FCSTD DOCUMENT  (FreeCAD 0.22R37100 (Git))
Label: composit_stand11
License: All rights reserved
LicenseURL: http://en.wikipedia.org/wiki/All_rights_reserved
objects: Part::FeaturePython×178, Sketcher::SketchObject×145, PartDesign::SubShapeBinder×39, Part::Mirroring×36, Part::Compound×36, PartDesign::FeaturePython×35, PartDesign::CoordinateSystem×35, Part::Extrusion×31, TechDraw::DrawViewDimension×31, PartDesign::Body×29, PartDesign::Boolean×29, PartDesign::Pocket×27, PartDesign::Pad×25, TechDraw::DrawViewPart×22, App::DocumentObjectGroup×12, PartDesign::Mirrored×11, TechDraw::DrawPage×9, TechDraw::DrawViewBalloon×8, PartDesign::Plane×7, Part::Feature×7, +13 more types
note: 794 computed .brp shape members not serialized (recipe doc carries the construction recipe); baked Part::Feature solids carry a one-line shape summary decoded from their .brp
EXTERNAL_REF file=../module.FCStd obj=Sketch
EXTERNAL_REF file=../module.FCStd obj=Spreadsheet
EXTERNAL_REF file=../module.FCStd obj=Body
EXTERNAL_REF file=../dropper.FCStd obj=Connect
EXTERNAL_REF file=../dropper.FCStd obj=Sketch008
EXTERNAL_REF file=../dropper.FCStd obj=Sketch007
EXTERNAL_REF file=../ULZ-P02-14W.FCStd obj=Sketch
EXTERNAL_REF file=../hinge.FCStd obj=Sketch

FEATURE [PartDesign::SubShapeBinder] Binder
  BindCopyOnChange = 0
  BindMode = 0
  ClaimChildren = true
  Context = -> Body [Binder.]
  Fuse = false
  MakeFace = true
  OffsetFill = false
  OffsetIntersection = false
  OffsetJoinType = 0
  OffsetOpenResult = false
  PartialLoad = false
  Relative = false
  Support = -> [Connect]
  _Version = 2
FEATURE [PartDesign::FeaturePython] BaseBend  # WARN: FeaturePython — macro-defined, semantics opaque (R4)
  BendSide = 1
  BendSketch = -> Binder
  MidPlane = false
  Reverse = false
  Suppressed = false
  length = 1100
  radius = 0.1
  thickness = 0.3
  expr: length = <<Properties>>.modules_fix_height
FEATURE [App::Link] Link  label="module_holes"
  LinkedObject = -> <external ../module.FCStd>#Sketch
  expr: LinkedObject = module#<<module_holes>>._self
FEATURE [Part::FeaturePython] LinearArray  # WARN: FeaturePython — macro-defined, semantics opaque (R4)
  Alignment = 0
  CellStart = A1
  Count = 11
  Dir = (0,0,1)
  DirIsDriven = true
  DistributionLaw = 0
  DrivenProperty = 1
  EndInclusive = true
  ExposePlacement = false
  GeneratorMode = 1
  MarkerShape = 1
  MarkerSize = 0
  NumElements = 11
  OrientMode = 0
  Point = (0,0,0)
  PointIsDriven = true
  Reverse = false
  SpanEnd = 800
  SpanStart = 0
  Step = 80
  Type = lattice2LinearArray.LinearArray
  VSGVersion = 1
  Values = 0.0 | 80.0 | 160.0 | 240.0 | 320.0 | 400.0 | 480.0 | 560.0 | 640.0 | 720.0 | 800.0
  ValuesSource = 2
  isLattice = 1
  expr: Count = <<Properties>>.number_of_modules
  expr: SpanEnd = Step * (Count - 1)
FEATURE [Sketcher::SketchObject] Sketch003  label="modules_plasements"
  FullyConstrained = true
  expr: Constraints[27] = <<module>>#<<Properties>>.module_width + 2 mm
  sketch-geometry (12):
    g0: LineSegment StartX=1 StartY=0 StartZ=0 EndX=151 EndY=0 EndZ=0
    g1: LineSegment StartX=151 StartY=0 StartZ=0 EndX=151 EndY=36 EndZ=0
    g2: LineSegment StartX=151 StartY=36 StartZ=0 EndX=1 EndY=36 EndZ=0
    g3: LineSegment StartX=1 StartY=36 StartZ=0 EndX=1 EndY=0 EndZ=0
    g4: LineSegment StartX=175.08 StartY=8.76442 StartZ=0 EndX=289.987 EndY=105.183 EndZ=0
    g5: LineSegment StartX=289.987 StartY=105.183 StartZ=0 EndX=266.846 EndY=132.76 EndZ=0
    g6: LineSegment StartX=266.846 StartY=132.76 StartZ=0 EndX=151.94 EndY=36.342 EndZ=0
    g7: LineSegment StartX=151.94 StartY=36.342 StartZ=0 EndX=175.08 EndY=8.76442 EndZ=0
    g8: LineSegment StartX=151 StartY=36 StartZ=0 EndX=151.532 EndY=36 EndZ=0
    g9: LineSegment StartX=151.532 StartY=36 StartZ=0 EndX=151.94 EndY=36.342 EndZ=0
    g10: LineSegment StartX=151 StartY=0 StartZ=0 EndX=164.635 EndY=0 EndZ=0
    g11: LineSegment StartX=164.635 StartY=0 StartZ=0 EndX=175.08 EndY=8.76442 EndZ=0
  constraints (34):
    c: Coincident(g0,g1)
    c: Coincident(g1,g2)
    c: Coincident(g2,g3)
    c: Coincident(g3,g0)
    c: Horizontal(g0)
    c: Horizontal(g2)
    c: Vertical(g1)
    c: Vertical(g3)
    c: Coincident(g4,g5)
    c: Coincident(g5,g6)
    c: Coincident(g6,g7)
    c: Coincident(g7,g4)
    c: Parallel(g4,g6)
    c: Parallel(g5,g7)
    c: Perpendicular(g5,g4)
    c: Equal(g7,g1)
    c: Equal(g2,g6)
    c: Coincident(g1,g8)
    c: Coincident(g8,g9)
    c: Coincident(g9,g6)
    c: Coincident(g0,g10)
    c: Coincident(g10,g11)
    c: Coincident(g11,g4)
    c: Parallel(g9,g6)
    c: Equal(g9,g8)
    c: DistanceY(g3,g3) = 36
    c: Parallel(g11,g9)
    c: DistanceX(g2,g2) = 150
    c: DistanceX(g0) = 1
    c: Distance(g1,g6) = 1
    c: Angle(g4) = 0.698132
    c: Parallel(g10,g0)
    c: DistanceY(g0) = 0
    c: Horizontal(g8)
FEATURE [Sketcher::SketchObject] Sketch  label="base_Sketch"
  ExternalGeometry = -> [Sketch003]
  FullyConstrained = true
  Placement = pos=(0,20,0) rot=(0,0,1;0rad)
  expr: .Constraints.offset = .Placement.Base.y
  sketch-geometry (6):
    g0: LineSegment StartX=0 StartY=1.6e-15 StartZ=0 EndX=164.635 EndY=1.6e-15 EndZ=0
    g1: LineSegment StartX=164.635 StartY=1.6e-15 StartZ=0 EndX=319.563 EndY=130 EndZ=0
    g2: LineSegment StartX=151 StartY=-20 StartZ=0 EndX=164.635 EndY=-20 EndZ=0
    g3: LineSegment StartX=164.635 StartY=-20 StartZ=0 EndX=175.08 EndY=-11.2356 EndZ=0
    g4: GeomPoint X=157.818 Y=-20 Z=0
    g5: GeomPoint X=-164.635 Y=1.6e-15 Z=0
  constraints (19):
    c: Coincident(g0,g1)
    c: Horizontal(g0)
    c: Parallel(g1,g-3)
    c: Coincident(g-4,g2)
    c: Horizontal(g2)
    c: Coincident(g2,g3)
    c: Coincident(g3,g-3)
    c: Parallel(g3,g-3)
    c: Vertical(g2,g0)
    c: PointOnObject(g0,g-2)
    c: DistanceY(g-4,g0) = 20  'offset'
    c: Angle(g1) = 0.698132  'angle'
    c: Symmetric(g2,g2,g4)
    c: DistanceX(g4) = 157.818  'rivet_placement'
    c: Distance(g1) = 202.244  'side'
    c: Symmetric(g5,g0,g-2)
    c: Distance(g5,g0) = 329.27  'face'
    c: DistanceY(g-4,g1) = 150  'total_depth'
    c: DistanceY(g0,g1) = 130
FEATURE [Sketcher::SketchObject] Sketch001  label="side_Sketch"
  ExternalGeometry = -> [Sketch]
  FullyConstrained = true
  sketch-geometry (2):
    g0: LineSegment StartX=319.563 StartY=150 StartZ=0 EndX=319.563 EndY=150 EndZ=0
    g1: LineSegment StartX=319.563 StartY=150 StartZ=0 EndX=319.563 EndY=0 EndZ=0
  constraints (8):
    c: Coincident(g0,g-3)
    c: Horizontal(g0)
    c: Coincident(g1,g0)
    c: PointOnObject(g1,g-1)
    c: Vertical(g1)
    c: Distance(g1) = 150  'side'
    c: DistanceX(g0,g0) = 0  'front'
    c: DistanceX(g1) = 319.563  'distance'
FEATURE [Part::Mirroring] Part__Mirroring  label="base_Sketch (Mirror #1)"
  Base = (0,0,0)
  Normal = (1,0,0)
  Source = -> Sketch
FEATURE [Sketcher::SketchObject] Sketch002  label="mid_Sketch"
  ExternalGeometry = -> [Sketch]
  FullyConstrained = true
  sketch-geometry (2):
    g0: GeomPoint X=319.563 Y=150 Z=0
    g1: LineSegment StartX=2.71984e-11 StartY=0 StartZ=0 EndX=4.40357e-11 EndY=0 EndZ=0
  constraints (5):
    c: DistanceX(g0) = 319.563  'middle'
    c: Coincident(g1,g-1)
    c: PointOnObject(g1,g-1)
    c: DistanceX(g1,g1) = 0  'length'
    c: Coincident(g0,g-3)
FEATURE [Part::Compound] Compound
  Links = -> [Sketch001,Part__Mirroring,Sketch002,Sketch]
  Placement = pos=(319.563,0,0) rot=(0,0,1;0rad)
  expr: .Placement.Base.x = <<mid_Sketch>>.Constraints.middle
FEATURE [Part::Mirroring] Part__Mirroring001  label="Compound (Mirror #2)"
  Base = (0,0,0)
  Normal = (1,0,0)
  Source = -> Compound
  expr: Normal = <<base_Sketch (Mirror #1)>>.Normal
FEATURE [Part::FeaturePython] Connect  label="face_bend_base"  # WARN: FeaturePython — macro-defined, semantics opaque (R4)
  Objects = -> [Part__Mirroring001,Compound]
  Tolerance = 0
FEATURE [Sketcher::SketchObject] Sketch004
  ExternalGeometry = -> [Sketch003]
  FullyConstrained = false
  sketch-geometry (8):
    g0: LineSegment StartX=70.3141 StartY=-1e-16 StartZ=0 EndX=76 EndY=-1e-16 EndZ=0
    g1: LineSegment StartX=76 StartY=-1e-16 StartZ=0 EndX=76 EndY=53.1648 EndZ=0
    g2: LineSegment StartX=228.178 StartY=53.3186 StartZ=0 EndX=232.533 EndY=56.9735 EndZ=0
    g3: LineSegment StartX=232.533 StartY=56.9735 StartZ=0 EndX=198.36 EndY=97.7001 EndZ=0
    g4: LineSegment StartX=-236.889 StartY=60.6283 StartZ=0 EndX=-232.533 EndY=56.9735 EndZ=0
    g5: LineSegment StartX=-232.533 StartY=56.9735 StartZ=0 EndX=-198.36 EndY=97.7001 EndZ=0
    g6: LineSegment StartX=-81.6859 StartY=-1.2725e-12 StartZ=0 EndX=-76 EndY=-1.2724e-12 EndZ=0
    g7: LineSegment StartX=-76 StartY=-1.2724e-12 StartZ=0 EndX=-76 EndY=53.1648 EndZ=0
  constraints (21):
    c: Coincident(g0,g1)
    c: Vertical(g1)
    c: Coincident(g2,g3)
    c: Coincident(g4,g5)
    c: Coincident(g6,g7)
    c: Vertical(g7)
    c: Perpendicular(g5,g4)
    c: Perpendicular(g3,g2)
    c: Symmetric(g4,g2,g-2)
    c: Equal(g0,g2)
    c: Equal(g2,g6)
    c: Equal(g6,g4)
    c: Equal(g1,g3)
    c: Equal(g3,g7)
    c: Symmetric(g5,g3,g-2)
    c: Symmetric(g6,g0,g-2)
    c: Parallel(g2,g-4)
    c: Horizontal(g0)
    c: Symmetric(g-3,g-3,g0)
    c: Symmetric(g-4,g-4,g2)
    c: Perpendicular(g7,g6)
FEATURE [Part::FeaturePython] Placment  # WARN: FeaturePython — macro-defined, semantics opaque (R4)
  AttacherType = Attacher::AttachEngine3D
  ExposePlacement = true
  MapMode = 49
  MarkerShape = 1
  MarkerSize = 50
  NumElements = 1
  Placement = pos=(76,0,0) rot=(0,0,1;0rad)
  Type = lattice2AttachablePlacement.AttachablePlacement
  isLattice = 1
FEATURE [Part::FeaturePython] PlacementSubsequence  # WARN: FeaturePython — macro-defined, semantics opaque (R4)
  Base = -> Placment
  CycleMode = 0
  ExposePlacement = false
  MarkerShape = 1
  MarkerSize = 0
  NumElements = 4
  Type = lattice2AttachablePlacement.AttachedPlacementSubsequence
  isLattice = 1
FEATURE [Part::FeaturePython] LinearArray001  label="sections_LinearArray"  # WARN: FeaturePython — macro-defined, semantics opaque (R4)
  Alignment = 0
  CellStart = A1
  Count = 5
  Dir = (1,0,0)
  DirIsDriven = true
  DistributionLaw = 0
  DrivenProperty = 1
  EndInclusive = true
  ExposePlacement = false
  GeneratorMode = 0
  MarkerShape = 1
  MarkerSize = 0
  NumElements = 2
  OrientMode = 1
  Point = (0,0,0)
  PointIsDriven = true
  Reverse = false
  SpanEnd = 500
  SpanStart = 0
  Step = 125
  Type = lattice2LinearArray.LinearArray
  VSGVersion = 1
  Values = -319.562984 | 319.562984
  ValuesSource = 0
  isLattice = 1
  expr: Values = list(<<%f>> % (-<<mid_Sketch>>.Constraints.middle / 1 mm); <<%f>> % (<<mid_Sketch>>.Constraints.middle / 1 mm))
FEATURE [Part::FeaturePython] Populate  label="Populate LinearArray001 with PlacementSubsequence"  # WARN: FeaturePython — macro-defined, semantics opaque (R4)
  Copying = 0
  ExposePlacement = false
  MarkerShape = 1
  MarkerSize = 0
  NumElements = 8
  Object = -> PlacementSubsequence
  OutputCompounding = 0
  Placement = pos=(0,20,0) rot=(0,0,1;0rad)
  PlacementsTo = -> LinearArray001
  Referencing = 0
  Type = lattice2PopulateCopies.LatticePopulateCopies
  isLattice = 1
  expr: .Placement.Base.y = <<base_Sketch>>.Constraints.offset
FEATURE [Part::FeaturePython] Populate001  label="Populate LinearArray with Populate LinearArray001 with PlacementSubsequence"  # WARN: FeaturePython — macro-defined, semantics opaque (R4)
  Copying = 0
  ExposePlacement = false
  MarkerShape = 1
  MarkerSize = 0
  NumElements = 88
  Object = -> Populate
  OutputCompounding = 0
  PlacementsTo = -> LinearArray
  Referencing = 0
  Type = lattice2PopulateCopies.LatticePopulateCopies
  isLattice = 1
FEATURE [Part::FeaturePython] Placment001  label="Custom"  # WARN: FeaturePython — macro-defined, semantics opaque (R4)
  ExposePlacement = true
  FlipZ = false
  Invert = false
  MarkerShape = 1
  MarkerSize = 20
  NumElements = 1
  Placement = pos=(0,0,0) rot=(0,0.707107,0.707107;3.14159rad)
  PlacementChoice = 0
  Type = lattice2Placement.LatticePlacement
  isLattice = 1
FEATURE [Part::FeaturePython] Populate002  label="Populate Populate LinearArray with Populate LinearArray001 with PlacementSubsequence with Custom"  # WARN: FeaturePython — macro-defined, semantics opaque (R4)
  Copying = 0
  ExposePlacement = false
  MarkerShape = 1
  MarkerSize = 0
  NumElements = 88
  Object = -> Placment001
  OutputCompounding = 0
  Placement = pos=(0,0,280) rot=(0,0,1;0rad)
  PlacementsTo = -> Populate001
  Referencing = 0
  Type = lattice2PopulateCopies.LatticePopulateCopies
  isLattice = 1
  expr: .Placement.Base.z = <<Properties>>.bottom_cut_height + <<Properties>>.sink_height + module#<<Properties>>.module_height
FEATURE [App::Link] Link001  label="module_Body"
  LinkedObject = -> <external ../module.FCStd>#Body
  expr: LinkedObject = module#<<module_Body>>._self
FEATURE [Part::Extrusion] Extrude
  Base = -> Link
  Dir = (0,0,1)
  DirMode = 2
  FaceMakerClass = Part::FaceMakerBullseye
  LengthFwd = 10
  LengthRev = 0
  Reversed = true
  Solid = true
  Symmetric = false
FEATURE [Part::FeaturePython] Populate004  label="face_modules_fix"  # WARN: FeaturePython — macro-defined, semantics opaque (R4)
  Copying = 0
  ExposePlacement = false
  MarkerShape = 1
  MarkerSize = 0
  NumElements = 0
  Object = -> Extrude
  OutputCompounding = 1
  PlacementsTo = -> Populate002
  Referencing = 0
  Type = lattice2PopulateCopies.LatticePopulateCopies
  isLattice = 0
FEATURE [PartDesign::Body] Body001  label="dummy_body"
  Origin = -> Origin001
FEATURE [Spreadsheet::Sheet] Spreadsheet  label="Properties"
  cells = B2(modules_fix_height)==modules_height + modules_to_droppers + bottom_cut_height + sink_height; C2(total_height)==modules_fix_height + cap_height; D2(number_of_modules)=11; E2(modules_height)==module#<<Properties>>.module_fixture_distance_y * (number_of_modules - 1) + module#<<Properties>>.module_height; F2(modules_to_droppers)==20 mm; G2(bottom_cut_height)==100 mm; H2(sink_height)==20 mm; I2(cap_height)==40 mm
FEATURE [PartDesign::SubShapeBinder] Binder001
  BindCopyOnChange = 0
  BindMode = 0
  ClaimChildren = true
  Context = -> Body003 [Binder001.]
  Fuse = false
  MakeFace = true
  OffsetFill = false
  OffsetIntersection = false
  OffsetJoinType = 0
  OffsetOpenResult = false
  PartialLoad = false
  Relative = false
  Support = -> [Sketch]
  _Version = 2
FEATURE [PartDesign::CoordinateSystem] Local_CS
  AttacherType = Attacher::AttachEngine3D
  AttachmentOffset = pos=(0,0,0) rot=(0,1,0;1.5708rad)
  MapMode = 7
  Placement = pos=(164.635,-1.4e-14,0) rot=(0.889126,0.323616,0.323616;1.68804rad)
FEATURE [Sketcher::SketchObject] Sketch005  label="sink_side_line"
  ExternalGeometry = -> [Binder001]
  FullyConstrained = true
  MapMode = 5
  Placement = pos=(164.635,-2.8e-14,0) rot=(0.889126,0.323616,0.323616;1.68804rad)
  sketch-geometry (1):
    g0: LineSegment StartX=-2.84e-14 StartY=0 StartZ=0 EndX=202.244 EndY=20 EndZ=0
  constraints (4):
    c: Coincident(g0,g-3)
    c: Vertical(g0,g-3)
    c: DistanceY(g0) = 20  'height'
    c: Angle(g0) = 0.0985699  'angle'
FEATURE [Sketcher::SketchObject] Sketch006  label="sink_front_bend_sketch"
  ExternalGeometry = -> [Sketch005]
  FullyConstrained = true
  MapMode = 5
  Placement = pos=(0,0,0) rot=(0.57735,0.57735,0.57735;2.0944rad)
  sketch-geometry (3):
    g0: LineSegment StartX=0 StartY=2.91403 StartZ=0 EndX=-1.83e-14 EndY=0 EndZ=0
    g1: LineSegment StartX=-1.83e-14 StartY=0 StartZ=0 EndX=2.88014 EndY=0.443099 EndZ=0
    g2: ArcOfCircle CenterX=2.5 CenterY=2.91403 CenterZ=0 NormalX=0 NormalY=0 NormalZ=1 AngleXU=0 Radius=2.5 StartAngle=3.14159 EndAngle=4.86504
  constraints (8):
    c: PointOnObject(g0,g-2)
    c: Coincident(g0,g-3)
    c: Coincident(g0,g1)
    c: PointOnObject(g1,g-3)
    c: Tangent(g2,g1) = -1.5708
    c: Tangent(g2,g0) = -1.5708
    c: Radius(g2) = 2.5
    c: Angle(g1) = 0.152649  'angle'
FEATURE [Sketcher::SketchObject] Sketch007
  ExternalGeometry = -> [Binder001]
  FullyConstrained = true
  MapMode = 7
  Placement = pos=(164.635,-8.5e-14,-4e-15) rot=(0.846388,-0.394677,-0.357572;1.83324rad)
  sketch-geometry (3):
    g0: ArcOfCircle CenterX=-2.5 CenterY=2.81034 CenterZ=0 NormalX=0 NormalY=0 NormalZ=1 AngleXU=0 Radius=2.5 StartAngle=4.59564 EndAngle=6.28319
    g1: LineSegment StartX=-2.79121 StartY=0.327355 StartZ=0 EndX=0 EndY=0 EndZ=0
    g2: LineSegment StartX=0 StartY=0 StartZ=0 EndX=0 EndY=2.81034 EndZ=0
  constraints (7):
    c: PointOnObject(g0,g-2)
    c: Coincident(g1,g-1)
    c: Coincident(g2,g1)
    c: Tangent(g2,g0) = -1.5708
    c: Tangent(g1,g0) = -1.5708
    c: PointOnObject(g0,g-3)
    c: Radius(g0) = 2.5
FEATURE [PartDesign::CoordinateSystem] Local_CS001
  AttacherType = Attacher::AttachEngine3D
  AttachmentOffset = pos=(0,0,0) rot=(1,0,0;0.152649rad)
  MapMode = 5
  Placement = pos=(0,0,0) rot=(1,0,0;0.152649rad)
  expr: .AttachmentOffset.Rotation.Angle = <<sink_front_bend_sketch>>.Constraints.angle
FEATURE [Sketcher::SketchObject] Sketch008  label="sink_plane_sketch"
  ExternalGeometry = -> [Sketch006,Sketch005,Sketch007]
  FullyConstrained = true
  MapMode = 5
  Placement = pos=(0,0,0) rot=(1,0,0;0.152649rad)
  sketch-geometry (4):
    g0: LineSegment StartX=-163.725 StartY=2.91403 StartZ=0 EndX=163.725 EndY=2.91403 EndZ=0
    g1: LineSegment StartX=163.725 StartY=2.91403 StartZ=0 EndX=317.576 EndY=133.529 EndZ=0
    g2: LineSegment StartX=317.576 StartY=133.529 StartZ=0 EndX=-317.576 EndY=133.529 EndZ=0
    g3: LineSegment StartX=-317.576 StartY=133.529 StartZ=0 EndX=-163.725 EndY=2.91403 EndZ=0
  constraints (14):
    c: Coincident(g0,g1)
    c: Coincident(g1,g2)
    c: Coincident(g2,g3)
    c: Coincident(g3,g0)
    c: Symmetric(g0,g0,g-2)
    c: Symmetric(g2,g1,g-2)
    c: Parallel(g1,g-4)
    c: PointOnObject(g-5,g1)
    c: PointOnObject(g-3,g0)
    c: Distance(g1) = 201.818  'rigth_side'
    c: Distance(g0) = 327.45  'front'
    c: Distance(g2) = 635.153  'end'
    c: Distance(g3) = 201.818  'left_side'
    c: DistanceY(g-4,g1) = 2
FEATURE [Sketcher::SketchObject] Sketch009
  ExternalGeometry = -> [Sketch006]
  FullyConstrained = true
  MapMode = 2
  Placement = pos=(0,0,0) rot=(0.57735,0.57735,0.57735;2.0944rad)
  sketch-geometry (4):
    g0: ArcOfCircle CenterX=2.5 CenterY=2.91403 CenterZ=0 NormalX=0 NormalY=0 NormalZ=1 AngleXU=0 Radius=2.5 StartAngle=3.14159 EndAngle=4.86504
    g1: LineSegment StartX=2.88014 StartY=0.443099 StartZ=0 EndX=2.80411 EndY=0.937285 EndZ=0
    g2: LineSegment StartX=1.1302e-12 StartY=2.91403 StartZ=0 EndX=0.5 EndY=2.91403 EndZ=0
    g3: ArcOfCircle CenterX=2.5 CenterY=2.91403 CenterZ=0 NormalX=0 NormalY=0 NormalZ=1 AngleXU=0 Radius=2 StartAngle=3.14159 EndAngle=4.86504
  constraints (10):
    c: Coincident(g0,g-3)
    c: Tangent(g0,g-3) = -1.5708
    c: Coincident(g0,g1)
    c: Coincident(g0,g2)
    c: Coincident(g3,g0)
    c: Coincident(g3,g2)
    c: Coincident(g3,g1)
    c: Perpendicular(g3,g1)
    c: Perpendicular(g3,g2)
    c: Distance(g1) = 0.5
FEATURE [Sketcher::SketchObject] Sketch010
  ExternalGeometry = -> [Sketch007]
  FullyConstrained = true
  MapMode = 7
  Placement = pos=(163.725,2.88014,0.443099) rot=(0.846388,-0.394677,-0.357572;1.83324rad)
  sketch-geometry (4):
    g0: ArcOfCircle CenterX=0.291206 CenterY=2.48298 CenterZ=0 NormalX=0 NormalY=0 NormalZ=1 AngleXU=0 Radius=2.5 StartAngle=4.59564 EndAngle=6.28319
    g1: LineSegment StartX=-2.56e-14 StartY=2.7e-15 StartZ=0 EndX=0.0582413 EndY=0.496596 EndZ=0
    g2: LineSegment StartX=2.79121 StartY=2.48298 StartZ=0 EndX=2.29121 EndY=2.48298 EndZ=0
    g3: ArcOfCircle CenterX=0.291206 CenterY=2.48298 CenterZ=0 NormalX=0 NormalY=0 NormalZ=1 AngleXU=0 Radius=2 StartAngle=4.59564 EndAngle=6.28319
  constraints (10):
    c: Coincident(g0,g-3)
    c: Tangent(g0,g-3) = -1.5708
    c: Coincident(g1,g0)
    c: Coincident(g2,g0)
    c: Coincident(g3,g0)
    c: Coincident(g3,g1)
    c: Coincident(g3,g2)
    c: Perpendicular(g0,g1)
    c: Perpendicular(g0,g2)
    c: Distance(g1) = 0.5
FEATURE [Sketcher::SketchObject] Sketch011
  ExternalGeometry = -> [Sketch008]
  FullyConstrained = true
  MapMode = 7
  Placement = pos=(-163.725,2.88014,0.443099) rot=(-0.298783,0.640743,0.707232;3.7787rad)
  sketch-geometry (4):
    g0: ArcOfCircle CenterX=0.291206 CenterY=2.48298 CenterZ=0 NormalX=0 NormalY=0 NormalZ=1 AngleXU=0 Radius=2 StartAngle=4.59564 EndAngle=6.28319
    g1: ArcOfCircle CenterX=0.291206 CenterY=2.48298 CenterZ=0 NormalX=0 NormalY=0 NormalZ=1 AngleXU=0 Radius=2.5 StartAngle=4.59564 EndAngle=6.28319
    g2: LineSegment StartX=-4e-16 StartY=0 StartZ=0 EndX=0.0582413 EndY=0.496596 EndZ=0
    g3: LineSegment StartX=2.29121 StartY=2.48298 StartZ=0 EndX=2.79121 EndY=2.48298 EndZ=0
  constraints (12):
    c: Coincident(g1,g0)
    c: Coincident(g1,g-1)
    c: Coincident(g2,g1)
    c: Coincident(g2,g0)
    c: Coincident(g3,g0)
    c: Coincident(g3,g1)
    c: Perpendicular(g0,g3)
    c: Perpendicular(g0,g2)
    c: Perpendicular(g2,g-3)
    c: Horizontal(g3)
    c: Radius(g0) = 2
    c: Distance(g2) = 0.5
FEATURE [PartDesign::Pad] Pad
  Direction = (0,-0.152057,0.988372)
  Length = 0.5
  Length2 = 10
  Placement = pos=(0,0,0) rot=(1,0,0;0.152649rad)
  Profile = -> Sketch008
  ReferenceAxis = -> Sketch008 [N_Axis]
  Suppressed = false
  Type = 0
FEATURE [PartDesign::Pad] Pad001
  BaseFeature = -> Pad
  Direction = (-0.762326,-0.639667,-0.0984104)
  Length = 201.818
  Length2 = 10
  Placement = pos=(0,0,0) rot=(1,0,0;0.152649rad)
  Profile = -> Sketch010
  ReferenceAxis = -> Sketch010 [N_Axis]
  Reversed = true
  Suppressed = false
  Type = 0
  expr: Length = <<sink_plane_sketch>>.Constraints.rigth_side
FEATURE [PartDesign::Pad] Pad002
  BaseFeature = -> Pad001
  Direction = (-0.762326,0.639667,0.0984104)
  Length = 201.818
  Length2 = 10
  Placement = pos=(0,0,0) rot=(1,0,0;0.152649rad)
  Profile = -> Sketch011
  ReferenceAxis = -> Sketch011 [N_Axis]
  Suppressed = false
  Type = 0
  expr: Length = <<sink_plane_sketch>>.Constraints.left_side
FEATURE [PartDesign::Pad] Pad003
  BaseFeature = -> Pad002
  Direction = (1,0,0)
  Length = 327.45
  Length2 = 10
  Midplane = true
  Placement = pos=(0,0,0) rot=(1,0,0;0.152649rad)
  Profile = -> Sketch009
  ReferenceAxis = -> Sketch009 [N_Axis]
  Suppressed = false
  Type = 0
  expr: Length = <<sink_plane_sketch>>.Constraints.front
FEATURE [Sketcher::SketchObject] Sketch013
  ExternalGeometry = -> [Sketch008,Sketch009]
  FullyConstrained = true
  MapMode = 5
  Placement = pos=(0,0,0) rot=(1,0,0;1.5708rad)
  sketch-geometry (6):
    g0: LineSegment StartX=-163.725 StartY=2.91403 StartZ=0 EndX=-163.725 EndY=80 EndZ=0
    g1: LineSegment StartX=-163.725 StartY=80 StartZ=0 EndX=163.725 EndY=80 EndZ=0
    g2: LineSegment StartX=163.725 StartY=80 StartZ=0 EndX=163.725 EndY=2.91403 EndZ=0
    g3: LineSegment StartX=163.725 StartY=2.91403 StartZ=0 EndX=-163.725 EndY=2.91403 EndZ=0
    g4: LineSegment StartX=-163.725 StartY=0.443099 StartZ=0 EndX=-163.725 EndY=2.91403 EndZ=0
    g5: LineSegment StartX=163.725 StartY=0.443099 StartZ=0 EndX=163.725 EndY=2.91403 EndZ=0
  constraints (16):
    c: Vertical(g0)
    c: Coincident(g0,g1)
    c: Horizontal(g1)
    c: Coincident(g1,g2)
    c: Vertical(g2)
    c: Coincident(g2,g3)
    c: Coincident(g3,g0)
    c: Horizontal(g3)
    c: PointOnObject(g-4,g3)
    c: Coincident(g4,g-3)
    c: Coincident(g4,g0)
    c: Perpendicular(g3,g4)
    c: Coincident(g5,g-3)
    c: Coincident(g5,g2)
    c: Perpendicular(g3,g5)
    c: DistanceY(g1) = 80
FEATURE [Sketcher::SketchObject] Sketch012
  ExternalGeometry = -> [Sketch008,Sketch010,Sketch013]
  FullyConstrained = true
  MapMode = 5
  Placement = pos=(164.635,-2.8e-14,0) rot=(0.889126,0.323616,0.323616;1.68804rad)
  sketch-geometry (4):
    g0: LineSegment StartX=0.909926 StartY=2.91403 StartZ=0 EndX=201.749 EndY=22.775 EndZ=0
    g1: LineSegment StartX=0.909926 StartY=2.91403 StartZ=0 EndX=0.909926 EndY=80 EndZ=0
    g2: LineSegment StartX=0.909926 StartY=80 StartZ=0 EndX=201.749 EndY=80 EndZ=0
    g3: LineSegment StartX=201.749 StartY=80 StartZ=0 EndX=201.749 EndY=22.775 EndZ=0
  constraints (11):
    c: Coincident(g0,g-4)
    c: Parallel(g-3,g0)
    c: Equal(g0,g-3)
    c: Coincident(g0,g1)
    c: Vertical(g1)
    c: Coincident(g1,g2)
    c: Horizontal(g2)
    c: Coincident(g2,g3)
    c: Coincident(g3,g0)
    c: Vertical(g3)
    c: Horizontal(g-5,g1)
FEATURE [PartDesign::Pad] Pad004
  BaseFeature = -> Pad003
  Direction = (0,-1,2e-16)
  Length = 0.5
  Length2 = 10
  Placement = pos=(0,0,0) rot=(1,0,0;0.152649rad)
  Profile = -> Sketch013
  ReferenceAxis = -> Sketch013 [N_Axis]
  Reversed = true
  Suppressed = false
  Type = 0
FEATURE [PartDesign::Pad] Pad005
  BaseFeature = -> Pad004
  Direction = (0.642788,-0.766044,0)
  Length = 0.5
  Length2 = 10
  Placement = pos=(0,0,0) rot=(1,0,0;0.152649rad)
  Profile = -> Sketch012
  ReferenceAxis = -> Sketch012 [N_Axis]
  Reversed = true
  Suppressed = false
  Type = 0
FEATURE [Sketcher::SketchObject] Sketch014
  ExternalGeometry = -> [Binder001]
  FullyConstrained = true
  MapMode = 5
  sketch-geometry (1):
    g0: LineSegment StartX=-319.563 StartY=130 StartZ=0 EndX=-164.635 EndY=0 EndZ=0
  constraints (2):
    c: Symmetric(g0,g-3,g-2)
    c: Symmetric(g0,g-3,g-2)
FEATURE [PartDesign::CoordinateSystem] Local_CS003
  AttacherType = Attacher::AttachEngine3D
  AttachmentOffset = pos=(0,0,0) rot=(0,1,0;1.5708rad)
  MapMode = 7
  Placement = pos=(-164.635,-1.4e-14,0) rot=(0.889126,-0.323616,-0.323616;1.68804rad)
FEATURE [Sketcher::SketchObject] Sketch015
  ExternalGeometry = -> [Sketch008,Sketch011,Sketch013]
  FullyConstrained = true
  MapMode = 5
  Placement = pos=(-164.635,-2.8e-14,0) rot=(0.889126,-0.323616,-0.323616;1.68804rad)
  sketch-geometry (5):
    g0: LineSegment StartX=-201.749 StartY=22.775 StartZ=0 EndX=-0.909926 EndY=2.91403 EndZ=0
    g1: LineSegment StartX=-0.909926 StartY=2.91403 StartZ=0 EndX=-0.909926 EndY=80 EndZ=0
    g2: LineSegment StartX=-0.909926 StartY=80 StartZ=0 EndX=-201.749 EndY=80 EndZ=0
    g3: LineSegment StartX=-201.749 StartY=80 StartZ=0 EndX=-201.749 EndY=22.775 EndZ=0
    g4: LineSegment StartX=-201.993 StartY=20.3041 StartZ=0 EndX=-201.749 EndY=22.775 EndZ=0
  constraints (13):
    c: Coincident(g0,g-4)
    c: Coincident(g1,g0)
    c: Vertical(g1)
    c: Coincident(g1,g2)
    c: Horizontal(g2)
    c: Coincident(g2,g3)
    c: Coincident(g3,g0)
    c: Vertical(g3)
    c: Coincident(g4,g-3)
    c: Coincident(g4,g0)
    c: Perpendicular(g-3,g4)
    c: Parallel(g-3,g0)
    c: Horizontal(g1,g-5)
FEATURE [PartDesign::Pad] Pad006
  BaseFeature = -> Pad005
  Direction = (-0.642788,-0.766044,0)
  Length = 0.5
  Length2 = 10
  Placement = pos=(0,0,0) rot=(1,0,0;0.152649rad)
  Profile = -> Sketch015
  ReferenceAxis = -> Sketch015 [N_Axis]
  Reversed = true
  Suppressed = false
  Type = 0
FEATURE [Sketcher::SketchObject] Sketch016
  ExternalGeometry = -> [Pad006]
  FullyConstrained = true
  MapMode = 5
  Placement = pos=(0,0,0) rot=(1,0,0;0.152649rad)
  sketch-geometry (28):
    g0: LineSegment StartX=0 StartY=2 StartZ=0 EndX=40.9313 EndY=2 EndZ=0
    g1: LineSegment StartX=40.9313 StartY=2 StartZ=0 EndX=81.8625 EndY=2 EndZ=0
    g2: LineSegment StartX=81.8625 StartY=2 StartZ=0 EndX=122.794 EndY=2 EndZ=0
    g3: LineSegment StartX=122.794 StartY=2 StartZ=0 EndX=163.725 EndY=2 EndZ=0
    g4: ArcOfCircle CenterX=-17 CenterY=2 CenterZ=0 NormalX=0 NormalY=0 NormalZ=1 AngleXU=0 Radius=3 StartAngle=1.5708 EndAngle=4.71239
    g5: ArcOfCircle CenterX=17 CenterY=2 CenterZ=0 NormalX=0 NormalY=0 NormalZ=1 AngleXU=0 Radius=3 StartAngle=4.71239 EndAngle=7.85398
    g6: LineSegment StartX=-17 StartY=5 StartZ=0 EndX=17 EndY=5 EndZ=0
    g7: LineSegment StartX=-17 StartY=-1 StartZ=0 EndX=17 EndY=-1 EndZ=0
    g8: GeomPoint X=-20 Y=2 Z=0
    g9: GeomPoint X=20 Y=2 Z=0
    g10: ArcOfCircle CenterX=106 CenterY=2 CenterZ=0 NormalX=0 NormalY=0 NormalZ=1 AngleXU=0 Radius=3 StartAngle=1.5708 EndAngle=4.71239
    g11: ArcOfCircle CenterX=140 CenterY=2 CenterZ=0 NormalX=0 NormalY=0 NormalZ=1 AngleXU=0 Radius=3 StartAngle=4.71239 EndAngle=7.85398
    g12: LineSegment StartX=106 StartY=5 StartZ=0 EndX=140 EndY=5 EndZ=0
    g13: LineSegment StartX=106 StartY=-1 StartZ=0 EndX=140 EndY=-1 EndZ=0
    g14: ArcOfCircle CenterX=-140 CenterY=2 CenterZ=0 NormalX=0 NormalY=0 NormalZ=1 AngleXU=0 Radius=3 StartAngle=1.5708 EndAngle=4.71239
    g15: ArcOfCircle CenterX=-106 CenterY=2 CenterZ=0 NormalX=0 NormalY=0 NormalZ=1 AngleXU=0 Radius=3 StartAngle=4.71239 EndAngle=7.85398
    g16: LineSegment StartX=-140 StartY=5 StartZ=0 EndX=-106 EndY=5 EndZ=0
    g17: LineSegment StartX=-140 StartY=-1 StartZ=0 EndX=-106 EndY=-1 EndZ=0
    g18: ArcOfCircle CenterX=-78.5 CenterY=2 CenterZ=0 NormalX=0 NormalY=0 NormalZ=1 AngleXU=0 Radius=3 StartAngle=1.5708 EndAngle=4.71239
    g19: ArcOfCircle CenterX=-44.5 CenterY=2 CenterZ=0 NormalX=0 NormalY=0 NormalZ=1 AngleXU=0 Radius=3 StartAngle=4.71239 EndAngle=7.85398
    g20: LineSegment StartX=-78.5 StartY=5 StartZ=0 EndX=-44.5 EndY=5 EndZ=0
    g21: LineSegment StartX=-78.5 StartY=-1 StartZ=0 EndX=-44.5 EndY=-1 EndZ=0
    g22: ArcOfCircle CenterX=44.5 CenterY=2 CenterZ=0 NormalX=0 NormalY=0 NormalZ=1 AngleXU=0 Radius=3 StartAngle=1.5708 EndAngle=4.71239
    g23: ArcOfCircle CenterX=78.5 CenterY=2 CenterZ=0 NormalX=0 NormalY=0 NormalZ=1 AngleXU=0 Radius=3 StartAngle=4.71239 EndAngle=7.85398
    g24: LineSegment StartX=44.5 StartY=5 StartZ=0 EndX=78.5 EndY=5 EndZ=0
    g25: LineSegment StartX=44.5 StartY=-1 StartZ=0 EndX=78.5 EndY=-1 EndZ=0
    g26: LineSegment StartX=17 StartY=-1 StartZ=0 EndX=44.5 EndY=-1 EndZ=0
    g27: LineSegment StartX=78.5 StartY=-1 StartZ=0 EndX=106 EndY=-1 EndZ=0
  constraints (67):
    c: PointOnObject(g0,g-2)
    c: Coincident(g0,g1)
    c: Horizontal(g1)
    c: Coincident(g1,g2)
    c: Coincident(g2,g3)
    c: Horizontal(g3)
    c: Vertical(g-3,g3)
    c: Horizontal(g0)
    c: Equal(g0,g1)
    c: Equal(g1,g2)
    c: Equal(g2,g3)
    c: DistanceY(g0) = 2
    c: Horizontal(g2)
    c: Tangent(g4,g6) = 1.5708
    c: Tangent(g4,g7) = -1.5708
    c: Tangent(g5,g6) = 1.5708
    c: Tangent(g5,g7) = -1.5708
    c: Equal(g4,g5)
    c: PointOnObject(g5,g0)
    c: Symmetric(g4,g5,g-2)
    c: Radius(g5) = 3
    c: PointOnObject(g8,g4)
    c: PointOnObject(g9,g5)
    c: Horizontal(g9,g8)
    c: Horizontal(g8,g0)
    c: DistanceX(g8,g9) = 40
    c: Tangent(g10,g12) = 1.5708
    c: Tangent(g10,g13) = -1.5708
    c: Tangent(g11,g12) = 1.5708
    c: Tangent(g11,g13) = -1.5708
    c: Equal(g10,g11)
    c: Tangent(g14,g16) = 1.5708
    c: Tangent(g14,g17) = -1.5708
    c: Tangent(g15,g16) = 1.5708
    c: Tangent(g15,g17) = -1.5708
    c: Equal(g14,g15)
    c: Tangent(g18,g20) = 1.5708
    c: Tangent(g18,g21) = -1.5708
    c: Tangent(g19,g20) = 1.5708
    c: Tangent(g19,g21) = -1.5708
    c: Equal(g18,g19)
    c: Tangent(g22,g24) = 1.5708
    c: Tangent(g22,g25) = -1.5708
    c: Tangent(g23,g24) = 1.5708
    c: Tangent(g23,g25) = -1.5708
    c: Equal(g22,g23)
    c: Horizontal(g14,g15)
    c: Horizontal(g18,g19)
    c: Horizontal(g22,g23)
    c: Horizontal(g10,g11)
    c: Equal(g11,g23)
    c: Equal(g23,g5)
    c: Equal(g5,g19)
    c: Equal(g19,g15)
    c: Equal(g16,g20)
    c: Equal(g20,g6)
    c: Equal(g6,g24)
    c: Equal(g12,g24)
    c: Horizontal(g10,g22)
    c: Symmetric(g19,g22,g-2)
    c: Symmetric(g10,g15,g-2)
    c: Tangent(g26,g5) = -1.5708
    c: Coincident(g26,g22)
    c: Coincident(g27,g23)
    c: Coincident(g27,g10)
    c: Equal(g26,g27)
    c: DistanceX(g11) = 140
FEATURE [PartDesign::FeaturePython] SketchOnSheet  # WARN: FeaturePython — macro-defined, semantics opaque (R4)
  BaseFeature = -> Pad006
  Sketch = -> Sketch016
  Suppressed = false
  baseObject = -> Pad006 [Face14]
  kfactor = 0.5
FEATURE [PartDesign::FeaturePython] CornerRelief  # WARN: FeaturePython — macro-defined, semantics opaque (R4)
  BaseFeature = -> SketchOnSheet
  ReliefSketch = 0
  Size = 5
  SizeRatio = 1
  Suppressed = false
  XOffset = 0
  YOffset = 0
  baseObject = -> SketchOnSheet [Edge56,Edge57]
  kfactor = 0.5
FEATURE [PartDesign::FeaturePython] CornerRelief001  # WARN: FeaturePython — macro-defined, semantics opaque (R4)
  BaseFeature = -> CornerRelief
  ReliefSketch = 0
  Size = 5
  SizeRatio = 1
  Suppressed = false
  XOffset = 0
  YOffset = 0
  baseObject = -> CornerRelief [Edge17,Edge14]
  kfactor = 0.5
  expr: Size = <<CornerRelief>>.Size
FEATURE [Sketcher::SketchObject] Sketch017
  ExternalGeometry = -> [Sketch012]
  FullyConstrained = true
  MapMode = 5
  Placement = pos=(164.635,-2.8e-14,0) rot=(0.889126,0.323616,0.323616;1.68804rad)
  sketch-geometry (6):
    g0: LineSegment StartX=0.909926 StartY=78 StartZ=0 EndX=0.909926 EndY=80 EndZ=0
    g1: LineSegment StartX=0.909926 StartY=80 StartZ=0 EndX=2.90993 EndY=80 EndZ=0
    g2: LineSegment StartX=199.749 StartY=80 StartZ=0 EndX=201.749 EndY=80 EndZ=0
    g3: LineSegment StartX=201.749 StartY=80 StartZ=0 EndX=201.749 EndY=78 EndZ=0
    g4: ArcOfCircle CenterX=2.90993 CenterY=78 CenterZ=0 NormalX=0 NormalY=0 NormalZ=1 AngleXU=0 Radius=2 StartAngle=1.5708 EndAngle=3.14159
    g5: ArcOfCircle CenterX=199.749 CenterY=78 CenterZ=0 NormalX=0 NormalY=0 NormalZ=1 AngleXU=0 Radius=2 StartAngle=5.856e-13 EndAngle=1.5708
  constraints (14):
    c: Coincident(g0,g-3)
    c: Vertical(g0)
    c: Coincident(g0,g1)
    c: PointOnObject(g1,g-3)
    c: Coincident(g2,g-3)
    c: Coincident(g2,g3)
    c: Tangent(g5,g3) = 1.5708
    c: Tangent(g5,g2) = 1.5708
    c: Tangent(g4,g1) = 1.5708
    c: Tangent(g4,g0) = 1.5708
    c: Equal(g4,g5)
    c: Radius(g5) = 2
    c: Vertical(g3)
    c: PointOnObject(g2,g-3)
FEATURE [Sketcher::SketchObject] Sketch018
  ExternalGeometry = -> [Sketch015]
  FullyConstrained = true
  MapMode = 2
  Placement = pos=(-164.635,-2.8e-14,0) rot=(0.889126,-0.323616,-0.323616;1.68804rad)
  sketch-geometry (6):
    g0: ArcOfCircle CenterX=-2.90993 CenterY=78 CenterZ=0 NormalX=0 NormalY=0 NormalZ=1 AngleXU=0 Radius=2 StartAngle=6.28318 EndAngle=7.85398
    g1: ArcOfCircle CenterX=-199.749 CenterY=78 CenterZ=0 NormalX=0 NormalY=0 NormalZ=1 AngleXU=0 Radius=2 StartAngle=1.5708 EndAngle=3.14159
    g2: LineSegment StartX=-201.749 StartY=78 StartZ=0 EndX=-201.749 EndY=80 EndZ=0
    g3: LineSegment StartX=-201.749 StartY=80 StartZ=0 EndX=-199.749 EndY=80 EndZ=0
    g4: LineSegment StartX=-2.90993 StartY=80 StartZ=0 EndX=-0.909926 EndY=80 EndZ=0
    g5: LineSegment StartX=-0.909926 StartY=80 StartZ=0 EndX=-0.909926 EndY=78 EndZ=0
  constraints (15):
    c: PointOnObject(g1,g-3)
    c: Coincident(g2,g3)
    c: Vertical(g2)
    c: Tangent(g1,g2) = 1.5708
    c: Tangent(g3,g1) = 1.5708
    c: Coincident(g4,g5)
    c: Coincident(g5,g0)
    c: Tangent(g5,g0)
    c: Tangent(g0,g4) = 1.5708
    c: Coincident(g4,g-3)
    c: Equal(g0,g1)
    c: Radius(g0) = 2
    c: Coincident(g2,g-3)
    c: PointOnObject(g0,g-3)
    c: Vertical(g5)
FEATURE [Sketcher::SketchObject] Sketch019
  ExternalGeometry = -> [Sketch013]
  FullyConstrained = true
  MapMode = 5
  Placement = pos=(0,0,0) rot=(1,0,0;1.5708rad)
  sketch-geometry (6):
    g0: LineSegment StartX=161.725 StartY=80 StartZ=0 EndX=163.725 EndY=80 EndZ=0
    g1: LineSegment StartX=163.725 StartY=80 StartZ=0 EndX=163.725 EndY=78 EndZ=0
    g2: LineSegment StartX=-163.725 StartY=78 StartZ=0 EndX=-163.725 EndY=80 EndZ=0
    g3: LineSegment StartX=-163.725 StartY=80 StartZ=0 EndX=-161.725 EndY=80 EndZ=0
    g4: ArcOfCircle CenterX=-161.725 CenterY=78 CenterZ=0 NormalX=0 NormalY=0 NormalZ=1 AngleXU=0 Radius=2 StartAngle=1.5708 EndAngle=3.14159
    g5: ArcOfCircle CenterX=161.725 CenterY=78 CenterZ=0 NormalX=0 NormalY=0 NormalZ=1 AngleXU=0 Radius=2 StartAngle=5.87e-13 EndAngle=1.5708
  constraints (14):
    c: Coincident(g0,g-3)
    c: Coincident(g0,g1)
    c: Coincident(g2,g-3)
    c: Coincident(g2,g3)
    c: Tangent(g5,g1) = 1.5708
    c: Tangent(g5,g0) = 1.5708
    c: Tangent(g4,g2) = 1.5708
    c: Tangent(g4,g3) = 1.5708
    c: Equal(g5,g4)
    c: Radius(g5) = 2
    c: PointOnObject(g3,g-3)
    c: Vertical(g2)
    c: PointOnObject(g0,g-3)
    c: Vertical(g1)
FEATURE [PartDesign::Pocket] Pocket
  BaseFeature = -> CornerRelief001
  Direction = (-0.642788,0.766044,0)
  Length = 5
  Length2 = 5
  Midplane = true
  Profile = -> Sketch017
  ReferenceAxis = -> Sketch017 [N_Axis]
  Suppressed = false
  Type = 1
FEATURE [PartDesign::Pocket] Pocket001
  BaseFeature = -> Pocket
  Direction = (0.642788,0.766044,-3e-16)
  Length = 5
  Length2 = 5
  Midplane = true
  Profile = -> Sketch018
  ReferenceAxis = -> Sketch018 [N_Axis]
  Suppressed = false
  Type = 0
FEATURE [PartDesign::Pocket] Pocket002
  BaseFeature = -> Pocket001
  Direction = (0,1,-2e-16)
  Length = 5
  Length2 = 5
  Midplane = true
  Profile = -> Sketch019
  ReferenceAxis = -> Sketch019 [N_Axis]
  Suppressed = false
  Type = 1
FEATURE [PartDesign::CoordinateSystem] Local_CS004  label="sink_place"
  AttacherType = Attacher::AttachEngine3D
  MapMode = 5
FEATURE [PartDesign::CoordinateSystem] Local_CS005  label="face_base_placement"
  AttacherType = Attacher::AttachEngine3D
  AttachmentSupport = -> [XY_Plane]
  MapMode = 5
FEATURE [PartDesign::SubShapeBinder] Binder002  label="base_Sketch_link"
  BindCopyOnChange = 0
  BindMode = 0
  ClaimChildren = true
  Fuse = false
  MakeFace = true
  OffsetFill = false
  OffsetIntersection = false
  OffsetJoinType = 0
  OffsetOpenResult = false
  PartialLoad = false
  Relative = false
  Support = -> [Sketch]
  _Version = 2
  expr: Support = <<base_Sketch>>._self
FEATURE [Sketcher::SketchObject] Sketch023  label="face_top_fix_bends"
  ExternalGeometry = -> [Sketch]
  FullyConstrained = true
  expr: .Constraints.length = 0.4 mm
  expr: Constraints[10] = <<side_Sketch>>.Constraints.distance - .Constraints.length
  expr: Constraints[14] = <<base_Sketch>>.Constraints.offset
  expr: Constraints[15] = <<base_Sketch>>.Constraints.offset - .Constraints.length
  expr: Constraints[3] = <<base_Sketch>>.Constraints.angle - 90 deg
  expr: Constraints[4] = <<base_Sketch>>.Constraints.angle - 90 deg
  expr: Constraints[9] = <<side_Sketch>>.Constraints.distance
  sketch-geometry (8):
    g0: LineSegment StartX=319.563 StartY=0.1 StartZ=0 EndX=319.163 EndY=0.1 EndZ=0
    g1: LineSegment StartX=319.563 StartY=148.551 StartZ=0 EndX=319.163 EndY=148.551 EndZ=0
    g2: LineSegment StartX=318.453 StartY=149.068 StartZ=0 EndX=318.71 EndY=148.762 EndZ=0
    g3: LineSegment StartX=166.933 StartY=21.9284 StartZ=0 EndX=167.19 EndY=21.6219 EndZ=0
    g4: LineSegment StartX=161.635 StartY=20 StartZ=0 EndX=161.635 EndY=19.6 EndZ=0
    g5: LineSegment StartX=0 StartY=0 StartZ=0 EndX=0.4 EndY=0 EndZ=0
    g6: LineSegment StartX=318.71 StartY=148.762 StartZ=0 EndX=318.887 EndY=148.551 EndZ=0
    g7: LineSegment StartX=318.887 StartY=148.551 StartZ=0 EndX=319.163 EndY=148.551 EndZ=0
  constraints (28):
    c: Horizontal(g0)
    c: PointOnObject(g2,g-3)
    c: PointOnObject(g3,g-3)
    c: Angle(g3) = -0.872665
    c: Angle(g2) = -0.872665
    c: Equal(g3,g2)
    c: Equal(g2,g1)
    c: Equal(g1,g0)
    c: Vertical(g0,g1)
    c: DistanceX(g0) = 319.563
    c: DistanceX(g0) = 319.163
    c: DistanceY(g0) = 0.1
    c: Vertical(g4)
    c: DistanceX(g4,g-3) = 3
    c: DistanceY(g4) = 20
    c: DistanceY(g4) = 19.6
    c: Distance(g-3,g3) = 3
    c: Vertical(g1,g0)
    c: Coincident(g5,g-1)
    c: PointOnObject(g5,g-1)
    c: DistanceX(g5,g5) = 0.4  'length'
    c: Coincident(g2,g6)
    c: Coincident(g6,g7)
    c: Coincident(g7,g1)
    c: Parallel(g7,g1)
    c: Parallel(g6,g2)
    c: Equal(g6,g7)
    c: Distance(g1,g2) = 0.5
FEATURE [Sketcher::SketchObject] Sketch026  label="top_bends2_sketch"
  ExternalGeometry = -> [Sketch023]
  FullyConstrained = true
  expr: Constraints[10] = 90 deg - <<base_Sketch>>.Constraints.angle / 2
  expr: Constraints[4] = <<top_bends1_sketch>>.Constraints.max_width
  sketch-geometry (4):
    g0: LineSegment StartX=319.163 StartY=0.1 StartZ=0 EndX=319.163 EndY=148.551 EndZ=0
    g1: LineSegment StartX=294.963 StartY=0.1 StartZ=0 EndX=319.163 EndY=0.1 EndZ=0
    g2: LineSegment StartX=294.963 StartY=0.1 StartZ=0 EndX=294.963 EndY=82.0617 EndZ=0
    g3: LineSegment StartX=294.963 StartY=82.0617 StartZ=0 EndX=319.163 EndY=148.551 EndZ=0
  constraints (11):
    c: Coincident(g1,g0)
    c: Horizontal(g1)
    c: Coincident(g0,g-4)
    c: Coincident(g0,g-3)
    c: DistanceX(g1,g1) = 24.2
    c: Coincident(g1,g2)
    c: Vertical(g2)
    c: DistanceX(g2,g3) = 0
    c: Coincident(g2,g3)
    c: Coincident(g3,g0)
    c: Angle(g3) = 1.22173
FEATURE [Sketcher::SketchObject] Sketch027
  ExternalGeometry = -> [Sketch023,Sketch026]
  FullyConstrained = true
  sketch-geometry (15):
    g0: Circle CenterX=314.763 CenterY=25.1 CenterZ=0 NormalX=0 NormalY=0 NormalZ=1 AngleXU=0 Radius=1.7
    g1: Circle CenterX=314.763 CenterY=131.551 CenterZ=0 NormalX=0 NormalY=0 NormalZ=1 AngleXU=0 Radius=1.7
    g2: LineSegment StartX=316.463 StartY=131.551 StartZ=0 EndX=319.563 EndY=131.551 EndZ=0
    g3: LineSegment StartX=316.563 StartY=55.8253 StartZ=0 EndX=316.563 EndY=75.8253 EndZ=0
    g4: LineSegment StartX=316.563 StartY=75.8253 StartZ=0 EndX=313.363 EndY=75.8253 EndZ=0
    g5: LineSegment StartX=313.363 StartY=75.8253 StartZ=0 EndX=313.363 EndY=55.8253 EndZ=0
    g6: LineSegment StartX=313.363 StartY=55.8253 StartZ=0 EndX=316.563 EndY=55.8253 EndZ=0
    g7: LineSegment StartX=319.563 StartY=0.1 StartZ=0 EndX=319.563 EndY=55.8253 EndZ=0
    g8: LineSegment StartX=319.563 StartY=55.8253 StartZ=0 EndX=319.563 EndY=75.8253 EndZ=0
    g9: LineSegment StartX=319.563 StartY=75.8253 StartZ=0 EndX=319.563 EndY=131.551 EndZ=0
    g10: Circle CenterX=301.963 CenterY=25.1 CenterZ=0 NormalX=0 NormalY=0 NormalZ=1 AngleXU=0 Radius=1.7
    g11: Circle CenterX=301.963 CenterY=75.0617 CenterZ=0 NormalX=0 NormalY=0 NormalZ=1 AngleXU=0 Radius=1.7
    g12: LineSegment StartX=294.963 StartY=82.0617 StartZ=0 EndX=319.163 EndY=82.0617 EndZ=0
    g13: LineSegment StartX=301.963 StartY=82.0617 StartZ=0 EndX=301.963 EndY=75.0617 EndZ=0
    g14: LineSegment StartX=301.963 StartY=75.0617 StartZ=0 EndX=294.963 EndY=75.0617 EndZ=0
  constraints (45):
    c: Equal(g0,g1)
    c: Diameter(g0) = 3.4
    c: Vertical(g1,g0)
    c: DistanceY(g-4,g0) = 25
    c: DistanceY(g1,g-3) = 17
    c: Vertical(g2,g-3)
    c: PointOnObject(g1,g2)
    c: Horizontal(g2)
    c: Coincident(g3,g4)
    c: Coincident(g4,g5)
    c: Coincident(g5,g6)
    c: Coincident(g6,g3)
    c: Vertical(g3)
    c: Vertical(g5)
    c: Horizontal(g4)
    c: Horizontal(g6)
    c: DistanceX(g3,g-4) = 3
    c: DistanceX(g6,g6) = 3.2
    c: DistanceY(g3,g3) = 20
    c: Coincident(g-4,g7)
    c: Vertical(g7)
    c: Coincident(g7,g8)
    c: Vertical(g8)
    c: Coincident(g8,g9)
    c: Coincident(g9,g2)
    c: Equal(g7,g9)
    c: Horizontal(g7,g3)
    c: Horizontal(g3,g8)
    c: PointOnObject(g2,g1)
    c: Distance(g2) = 3.1
    c: Equal(g10,g0)
    c: Horizontal(g10,g0)
    c: Coincident(g12,g-5)
    c: Horizontal(g12)
    c: Vertical(g12,g-4)
    c: PointOnObject(g13,g12)
    c: Coincident(g13,g11)
    c: Vertical(g13)
    c: Coincident(g13,g14)
    c: PointOnObject(g14,g-5)
    c: Horizontal(g14)
    c: Equal(g14,g13)
    c: Vertical(g11,g10)
    c: DistanceX(g-5,g10) = 7
    c: Equal(g11,g10)
FEATURE [PartDesign::FeaturePython] Extend  # WARN: FeaturePython — macro-defined, semantics opaque (R4)
  BaseFeature = -> BaseBend
  Offset = 0.02
  Refine = true
  Suppressed = false
  UseSubtraction = false
  baseObject = -> BaseBend [Face1]
  gap1 = 0
  gap2 = 0
  length = 0
FEATURE [PartDesign::FeaturePython] Bend  # WARN: FeaturePython — macro-defined, semantics opaque (R4)
  AutoMiter = false
  BaseFeature = -> Extend
  BendType = 0
  LengthList = [0.1]
  LengthSpec = 0
  ReliefFactor = 0.7
  Suppressed = false
  UseReliefFactor = false
  angle = 90
  baseObject = -> Extend [Edge119,Edge104,Edge124,Edge75,Edge58,Edge122,Edge29,Edge14]
  bendAList = [90]
  extend1 = 0
  extend2 = 0
  gap1 = 0
  gap2 = 0
  invert = true
  kfactor = 0.5
  length = 0.1
  maxExtendDist = 5
  minGap = 0.2
  minReliefGap = 1
  miterangle1 = 0
  miterangle2 = 0
  offset = 0
  radius = 0.1
  reliefType = 0
  reliefd = 1
  reliefw = 0.8
  sketchflip = false
  sketchinvert = false
  unfold = false
  expr: radius = BaseBend.radius
FEATURE [Sketcher::SketchObject] Sketch028
  ExternalGeometry = -> [Sketch023,Sketch]
  FullyConstrained = true
  sketch-geometry (11):
    g0: LineSegment StartX=318.774 StartY=148.685 StartZ=0 EndX=319.063 EndY=148.928 EndZ=0
    g1: LineSegment StartX=319.063 StartY=148.928 StartZ=0 EndX=318.742 EndY=149.311 EndZ=0
    g2: LineSegment StartX=319.063 StartY=149.58 StartZ=0 EndX=318.453 EndY=149.068 EndZ=0
    g3: LineSegment StartX=318.453 StartY=149.068 StartZ=0 EndX=318.774 EndY=148.685 EndZ=0
    g4: LineSegment StartX=164.817 StartY=19.5 StartZ=0 EndX=167.255 EndY=21.5453 EndZ=0
    g5: LineSegment StartX=167.255 StartY=21.5453 StartZ=0 EndX=166.933 EndY=21.9284 EndZ=0
    g6: LineSegment StartX=166.933 StartY=21.9284 StartZ=0 EndX=161.635 EndY=28.2424 EndZ=0
    g7: LineSegment StartX=161.635 StartY=19.5 StartZ=0 EndX=164.817 EndY=19.5 EndZ=0
    g8: LineSegment StartX=161.635 StartY=28.2424 StartZ=0 EndX=161.635 EndY=20 EndZ=0
    g9: LineSegment StartX=161.635 StartY=20 StartZ=0 EndX=161.635 EndY=19.5 EndZ=0
    g10: LineSegment StartX=319.063 StartY=149.58 StartZ=0 EndX=319.063 EndY=148.928 EndZ=0
  constraints (30):
    c: Coincident(g0,g1)
    c: Coincident(g2,g3)
    c: Parallel(g0,g2)
    c: Coincident(g5,g6)
    c: Coincident(g8,g9)
    c: Coincident(g8,g-4)
    c: Coincident(g4,g7)
    c: Coincident(g5,g-3)
    c: Coincident(g2,g-5)
    c: Coincident(g8,g6)
    c: Parallel(g5,g6)
    c: Parallel(g9,g8)
    c: Perpendicular(g7,g9)
    c: Perpendicular(g5,g4)
    c: Coincident(g10,g0)
    c: Perpendicular(g2,g1)
    c: PointOnObject(g2,g-6)
    c: DistanceX(g10,g-6) = 0.5
    c: PointOnObject(g1,g2)
    c: Coincident(g2,g10)
    c: Vertical(g10)
    c: Coincident(g7,g9)
    c: DistanceY(g9,g9) = 0.5
    c: Parallel(g9,g-4)
    c: Coincident(g5,g4)
    c: Equal(g5,g9)
    c: Parallel(g5,g-3)
    c: PointOnObject(g-5,g3)
    c: Coincident(g3,g0)
    c: Equal(g3,g5)
FEATURE [Sketcher::SketchObject] Sketch029  label="cap_base_sketch"
  FullyConstrained = true
  expr: Constraints[6] = (<<side_Sketch>>.Constraints.distance + <<mid_Sketch>>.Constraints.middle) * 2
  expr: Constraints[7] = <<side_Sketch>>.Constraints.side
  sketch-geometry (3):
    g0: LineSegment StartX=639.126 StartY=0 StartZ=0 EndX=639.126 EndY=150 EndZ=0
    g1: LineSegment StartX=639.126 StartY=150 StartZ=0 EndX=-639.126 EndY=150 EndZ=0
    g2: LineSegment StartX=-639.126 StartY=150 StartZ=0 EndX=-639.126 EndY=0 EndZ=0
  constraints (9):
    c: PointOnObject(g0,g-1)
    c: Vertical(g0)
    c: Coincident(g0,g1)
    c: Coincident(g1,g2)
    c: PointOnObject(g2,g-1)
    c: Vertical(g2)
    c: DistanceX(g1,g1) = 1278.25
    c: DistanceY(g0,g0) = 150
    c: Symmetric(g0,g1,g-2)
FEATURE [Sketcher::SketchObject] Sketch030
  ExternalGeometry = -> [Sketch023,Sketch001]
  FullyConstrained = false
  sketch-geometry (8):
    g0: LineSegment StartX=319.063 StartY=0.1 StartZ=0 EndX=319.063 EndY=0 EndZ=0
    g1: LineSegment StartX=319.063 StartY=0 StartZ=0 EndX=319.563 EndY=0 EndZ=0
    g2: LineSegment StartX=319.563 StartY=0 StartZ=0 EndX=319.563 EndY=0.1 EndZ=0
    g3: LineSegment StartX=319.563 StartY=0.1 StartZ=0 EndX=319.063 EndY=0.1 EndZ=0
    g4: LineSegment StartX=319.063 StartY=149 StartZ=0 EndX=319.563 EndY=149 EndZ=0
    g5: LineSegment StartX=319.563 StartY=149 StartZ=0 EndX=319.563 EndY=150 EndZ=0
    g6: LineSegment StartX=319.563 StartY=150 StartZ=0 EndX=319.063 EndY=150 EndZ=0
    g7: LineSegment StartX=319.063 StartY=150 StartZ=0 EndX=319.063 EndY=149 EndZ=0
  constraints (16):
    c: Coincident(g0,g1)
    c: Coincident(g1,g2)
    c: Coincident(g2,g3)
    c: Coincident(g3,g0)
    c: Vertical(g0)
    c: Vertical(g2)
    c: Horizontal(g1)
    c: Horizontal(g3)
    c: Coincident(g4,g5)
    c: Coincident(g5,g6)
    c: Coincident(g6,g7)
    c: Coincident(g7,g4)
    c: Horizontal(g4)
    c: Horizontal(g6)
    c: Vertical(g5)
    c: Vertical(g7)
FEATURE [PartDesign::SubShapeBinder] Binder003
  BindCopyOnChange = 0
  BindMode = 0
  ClaimChildren = true
  Context = -> Body002 [Binder003.]
  Fuse = false
  MakeFace = true
  OffsetFill = false
  OffsetIntersection = false
  OffsetJoinType = 0
  OffsetOpenResult = false
  PartialLoad = false
  Relative = true
  Support = -> [Connect001]
  _Version = 2
FEATURE [PartDesign::FeaturePython] BaseBend001  # WARN: FeaturePython — macro-defined, semantics opaque (R4)
  BendSide = 0
  BendSketch = -> Binder003
  MidPlane = false
  Reverse = false
  Suppressed = false
  length = 100
  radius = 0.1
  thickness = 0.3
FEATURE [PartDesign::FeaturePython] Extend001  # WARN: FeaturePython — macro-defined, semantics opaque (R4)
  BaseFeature = -> BaseBend001
  Offset = 0.02
  Refine = true
  Suppressed = false
  UseSubtraction = false
  baseObject = -> BaseBend001 [Face1]
  gap1 = 0
  gap2 = 0
  length = 0
FEATURE [PartDesign::FeaturePython] Bend001  # WARN: FeaturePython — macro-defined, semantics opaque (R4)
  AutoMiter = true
  BaseFeature = -> Extend001
  BendType = 1
  LengthList = [15]
  LengthSpec = 0
  ReliefFactor = 0.7
  Suppressed = false
  UseReliefFactor = false
  angle = 90
  baseObject = -> Extend001 [Edge6,Edge8,Edge9,Edge11]
  bendAList = [90]
  extend1 = 0
  extend2 = 0
  gap1 = 0
  gap2 = 0
  invert = true
  kfactor = 0.5
  length = 15
  maxExtendDist = 5
  minGap = 0.2
  minReliefGap = 1
  miterangle1 = 0
  miterangle2 = 0
  offset = 0
  radius = 0.1
  reliefType = 0
  reliefd = 1
  reliefw = 0.8
  sketchflip = false
  sketchinvert = false
  unfold = false
  expr: radius = BaseBend.radius
FEATURE [Sketcher::SketchObject] Sketch031
  AttachmentSupport = -> [XY_Plane003]
  ExternalGeometry = -> [Binder003]
  FullyConstrained = true
  MapMode = 5
  sketch-geometry (13):
    g0: LineSegment StartX=172.194 StartY=8.2 StartZ=0 EndX=172.194 EndY=11.2 EndZ=0
    g1: LineSegment StartX=172.194 StartY=11.2 StartZ=0 EndX=174.122 EndY=8.90187 EndZ=0
    g2: LineSegment StartX=172.194 StartY=8.2 StartZ=0 EndX=173.286 EndY=8.2 EndZ=0
    g3: LineSegment StartX=173.286 StartY=8.2 StartZ=0 EndX=174.122 EndY=8.90187 EndZ=0
    g4: LineSegment StartX=309.163 StartY=122.737 StartZ=0 EndX=309.163 EndY=147 EndZ=0
    g5: LineSegment StartX=309.163 StartY=122.214 StartZ=0 EndX=312.42 EndY=124.947 EndZ=0
    g6: LineSegment StartX=309.163 StartY=122.214 StartZ=0 EndX=308.906 EndY=122.521 EndZ=0
    g7: LineSegment StartX=308.906 StartY=122.521 StartZ=0 EndX=309.163 EndY=122.737 EndZ=0
    g8: LineSegment StartX=312.163 StartY=150 StartZ=0 EndX=312.163 EndY=125.254 EndZ=0
    g9: LineSegment StartX=312.163 StartY=125.254 StartZ=0 EndX=312.42 EndY=124.947 EndZ=0
    g10: LineSegment StartX=309.163 StartY=147 StartZ=0 EndX=311.763 EndY=147 EndZ=0
    g11: LineSegment StartX=311.763 StartY=147 StartZ=0 EndX=311.763 EndY=150 EndZ=0
    g12: LineSegment StartX=311.763 StartY=150 StartZ=0 EndX=312.163 EndY=150 EndZ=0
  constraints (38):
    c: PointOnObject(g0,g-3)
    c: Coincident(g0,g1)
    c: PointOnObject(g1,g-4)
    c: Perpendicular(g-3,g0)
    c: Perpendicular(g-4,g1)
    c: Equal(g1,g0)
    c: DistanceY(g0,g0) = 3
    c: Coincident(g0,g2)
    c: Coincident(g2,g-4)
    c: Coincident(g2,g3)
    c: Coincident(g3,g1)
    c: Vertical(g4)
    c: Coincident(g4,g10)
    c: Coincident(g12,g8)
    c: PointOnObject(g5,g-4)
    c: Vertical(g4,g5)
    c: Coincident(g5,g6)
    c: Coincident(g6,g7)
    c: Distance(g6) = 0.4
    c: Perpendicular(g5,g6)
    c: Perpendicular(g7,g6)
    c: DistanceX(g10,g12) = 3
    c: Coincident(g5,g9)
    c: Coincident(g7,g4)
    c: Coincident(g8,g9)
    c: Vertical(g8)
    c: Perpendicular(g5,g9)
    c: PointOnObject(g-5,g5)
    c: Distance(g9) = 0.4
    c: Coincident(g10,g11)
    c: Horizontal(g10)
    c: Coincident(g11,g12)
    c: Horizontal(g12)
    c: Coincident(g8,g-5)
    c: Vertical(g11)
    c: DistanceY(g11,g11) = 3
    c: DistanceX(g12,g12) = 0.4
    c: Distance(g8,g4) = 3
FEATURE [PartDesign::Pocket] Pocket003
  BaseFeature = -> Bend001
  Direction = (0,0,-1)
  Length = 5
  Length2 = 5
  Midplane = true
  Profile = -> Sketch031
  ReferenceAxis = -> Sketch031 [N_Axis]
  Suppressed = false
  Type = 1
FEATURE [PartDesign::Mirrored] Mirrored
  BaseFeature = -> Pocket003
  MirrorPlane = -> Sketch031 [V_Axis]
  Originals = -> [Pocket003]
  Suppressed = false
FEATURE [Part::FeaturePython] LinearArray002  # WARN: FeaturePython — macro-defined, semantics opaque (R4)
  Alignment = 0
  CellStart = A1
  Count = 2
  Dir = (1,0,0)
  DirIsDriven = true
  DistributionLaw = 0
  DrivenProperty = 1
  EndInclusive = true
  ExposePlacement = false
  GeneratorMode = 0
  MarkerShape = 1
  MarkerSize = 0
  NumElements = 2
  OrientMode = 1
  Placement = pos=(-30,13.8,0) rot=(0,0,1;0rad)
  Point = (0,0,0)
  PointIsDriven = true
  Reverse = false
  SpanEnd = 60
  SpanStart = 0
  Step = 60
  Type = lattice2LinearArray.LinearArray
  VSGVersion = 1
  Values = 0.0 | 60.0
  ValuesSource = 2
  isLattice = 1
  expr: .Placement.Base.x = -SpanEnd / 2
FEATURE [Part::FeaturePython] Populate005  label="Populate Populate LinearArray001 with PlacementSubsequence with LinearArray002"  # WARN: FeaturePython — macro-defined, semantics opaque (R4)
  Copying = 0
  ExposePlacement = false
  MarkerShape = 1
  MarkerSize = 0
  NumElements = 8
  Object = -> LinearArray002
  OutputCompounding = 0
  Placement = pos=(0,20,0) rot=(0,0,1;0rad)
  PlacementsTo = -> PlacementSubsequence
  Referencing = 0
  Type = lattice2PopulateCopies.LatticePopulateCopies
  isLattice = 1
  expr: .Placement.Base.y = <<base_Sketch>>.Constraints.offset
FEATURE [Sketcher::SketchObject] Sketch025
  ExternalGeometry = -> [Sketch023,Populate005]
  FullyConstrained = true
  sketch-geometry (20):
    g0: Circle CenterX=38 CenterY=15.2 CenterZ=0 NormalX=0 NormalY=0 NormalZ=1 AngleXU=0 Radius=1.7
    g1: Circle CenterX=144.635 CenterY=15.2 CenterZ=0 NormalX=0 NormalY=0 NormalZ=1 AngleXU=0 Radius=1.7
    g2: Circle CenterX=183.041 CenterY=29.1787 CenterZ=0 NormalX=0 NormalY=0 NormalZ=1 AngleXU=0 Radius=1.7
    g3: Circle CenterX=266.261 CenterY=99.008 CenterZ=0 NormalX=0 NormalY=0 NormalZ=1 AngleXU=0 Radius=1.7
    g4: LineSegment StartX=161.635 StartY=20 StartZ=0 EndX=0 EndY=20 EndZ=0
    g5: LineSegment StartX=144.635 StartY=16.9 StartZ=0 EndX=144.635 EndY=20 EndZ=0
    g6: LineSegment StartX=166.933 StartY=21.9284 StartZ=0 EndX=318.453 EndY=149.068 EndZ=0
    g7: LineSegment StartX=265.168 StartY=100.31 StartZ=0 EndX=263.175 EndY=102.685 EndZ=0
    g8: LineSegment StartX=181.949 StartY=30.481 StartZ=0 EndX=179.956 EndY=32.8558 EndZ=0
    g9: LineSegment StartX=0 StartY=15.2 StartZ=0 EndX=38 EndY=15.2 EndZ=0
    g10: LineSegment StartX=38 StartY=15.2 StartZ=0 EndX=91.3175 EndY=15.2 EndZ=0
    g11: LineSegment StartX=91.3175 StartY=15.2 StartZ=0 EndX=144.635 EndY=15.2 EndZ=0
    g12: LineSegment StartX=246.644 StartY=106.829 StartZ=0 EndX=255.515 EndY=96.2571 EndZ=0
    g13: Circle CenterX=204.174 CenterY=27.3299 CenterZ=0 NormalX=0 NormalY=0 NormalZ=1 AngleXU=0 Radius=1.7
    g14: LineSegment StartX=183.041 StartY=29.1787 StartZ=0 EndX=192.683 EndY=17.6881 EndZ=0
    g15: LineSegment StartX=192.683 StartY=17.6881 StartZ=0 EndX=204.174 EndY=27.3299 EndZ=0
    g16: LineSegment StartX=275.902 StartY=87.5173 StartZ=0 EndX=266.261 EndY=99.008 EndZ=0
    g17: LineSegment StartX=204.174 StartY=27.3299 StartZ=0 EndX=240.038 EndY=57.4236 EndZ=0
    g18: LineSegment StartX=240.038 StartY=57.4236 StartZ=0 EndX=275.902 EndY=87.5173 EndZ=0
    g19: Circle CenterX=240.038 CenterY=57.4236 CenterZ=0 NormalX=0 NormalY=0 NormalZ=1 AngleXU=0 Radius=1.7
  constraints (58):
    c: Equal(g0,g1)
    c: Equal(g0,g2)
    c: Equal(g0,g3)
    c: Diameter(g0) = 3.4
    c: Coincident(g4,g-3)
    c: PointOnObject(g4,g-2)
    c: Horizontal(g4)
    c: PointOnObject(g5,g1)
    c: PointOnObject(g5,g4)
    c: Vertical(g5)
    c: Horizontal(g1,g0)
    c: PointOnObject(g1,g5)
    c: Coincident(g6,g-4)
    c: Coincident(g6,g-5)
    c: PointOnObject(g7,g3)
    c: PointOnObject(g7,g6)
    c: PointOnObject(g8,g2)
    c: PointOnObject(g8,g6)
    c: Perpendicular(g6,g8)
    c: PointOnObject(g2,g8)
    c: PointOnObject(g3,g7)
    c: Perpendicular(g6,g7)
    c: Equal(g7,g8)
    c: Distance(g6,g8) = 17
    c: PointOnObject(g9,g-2)
    c: Coincident(g9,g0)
    c: Horizontal(g9)
    c: Coincident(g9,g10)
    c: Horizontal(g10)
    c: Coincident(g10,g11)
    c: Coincident(g11,g1)
    c: Equal(g11,g10)
    c: DistanceX(g1,g4) = 17
    c: DistanceY(g5,g5) = 3.1
    c: Equal(g8,g5)
    c: Coincident(g12,g-6)
    c: PointOnObject(g12,g6)
    c: Perpendicular(g6,g12)
    c: Distance(g12,g7) = 10
    c: Coincident(g14,g2)
    c: Parallel(g14,g8)
    c: Equal(g13,g2)
    c: Distance(g14) = 15
    c: Coincident(g14,g15)
    c: Coincident(g15,g13)
    c: Coincident(g15,g17)
    c: Coincident(g18,g16)
    c: Coincident(g16,g3)
    c: Parallel(g7,g16)
    c: Perpendicular(g14,g15)
    c: Equal(g15,g14)
    c: Coincident(g17,g18)
    c: Parallel(g15,g17)
    c: Parallel(g15,g18)
    c: Equal(g17,g18)
    c: Coincident(g19,g17)
    c: Equal(g19,g13)
    c: DistanceX(g9,g9) = 38
FEATURE [Sketcher::SketchObject] Sketch020  label="top_cut_line"
  ExternalGeometry = -> [Sketch,Sketch025]
  FullyConstrained = false
  sketch-geometry (5):
    g0: LineSegment StartX=159.84 StartY=-3.34356 StartZ=0 EndX=333.391 EndY=142.283 EndZ=0
    g1: LineSegment StartX=159.969 StartY=-3.49677 StartZ=0 EndX=333.519 EndY=142.13 EndZ=0
    g2: LineSegment StartX=333.519 StartY=142.13 StartZ=0 EndX=333.262 EndY=142.436 EndZ=0
    g3: LineSegment StartX=333.262 StartY=142.436 StartZ=0 EndX=159.711 EndY=-3.19035 EndZ=0
    g4: LineSegment StartX=159.711 StartY=-3.19035 StartZ=0 EndX=159.969 EndY=-3.49677 EndZ=0
  constraints (12):
    c: Coincident(g1,g2)
    c: Coincident(g2,g3)
    c: Coincident(g3,g4)
    c: Coincident(g4,g1)
    c: Parallel(g1,g3)
    c: Parallel(g2,g4)
    c: Perpendicular(g2,g1)
    c: Symmetric(g1,g3,g0)
    c: Symmetric(g1,g2,g0)
    c: Distance(g4) = 0.4
    c: Parallel(g0,g-3)
    c: Distance(g-4,g0) = 10
FEATURE [Sketcher::SketchObject] Sketch021  label="dropper_fix_composit_base_sketch"
  ExternalGeometry = -> [Sketch020,Sketch,Sketch025]
  FullyConstrained = true
  expr: Constraints[12] = <<base_Sketch>>.Constraints.total_depth
  sketch-geometry (4):
    g0: LineSegment StartX=0 StartY=8.2 StartZ=0 EndX=173.286 EndY=8.2 EndZ=0
    g1: LineSegment StartX=312.163 StartY=150 StartZ=0 EndX=0 EndY=150 EndZ=0
    g2: LineSegment StartX=173.286 StartY=8.2 StartZ=0 EndX=312.163 EndY=124.732 EndZ=0
    g3: LineSegment StartX=312.163 StartY=124.732 StartZ=0 EndX=312.163 EndY=150 EndZ=0
  constraints (15):
    c: Coincident(g0,g2)
    c: Coincident(g3,g1)
    c: PointOnObject(g0,g-2)
    c: PointOnObject(g1,g-2)
    c: Horizontal(g1)
    c: Horizontal(g0)
    c: Coincident(g2,g3)
    c: PointOnObject(g-3,g2)
    c: PointOnObject(g-3,g2)
    c: Vertical(g3)
    c: DistanceY(g0,g-6) = 7
    c: Angle(g-1,g2) = 0.698132  'angle'
    c: DistanceY(g1) = 150
    c: Distance(g3) = 25.2683  'side'
    c: DistanceX(g1,g-4) = 7.4
FEATURE [Sketcher::SketchObject] Sketch022
  ExternalGeometry = -> [Sketch020]
  FullyConstrained = false
  sketch-geometry (6):
    g0: LineSegment StartX=159.711 StartY=-3.19035 StartZ=0 EndX=159.711 EndY=-88.7348 EndZ=0
    g1: LineSegment StartX=159.711 StartY=-88.7348 StartZ=0 EndX=398.504 EndY=-88.7348 EndZ=0
    g2: LineSegment StartX=398.504 StartY=-88.7348 StartZ=0 EndX=398.504 EndY=175.545 EndZ=0
    g3: LineSegment StartX=398.504 StartY=175.545 StartZ=0 EndX=333.262 EndY=175.545 EndZ=0
    g4: LineSegment StartX=333.262 StartY=175.545 StartZ=0 EndX=333.262 EndY=142.436 EndZ=0
    g5: LineSegment StartX=333.262 StartY=142.436 StartZ=0 EndX=159.711 EndY=-3.19035 EndZ=0
  constraints (13):
    c: Coincident(g-3,g0)
    c: Vertical(g0)
    c: Coincident(g0,g1)
    c: Horizontal(g1)
    c: Coincident(g1,g2)
    c: Vertical(g2)
    c: Coincident(g2,g3)
    c: Horizontal(g3)
    c: Coincident(g3,g4)
    c: Coincident(g4,g-3)
    c: Vertical(g4)
    c: Coincident(g4,g5)
    c: Coincident(g5,g0)
FEATURE [Sketcher::SketchObject] Sketch024  label="top_bends1_sketch"
  ExternalGeometry = -> [Sketch023,Sketch021]
  FullyConstrained = true
  sketch-geometry (11):
    g0: LineSegment StartX=0 StartY=19.6 StartZ=0 EndX=161.635 EndY=19.6 EndZ=0
    g1: LineSegment StartX=161.635 StartY=19.6 StartZ=0 EndX=161.635 EndY=9.6 EndZ=0
    g2: LineSegment StartX=161.635 StartY=9.6 StartZ=0 EndX=0 EndY=9.6 EndZ=0
    g3: LineSegment StartX=182.746 StartY=3.08367 StartZ=0 EndX=286.263 EndY=89.9452 EndZ=0
    g4: LineSegment StartX=167.19 StartY=21.6219 StartZ=0 EndX=182.746 EndY=3.08367 EndZ=0
    g5: LineSegment StartX=318.71 StartY=148.762 StartZ=0 EndX=167.19 EndY=21.6219 EndZ=0
    g6: LineSegment StartX=318.71 StartY=148.762 StartZ=0 EndX=286.263 EndY=89.9452 EndZ=0
    g7: LineSegment StartX=318.453 StartY=149.068 StartZ=0 EndX=318.453 EndY=0 EndZ=0
    g8: LineSegment StartX=166.933 StartY=21.9284 StartZ=0 EndX=318.453 EndY=149.068 EndZ=0
    g9: LineSegment StartX=166.933 StartY=21.9284 StartZ=0 EndX=242.693 EndY=10.9642 EndZ=0
    g10: LineSegment StartX=318.453 StartY=0 StartZ=0 EndX=242.693 EndY=10.9642 EndZ=0
  constraints (30):
    c: PointOnObject(g0,g-2)
    c: Coincident(g0,g-5)
    c: Horizontal(g0)
    c: Coincident(g0,g1)
    c: Vertical(g1)
    c: Coincident(g1,g2)
    c: Coincident(g5,g4)
    c: Coincident(g4,g3)
    c: Coincident(g5,g-4)
    c: Parallel(g3,g5)
    c: Coincident(g6,g3)
    c: Coincident(g5,g6)
    c: Coincident(g5,g-3)
    c: Parallel(g4,g-4)
    c: PointOnObject(g2,g-2)
    c: Horizontal(g2)
    c: DistanceY(g1,g1) = 10
    c: Coincident(g7,g-3)
    c: PointOnObject(g7,g-1)
    c: Vertical(g7)
    c: Coincident(g8,g-4)
    c: Coincident(g8,g7)
    c: Coincident(g9,g8)
    c: Coincident(g10,g7)
    c: Coincident(g10,g9)
    c: Parallel(g10,g9)
    c: Equal(g10,g9)
    c: PointOnObject(g9,g6)
    c: Distance(g3,g-6) = 10
    c: Distance(g3,g4) = 24.2  'max_width'
FEATURE [Part::Mirroring] Part__Mirroring003  label="Sketch024 (Mirror #4)"
  Base = (0,0,0)
  Normal = (1,0,0)
  Source = -> Sketch024
FEATURE [Part::FeaturePython] Connect002  # WARN: FeaturePython — macro-defined, semantics opaque (R4)
  Objects = -> [Sketch024,Part__Mirroring003]
  Tolerance = 0
FEATURE [Part::Compound] Compound002
  Links = -> [Connect002,Sketch026]
  Placement = pos=(319.563,0,0) rot=(0,0,1;0rad)
  expr: .Placement.Base.x = <<mid_Sketch>>.Constraints.middle
FEATURE [Part::Mirroring] Part__Mirroring004  label="Compound002 (Mirror #5)"
  Base = (0,0,0)
  Normal = (1,0,0)
  Source = -> Compound002
FEATURE [Part::FeaturePython] Connect003  # WARN: FeaturePython — macro-defined, semantics opaque (R4)
  Objects = -> [Part__Mirroring004,Compound002]
  Tolerance = 0
FEATURE [Part::Mirroring] Part__Mirroring005  label="Sketch025 (Mirror #6)"
  Base = (0,0,0)
  Normal = (1,0,0)
  Source = -> Sketch025
FEATURE [Part::Compound] Compound003
  Links = -> [Sketch025,Part__Mirroring005,Sketch027]
  Placement = pos=(319.563,0,0) rot=(0,0,1;0rad)
  expr: .Placement.Base.x = <<mid_Sketch>>.Constraints.middle
FEATURE [Part::Mirroring] Part__Mirroring006  label="Compound003 (Mirror #7)"
  Base = (0,0,0)
  Normal = (1,0,0)
  Source = -> Compound003
FEATURE [Part::Compound] Compound004
  Links = -> [Part__Mirroring006,Compound003]
FEATURE [Part::Extrusion] Extrude001
  Base = -> Connect003
  Dir = (0,0,1)
  DirMode = 2
  FaceMakerClass = Part::FaceMakerBullseye
  LengthFwd = 0.3
  LengthRev = 0
  Solid = true
  Symmetric = false
FEATURE [Part::Extrusion] Extrude002
  Base = -> Compound004
  Dir = (0,0,1)
  DirMode = 2
  FaceMakerClass = Part::FaceMakerBullseye
  LengthFwd = 10
  LengthRev = 0
  Solid = true
  Symmetric = false
FEATURE [Part::Cut] Cut
  Base = -> Extrude001
  Placement = pos=(0,0,1100.1) rot=(0,0,1;0rad)
  Tool = -> Extrude002
  expr: .Placement.Base.z = <<Properties>>.modules_fix_height + 0.1 mm
FEATURE [Part::Mirroring] Part__Mirroring002  label="dropper_fix_composit_base_sketch (Mirror #3)"
  Base = (0,0,0)
  Normal = (1,0,0)
  Source = -> Sketch021
FEATURE [Part::FeaturePython] Connect001  # WARN: FeaturePython — macro-defined, semantics opaque (R4)
  Objects = -> [Sketch021,Part__Mirroring002]
  Tolerance = 0
FEATURE [PartDesign::SubShapeBinder] Binder004
  BindCopyOnChange = 0
  BindMode = 0
  ClaimChildren = false
  Fuse = false
  MakeFace = true
  OffsetFill = false
  OffsetIntersection = false
  OffsetJoinType = 0
  OffsetOpenResult = false
  PartialLoad = false
  Relative = true
  Support = -> [<external ../dropper.FCStd>#Connect]
  _Version = 2
  expr: Support = dropper#<<fix>>._self
FEATURE [PartDesign::SubShapeBinder] Binder005  label="dropper_feed"
  BindCopyOnChange = 0
  BindMode = 0
  ClaimChildren = false
  Fuse = false
  MakeFace = true
  OffsetFill = false
  OffsetIntersection = false
  OffsetJoinType = 0
  OffsetOpenResult = false
  PartialLoad = false
  Relative = false
  Support = -> [<external ../dropper.FCStd>#Sketch008]
  _Version = 2
  expr: Support = <<dropper>>#<<feed>>._self
FEATURE [PartDesign::SubShapeBinder] Binder006  label="dropper_base"
  BindCopyOnChange = 0
  BindMode = 0
  ClaimChildren = false
  Fuse = false
  MakeFace = true
  OffsetFill = false
  OffsetIntersection = false
  OffsetJoinType = 0
  OffsetOpenResult = false
  PartialLoad = false
  Relative = true
  Support = -> [<external ../dropper.FCStd>#Sketch007]
  _Version = 2
  expr: Support = <<dropper>>#<<base>>._self
FEATURE [Part::Compound] Compound008
  Links = -> [Binder004,Binder006]
FEATURE [Part::FeaturePython] FuseCompound  label="dropper_fix"  # WARN: FeaturePython — macro-defined, semantics opaque (R4)
  Base = -> Compound008
  Refine = true
  recomputeQuota = -1
FEATURE [Part::Extrusion] Extrude004  label="dropper_feed_extrude"
  Base = -> Binder005
  Dir = (0,0,1)
  DirMode = 2
  FaceMakerClass = Part::FaceMakerBullseye
  LengthFwd = 30
  LengthRev = 0
  Solid = false
  Symmetric = true
FEATURE [Part::FeaturePython] Populate006  label="Populate Populate Populate LinearArray001 with PlacementSubsequence with LinearArray002 with dropper_feed"  # WARN: FeaturePython — macro-defined, semantics opaque (R4)
  Copying = 0
  ExposePlacement = false
  MarkerShape = 1
  MarkerSize = 0
  NumElements = 0
  Object = -> Extrude004
  OutputCompounding = 1
  PlacementsTo = -> Populate005
  Referencing = 0
  Type = lattice2PopulateCopies.LatticePopulateCopies
  isLattice = 0
FEATURE [Part::Extrusion] Extrude005  label="dropper_fix_extrude"
  Base = -> FuseCompound
  Dir = (0,0,1)
  DirMode = 2
  FaceMakerClass = Part::FaceMakerBullseye
  LengthFwd = 2.4
  LengthRev = 0
  Solid = false
  Symmetric = false
FEATURE [Part::Extrusion] Extrude006  label="dropper_base_extrude"
  Base = -> Binder006
  Dir = (0,0,1)
  DirMode = 2
  FaceMakerClass = Part::FaceMakerBullseye
  LengthFwd = 20
  LengthRev = 0
  Solid = false
  Symmetric = false
FEATURE [Part::FeaturePython] Populate008  label="Populate Populate Populate LinearArray001 with PlacementSubsequence with LinearArray002 with dropper_base"  # WARN: FeaturePython — macro-defined, semantics opaque (R4)
  Copying = 0
  ExposePlacement = false
  MarkerShape = 1
  MarkerSize = 0
  NumElements = 0
  Object = -> Extrude006
  OutputCompounding = 1
  PlacementsTo = -> Populate005
  Referencing = 0
  Type = lattice2PopulateCopies.LatticePopulateCopies
  isLattice = 0
FEATURE [Part::Compound] Compound010
  Links = -> [Part__Mirroring005,Sketch025]
FEATURE [Part::Extrusion] Extrude007
  Base = -> Compound010
  Dir = (0,0,1)
  DirMode = 2
  FaceMakerClass = Part::FaceMakerBullseye
  LengthFwd = 10
  LengthRev = 0
  Solid = true
  Symmetric = false
FEATURE [PartDesign::CoordinateSystem] Local_CS008
  AttacherType = Attacher::AttachEngine3D
  AttachmentOffset = pos=(0,20,0) rot=(0,0,1;0rad)
  AttachmentSupport = -> [XY_Plane003]
  MapMode = 5
  Placement = pos=(0,20,0) rot=(0,0,1;0rad)
  expr: .AttachmentOffset.Base.y = <<base_Sketch>>.Constraints.offset
FEATURE [PartDesign::CoordinateSystem] Local_CS009  label="face_section_LCS"
  AttacherType = Attacher::AttachEngine3D
  AttachmentOffset = pos=(319.563,20,0) rot=(0,0,1;0rad)
  AttachmentSupport = -> [XY_Plane]
  MapMode = 5
  Placement = pos=(319.563,20,0) rot=(0,0,1;0rad)
  expr: .AttachmentOffset.Base.x = <<mid_Sketch>>.Constraints.middle
  expr: .AttachmentOffset.Base.y = <<base_Sketch>>.Constraints.offset
FEATURE [PartDesign::CoordinateSystem] Local_CS006  label="sink1_placement"
  AttacherType = Attacher::AttachEngine3D
  AttachmentOffset = pos=(0,0,100) rot=(0,0,1;0rad)
  AttachmentSupport = -> [Local_CS009]
  MapMode = 5
  Placement = pos=(319.563,20,100) rot=(0,0,1;0rad)
  expr: .AttachmentOffset.Base.z = <<sink_placement>>.Placement.Base.z
FEATURE [PartDesign::CoordinateSystem] Local_CS007  label="sink2_placement"
  AttacherType = Attacher::AttachEngine3D
  AttachmentOffset = pos=(-639.126,0,0) rot=(0,0,1;0rad)
  AttachmentSupport = -> [Local_CS006]
  MapMode = 5
  Placement = pos=(-319.563,20,100) rot=(0,0,1;0rad)
  expr: .AttachmentOffset.Base.x = -<<mid_Sketch>>.Constraints.middle * 2
FEATURE [PartDesign::CoordinateSystem] Local_CS010  label="dropper_comp_fix1"
  AttacherType = Attacher::AttachEngine3D
  AttachmentOffset = pos=(0,0,1100) rot=(0,0,1;0rad)
  AttachmentSupport = -> [Local_CS009]
  MapMode = 5
  Placement = pos=(319.563,20,1100) rot=(0,0,1;0rad)
  expr: .AttachmentOffset.Base.z = <<Properties>>.modules_fix_height
FEATURE [PartDesign::CoordinateSystem] Local_CS011  label="dropper_comp_fix2"
  AttacherType = Attacher::AttachEngine3D
  AttachmentOffset = pos=(-639.126,0,0) rot=(0,0,1;0rad)
  AttachmentSupport = -> [Local_CS010]
  MapMode = 5
  Placement = pos=(-319.563,20,1100) rot=(0,0,1;0rad)
  expr: .AttachmentOffset.Base.x = -<<mid_Sketch>>.Constraints.middle * 2
FEATURE [Sketcher::SketchObject] Sketch032  label="dropper_fix_PP_base_sketch"
  ExternalGeometry = -> [Sketch021,Sketch025,Sketch]
  FullyConstrained = true
  sketch-geometry (12):
    g0: LineSegment StartX=0 StartY=11.2 StartZ=0 EndX=172.194 EndY=11.2 EndZ=0
    g1: LineSegment StartX=273.061 StartY=126 StartZ=0 EndX=251.134 EndY=126 EndZ=0
    g2: LineSegment StartX=251.134 StartY=126 StartZ=0 EndX=155.317 EndY=45.6 EndZ=0
    g3: LineSegment StartX=155.317 StartY=45.6 StartZ=0 EndX=0 EndY=45.6 EndZ=0
    g4: LineSegment StartX=172.194 StartY=8.2 StartZ=0 EndX=172.194 EndY=11.2 EndZ=0
    g5: LineSegment StartX=172.194 StartY=11.2 StartZ=0 EndX=174.122 EndY=8.90187 EndZ=0
    g6: LineSegment StartX=172.194 StartY=11.2 StartZ=0 EndX=273.061 EndY=95.8371 EndZ=0
    g7: LineSegment StartX=273.061 StartY=95.8371 StartZ=0 EndX=273.061 EndY=126 EndZ=0
    g8: LineSegment StartX=273.061 StartY=99.008 StartZ=0 EndX=266.261 EndY=99.008 EndZ=0
    g9: LineSegment StartX=266.261 StartY=99.008 StartZ=0 EndX=270.631 EndY=93.7989 EndZ=0
    g10: LineSegment StartX=155.317 StartY=20 StartZ=0 EndX=155.317 EndY=45.6 EndZ=0
    g11: LineSegment StartX=155.317 StartY=45.6 StartZ=0 EndX=171.773 EndY=25.9893 EndZ=0
  constraints (37):
    c: PointOnObject(g0,g-2)
    c: Horizontal(g0)
    c: Coincident(g0,g6)
    c: Coincident(g7,g1)
    c: Horizontal(g1)
    c: Coincident(g1,g2)
    c: Coincident(g2,g3)
    c: PointOnObject(g3,g-2)
    c: Horizontal(g3)
    c: PointOnObject(g4,g-4)
    c: Coincident(g4,g0)
    c: Vertical(g4)
    c: Coincident(g4,g5)
    c: PointOnObject(g5,g-3)
    c: Perpendicular(g-3,g5)
    c: Equal(g4,g5)
    c: DistanceY(g4,g4) = 3
    c: Coincident(g6,g7)
    c: Parallel(g6,g2)
    c: Parallel(g6,g-3)
    c: Vertical(g7)
    c: PointOnObject(g8,g7)
    c: Coincident(g8,g-5)
    c: Coincident(g8,g9)
    c: PointOnObject(g9,g6)
    c: Horizontal(g8)
    c: Perpendicular(g6,g9)
    c: Equal(g8,g9)
    c: DistanceY(g1,g-6) = 24
    c: Coincident(g10,g2)
    c: Vertical(g10)
    c: Coincident(g10,g11)
    c: PointOnObject(g11,g-6)
    c: Perpendicular(g-6,g11)
    c: Horizontal(g10,g-6)
    c: Equal(g10,g11)
    c: DistanceY(g10,g10) = 25.6
FEATURE [Part::Mirroring] Part__Mirroring009  label="Sketch032 (Mirror #10)"
  Base = (0,0,0)
  Normal = (1,0,0)
  Source = -> Sketch032
FEATURE [Part::FeaturePython] Connect004  # WARN: FeaturePython — macro-defined, semantics opaque (R4)
  Objects = -> [Part__Mirroring009,Sketch032]
  Tolerance = 0
FEATURE [PartDesign::SubShapeBinder] Binder007
  BindCopyOnChange = 0
  BindMode = 0
  ClaimChildren = true
  Context = -> Body004 [Binder007.]
  Fuse = false
  MakeFace = true
  OffsetFill = false
  OffsetIntersection = false
  OffsetJoinType = 0
  OffsetOpenResult = false
  PartialLoad = false
  Relative = true
  Support = -> [Connect004]
  _Version = 2
FEATURE [PartDesign::Pad] Pad007
  Direction = (0,0,1)
  Length = 5
  Length2 = 10
  Profile = -> Binder007
  Suppressed = false
  Type = 0
FEATURE [PartDesign::CoordinateSystem] Local_CS012
  AttacherType = Attacher::AttachEngine3D
  AttachmentSupport = -> [XY_Plane005]
  MapMode = 5
FEATURE [PartDesign::CoordinateSystem] Local_CS013  label="dropper_fix_PP_placement"
  AttacherType = Attacher::AttachEngine3D
  AttachmentOffset = pos=(0,0,3) rot=(0,0,1;0rad)
  AttachmentSupport = -> [XY_Plane003]
  MapMode = 5
  Placement = pos=(0,0,3) rot=(0,0,1;0rad)
FEATURE [Sketcher::SketchObject] Sketch033  label="bar_base_sketch"
  FullyConstrained = true
  expr: .Constraints.depth = <<base_Sketch>>.Constraints.offset - 3 mm
  sketch-geometry (17):
    g0: LineSegment StartX=0 StartY=16 StartZ=0 EndX=13 EndY=16 EndZ=0
    g1: LineSegment StartX=15 StartY=14 StartZ=0 EndX=15 EndY=3 EndZ=0
    g2: LineSegment StartX=18 StartY=0 StartZ=0 EndX=30 EndY=0 EndZ=0
    g3: LineSegment StartX=30 StartY=0 StartZ=0 EndX=30 EndY=1 EndZ=0
    g4: LineSegment StartX=30 StartY=1 StartZ=0 EndX=18 EndY=1 EndZ=0
    g5: LineSegment StartX=16 StartY=3 StartZ=0 EndX=16 EndY=14 EndZ=0
    g6: LineSegment StartX=13 StartY=17 StartZ=0 EndX=0 EndY=17 EndZ=0
    g7: ArcOfCircle CenterX=13 CenterY=14 CenterZ=0 NormalX=0 NormalY=0 NormalZ=1 AngleXU=0 Radius=2 StartAngle=2e-16 EndAngle=1.5708
    g8: GeomPoint X=15 Y=16 Z=0
    g9: ArcOfCircle CenterX=13 CenterY=14 CenterZ=0 NormalX=0 NormalY=0 NormalZ=1 AngleXU=0 Radius=3 StartAngle=0 EndAngle=1.5708
    g10: GeomPoint X=16 Y=17 Z=0
    g11: ArcOfCircle CenterX=18 CenterY=3 CenterZ=0 NormalX=0 NormalY=0 NormalZ=1 AngleXU=0 Radius=2 StartAngle=3.14159 EndAngle=4.71239
    g12: GeomPoint X=16 Y=1 Z=0
    g13: ArcOfCircle CenterX=18 CenterY=3 CenterZ=0 NormalX=0 NormalY=0 NormalZ=1 AngleXU=0 Radius=3 StartAngle=3.14159 EndAngle=4.71239
    g14: GeomPoint X=15 Y=0 Z=0
    g15: GeomPoint X=-30 Y=0 Z=0
    g16: GeomPoint X=-13 Y=16 Z=0
  constraints (40):
    c: PointOnObject(g0,g-2)
    c: Horizontal(g0)
    c: PointOnObject(g14,g-1)
    c: Vertical(g1)
    c: PointOnObject(g2,g-1)
    c: Coincident(g2,g3)
    c: Vertical(g3)
    c: Coincident(g3,g4)
    c: Horizontal(g4)
    c: Vertical(g5)
    c: PointOnObject(g6,g-2)
    c: Horizontal(g6)
    c: PointOnObject(g8,g0)
    c: PointOnObject(g8,g1)
    c: Tangent(g0,g7) = 1.5708
    c: Tangent(g1,g7) = 1.5708
    c: PointOnObject(g10,g5)
    c: PointOnObject(g10,g6)
    c: Tangent(g5,g9) = -1.5708
    c: Tangent(g6,g9) = -1.5708
    c: PointOnObject(g12,g4)
    c: PointOnObject(g12,g5)
    c: Tangent(g4,g11) = 1.5708
    c: Tangent(g5,g11) = 1.5708
    c: PointOnObject(g14,g1)
    c: PointOnObject(g14,g2)
    c: Tangent(g1,g13) = -1.5708
    c: Tangent(g2,g13) = -1.5708
    c: Coincident(g13,g11)
    c: Coincident(g7,g9)
    c: DistanceY(g3,g3) = 1  'thickness'
    c: Equal(g11,g7)
    c: Radius(g11) = 2  'r'
    c: Symmetric(g15,g2,g-2)
    c: DistanceX(g15,g2) = 60  'total_width'
    c: Symmetric(g16,g0,g-2)
    c: DistanceX(g16,g0) = 26  'inner_plane_width'
    c: DistanceX(g2,g2) = 12  'fix_plane'
    c: DistanceY(g6) = 17  'depth'
    c: DistanceX(g5) = 16
FEATURE [Part::Mirroring] Part__Mirroring010  label="Sketch033 (Mirror #11)"
  Base = (0,0,0)
  Normal = (1,0,0)
  Source = -> Sketch033
FEATURE [Part::FeaturePython] Connect005  # WARN: FeaturePython — macro-defined, semantics opaque (R4)
  Objects = -> [Part__Mirroring010,Sketch033]
  Tolerance = 0
FEATURE [PartDesign::SubShapeBinder] Binder008
  BindCopyOnChange = 0
  BindMode = 0
  ClaimChildren = true
  Context = -> Body005 [Binder008.]
  Fuse = false
  MakeFace = true
  OffsetFill = false
  OffsetIntersection = false
  OffsetJoinType = 0
  OffsetOpenResult = false
  PartialLoad = false
  Relative = false
  Support = -> [Connect005]
  _Version = 2
FEATURE [PartDesign::Pad] Pad008  label="bar_pad"
  Direction = (0,0,1)
  Length = 1272.25
  Length2 = 10
  Profile = -> Binder008
  Refine = true
  Suppressed = false
  Type = 0
  expr: Length = <<Dimensions>>.Constraints.width - 3 mm * 2
FEATURE [Sketcher::SketchObject] Sketch034  label="wall_fix_sketch"
  FullyConstrained = true
  sketch-geometry (5):
    g0: ArcOfCircle CenterX=0 CenterY=0 CenterZ=0 NormalX=0 NormalY=0 NormalZ=1 AngleXU=0 Radius=7.5 StartAngle=5.32983 EndAngle=7.85398
    g1: ArcOfCircle CenterX=5.5 CenterY=-7.74597 CenterZ=0 NormalX=0 NormalY=0 NormalZ=1 AngleXU=0 Radius=2 StartAngle=2.18823 EndAngle=3.14159
    g2: ArcOfCircle CenterX=0 CenterY=-12 CenterZ=0 NormalX=0 NormalY=0 NormalZ=1 AngleXU=0 Radius=3.5 StartAngle=4.71239 EndAngle=6.28319
    g3: LineSegment StartX=3.5 StartY=-12 StartZ=0 EndX=3.5 EndY=-7.74597 EndZ=0
    g4: GeomPoint X=0 Y=-4 Z=0
  constraints (14):
    c: Coincident(g0,g-1)
    c: PointOnObject(g0,g-2)
    c: PointOnObject(g2,g-2)
    c: PointOnObject(g2,g-2)
    c: Vertical(g3)
    c: Tangent(g3,g2) = -1.5708
    c: Tangent(g3,g1) = 1.5708
    c: Tangent(g1,g0) = 1.5708
    c: Diameter(g0) = 15
    c: Diameter(g2) = 7
    c: DistanceY(g2) = -12
    c: Radius(g1) = 2
    c: Symmetric(g0,g2,g4)
    c: DistanceY(g4) = -4  'center'
FEATURE [Part::Mirroring] Part__Mirroring011  label="Sketch034 (Mirror #12)"
  Base = (0,0,0)
  Normal = (1,0,0)
  Source = -> Sketch034
FEATURE [Part::FeaturePython] Connect006  # WARN: FeaturePython — macro-defined, semantics opaque (R4)
  Objects = -> [Part__Mirroring011,Sketch034]
  Tolerance = 0
FEATURE [Part::Extrusion] Extrude008
  Base = -> Connect006
  Dir = (0,0,1)
  DirMode = 2
  FaceMakerClass = Part::FaceMakerBullseye
  LengthFwd = 10
  LengthRev = 0
  Solid = true
  Symmetric = false
FEATURE [Sketcher::SketchObject] Sketch035  label="bar_fix_base_sketch"
  FullyConstrained = true
  Placement = pos=(0,0,0) rot=(0.57735,0.57735,0.57735;2.0944rad)
  sketch-geometry (2):
    g0: LineSegment StartX=0 StartY=40 StartZ=0 EndX=0 EndY=0 EndZ=0
    g1: LineSegment StartX=0 StartY=0 StartZ=0 EndX=50 EndY=0 EndZ=0
  constraints (6):
    c: PointOnObject(g0,g-2)
    c: Coincident(g0,g-1)
    c: Coincident(g0,g1)
    c: PointOnObject(g1,g-1)
    c: DistanceY(g0,g0) = 40  'bar_side'
    c: DistanceX(g1,g1) = 50  'comp_side'
FEATURE [PartDesign::SubShapeBinder] Binder009
  BindCopyOnChange = 0
  BindMode = 0
  ClaimChildren = true
  Context = -> Body006 [Binder009.]
  Fuse = false
  MakeFace = true
  OffsetFill = false
  OffsetIntersection = false
  OffsetJoinType = 0
  OffsetOpenResult = false
  PartialLoad = false
  Placement = pos=(0,0,0) rot=(0.57735,0.57735,0.57735;2.0944rad)
  Relative = false
  Support = -> [Sketch035]
  _Version = 2
FEATURE [PartDesign::FeaturePython] BaseBend002  label="bar_fix_BaseBend"  # WARN: FeaturePython — macro-defined, semantics opaque (R4)
  BendSide = 1
  BendSketch = -> Binder009
  MidPlane = true
  Reverse = false
  Suppressed = false
  length = 26
  radius = 2
  thickness = 0.7
  expr: length = <<bar_base_sketch>>.Constraints.inner_plane_width
FEATURE [Part::FeaturePython] LinearArray003  # WARN: FeaturePython — macro-defined, semantics opaque (R4)
  Alignment = 0
  CellStart = A1
  Count = 2
  Dir = (1,0,0)
  DirIsDriven = true
  DistributionLaw = 0
  DrivenProperty = 1
  EndInclusive = true
  ExposePlacement = false
  GeneratorMode = 0
  MarkerShape = 1
  MarkerSize = 50
  NumElements = 2
  OrientMode = 1
  Placement = pos=(-157.818,0,0) rot=(0,0,1;0rad)
  Point = (0,0,0)
  PointIsDriven = true
  Reverse = false
  SpanEnd = 315.635
  SpanStart = 0
  Step = 315.635
  Type = lattice2LinearArray.LinearArray
  VSGVersion = 1
  Values = 0.0 | 315.63501731982126
  ValuesSource = 2
  isLattice = 1
  expr: .Placement.Base.x = -SpanEnd / 2
  expr: SpanEnd = <<base_Sketch>>.Constraints.rivet_placement * 2
FEATURE [Part::FeaturePython] Populate009  label="Populate LinearArray001 with LinearArray003"  # WARN: FeaturePython — macro-defined, semantics opaque (R4)
  Copying = 0
  ExposePlacement = false
  MarkerShape = 1
  MarkerSize = 0
  NumElements = 4
  Object = -> LinearArray003
  OutputCompounding = 0
  Placement = pos=(24,-3,636.126) rot=(0.57735,-0.57735,-0.57735;4.18879rad)
  PlacementsTo = -> LinearArray001
  Referencing = 0
  Type = lattice2PopulateCopies.LatticePopulateCopies
  isLattice = 1
  expr: .Placement.Base.x = (<<bar_base_sketch>>.Constraints.total_width - <<bar_base_sketch>>.Constraints.fix_plane) / 2
  expr: .Placement.Base.z = <<mid_Sketch>>.Constraints.middle + <<side_Sketch>>.Constraints.distance - 3 mm
FEATURE [Part::FeaturePython] LinearArray004  # WARN: FeaturePython — macro-defined, semantics opaque (R4)
  Alignment = 0
  CellStart = A1
  Count = 2
  Dir = (1,0,0)
  DirIsDriven = true
  DistributionLaw = 0
  DrivenProperty = 1
  EndInclusive = true
  ExposePlacement = false
  GeneratorMode = 0
  MarkerShape = 1
  MarkerSize = 0
  NumElements = 2
  OrientMode = 1
  Placement = pos=(-636.126,17,220) rot=(0.707107,0,0.707107;3.14159rad)
  Point = (0,0,0)
  PointIsDriven = true
  Reverse = false
  SpanEnd = 663.5
  SpanStart = 0
  Step = 663.5
  Type = lattice2LinearArray.LinearArray
  VSGVersion = 1
  Values = 0.0 | 663.5
  ValuesSource = 2
  isLattice = 1
  expr: .Placement.Base.x = -(<<side_Sketch>>.Constraints.distance + <<mid_Sketch>>.Constraints.middle - 3 mm)
  expr: .Placement.Base.y = <<base_Sketch>>.Constraints.offset - 3 mm
FEATURE [Sketcher::SketchObject] Sketch036
  FullyConstrained = true
  sketch-geometry (3):
    g0: Circle CenterX=0 CenterY=45 CenterZ=0 NormalX=0 NormalY=0 NormalZ=1 AngleXU=0 Radius=1.7
    g1: Circle CenterX=10 CenterY=15 CenterZ=0 NormalX=0 NormalY=0 NormalZ=1 AngleXU=0 Radius=1.7
    g2: Circle CenterX=-10 CenterY=15 CenterZ=0 NormalX=0 NormalY=0 NormalZ=1 AngleXU=0 Radius=1.7
  constraints (8):
    c: Equal(g0,g2)
    c: Equal(g0,g1)
    c: Diameter(g0) = 3.4
    c: PointOnObject(g0,g-2)
    c: Symmetric(g2,g1,g-2)
    c: DistanceX(g2,g1) = 20
    c: DistanceY(g0) = 45
    c: DistanceY(g1) = 15
FEATURE [Part::FeaturePython] Placment002  label="Custom001"  # WARN: FeaturePython — macro-defined, semantics opaque (R4)
  ExposePlacement = true
  FlipZ = false
  Invert = false
  MarkerShape = 1
  MarkerSize = 10
  NumElements = 1
  Placement = pos=(0,0,0) rot=(0,0,1;3.14159rad)
  PlacementChoice = 0
  Type = lattice2Placement.LatticePlacement
  isLattice = 1
FEATURE [Part::FeaturePython] ArrayFromShape  label="Array from Sketch036"  # WARN: FeaturePython — macro-defined, semantics opaque (R4)
  CompoundTraversal = 1
  ExposePlacement = false
  MarkerShape = 1
  MarkerSize = 0
  NumElements = 3
  OrientElementIndex = 0
  OrientMode = 0
  Placement = pos=(0,0,-3) rot=(0,0,1;0rad)
  ShapeLink = -> Sketch036
  TranslateElementIndex = 0
  TranslateMode = 3
  Type = lattice2ArrayFromShape.LatticeArrayFromShape
  isLattice = 1
FEATURE [Part::FeaturePython] Populate010  label="Populate Custom001 with Array from Sketch036"  # WARN: FeaturePython — macro-defined, semantics opaque (R4)
  Copying = 0
  ExposePlacement = false
  MarkerShape = 1
  MarkerSize = 0
  NumElements = 3
  Object = -> ArrayFromShape
  OutputCompounding = 0
  PlacementsTo = -> Placment002
  Referencing = 0
  Type = lattice2PopulateCopies.LatticePopulateCopies
  isLattice = 1
FEATURE [Part::Cylinder] Cylinder  label="hole_3.4mm"
  Angle = 360
  AttacherType = Attacher::AttachEngine3D
  FirstAngle = 0
  Height = 5.5
  Radius = 1.7
  SecondAngle = 0
FEATURE [Sketcher::SketchObject] Sketch037
  FullyConstrained = true
  Placement = pos=(0,0,0) rot=(1,0,0;1.5708rad)
  expr: Constraints[10] = <<bar_base_sketch>>.Constraints.inner_plane_width - 7 mm
  sketch-geometry (9):
    g0: LineSegment StartX=-9.5 StartY=12 StartZ=0 EndX=9.5 EndY=12 EndZ=0
    g1: LineSegment StartX=9.5 StartY=12 StartZ=0 EndX=9.5 EndY=34 EndZ=0
    g2: LineSegment StartX=9.5 StartY=34 StartZ=0 EndX=-9.5 EndY=34 EndZ=0
    g3: LineSegment StartX=-9.5 StartY=34 StartZ=0 EndX=-9.5 EndY=12 EndZ=0
    g4: GeomPoint X=0 Y=23 Z=0
    g5: Circle CenterX=-9.5 CenterY=12 CenterZ=0 NormalX=0 NormalY=0 NormalZ=1 AngleXU=0 Radius=1.7
    g6: Circle CenterX=-9.5 CenterY=34 CenterZ=0 NormalX=0 NormalY=0 NormalZ=1 AngleXU=0 Radius=1.7
    g7: Circle CenterX=9.5 CenterY=34 CenterZ=0 NormalX=0 NormalY=0 NormalZ=1 AngleXU=0 Radius=1.7
    g8: Circle CenterX=9.5 CenterY=12 CenterZ=0 NormalX=0 NormalY=0 NormalZ=1 AngleXU=0 Radius=1.7
  constraints (21):
    c: Coincident(g0,g1)
    c: Coincident(g1,g2)
    c: Coincident(g2,g3)
    c: Coincident(g3,g0)
    c: Horizontal(g0)
    c: Horizontal(g2)
    c: Vertical(g1)
    c: Vertical(g3)
    c: Symmetric(g2,g0,g4)
    c: PointOnObject(g4,g-2)
    c: DistanceX(g2,g2) = 19
    c: DistanceY(g0) = 12
    c: DistanceY(g1,g1) = 22
    c: Coincident(g5,g0)
    c: Coincident(g6,g2)
    c: Coincident(g7,g1)
    c: Coincident(g8,g0)
    c: Equal(g8,g7)
    c: Equal(g8,g6)
    c: Equal(g8,g5)
    c: Diameter(g8) = 3.4
FEATURE [Part::Extrusion] Extrude009
  Base = -> Sketch037
  Dir = (0,-1,2e-16)
  DirMode = 2
  FaceMakerClass = Part::FaceMakerBullseye
  LengthFwd = 50
  LengthRev = 0
  Solid = true
  Symmetric = true
FEATURE [Part::FeaturePython] Placment003  label="Custom002"  # WARN: FeaturePython — macro-defined, semantics opaque (R4)
  ExposePlacement = true
  FlipZ = false
  Invert = false
  MarkerShape = 1
  MarkerSize = 10
  NumElements = 1
  Placement = pos=(0,16,0) rot=(0,0,1;0rad)
  PlacementChoice = 0
  Type = lattice2Placement.LatticePlacement
  isLattice = 1
  expr: .Placement.Base.y = <<bar_base_sketch>>.Constraints.depth - <<bar_base_sketch>>.Constraints.thickness
FEATURE [Part::FeaturePython] Placment004  label="Custom003"  # WARN: FeaturePython — macro-defined, semantics opaque (R4)
  ExposePlacement = true
  FlipZ = false
  Invert = false
  MarkerShape = 1
  MarkerSize = 10
  NumElements = 1
  Placement = pos=(0,16,1272.25) rot=(0,1,0;3.14159rad)
  PlacementChoice = 0
  Type = lattice2Placement.LatticePlacement
  isLattice = 1
  expr: .Placement.Base.y = <<Custom002>>.Placement.Base.y
  expr: .Placement.Base.z = <<bar_pad>>.Length
FEATURE [Part::FeaturePython] Populate013  label="Populate Populate LinearArray001 with LinearArray003 with hole_3.4mm"  # WARN: FeaturePython — macro-defined, semantics opaque (R4)
  Copying = 0
  ExposePlacement = false
  MarkerShape = 1
  MarkerSize = 0
  NumElements = 0
  Object = -> Cylinder
  OutputCompounding = 1
  PlacementsTo = -> Populate009
  Referencing = 0
  Type = lattice2PopulateCopies.LatticePopulateCopies
  isLattice = 0
FEATURE [Part::FeaturePython] Join001  # WARN: FeaturePython — macro-defined, semantics opaque (R4)
  ExposePlacement = false
  Interleave = false
  Links = -> [Placment003,Placment004]
  MarkerShape = 1
  MarkerSize = 0
  NumElements = 2
  Type = lattice2JoinArrays.JoinArrays
  isLattice = 1
FEATURE [Part::FeaturePython] Populate014  label="Populate Join001 with Extrude009"  # WARN: FeaturePython — macro-defined, semantics opaque (R4)
  Copying = 0
  ExposePlacement = false
  MarkerShape = 1
  MarkerSize = 0
  NumElements = 0
  Object = -> Extrude009
  OutputCompounding = 1
  PlacementsTo = -> Join001
  Referencing = 0
  Type = lattice2PopulateCopies.LatticePopulateCopies
  isLattice = 0
FEATURE [Part::FeaturePython] Populate015  label="Populate Array from Sketch036 with hole_3.4mm"  # WARN: FeaturePython — macro-defined, semantics opaque (R4)
  Copying = 0
  ExposePlacement = false
  MarkerShape = 1
  MarkerSize = 0
  NumElements = 0
  Object = -> Cylinder
  OutputCompounding = 1
  PlacementsTo = -> ArrayFromShape
  Referencing = 0
  Type = lattice2PopulateCopies.LatticePopulateCopies
  isLattice = 0
FEATURE [Part::Compound] Compound013
  Links = -> [Extrude009,Populate015]
FEATURE [Part::FeaturePython] Populate016  label="Populate Join001 with Populate Custom001 with Array from Sketch036"  # WARN: FeaturePython — macro-defined, semantics opaque (R4)
  Copying = 0
  ExposePlacement = false
  MarkerShape = 1
  MarkerSize = 0
  NumElements = 6
  Object = -> Populate010
  OutputCompounding = 0
  PlacementsTo = -> Join001
  Referencing = 0
  Type = lattice2PopulateCopies.LatticePopulateCopies
  isLattice = 1
FEATURE [Part::FeaturePython] Join  # WARN: FeaturePython — macro-defined, semantics opaque (R4)
  ExposePlacement = false
  Interleave = false
  Links = -> [Populate009,Populate016]
  MarkerShape = 1
  MarkerSize = 0
  NumElements = 10
  Type = lattice2JoinArrays.JoinArrays
  isLattice = 1
FEATURE [Part::FeaturePython] Populate011  label="Populate LinearArray004 with Join"  # WARN: FeaturePython — macro-defined, semantics opaque (R4)
  Copying = 0
  ExposePlacement = false
  MarkerShape = 1
  MarkerSize = 0
  NumElements = 20
  Object = -> Join
  OutputCompounding = 0
  PlacementsTo = -> LinearArray004
  Referencing = 0
  Type = lattice2PopulateCopies.LatticePopulateCopies
  isLattice = 1
FEATURE [Part::FeaturePython] Populate012  label="face_bar_fix"  # WARN: FeaturePython — macro-defined, semantics opaque (R4)
  Copying = 0
  ExposePlacement = false
  MarkerShape = 1
  MarkerSize = 0
  NumElements = 0
  Object = -> Cylinder
  OutputCompounding = 1
  PlacementsTo = -> Populate011
  Referencing = 0
  Type = lattice2PopulateCopies.LatticePopulateCopies
  isLattice = 0
FEATURE [PartDesign::CoordinateSystem] Local_CS014  label="bar1_placement"
  AttacherType = Attacher::AttachEngine3D
  AttachmentSupport = -> [LinearArray004]
  MapMode = 1
  Placement = pos=(-636.126,17,220) rot=(0.707107,0,0.707107;3.14159rad)
FEATURE [PartDesign::CoordinateSystem] Local_CS015  label="bar2_placement"
  AttacherType = Attacher::AttachEngine3D
  AttachmentSupport = -> [LinearArray004]
  MapMode = 1
  Placement = pos=(-636.126,17,883.5) rot=(0.707107,0,0.707107;3.14159rad)
FEATURE [PartDesign::CoordinateSystem] Local_CS016  label="bar_orig"
  AttacherType = Attacher::AttachEngine3D
  MapMode = 5
FEATURE [PartDesign::CoordinateSystem] Local_CS017  label="bar_fix_orig"
  AttacherType = Attacher::AttachEngine3D
  AttachmentOffset = pos=(0,0,0) rot=(0,0,1;3.14159rad)
  MapMode = 5
  Placement = pos=(0,0,0) rot=(0,0,1;3.14159rad)
FEATURE [PartDesign::CoordinateSystem] Local_CS018  label="bar_top"
  AttacherType = Attacher::AttachEngine3D
  AttachmentOffset = pos=(0,0,1272.25) rot=(0,-1,0;3.14159rad)
  MapMode = 5
  Placement = pos=(0,0,1272.25) rot=(0,1,0;3.14159rad)
  expr: .AttachmentOffset.Base.z = <<bar_pad>>.Length
FEATURE [Part::FeaturePython] LinearArray005  # WARN: FeaturePython — macro-defined, semantics opaque (R4)
  Alignment = 0
  CellStart = A1
  Count = 2
  Dir = (1,0,0)
  DirIsDriven = true
  DistributionLaw = 0
  DrivenProperty = 1
  EndInclusive = true
  ExposePlacement = false
  GeneratorMode = 0
  MarkerShape = 1
  MarkerSize = 0
  NumElements = 2
  OrientMode = 1
  Placement = pos=(0,17,636.126) rot=(0.57735,-0.57735,0.57735;2.0944rad)
  Point = (0,0,0)
  PointIsDriven = true
  Reverse = false
  SpanEnd = 539.126
  SpanStart = -539.126
  Step = 1078.25
  Type = lattice2LinearArray.LinearArray
  VSGVersion = 1
  Values = -539.1259687141459 | 539.1259687141459
  ValuesSource = 2
  isLattice = 1
  expr: .Placement.Base.y = <<bar_base_sketch>>.Constraints.depth
  expr: .Placement.Base.z = <<mid_Sketch>>.Constraints.middle + <<side_Sketch>>.Constraints.distance - 3 mm
  expr: SpanEnd = <<Dimensions>>.Constraints.width / 2 - 100 mm
  expr: SpanStart = -SpanEnd
FEATURE [Part::FeaturePython] Populate017  label="Populate LinearArray005 with Extrude008"  # WARN: FeaturePython — macro-defined, semantics opaque (R4)
  Copying = 0
  ExposePlacement = false
  MarkerShape = 1
  MarkerSize = 0
  NumElements = 0
  Object = -> Extrude008
  OutputCompounding = 1
  Placement = pos=(-4,0,0) rot=(0,0,1;0rad)
  PlacementsTo = -> LinearArray005
  Referencing = 0
  Type = lattice2PopulateCopies.LatticePopulateCopies
  isLattice = 0
  expr: .Placement.Base.x = <<wall_fix_sketch>>.Constraints.center
FEATURE [Sketcher::SketchObject] Sketch038
  AttachmentOffset = pos=(-0.5,0,0) rot=(0,1,0;1.5708rad)
  ExternalGeometry = -> [Sketch012]
  FullyConstrained = true
  MapMode = 7
  Placement = pos=(164.314,0.383022,0) rot=(0.889126,0.323616,0.323616;1.68804rad)
  sketch-geometry (6):
    g0: LineSegment StartX=-14.0901 StartY=73 StartZ=0 EndX=5.90993 EndY=73 EndZ=0
    g1: LineSegment StartX=5.90993 StartY=73 StartZ=0 EndX=5.90993 EndY=88 EndZ=0
    g2: LineSegment StartX=171.749 StartY=73 StartZ=0 EndX=191.749 EndY=73 EndZ=0
    g3: LineSegment StartX=191.749 StartY=73 StartZ=0 EndX=191.749 EndY=88 EndZ=0
    g4: LineSegment StartX=0.909926 StartY=80 StartZ=0 EndX=5.90993 EndY=80 EndZ=0
    g5: LineSegment StartX=201.749 StartY=80 StartZ=0 EndX=191.749 EndY=80 EndZ=0
  constraints (20):
    c: Horizontal(g0)
    c: Coincident(g0,g1)
    c: Vertical(g1)
    c: Horizontal(g2)
    c: Coincident(g2,g3)
    c: Vertical(g3)
    c: Horizontal(g2,g0)
    c: Equal(g1,g3)
    c: Equal(g0,g2)
    c: DistanceY(g0) = 73
    c: Coincident(g4,g-3)
    c: PointOnObject(g4,g1)
    c: Horizontal(g4)
    c: Coincident(g5,g-3)
    c: PointOnObject(g5,g3)
    c: Horizontal(g5)
    c: DistanceX(g4,g4) = 5
    c: DistanceX(g2,g2) = 20
    c: DistanceY(g3,g3) = 15
    c: DistanceX(g5,g5) = 10
FEATURE [Sketcher::SketchObject] Sketch039
  ExternalGeometry = -> [Sketch013]
  FullyConstrained = true
  Placement = pos=(0,0.5,0) rot=(1,0,0;1.5708rad)
  sketch-geometry (4):
    g0: LineSegment StartX=138.725 StartY=73 StartZ=0 EndX=158.725 EndY=73 EndZ=0
    g1: LineSegment StartX=158.725 StartY=73 StartZ=0 EndX=158.725 EndY=113 EndZ=0
    g2: LineSegment StartX=138.725 StartY=21 StartZ=0 EndX=158.725 EndY=21 EndZ=0
    g3: LineSegment StartX=158.725 StartY=21 StartZ=0 EndX=158.725 EndY=61 EndZ=0
  constraints (15):
    c: Horizontal(g0)
    c: Coincident(g0,g1)
    c: Vertical(g1)
    c: DistanceY(g0) = 73
    c: DistanceX(g0,g-3) = 5
    c: DistanceX(g0,g0) = 20
    c: DistanceY(g1,g1) = 40
    c: DistanceY(g0,g-3) = 7
    c: Horizontal(g2)
    c: Coincident(g2,g3)
    c: Vertical(g3)
    c: Vertical(g2,g0)
    c: Equal(g2,g0)
    c: Equal(g3,g1)
    c: DistanceY(g2,g0) = 52
FEATURE [App::DocumentObjectGroup] Group001  label="sketches"
  Group = -> [Sketch003,Sketch004,Sketch020,Sketch022,Sketch023,Sketch029,Binder002,Sketch036,Sketch038,Sketch039,Sketch]
FEATURE [Part::FeaturePython] Placment005  # WARN: FeaturePython — macro-defined, semantics opaque (R4)
  AttacherType = Attacher::AttachEngine3D
  ExposePlacement = true
  MapMode = 49
  MarkerShape = 1
  MarkerSize = 20
  NumElements = 1
  Placement = pos=(168.841,4.18185,73) rot=(0.889126,0.323616,0.323616;1.68804rad)
  Type = lattice2AttachablePlacement.AttachablePlacement
  isLattice = 1
FEATURE [Part::FeaturePython] Placment006  # WARN: FeaturePython — macro-defined, semantics opaque (R4)
  AttacherType = Attacher::AttachEngine3D
  ExposePlacement = true
  MapMode = 49
  MarkerShape = 1
  MarkerSize = 20
  NumElements = 1
  Placement = pos=(158.725,0.5,73) rot=(1,0,0;1.5708rad)
  Type = lattice2AttachablePlacement.AttachablePlacement
  isLattice = 1
FEATURE [Part::FeaturePython] PlacementSubsequence001  # WARN: FeaturePython — macro-defined, semantics opaque (R4)
  Base = -> Placment005
  CycleMode = 0
  ExposePlacement = false
  MarkerShape = 1
  MarkerSize = 0
  NumElements = 2
  Type = lattice2AttachablePlacement.AttachedPlacementSubsequence
  isLattice = 1
FEATURE [Part::FeaturePython] Mirror  label="Mirror of Join002"  # WARN: FeaturePython — macro-defined, semantics opaque (R4)
  ExposePlacement = false
  FlipX = true
  FlipY = false
  FlipZ = false
  MarkerShape = 1
  MarkerSize = 0
  NumElements = 2
  Object = -> PlacementSubsequence001
  ObjectTraversal = 0
  Type = lattice2Mirror.LatticeMirror
  isLattice = 1
FEATURE [Part::FeaturePython] Placment007  label="sink_placement"  # WARN: FeaturePython — macro-defined, semantics opaque (R4)
  ExposePlacement = true
  FlipZ = false
  Invert = false
  MarkerShape = 1
  MarkerSize = 20
  NumElements = 1
  Placement = pos=(0,20,100) rot=(0,0,1;0rad)
  PlacementChoice = 0
  Type = lattice2Placement.LatticePlacement
  isLattice = 1
  expr: .Placement.Base.y = <<base_Sketch>>.Constraints.offset
  expr: .Placement.Base.z = <<Properties>>.bottom_cut_height
FEATURE [Part::FeaturePython] Populate022  label="Populate Populate Populate LinearArray with Populate LinearArray001 with PlacementSubsequence with Custom with module_Body"  # WARN: FeaturePython — macro-defined, semantics opaque (R4)
  Copying = 0
  ExposePlacement = false
  MarkerShape = 1
  MarkerSize = 0
  NumElements = 0
  Object = -> Link001
  OutputCompounding = 1
  PlacementsTo = -> Populate002
  Referencing = 0
  Type = lattice2PopulateCopies.LatticePopulateCopies
  isLattice = 0
FEATURE [PartDesign::CoordinateSystem] Local_CS019
  AttacherType = Attacher::AttachEngine3D
  MapMode = 5
FEATURE [App::Part] Part  label="modules"
  Group = -> [Populate022,Local_CS019]
  Origin = -> Origin009
FEATURE [Sketcher::SketchObject] Sketch040  label="sink_front_sketch"
  FullyConstrained = true
  expr: Constraints[2] = <<base_Sketch>>.Constraints.face / 2
  expr: Constraints[3] = -<<mid_Sketch>>.Constraints.middle
  sketch-geometry (5):
    g0: LineSegment StartX=-319.563 StartY=0 StartZ=0 EndX=164.635 EndY=0 EndZ=0
    g1: LineSegment StartX=-309.563 StartY=-35 StartZ=0 EndX=204.635 EndY=-35 EndZ=0
    g2: LineSegment StartX=204.635 StartY=-35 StartZ=0 EndX=204.635 EndY=35 EndZ=0
    g3: LineSegment StartX=204.635 StartY=35 StartZ=0 EndX=-309.563 EndY=35 EndZ=0
    g4: LineSegment StartX=-309.563 StartY=35 StartZ=0 EndX=-309.563 EndY=-35 EndZ=0
  constraints (18):
    c: PointOnObject(g0,g-1)
    c: PointOnObject(g0,g-1)
    c: DistanceX(g0) = 164.635
    c: DistanceX(g0) = -319.563
    c: Coincident(g1,g2)
    c: Coincident(g2,g3)
    c: Coincident(g3,g4)
    c: Coincident(g4,g1)
    c: Horizontal(g1)
    c: Horizontal(g3)
    c: Vertical(g2)
    c: Vertical(g4)
    c: DistanceY(g2) = 35
    c: DistanceX(g0,g2) = 40
    c: DistanceY(g1) = -35
    c: DistanceX(g0,g3) = 10
    c: DistanceX(g1,g-1) = 309.563  'left'
    c: DistanceX(g-1,g1) = 204.635  'right'
FEATURE [PartDesign::CoordinateSystem] Local_CS020
  AttacherType = Attacher::AttachEngine3D
  AttachmentOffset = pos=(0,3,0) rot=(0,0,1;0rad)
  AttachmentSupport = -> [XY_Plane008]
  MapMode = 5
  Placement = pos=(0,3,0) rot=(0,0,1;0rad)
FEATURE [PartDesign::SubShapeBinder] Binder010
  BindCopyOnChange = 0
  BindMode = 0
  ClaimChildren = true
  Context = -> Body007 [Binder010.]
  Fuse = false
  MakeFace = true
  OffsetFill = false
  OffsetIntersection = false
  OffsetJoinType = 0
  OffsetOpenResult = false
  PartialLoad = false
  Placement = pos=(0,0,0) rot=(1,0,0;1.5708rad)
  Relative = false
  Support = -> [Sketch040]
  _Version = 2
FEATURE [Sketcher::SketchObject] Sketch042  label="sink_back_base_Sketch"
  ExternalGeometry = -> [Binder010]
  FullyConstrained = false
  MapMode = 5
  Placement = pos=(0,0,0) rot=(0.57735,0.57735,0.57735;2.0944rad)
  sketch-geometry (11):
    g0: LineSegment StartX=0 StartY=-33.9589 StartZ=0 EndX=7.8e-15 EndY=35 EndZ=0
    g1: LineSegment StartX=7.8e-15 StartY=35 StartZ=0 EndX=-0.5 EndY=35 EndZ=0
    g2: LineSegment StartX=-0.5 StartY=35 StartZ=0 EndX=-0.5 EndY=-33.9589 EndZ=0
    g3: LineSegment StartX=0.566059 StartY=-36.0067 StartZ=0 EndX=3.27471 EndY=-37.9034 EndZ=0
    g4: LineSegment StartX=3.27471 StartY=-37.9034 StartZ=0 EndX=3.5615 EndY=-37.4938 EndZ=0
    g5: LineSegment StartX=3.5615 StartY=-37.4938 StartZ=0 EndX=0.852847 EndY=-35.5972 EndZ=0
    g6: ArcOfCircle CenterX=2 CenterY=-33.9589 CenterZ=0 NormalX=0 NormalY=0 NormalZ=1 AngleXU=0 Radius=2 StartAngle=3.14159 EndAngle=4.10152
    g7: GeomPoint X=0 Y=-35 Z=0
    g8: ArcOfCircle CenterX=2 CenterY=-33.9589 CenterZ=0 NormalX=0 NormalY=0 NormalZ=1 AngleXU=0 Radius=2.5 StartAngle=3.14159 EndAngle=4.10152
    g9: GeomPoint X=-0.5 Y=-35.2603 Z=0
    g10: LineSegment StartX=0.566059 StartY=-36.0067 StartZ=0 EndX=0.852847 EndY=-35.5972 EndZ=0
  constraints (26):
    c: PointOnObject(g7,g-2)
    c: Coincident(g0,g1)
    c: Horizontal(g1)
    c: Coincident(g1,g2)
    c: Vertical(g2)
    c: Coincident(g3,g4)
    c: Coincident(g4,g5)
    c: PointOnObject(g7,g0)
    c: PointOnObject(g7,g5)
    c: Tangent(g0,g6) = 1.5708
    c: Tangent(g5,g6) = 1.5708
    c: PointOnObject(g9,g2)
    c: PointOnObject(g9,g3)
    c: Tangent(g2,g8) = -1.5708
    c: Tangent(g3,g8) = -1.5708
    c: Coincident(g8,g6)
    c: DistanceX(g1,g1) = 0.5
    c: Perpendicular(g5,g4)
    c: Perpendicular(g3,g4)
    c: Radius(g6) = 2
    c: Angle(g5) = 2.53073
    c: Coincident(g10,g8)
    c: Angle(g5,g-1) = 0.610865  'angle'
    c: Coincident(g10,g6)
    c: Coincident(g0,g-4)
    c: PointOnObject(g-3,g5)
FEATURE [Sketcher::SketchObject] Sketch041
  AttachmentOffset = pos=(0,0,-35) rot=(1,0,0;-0.610865rad)
  AttachmentSupport = -> [XY_Plane008]
  ExternalGeometry = -> [Sketch042,Binder010]
  FullyConstrained = true
  MapMode = 5
  Placement = pos=(0,0,-35) rot=(1,0,0;5.67232rad)
  expr: .AttachmentOffset.Rotation.Angle = -<<sink_back_base_Sketch>>.Constraints.angle
  sketch-geometry (4):
    g0: LineSegment StartX=-309.563 StartY=1.04113 StartZ=0 EndX=204.635 EndY=1.04113 EndZ=0
    g1: LineSegment StartX=204.635 StartY=1.04113 StartZ=0 EndX=204.635 EndY=26.0411 EndZ=0
    g2: LineSegment StartX=204.635 StartY=26.0411 StartZ=0 EndX=-309.563 EndY=66.0411 EndZ=0
    g3: LineSegment StartX=-309.563 StartY=66.0411 StartZ=0 EndX=-309.563 EndY=1.04113 EndZ=0
  constraints (13):
    c: Coincident(g0,g1)
    c: Coincident(g1,g2)
    c: Coincident(g2,g3)
    c: Horizontal(g0)
    c: Vertical(g1)
    c: Vertical(g3)
    c: Coincident(g0,g3)
    c: PointOnObject(g-3,g0)
    c: PointOnObject(g-4,g1)
    c: PointOnObject(g-5,g3)
    c: DistanceY(g1,g2) = 40
    c: DistanceY(g1,g1) = 25
    c: Distance(g2) = 515.751  'end'
FEATURE [Sketcher::SketchObject] Sketch043
  AttachmentSupport = -> [Sketch041]
  ExternalGeometry = -> [Sketch041]
  FullyConstrained = true
  MapMode = 7
  Placement = pos=(204.635,21.3316,-49.9366) rot=(0.593097,0.556507,0.581839;2.03146rad)
  sketch-geometry (6):
    g0: LineSegment StartX=2e-16 StartY=-8.9e-15 StartZ=0 EndX=-0.286208 EndY=-0.409982 EndZ=0
    g1: ArcOfCircle CenterX=1.14483 CenterY=1.63993 CenterZ=0 NormalX=0 NormalY=0 NormalZ=1 AngleXU=0 Radius=2 StartAngle=4.10294 EndAngle=5.67374
    g2: ArcOfCircle CenterX=1.14483 CenterY=1.63993 CenterZ=0 NormalX=0 NormalY=0 NormalZ=1 AngleXU=0 Radius=2.5 StartAngle=4.10294 EndAngle=5.67374
    g3: LineSegment StartX=2.78476 StartY=0.495097 StartZ=0 EndX=16.4011 EndY=20 EndZ=0
    g4: LineSegment StartX=16.4011 StartY=20 StartZ=0 EndX=16.8111 EndY=19.7138 EndZ=0
    g5: LineSegment StartX=16.8111 StartY=19.7138 StartZ=0 EndX=3.19474 EndY=0.208889 EndZ=0
  constraints (16):
    c: Coincident(g0,g-3)
    c: Coincident(g1,g0)
    c: Coincident(g2,g1)
    c: Coincident(g2,g0)
    c: Tangent(g1,g3) = -1.5708
    c: Coincident(g3,g4)
    c: Coincident(g4,g5)
    c: Perpendicular(g-3,g0)
    c: Perpendicular(g1,g0)
    c: Tangent(g5,g2) = 1.5708
    c: Distance(g0) = 0.5
    c: Perpendicular(g3,g4)
    c: Perpendicular(g5,g4)
    c: Angle(g3,g-3) = 1.5708
    c: Radius(g1) = 2
    c: DistanceY(g3) = 20
FEATURE [PartDesign::Pad] Pad009  label="sink_back_base_Pad009"
  Direction = (1,0,0)
  Length = 204.635
  Length2 = 309.563
  Placement = pos=(0,0,0) rot=(0.57735,0.57735,0.57735;2.0944rad)
  Profile = -> Sketch042
  ReferenceAxis = -> Sketch042 [N_Axis]
  Suppressed = false
  Type = 4
  expr: Length = <<sink_front_sketch>>.Constraints.right
  expr: Length2 = <<sink_front_sketch>>.Constraints.left
FEATURE [PartDesign::Pad] Pad010
  BaseFeature = -> Pad009
  Direction = (0,0.573576,0.819152)
  Length = 0.5
  Length2 = 10
  Placement = pos=(0,0,0) rot=(0.57735,0.57735,0.57735;2.0944rad)
  Profile = -> Sketch041
  ReferenceAxis = -> Sketch041 [N_Axis]
  Reversed = true
  Suppressed = false
  Type = 0
FEATURE [Sketcher::SketchObject] Sketch044
  ExternalGeometry = -> [Sketch]
  FullyConstrained = true
  sketch-geometry (5):
    g0: LineSegment StartX=-319.563 StartY=150 StartZ=0 EndX=319.563 EndY=150 EndZ=0
    g1: LineSegment StartX=319.563 StartY=150 StartZ=0 EndX=319.563 EndY=0 EndZ=0
    g2: LineSegment StartX=319.563 StartY=0 StartZ=0 EndX=-319.563 EndY=0 EndZ=0
    g3: LineSegment StartX=-319.563 StartY=0 StartZ=0 EndX=-319.563 EndY=150 EndZ=0
    g4: LineSegment StartX=-164.635 StartY=20 StartZ=0 EndX=-319.563 EndY=150 EndZ=0
  constraints (13):
    c: PointOnObject(g1,g-1)
    c: Vertical(g1)
    c: Coincident(g1,g2)
    c: PointOnObject(g2,g-1)
    c: Coincident(g2,g3)
    c: Vertical(g3)
    c: Symmetric(g4,g-3,g-2)
    c: Symmetric(g4,g-3,g-2)
    c: PointOnObject(g0,g4)
    c: Horizontal(g0)
    c: Coincident(g1,g0)
    c: Coincident(g3,g0)
    c: Coincident(g0,g-3)
FEATURE [PartDesign::SubShapeBinder] Binder011  label="drain_holer_link"
  BindCopyOnChange = 0
  BindMode = 0
  ClaimChildren = true
  Fuse = false
  MakeFace = true
  OffsetFill = false
  OffsetIntersection = false
  OffsetJoinType = 0
  OffsetOpenResult = false
  PartialLoad = false
  Relative = false
  Support = -> [Sketch045]
  _Version = 2
FEATURE [Part::Mirroring] Part__Mirroring013  label="Binder011 (Mirror #14)"
  Base = (0,0,0)
  Normal = (1,0,0)
  Source = -> Binder011
FEATURE [Part::FeaturePython] Connect007  # WARN: FeaturePython — macro-defined, semantics opaque (R4)
  Objects = -> [Binder011,Part__Mirroring013]
  Tolerance = 0
FEATURE [Part::FeaturePython] Placment008  # WARN: FeaturePython — macro-defined, semantics opaque (R4)
  AttacherType = Attacher::AttachEngine3D
  AttachmentOffset = pos=(0,0,10) rot=(0.707107,0,0.707107;3.14159rad)
  ExposePlacement = true
  MapMode = 7
  MarkerShape = 1
  MarkerSize = 20
  NumElements = 1
  Placement = pos=(78.5328,88.0194,-1e-15) rot=(0.249244,0.684791,-0.684791;3.63013rad)
  Type = lattice2AttachablePlacement.AttachablePlacement
  isLattice = 1
FEATURE [Part::FeaturePython] Mirror002  label="Mirror002 of Placment008"  # WARN: FeaturePython — macro-defined, semantics opaque (R4)
  ExposePlacement = false
  FlipX = true
  FlipY = false
  FlipZ = false
  MarkerShape = 1
  MarkerSize = 20
  NumElements = 1
  Object = -> Placment008
  ObjectTraversal = 0
  Type = lattice2Mirror.LatticeMirror
  isLattice = 1
FEATURE [Part::FeaturePython] Join005  # WARN: FeaturePython — macro-defined, semantics opaque (R4)
  ExposePlacement = false
  Interleave = false
  Links = -> [Placment008,Mirror002]
  MarkerShape = 1
  MarkerSize = 0
  NumElements = 2
  Type = lattice2JoinArrays.JoinArrays
  isLattice = 1
FEATURE [Part::FeaturePython] LinearArray006  # WARN: FeaturePython — macro-defined, semantics opaque (R4)
  Alignment = 0
  CellStart = A1
  Count = 2
  Dir = (0,0,1)
  DirIsDriven = true
  DistributionLaw = 0
  DrivenProperty = 1
  EndInclusive = true
  ExposePlacement = false
  GeneratorMode = 0
  MarkerShape = 1
  MarkerSize = 0
  NumElements = 2
  OrientMode = 0
  Point = (0,0,0)
  PointIsDriven = true
  Reverse = false
  SpanEnd = 94
  SpanStart = 77
  Step = 17
  Type = lattice2LinearArray.LinearArray
  VSGVersion = 1
  Values = 77.0 | 94.0
  ValuesSource = 2
  isLattice = 1
FEATURE [Part::FeaturePython] Populate024  label="Populate LinearArray006 with Join005"  # WARN: FeaturePython — macro-defined, semantics opaque (R4)
  Copying = 0
  ExposePlacement = false
  MarkerShape = 1
  MarkerSize = 0
  NumElements = 4
  Object = -> Join005
  OutputCompounding = 0
  PlacementsTo = -> LinearArray006
  Referencing = 0
  Type = lattice2PopulateCopies.LatticePopulateCopies
  isLattice = 1
FEATURE [Part::FeaturePython] Populate025  label="Populate Populate LinearArray006 with Join005 with hole_3.4mm"  # WARN: FeaturePython — macro-defined, semantics opaque (R4)
  Copying = 0
  ExposePlacement = false
  MarkerShape = 1
  MarkerSize = 0
  NumElements = 0
  Object = -> Cylinder
  OutputCompounding = 1
  PlacementsTo = -> Populate024
  Referencing = 0
  Type = lattice2PopulateCopies.LatticePopulateCopies
  isLattice = 0
FEATURE [Sketcher::SketchObject] Sketch046
  FullyConstrained = true
  expr: .Constraints.door_rotation_axis_d = 3.5
  sketch-geometry (1):
    g0: Circle CenterX=10 CenterY=23.1324 CenterZ=0 NormalX=0 NormalY=0 NormalZ=1 AngleXU=0 Radius=1.75
  constraints (3):
    c: DistanceY(g0) = 23.1324  'door_offset'
    c: Diameter(g0) = 3.5  'door_rotation_axis_d'
    c: DistanceX(g0) = 10
FEATURE [Sketcher::SketchObject] Sketch047
  FullyConstrained = false
  sketch-geometry (5):
    g0: LineSegment StartX=-16.0768 StartY=11.7242 StartZ=0 EndX=-16.0768 EndY=0 EndZ=0
    g1: LineSegment StartX=-16.0768 StartY=0 StartZ=0 EndX=16.0768 EndY=0 EndZ=0
    g2: LineSegment StartX=16.0768 StartY=0 StartZ=0 EndX=16.0768 EndY=11.7242 EndZ=0
    g3: LineSegment StartX=16.0768 StartY=11.7242 StartZ=0 EndX=-16.0768 EndY=11.7242 EndZ=0
    g4: GeomPoint X=0 Y=5.8621 Z=0
  constraints (11):
    c: Coincident(g0,g1)
    c: Coincident(g1,g2)
    c: Coincident(g2,g3)
    c: Coincident(g3,g0)
    c: Vertical(g0)
    c: Vertical(g2)
    c: Horizontal(g1)
    c: Horizontal(g3)
    c: Symmetric(g2,g0,g4)
    c: PointOnObject(g4,g-2)
    c: PointOnObject(g1,g-1)
FEATURE [Sketcher::SketchObject] Sketch049
  FullyConstrained = false
  sketch-geometry (1):
    g0: Circle CenterX=0 CenterY=4.74044 CenterZ=0 NormalX=0 NormalY=0 NormalZ=1 AngleXU=0 Radius=1.75
  constraints (2):
    c: PointOnObject(g0,g-2)
    c: Diameter(g0) = 3.5
FEATURE [Sketcher::SketchObject] Sketch048
  ExternalGeometry = -> [Sketch049]
  FullyConstrained = true
  sketch-geometry (4):
    g0: ArcOfCircle CenterX=0 CenterY=4.74044 CenterZ=0 NormalX=0 NormalY=0 NormalZ=1 AngleXU=0 Radius=7 StartAngle=5.53923 EndAngle=8.02573
    g1: LineSegment StartX=-40 StartY=6e-16 StartZ=0 EndX=5.15055 EndY=0 EndZ=0
    g2: ArcOfCircle CenterX=50.0751 CenterY=-283.949 CenterZ=0 NormalX=0 NormalY=0 NormalZ=1 AngleXU=0 Radius=300 StartAngle=1.74254 EndAngle=1.86835
    g3: ArcOfCircle CenterX=-37 CenterY=2e-16 CenterZ=0 NormalX=0 NormalY=0 NormalZ=1 AngleXU=0 Radius=3 StartAngle=1.86835 EndAngle=3.14159
  constraints (11):
    c: PointOnObject(g0,g-1)
    c: PointOnObject(g1,g-1)
    c: Coincident(g1,g0)
    c: Tangent(g2,g0) = -1.5708
    c: Perpendicular(g3,g1) = 1.5708
    c: Tangent(g3,g2) = -1.5708
    c: Radius(g3) = 3
    c: Radius(g0) = 7
    c: DistanceX(g1,g-1) = 40
    c: Coincident(g0,g-3)
    c: Radius(g2) = 300
FEATURE [PartDesign::SubShapeBinder] Binder013
  BindCopyOnChange = 0
  BindMode = 0
  ClaimChildren = true
  Context = -> Body010 [Binder013.]
  Fuse = false
  MakeFace = true
  OffsetFill = false
  OffsetIntersection = false
  OffsetJoinType = 0
  OffsetOpenResult = false
  PartialLoad = false
  Relative = false
  Support = -> [Sketch048]
  _Version = 2
FEATURE [PartDesign::Pad] Pad012
  Direction = (0,0,1)
  Length = 13
  Length2 = 10
  Midplane = true
  Profile = -> Binder013
  Suppressed = false
  Type = 0
FEATURE [PartDesign::SubShapeBinder] Binder014
  BindCopyOnChange = 0
  BindMode = 0
  ClaimChildren = false
  Context = -> Body010 [Binder014.]
  Fuse = false
  MakeFace = true
  OffsetFill = false
  OffsetIntersection = false
  OffsetJoinType = 0
  OffsetOpenResult = false
  PartialLoad = false
  Relative = true
  Support = -> [Sketch049]
  _Version = 2
FEATURE [PartDesign::Pocket] Pocket004
  BaseFeature = -> Pad012
  Direction = (0,0,-1)
  Length = 5
  Length2 = 5
  Midplane = true
  Profile = -> Binder014
  Suppressed = false
  Type = 1
FEATURE [PartDesign::SubShapeBinder] Binder015
  BindCopyOnChange = 0
  BindMode = 0
  ClaimChildren = false
  Context = -> Body009 [Binder015.]
  Fuse = false
  MakeFace = true
  OffsetFill = false
  OffsetIntersection = false
  OffsetJoinType = 0
  OffsetOpenResult = false
  PartialLoad = false
  Relative = true
  Support = -> [Sketch046]
  _Version = 2
FEATURE [Sketcher::SketchObject] Sketch050
  AttachmentOffset = pos=(0,0,-13) rot=(0,0,1;0rad)
  ExternalGeometry = -> [Binder015]
  FullyConstrained = true
  MapMode = 5
  Placement = pos=(0,0,-13) rot=(0,0,1;0rad)
  sketch-geometry (4):
    g0: LineSegment StartX=-15 StartY=-1.8e-15 StartZ=0 EndX=15 EndY=3.091e-13 EndZ=0
    g1: ArcOfCircle CenterX=10 CenterY=23.1324 CenterZ=0 NormalX=0 NormalY=0 NormalZ=1 AngleXU=0 Radius=7 StartAngle=0.0322243 EndAngle=2.14272
    g2: ArcOfCircle CenterX=33.2738 CenterY=-13.0246 CenterZ=0 NormalX=0 NormalY=0 NormalZ=1 AngleXU=0 Radius=50 StartAngle=2.14272 EndAngle=2.87806
    g3: ArcOfCircle CenterX=-82.9517 CenterY=20.1361 CenterZ=0 NormalX=0 NormalY=0 NormalZ=1 AngleXU=0 Radius=100 StartAngle=6.08044 EndAngle=6.31541
  constraints (11):
    c: PointOnObject(g0,g-1)
    c: Symmetric(g0,g0,g-2)
    c: Coincident(g1,g-3)
    c: Coincident(g2,g0)
    c: Coincident(g3,g0)
    c: Tangent(g2,g1) = -1.5708
    c: Tangent(g3,g1) = -1.5708
    c: DistanceX(g0,g0) = 30
    c: Radius(g1) = 7
    c: Radius(g2) = 50
    c: Radius(g3) = 100
FEATURE [Sketcher::SketchObject] Sketch051
  AttachmentOffset = pos=(0,0,-7) rot=(0,0,1;0rad)
  ExternalGeometry = -> [Sketch050]
  FullyConstrained = true
  MapMode = 5
  Placement = pos=(0,0,-7) rot=(0,0,1;0rad)
  sketch-geometry (4):
    g0: ArcOfCircle CenterX=33.2738 CenterY=-13.0246 CenterZ=0 NormalX=0 NormalY=0 NormalZ=1 AngleXU=0 Radius=50 StartAngle=2.61743 EndAngle=2.87806
    g1: ArcOfCircle CenterX=-82.9517 CenterY=20.1361 CenterZ=0 NormalX=0 NormalY=0 NormalZ=1 AngleXU=0 Radius=100 StartAngle=6.08044 EndAngle=6.20173
    g2: LineSegment StartX=-10.0132 StartY=12 StartZ=0 EndX=16.7168 EndY=12 EndZ=0
    g3: LineSegment StartX=-15 StartY=-1.8e-15 StartZ=0 EndX=15 EndY=1.5419e-12 EndZ=0
  constraints (10):
    c: Coincident(g0,g-4)
    c: Coincident(g0,g-4)
    c: Coincident(g1,g-3)
    c: Coincident(g1,g-3)
    c: Coincident(g2,g0)
    c: Coincident(g2,g1)
    c: Horizontal(g2)
    c: DistanceY(g1) = 12
    c: Coincident(g3,g0)
    c: Coincident(g3,g1)
FEATURE [PartDesign::Pad] Pad013
  Direction = (0,0,1)
  Length = 6
  Length2 = 10
  Profile = -> Sketch050
  ReferenceAxis = -> Sketch050 [N_Axis]
  Suppressed = false
  Type = 0
  expr: Length = <<Sketch051>>.AttachmentOffset.Base.z - <<Sketch050>>.AttachmentOffset.Base.z
FEATURE [PartDesign::Pad] Pad014
  BaseFeature = -> Pad013
  Direction = (0,0,1)
  Length = 7
  Length2 = 10
  Profile = -> Sketch051
  ReferenceAxis = -> Sketch051 [N_Axis]
  Suppressed = false
  Type = 0
  expr: Length = -<<Sketch051>>.AttachmentOffset.Base.z
FEATURE [PartDesign::Plane] DatumPlane
  AttachmentOffset = pos=(0,0,7) rot=(0,0,1;0rad)
  Length = 60.4972
  MapMode = 5
  Placement = pos=(0,0,7) rot=(0,0,1;0rad)
  ResizeMode = 0
  Width = 65.5925
  expr: .AttachmentOffset.Base.z = <<Pad014>>.Length
FEATURE [PartDesign::Mirrored] Mirrored001
  BaseFeature = -> Pad014
  MirrorPlane = -> XY_Plane011
  Originals = -> [Pad014,Pad013]
  Suppressed = false
FEATURE [PartDesign::Pocket] Pocket005
  BaseFeature = -> Mirrored001
  Direction = (0,0,-1)
  Length = 5
  Length2 = 5
  Midplane = true
  Profile = -> Binder015
  Refine = true
  Suppressed = false
  Type = 1
FEATURE [PartDesign::CoordinateSystem] Local_CS021  label="door_rot_axis2"
  AttacherType = Attacher::AttachEngine3D
  MapMode = 45
  Placement = pos=(8e-15,4.74044,0) rot=(0,0,1.16318;0rad)
FEATURE [PartDesign::Body] Body010  label="door_fix2"
  Group = -> [Binder013,Pad012,Binder014,Pocket004,Local_CS021]
  Origin = -> Origin012
  Tip = -> Pocket004
FEATURE [PartDesign::CoordinateSystem] Local_CS022  label="door_rot_axis"
  AttacherType = Attacher::AttachEngine3D
  MapMode = 45
  Placement = pos=(10,23.1324,0) rot=(0,0,1;1.2e-05rad)
FEATURE [Part::FeaturePython] LinearArray007  # WARN: FeaturePython — macro-defined, semantics opaque (R4)
  Alignment = 0
  CellStart = A1
  Count = 2
  Dir = (1,0,0)
  DirIsDriven = true
  DistributionLaw = 0
  DrivenProperty = 1
  EndInclusive = true
  ExposePlacement = false
  GeneratorMode = 0
  MarkerShape = 1
  MarkerSize = 0
  NumElements = 2
  OrientMode = 1
  Placement = pos=(-7,12,0) rot=(1,0,0;1.5708rad)
  Point = (0,0,0)
  PointIsDriven = true
  Reverse = false
  SpanEnd = 14
  SpanStart = 0
  Step = 14
  Type = lattice2LinearArray.LinearArray
  VSGVersion = 1
  Values = 0.0 | 14.0
  ValuesSource = 2
  isLattice = 1
  expr: .Placement.Base.x = -SpanEnd / 2
FEATURE [Sketcher::SketchObject] Sketch052
  FullyConstrained = true
  MapMode = 5
  sketch-geometry (1):
    g0: Circle CenterX=0 CenterY=0 CenterZ=0 NormalX=0 NormalY=0 NormalZ=1 AngleXU=0 Radius=3.025
  constraints (2):
    c: Coincident(g0,g-1)
    c: Diameter(g0) = 6.05
FEATURE [Sketcher::SketchObject] Sketch053
  FullyConstrained = true
  MapMode = 5
  sketch-geometry (1):
    g0: Circle CenterX=0 CenterY=0 CenterZ=0 NormalX=0 NormalY=0 NormalZ=1 AngleXU=0 Radius=1.75
  constraints (2):
    c: Coincident(g0,g-1)
    c: Diameter(g0) = 3.5
FEATURE [PartDesign::Pad] Pad015
  Direction = (0,0,1)
  Length = 2.1
  Length2 = 10
  Profile = -> Sketch052
  ReferenceAxis = -> Sketch052 [N_Axis]
  Suppressed = false
  Type = 0
FEATURE [PartDesign::Pad] Pad016
  BaseFeature = -> Pad015
  Direction = (0,0,1)
  Length = 50
  Length2 = 10
  Profile = -> Sketch053
  ReferenceAxis = -> Sketch053 [N_Axis]
  Suppressed = false
  Type = 0
FEATURE [PartDesign::Body] Body011
  Group = -> [Sketch052,Sketch053,Pad015,Pad016]
  Origin = -> Origin013
  Tip = -> Pad016
FEATURE [Part::FeaturePython] Populate026  label="Populate LinearArray007 with Body011"  # WARN: FeaturePython — macro-defined, semantics opaque (R4)
  Copying = 0
  ExposePlacement = false
  MarkerShape = 1
  MarkerSize = 0
  NumElements = 0
  Object = -> Body011
  OutputCompounding = 1
  PlacementsTo = -> LinearArray007
  Referencing = 0
  Type = lattice2PopulateCopies.LatticePopulateCopies
  isLattice = 0
FEATURE [Part::Compound] Compound017
  Links = -> [Populate026]
FEATURE [PartDesign::Boolean] Boolean009
  BaseFeature = -> Pocket005
  Group = -> [Compound017]
  Suppressed = false
  Type = 1
  UsePlacement = true
FEATURE [PartDesign::CoordinateSystem] Local_CS023  label="door_fix"
  AttacherType = Attacher::AttachEngine3D
  AttachmentOffset = pos=(0,0,0) rot=(0,1,0;3.14159rad)
  MapMode = 5
  Placement = pos=(0,0,0) rot=(0,0.707107,0.707107;3.14159rad)
FEATURE [PartDesign::Body] Body009  label="door_fix1"
  Group = -> [Sketch050,Binder015,Sketch051,Pad013,Pad014,DatumPlane,Mirrored001,Pocket005,Local_CS022,Boolean009,Local_CS023]
  Origin = -> Origin011
  Tip = -> Boolean009
FEATURE [Part::FeaturePython] LinearArray008  # WARN: FeaturePython — macro-defined, semantics opaque (R4)
  Alignment = 0
  CellStart = A1
  Count = 2
  Dir = (0,1,0)
  DirIsDriven = true
  DistributionLaw = 0
  DrivenProperty = 1
  EndInclusive = true
  ExposePlacement = false
  GeneratorMode = 0
  MarkerShape = 1
  MarkerSize = 0
  NumElements = 2
  OrientMode = 0
  Placement = pos=(319.563,150,0) rot=(1,0,0;1.5708rad)
  Point = (0,0,0)
  PointIsDriven = true
  Reverse = false
  SpanEnd = 200
  SpanStart = 0
  Step = 200
  Type = lattice2LinearArray.LinearArray
  VSGVersion = 1
  Values = 0.0 | 200.0
  ValuesSource = 2
  isLattice = 1
  expr: .Placement.Base.x = <<side_Sketch>>.Constraints.distance - <<side_Sketch>>.Constraints.front / 2
  expr: .Placement.Base.y = <<side_Sketch>>.Constraints.side
FEATURE [PartDesign::CoordinateSystem] Local_CS024
  AttacherType = Attacher::AttachEngine3D
  AttachmentOffset = pos=(319.563,0,0) rot=(0,1,0;3.14159rad)
  AttachmentSupport = -> [XY_Plane]
  MapMode = 5
  Placement = pos=(319.563,0,0) rot=(0,1,0;3.14159rad)
  expr: .AttachmentOffset.Base.x = <<mid_Sketch>>.Constraints.middle
FEATURE [Sketcher::SketchObject] Sketch054
  ExternalGeometry = -> [Sketch008]
  FullyConstrained = true
  MapMode = 5
  Placement = pos=(0,0,0) rot=(0.57735,0.57735,0.57735;2.0944rad)
  sketch-geometry (7):
    g0: ArcOfCircle CenterX=132.281 CenterY=18.3274 CenterZ=0 NormalX=0 NormalY=0 NormalZ=1 AngleXU=0 Radius=2 StartAngle=0 EndAngle=1.72345
    g1: ArcOfCircle CenterX=132.281 CenterY=18.3274 CenterZ=0 NormalX=0 NormalY=0 NormalZ=1 AngleXU=0 Radius=2.5 StartAngle=1.4e-15 EndAngle=1.72345
    g2: LineSegment StartX=131.977 StartY=20.3041 StartZ=0 EndX=131.901 EndY=20.7983 EndZ=0
    g3: LineSegment StartX=134.281 StartY=18.3274 StartZ=0 EndX=134.281 EndY=10.8274 EndZ=0
    g4: LineSegment StartX=134.281 StartY=10.8274 StartZ=0 EndX=134.781 EndY=10.8274 EndZ=0
    g5: LineSegment StartX=134.781 StartY=10.8274 StartZ=0 EndX=134.781 EndY=18.3274 EndZ=0
    g6: LineSegment StartX=134.781 StartY=20.8274 StartZ=0 EndX=0 EndY=20.8274 EndZ=0
  constraints (19):
    c: Coincident(g1,g0)
    c: Coincident(g2,g1)
    c: Vertical(g3)
    c: Coincident(g4,g3)
    c: Horizontal(g4)
    c: Coincident(g5,g4)
    c: Vertical(g5)
    c: Tangent(g0,g-3) = 1.5708
    c: Perpendicular(g2,g-3)
    c: Distance(g2) = 0.5
    c: Coincident(g2,g0)
    c: Radius(g0) = 2
    c: Horizontal(g6)
    c: Tangent(g6,g1)
    c: PointOnObject(g6,g-2)
    c: PointOnObject(g6,g5)
    c: Tangent(g3,g0) = 1.5708
    c: DistanceY(g4,g6) = 10
    c: Tangent(g5,g1) = -1.5708
FEATURE [PartDesign::Pad] Pad017
  BaseFeature = -> Pocket002
  Direction = (1,0,0)
  Length = 635.153
  Length2 = 10
  Midplane = true
  Profile = -> Sketch054
  ReferenceAxis = -> Sketch054 [N_Axis]
  Suppressed = false
  Type = 0
  expr: Length = <<sink_plane_sketch>>.Constraints.end
FEATURE [Sketcher::SketchObject] Sketch055
  ExternalGeometry = -> [Sketch054]
  FullyConstrained = true
  MapMode = 5
  Placement = pos=(0,0,0) rot=(1,0,0;1.5708rad)
  expr: Constraints[5] = <<sink_plane_sketch>>.Constraints.end / 2
  sketch-geometry (3):
    g0: ArcOfCircle CenterX=315.576 CenterY=12.8274 CenterZ=0 NormalX=0 NormalY=0 NormalZ=1 AngleXU=0 Radius=2 StartAngle=4.71239 EndAngle=6.28319
    g1: LineSegment StartX=315.576 StartY=10.8274 StartZ=0 EndX=317.576 EndY=10.8274 EndZ=0
    g2: LineSegment StartX=317.576 StartY=10.8274 StartZ=0 EndX=317.576 EndY=12.8274 EndZ=0
  constraints (9):
    c: Coincident(g1,g2)
    c: Coincident(g2,g0)
    c: Tangent(g2,g0)
    c: Vertical(g2)
    c: Horizontal(g1)
    c: DistanceX(g1) = 317.576
    c: Radius(g0) = 2
    c: Tangent(g0,g1) = -1.5708
    c: Horizontal(g-3,g1)
FEATURE [PartDesign::Pocket] Pocket006
  BaseFeature = -> Pad017
  Direction = (0,1,-2e-16)
  Length = 5
  Length2 = 5
  Midplane = true
  Profile = -> Sketch055
  ReferenceAxis = -> Sketch055 [N_Axis]
  Suppressed = false
  Type = 1
FEATURE [PartDesign::Mirrored] Mirrored002
  BaseFeature = -> Pocket006
  MirrorPlane = -> Sketch055 [V_Axis]
  Originals = -> [Pocket006]
  Suppressed = false
FEATURE [Sketcher::SketchObject] Sketch056  label="Dimensions"
  ExternalGeometry = -> [Sketch,Sketch004]
  FullyConstrained = true
  expr: .Constraints.depth = <<side_Sketch>>.Constraints.side
  expr: .Constraints.modules_middle_distance = <<mid_Sketch>>.Constraints.middle
  expr: .Constraints.side_face = <<side_Sketch>>.Constraints.front
  expr: .Constraints.width = (<<mid_Sketch>>.Constraints.middle + <<side_Sketch>>.Constraints.distance) * 2
  expr: Constraints[8] = <<base_Sketch>>.Constraints.offset
  sketch-geometry (10):
    g0: LineSegment StartX=-639.126 StartY=6.21388e-09 StartZ=0 EndX=639.126 EndY=-6.21414e-09 EndZ=0
    g1: LineSegment StartX=639.126 StartY=-6.21414e-09 StartZ=0 EndX=639.126 EndY=150 EndZ=0
    g2: LineSegment StartX=319.563 StartY=-3.10539e-09 StartZ=0 EndX=319.563 EndY=20 EndZ=0
    g3: LineSegment StartX=319.563 StartY=20 StartZ=0 EndX=484.198 EndY=20 EndZ=0
    g4: LineSegment StartX=484.198 StartY=20 StartZ=0 EndX=639.126 EndY=150 EndZ=0
    g5: LineSegment StartX=639.126 StartY=150 StartZ=0 EndX=639.126 EndY=150 EndZ=0
    g6: LineSegment StartX=319.563 StartY=20 StartZ=0 EndX=154.928 EndY=20 EndZ=0
    g7: LineSegment StartX=154.928 StartY=20 StartZ=0 EndX=2.24247e-11 EndY=150 EndZ=0
    g8: LineSegment StartX=2.24247e-11 StartY=150 StartZ=0 EndX=-1.66443e-11 EndY=150 EndZ=0
    g9: LineSegment StartX=-1.66443e-11 StartY=150 StartZ=0 EndX=-2.33878e-11 EndY=150 EndZ=0
  constraints (32):
    c: Coincident(g1,g0)
    c: Vertical(g1)
    c: PointOnObject(g-1,g0)
    c: DistanceY(g1,g1) = 150  'depth'
    c: DistanceX(g0,g0) = 1278.25  'width'
    c: Symmetric(g0,g0,g-2)
    c: PointOnObject(g2,g0)
    c: Vertical(g2)
    c: DistanceY(g2,g2) = 20
    c: Coincident(g3,g2)
    c: Horizontal(g3)
    c: Coincident(g4,g3)
    c: Coincident(g5,g1)
    c: Horizontal(g5)
    c: Coincident(g2,g6)
    c: Coincident(g6,g7)
    c: Coincident(g7,g8)
    c: PointOnObject(g8,g-2)
    c: Horizontal(g8)
    c: Coincident(g8,g9)
    c: Symmetric(g9,g7,g8)
    c: Symmetric(g6,g3,g2)
    c: Symmetric(g4,g7,g2)
    c: Coincident(g5,g4)
    c: DistanceX(g5,g5) = 0  'side_face'
    c: DistanceX(g8,g2) = 319.563  'modules_middle_distance'
    c: DistanceX(g9,g7) = 4.00553e-11  'midle_face'
    c: Equal(g3,g-3)
    c: DistanceX(g6,g3) = 329.27  'modules_face'
    c: Distance(g4) = 202.244  'modules_side'
    c: DistanceX(g-4) = 76  'module_center_offset'
    c: DistanceX(g2,g0) = 319.563  'module_middle_side'
FEATURE [Sketcher::SketchObject] Sketch057
  FullyConstrained = true
  MapMode = 5
  Placement = pos=(0,0,0) rot=(1,0,0;1.5708rad)
  expr: Constraints[6] = <<bar_base_sketch>>.Constraints.total_width / 2
  sketch-geometry (3):
    g0: ArcOfCircle CenterX=25 CenterY=5 CenterZ=0 NormalX=0 NormalY=0 NormalZ=1 AngleXU=0 Radius=5 StartAngle=4.71239 EndAngle=6.28319
    g1: LineSegment StartX=25 StartY=3.304e-13 StartZ=0 EndX=30 EndY=0 EndZ=0
    g2: LineSegment StartX=30 StartY=0 StartZ=0 EndX=30 EndY=5 EndZ=0
  constraints (8):
    c: PointOnObject(g0,g-1)
    c: PointOnObject(g1,g-1)
    c: Coincident(g2,g1)
    c: Tangent(g2,g0) = -1.5708
    c: Vertical(g2)
    c: Tangent(g1,g0) = -1.5708
    c: DistanceX(g1) = 30
    c: Radius(g0) = 5
FEATURE [PartDesign::Plane] DatumPlane001
  AttachmentOffset = pos=(0,0,636.126) rot=(0,0,1;0rad)
  Length = 70.9545
  MapMode = 5
  Placement = pos=(0,0,636.126) rot=(0,0,1;0rad)
  ResizeMode = 0
  Width = 60.9545
  expr: .AttachmentOffset.Base.z = <<bar_pad>>.Length / 2
FEATURE [PartDesign::Mirrored] Mirrored003
  MirrorPlane = -> YZ_Plane006
  Suppressed = false
FEATURE [PartDesign::Mirrored] Mirrored004
  MirrorPlane = -> DatumPlane001
  Suppressed = false
FEATURE [Sketcher::SketchObject] Sketch058
  AttachmentOffset = pos=(0,240.563,0) rot=(0,0,1;0rad)
  FullyConstrained = true
  MapMode = 5
  Placement = pos=(0,5.3e-14,240.563) rot=(1,0,0;1.5708rad)
  expr: .AttachmentOffset.Base.y = <<Dimensions>>.Constraints.module_middle_side - 3 mm - <<Dimensions>>.Constraints.module_center_offset
  expr: Constraints[44] = -<<bar_base_sketch>>.Constraints.total_width / 2
  sketch-geometry (22):
    g0: LineSegment StartX=-21 StartY=61.5 StartZ=0 EndX=-21 EndY=70.5 EndZ=0
    g1: LineSegment StartX=-30 StartY=76.5 StartZ=0 EndX=-30 EndY=55.5 EndZ=0
    g2: LineSegment StartX=-21 StartY=-70.5 StartZ=0 EndX=-21 EndY=-61.5 EndZ=0
    g3: LineSegment StartX=-30 StartY=-55.5 StartZ=0 EndX=-30 EndY=-76.5 EndZ=0
    g4: LineSegment StartX=-24 StartY=-58.5 StartZ=0 EndX=-27 EndY=-58.5 EndZ=0
    g5: LineSegment StartX=-27 StartY=58.5 StartZ=0 EndX=-24 EndY=58.5 EndZ=0
    g6: LineSegment StartX=-24 StartY=73.5 StartZ=0 EndX=-27 EndY=73.5 EndZ=0
    g7: LineSegment StartX=-27 StartY=-73.5 StartZ=0 EndX=-24 EndY=-73.5 EndZ=0
    g8: ArcOfCircle CenterX=-27 CenterY=76.5 CenterZ=0 NormalX=0 NormalY=0 NormalZ=1 AngleXU=0 Radius=3 StartAngle=3.14159 EndAngle=4.71239
    g9: ArcOfCircle CenterX=-27 CenterY=55.5 CenterZ=0 NormalX=0 NormalY=0 NormalZ=1 AngleXU=0 Radius=3 StartAngle=1.5708 EndAngle=3.14159
    g10: ArcOfCircle CenterX=-27 CenterY=-55.5 CenterZ=0 NormalX=0 NormalY=0 NormalZ=1 AngleXU=0 Radius=3 StartAngle=3.14159 EndAngle=4.71239
    g11: ArcOfCircle CenterX=-27 CenterY=-76.5 CenterZ=0 NormalX=0 NormalY=0 NormalZ=1 AngleXU=0 Radius=3 StartAngle=1.5708 EndAngle=3.14159
    g12: ArcOfCircle CenterX=-24 CenterY=61.5 CenterZ=0 NormalX=0 NormalY=0 NormalZ=1 AngleXU=0 Radius=3 StartAngle=4.71239 EndAngle=6.28319
    g13: GeomPoint X=-21 Y=58.5 Z=0
    g14: ArcOfCircle CenterX=-24 CenterY=70.5 CenterZ=0 NormalX=0 NormalY=0 NormalZ=1 AngleXU=0 Radius=3 StartAngle=1.6e-15 EndAngle=1.5708
    g15: GeomPoint X=-21 Y=73.5 Z=0
    g16: ArcOfCircle CenterX=-24 CenterY=-61.5 CenterZ=0 NormalX=0 NormalY=0 NormalZ=1 AngleXU=0 Radius=3 StartAngle=9e-16 EndAngle=1.5708
    g17: GeomPoint X=-21 Y=-58.5 Z=0
    g18: ArcOfCircle CenterX=-24 CenterY=-70.5 CenterZ=0 NormalX=0 NormalY=0 NormalZ=1 AngleXU=0 Radius=3 StartAngle=4.71239 EndAngle=6.28319
    g19: GeomPoint X=-21 Y=-73.5 Z=0
    g20: GeomPoint X=-30 Y=66 Z=0
    g21: GeomPoint X=-30 Y=-66 Z=0
  constraints (49):
    c: Vertical(g0)
    c: Vertical(g1)
    c: Vertical(g2)
    c: Vertical(g3)
    c: Equal(g3,g1)
    c: Symmetric(g3,g1,g-1)
    c: Horizontal(g4)
    c: Horizontal(g5)
    c: Horizontal(g6)
    c: Horizontal(g7)
    c: Tangent(g11,g7) = 1.5708
    c: Tangent(g11,g3) = -1.5708
    c: Tangent(g10,g4) = 1.5708
    c: Tangent(g10,g3) = -1.5708
    c: Tangent(g9,g5) = 1.5708
    c: Tangent(g9,g1) = -1.5708
    c: Tangent(g8,g6) = 1.5708
    c: Tangent(g8,g1) = -1.5708
    c: PointOnObject(g13,g0)
    c: PointOnObject(g13,g5)
    c: Tangent(g0,g12) = -1.5708
    c: Tangent(g5,g12) = -1.5708
    c: PointOnObject(g15,g0)
    c: PointOnObject(g15,g6)
    c: Tangent(g0,g14) = -1.5708
    c: Tangent(g6,g14) = -1.5708
    c: PointOnObject(g17,g2)
    c: PointOnObject(g17,g4)
    c: Tangent(g2,g16) = -1.5708
    c: Tangent(g4,g16) = -1.5708
    c: PointOnObject(g19,g2)
    c: PointOnObject(g19,g7)
    c: Tangent(g2,g18) = -1.5708
    c: Tangent(g7,g18) = -1.5708
    c: Equal(g18,g11)
    c: Equal(g11,g16)
    c: Equal(g16,g10)
    c: Equal(g10,g9)
    c: Equal(g9,g12)
    c: Equal(g12,g14)
    c: Equal(g14,g8)
    c: Radius(g14) = 3
    c: Symmetric(g3,g3,g21)
    c: Symmetric(g1,g1,g20)
    c: DistanceX(g20) = -30
    c: Vertical(g17,g13)
    c: DistanceY(g19,g17) = 15
    c: DistanceY(g21,g20) = 132
    c: Distance(g15,g1) = 9
FEATURE [Sketcher::SketchObject] Sketch059
  AttachmentOffset = pos=(13,40,0) rot=(0,0,1;0rad)
  FullyConstrained = true
  MapMode = 5
  Placement = pos=(13,8.9e-15,40) rot=(1,0,0;1.5708rad)
  expr: .AttachmentOffset.Base.x = <<bar_fix_BaseBend>>.length / 2
  expr: .AttachmentOffset.Base.y = <<bar_fix_base_sketch>>.Constraints.bar_side
  sketch-geometry (3):
    g0: ArcOfCircle CenterX=-5 CenterY=-5 CenterZ=0 NormalX=0 NormalY=0 NormalZ=1 AngleXU=0 Radius=5 StartAngle=-2.7e-15 EndAngle=1.5708
    g1: LineSegment StartX=-5 StartY=0 StartZ=0 EndX=0 EndY=0 EndZ=0
    g2: LineSegment StartX=0 StartY=0 StartZ=0 EndX=0 EndY=-5 EndZ=0
  constraints (7):
    c: PointOnObject(g0,g-1)
    c: PointOnObject(g0,g-2)
    c: Coincident(g1,g-1)
    c: Coincident(g2,g1)
    c: Tangent(g2,g0) = 1.5708
    c: Tangent(g1,g0) = 1.5708
    c: Radius(g0) = 5
FEATURE [PartDesign::Pocket] Pocket009
  BaseFeature = -> BaseBend002
  Direction = (0,1,-2e-16)
  Length = 5
  Length2 = 5
  Midplane = true
  Profile = -> Sketch059
  ReferenceAxis = -> Sketch059 [N_Axis]
  Suppressed = false
  Type = 1
FEATURE [Sketcher::SketchObject] Sketch060
  AttachmentOffset = pos=(13,50,0) rot=(0,0,1;0rad)
  FullyConstrained = true
  MapMode = 5
  Placement = pos=(13,50,0) rot=(0,0,1;0rad)
  expr: .AttachmentOffset.Base.x = <<bar_fix_BaseBend>>.length / 2
  expr: .AttachmentOffset.Base.y = <<bar_fix_base_sketch>>.Constraints.comp_side
  sketch-geometry (3):
    g0: LineSegment StartX=-5 StartY=0 StartZ=0 EndX=0 EndY=0 EndZ=0
    g1: LineSegment StartX=0 StartY=0 StartZ=0 EndX=0 EndY=-5 EndZ=0
    g2: ArcOfCircle CenterX=-5 CenterY=-5 CenterZ=0 NormalX=0 NormalY=0 NormalZ=1 AngleXU=0 Radius=5 StartAngle=0 EndAngle=1.5708
  constraints (7):
    c: PointOnObject(g0,g-1)
    c: Coincident(g0,g-1)
    c: Coincident(g0,g1)
    c: PointOnObject(g1,g-2)
    c: Tangent(g2,g0) = 1.5708
    c: Tangent(g2,g1) = 1.5708
    c: Radius(g2) = 5
FEATURE [PartDesign::Pocket] Pocket010
  BaseFeature = -> Pocket009
  Direction = (0,0,-1)
  Length = 5
  Length2 = 5
  Midplane = true
  Profile = -> Sketch060
  ReferenceAxis = -> Sketch060 [N_Axis]
  Suppressed = false
  Type = 1
FEATURE [PartDesign::Mirrored] Mirrored005
  BaseFeature = -> Pocket010
  MirrorPlane = -> YZ_Plane007
  Originals = -> [Pocket009,Pocket010]
  Suppressed = false
FEATURE [PartDesign::Boolean] Boolean005
  BaseFeature = -> Mirrored005
  Group = -> [Compound013]
  Suppressed = false
  Type = 1
  UsePlacement = true
FEATURE [PartDesign::Body] Body006  label="bar_fix"
  Group = -> [Binder009,BaseBend002,Sketch059,Pocket009,Sketch060,Pocket010,Mirrored005,Boolean005,Local_CS017]
  Origin = -> Origin007
  Tip = -> Boolean005
FEATURE [Sketcher::SketchObject] Sketch061
  AttachmentSupport = -> [XZ_Plane008]
  ExternalGeometry = -> [Sketch042]
  FullyConstrained = true
  MapMode = 5
  Placement = pos=(0,0,0) rot=(1,0,0;1.5708rad)
  expr: Constraints[14] = <<sink_back_base_Pad009>>.Length
  expr: Constraints[15] = -<<sink_back_base_Pad009>>.Length2
  sketch-geometry (6):
    g0: LineSegment StartX=204.635 StartY=30 StartZ=0 EndX=204.635 EndY=35 EndZ=0
    g1: LineSegment StartX=204.635 StartY=35 StartZ=0 EndX=199.635 EndY=35 EndZ=0
    g2: LineSegment StartX=-304.563 StartY=35 StartZ=0 EndX=-309.563 EndY=35 EndZ=0
    g3: LineSegment StartX=-309.563 StartY=35 StartZ=0 EndX=-309.563 EndY=30 EndZ=0
    g4: ArcOfCircle CenterX=199.635 CenterY=30 CenterZ=0 NormalX=0 NormalY=0 NormalZ=1 AngleXU=0 Radius=5 StartAngle=-1.35e-13 EndAngle=1.5708
    g5: ArcOfCircle CenterX=-304.563 CenterY=30 CenterZ=0 NormalX=0 NormalY=0 NormalZ=1 AngleXU=0 Radius=5 StartAngle=1.5708 EndAngle=3.14159
  constraints (16):
    c: Vertical(g0)
    c: Coincident(g0,g1)
    c: Horizontal(g1)
    c: Coincident(g2,g3)
    c: Vertical(g3)
    c: Horizontal(g2)
    c: Horizontal(g2,g0)
    c: Tangent(g5,g2) = -1.5708
    c: Tangent(g5,g3) = -1.5708
    c: Radius(g5) = 5
    c: Tangent(g4,g0) = -1.5708
    c: Tangent(g4,g1) = -1.5708
    c: Equal(g4,g5)
    c: Horizontal(g-3,g0)
    c: DistanceX(g0) = 204.635
    c: DistanceX(g2) = -309.563
FEATURE [TechDraw::DrawSVGTemplate] Template
  Height = 210
  Orientation = 1
  Template = <path>
  Width = 297
FEATURE [TechDraw::DrawViewPart] View003
  CoarseView = false
  Direction = (0.57735,0.57735,0.57735)
  Focus = 100
  HardHidden = false
  IsoCount = 0
  IsoHidden = false
  IsoVisible = false
  LockPosition = false
  Perspective = false
  Rotation = 0
  ScaleType = 0
  ScrubCount = 0
  SeamHidden = false
  SeamVisible = true
  SmoothHidden = false
  SmoothVisible = true
  Source = -> [Body006]
  X = 88.5
  XDirection = (-0.707107,0.707107,0)
  Y = 105
FEATURE [TechDraw::DrawViewPart] View004
  CoarseView = false
  Direction = (1,0,0)
  Focus = 100
  HardHidden = false
  IsoCount = 0
  IsoHidden = false
  IsoVisible = false
  LockPosition = false
  Perspective = false
  Rotation = 0
  ScaleType = 0
  ScrubCount = 0
  SeamHidden = false
  SeamVisible = true
  SmoothHidden = false
  SmoothVisible = true
  Source = -> [Body006]
  X = 199.423
  XDirection = (0,1,0)
  Y = 112.227
FEATURE [Part::FeaturePython] Placment009  # WARN: FeaturePython — macro-defined, semantics opaque (R4)
  AttacherType = Attacher::AttachEngine3D
  ExposePlacement = true
  MarkerShape = 1
  MarkerSize = 20
  NumElements = 1
  Placement = pos=(0,0.5,73) rot=(1,0,0;1.5708rad)
  Type = lattice2AttachablePlacement.AttachablePlacement
  isLattice = 1
FEATURE [Sketcher::SketchObject] Sketch062
  AttachmentSupport = -> [Sketch043]
  FullyConstrained = true
  MapMode = 51
  Placement = pos=(204.79,37.7561,-29.9564) rot=(0.999043,-0.020198,0.0388;4.10074rad)
  expr: Constraints[8] = -<<Pad011>>.Length
  sketch-geometry (6):
    g0: LineSegment StartX=0 StartY=5 StartZ=0 EndX=0 EndY=0 EndZ=0
    g1: LineSegment StartX=0 StartY=0 StartZ=0 EndX=-5 EndY=0 EndZ=0
    g2: LineSegment StartX=-515.751 StartY=5 StartZ=0 EndX=-515.751 EndY=0 EndZ=0
    g3: LineSegment StartX=-515.751 StartY=0 StartZ=0 EndX=-510.751 EndY=0 EndZ=0
    g4: ArcOfCircle CenterX=-5 CenterY=5 CenterZ=0 NormalX=0 NormalY=0 NormalZ=1 AngleXU=0 Radius=5 StartAngle=4.71239 EndAngle=6.28319
    g5: ArcOfCircle CenterX=-510.751 CenterY=5 CenterZ=0 NormalX=0 NormalY=0 NormalZ=1 AngleXU=0 Radius=5 StartAngle=3.14159 EndAngle=4.71239
  constraints (15):
    c: PointOnObject(g0,g-2)
    c: Coincident(g0,g-1)
    c: Coincident(g0,g1)
    c: PointOnObject(g1,g-1)
    c: Vertical(g2)
    c: Coincident(g2,g3)
    c: PointOnObject(g3,g-1)
    c: Horizontal(g3)
    c: DistanceX(g2) = -515.751
    c: Tangent(g4,g0) = 1.5708
    c: Tangent(g4,g1) = 1.5708
    c: Tangent(g5,g3) = -1.5708
    c: Tangent(g5,g2) = -1.5708
    c: Equal(g4,g5)
    c: Radius(g4) = 5
FEATURE [Sketcher::SketchObject] Sketch063
  AttachmentSupport = -> [XZ_Plane008]
  ExternalGeometry = -> [Binder010]
  FullyConstrained = true
  MapMode = 5
  Placement = pos=(0,0,0) rot=(1,0,0;1.5708rad)
  expr: Constraints[1] = -<<Dimensions>>.Constraints.modules_face / 2
  sketch-geometry (10):
    g0: GeomPoint X=-164.635 Y=0 Z=0
    g1: LineSegment StartX=-309.563 StartY=35 StartZ=0 EndX=-309.563 EndY=4.5 EndZ=0
    g2: LineSegment StartX=-307.063 StartY=7 StartZ=0 EndX=-167.135 EndY=7 EndZ=0
    g3: LineSegment StartX=-164.635 StartY=9.5 StartZ=0 EndX=-164.635 EndY=32.5 EndZ=0
    g4: LineSegment StartX=-162.135 StartY=35 StartZ=0 EndX=-309.563 EndY=35 EndZ=0
    g5: ArcOfCircle CenterX=-307.063 CenterY=4.5 CenterZ=0 NormalX=0 NormalY=0 NormalZ=1 AngleXU=0 Radius=2.5 StartAngle=1.5708 EndAngle=3.14159
    g6: ArcOfCircle CenterX=-167.135 CenterY=9.5 CenterZ=0 NormalX=0 NormalY=0 NormalZ=1 AngleXU=0 Radius=2.5 StartAngle=4.71239 EndAngle=6.28319
    g7: ArcOfCircle CenterX=-162.135 CenterY=32.5 CenterZ=0 NormalX=0 NormalY=0 NormalZ=1 AngleXU=0 Radius=2.5 StartAngle=1.5708 EndAngle=3.14159
    g8: GeomPoint X=-309.563 Y=35 Z=0
    g9: GeomPoint X=-164.635 Y=7 Z=0
  constraints (22):
    c: PointOnObject(g0,g-1)
    c: DistanceX(g0) = -164.635
    c: Tangent(g2,g6) = -1.5708
    c: Tangent(g3,g6) = -1.5708
    c: Vertical(g1)
    c: Vertical(g3)
    c: Horizontal(g2)
    c: Horizontal(g4)
    c: Equal(g5,g6)
    c: Equal(g6,g7)
    c: PointOnObject(g9,g2)
    c: PointOnObject(g9,g3)
    c: Diameter(g6) = 5
    c: Vertical(g9,g0)
    c: DistanceY(g0,g9) = 7
    c: Tangent(g7,g3) = 1.5708
    c: Tangent(g4,g7) = -1.5708
    c: Tangent(g5,g2) = 1.5708
    c: Tangent(g5,g1) = -1.5708
    c: Coincident(g8,g-3)
    c: Coincident(g1,g8)
    c: Coincident(g1,g4)
FEATURE [Sketcher::SketchObject] Sketch064  label="lamp_fix_base_Sketch"
  ExternalGeometry = -> [Sketch]
  FullyConstrained = true
  sketch-geometry (4):
    g0: LineSegment StartX=299.412 StartY=134.005 StartZ=0 EndX=318.563 EndY=150.075 EndZ=0
    g1: LineSegment StartX=318.563 StartY=150.075 StartZ=0 EndX=273.568 EndY=203.698 EndZ=0
    g2: LineSegment StartX=273.568 StartY=203.698 StartZ=0 EndX=263.568 EndY=197.924 EndZ=0
    g3: LineSegment StartX=319.563 StartY=150 StartZ=0 EndX=319.113 EndY=150.536 EndZ=0
  constraints (13):
    c: Coincident(g1,g0)
    c: Coincident(g2,g1)
    c: Distance(g0) = 25
    c: Coincident(g3,g-3)
    c: PointOnObject(g3,g0)
    c: Perpendicular(g0,g3)
    c: Perpendicular(g-3,g3)
    c: Angle(g1) = 2.26893
    c: Distance(g1) = 70
    c: DistanceX(g2,g2) = 10
    c: Angle(g2,g1) = 1.74533
    c: Distance(g3) = 0.7
    c: DistanceX(g0,g3) = 1
FEATURE [PartDesign::SubShapeBinder] Binder016
  BindCopyOnChange = 0
  BindMode = 0
  ClaimChildren = true
  Context = -> Body012 [Binder016.]
  Fuse = false
  MakeFace = true
  OffsetFill = false
  OffsetIntersection = false
  OffsetJoinType = 0
  OffsetOpenResult = false
  PartialLoad = false
  Relative = false
  Support = -> [Sketch064]
  _Version = 2
FEATURE [PartDesign::FeaturePython] BaseBend004  label="lamp_fix_BaseBend"  # WARN: FeaturePython — macro-defined, semantics opaque (R4)
  BendSide = 0
  BendSketch = -> Binder016
  MidPlane = false
  Reverse = false
  Suppressed = false
  length = 900
  radius = 2
  thickness = 0.7
FEATURE [Sketcher::SketchObject] Sketch065  label="lamp_fix_cut_sketch"
  AttachmentOffset = pos=(0,166.7,0) rot=(0,1,0;1.5708rad)
  FullyConstrained = true
  MapMode = 7
  Placement = pos=(318.563,150.075,166.7) rot=(0.313146,0.671543,0.671543;2.53465rad)
  expr: .AttachmentOffset.Base.y = 60 mm + .Constraints.length / 2
  sketch-geometry (8):
    g0: LineSegment StartX=-0.5 StartY=-106.7 StartZ=0 EndX=2.2 EndY=-106.7 EndZ=0
    g1: LineSegment StartX=4.2 StartY=-104.7 StartZ=0 EndX=4.2 EndY=104.7 EndZ=0
    g2: LineSegment StartX=2.2 StartY=106.7 StartZ=0 EndX=-0.5 EndY=106.7 EndZ=0
    g3: LineSegment StartX=-0.5 StartY=106.7 StartZ=0 EndX=-0.5 EndY=-106.7 EndZ=0
    g4: ArcOfCircle CenterX=2.2 CenterY=104.7 CenterZ=0 NormalX=0 NormalY=0 NormalZ=1 AngleXU=0 Radius=2 StartAngle=-2.7e-15 EndAngle=1.5708
    g5: GeomPoint X=4.2 Y=106.7 Z=0
    g6: ArcOfCircle CenterX=2.2 CenterY=-104.7 CenterZ=0 NormalX=0 NormalY=0 NormalZ=1 AngleXU=0 Radius=2 StartAngle=4.71239 EndAngle=6.28319
    g7: GeomPoint X=4.2 Y=-106.7 Z=0
  constraints (19):
    c: Coincident(g2,g3)
    c: Horizontal(g0)
    c: Horizontal(g2)
    c: Vertical(g1)
    c: PointOnObject(g5,g1)
    c: PointOnObject(g5,g2)
    c: Tangent(g1,g4) = -1.5708
    c: Tangent(g2,g4) = -1.5708
    c: Tangent(g0,g6) = -1.5708
    c: Tangent(g1,g6) = -1.5708
    c: Equal(g6,g4)
    c: Radius(g6) = 2  'r'
    c: Coincident(g0,g3)
    c: DistanceX(g0) = -0.5
    c: PointOnObject(g7,g1)
    c: PointOnObject(g7,g0)
    c: Symmetric(g0,g2,g-1)
    c: DistanceY(g3,g3) = 213.4  'length'
    c: DistanceX(g0,g0) = 2.7
FEATURE [Sketcher::SketchObject] Sketch066  label="lamp_fix_cut_sketch2"
  AttachmentOffset = pos=(0,166.7,0) rot=(0,1,0;1.5708rad)
  FullyConstrained = true
  MapMode = 7
  Placement = pos=(299.412,134.005,166.7) rot=(0.889126,0.323616,0.323616;1.68804rad)
  expr: .AttachmentOffset.Base.y = <<lamp_fix_cut_sketch>>.AttachmentOffset.Base.y
  expr: Constraints[6] = <<lamp_fix_cut_sketch>>.Constraints.length
  expr: Constraints[7] = <<lamp_fix_cut_sketch>>.Constraints.r
  sketch-geometry (4):
    g0: ArcOfCircle CenterX=2 CenterY=108.7 CenterZ=0 NormalX=0 NormalY=0 NormalZ=1 AngleXU=0 Radius=2 StartAngle=3.14159 EndAngle=4.71239
    g1: ArcOfCircle CenterX=2 CenterY=-108.7 CenterZ=0 NormalX=0 NormalY=0 NormalZ=1 AngleXU=0 Radius=2 StartAngle=1.5708 EndAngle=3.14159
    g2: LineSegment StartX=0 StartY=-108.7 StartZ=0 EndX=0 EndY=108.7 EndZ=0
    g3: LineSegment StartX=2 StartY=106.7 StartZ=0 EndX=2 EndY=-106.7 EndZ=0
  constraints (10):
    c: Coincident(g0,g3)
    c: Perpendicular(g3,g1) = 4.71239
    c: Perpendicular(g0,g3)
    c: Tangent(g1,g2) = 1.5708
    c: Vertical(g2)
    c: Symmetric(g1,g0,g-1)
    c: DistanceY(g3,g3) = 213.4
    c: Radius(g1) = 2
    c: PointOnObject(g-1,g2)
    c: Tangent(g0,g2) = 1.5708
FEATURE [Part::Mirroring] Part__Mirroring014  label="Sketch064 (Mirror #15)"
  Base = (0,0,0)
  Normal = (1,0,0)
  Source = -> Sketch064
FEATURE [PartDesign::SubShapeBinder] Binder017
  BindCopyOnChange = 0
  BindMode = 0
  ClaimChildren = true
  Context = -> Body013 [Binder017.]
  Fuse = false
  MakeFace = true
  OffsetFill = false
  OffsetIntersection = false
  OffsetJoinType = 0
  OffsetOpenResult = false
  PartialLoad = false
  Relative = true
  Support = -> [Part__Mirroring014]
  _Version = 2
FEATURE [PartDesign::FeaturePython] BaseBend005  # WARN: FeaturePython — macro-defined, semantics opaque (R4)
  BendSide = 1
  BendSketch = -> Binder017
  MidPlane = false
  Reverse = false
  Suppressed = false
  length = 900
  radius = 2
  thickness = 0.7
  expr: length = <<lamp_fix_BaseBend>>.length
  expr: radius = <<lamp_fix_BaseBend>>.radius
  expr: thickness = <<lamp_fix_BaseBend>>.thickness
FEATURE [PartDesign::SubShapeBinder] Binder020
  BindCopyOnChange = 0
  BindMode = 0
  ClaimChildren = true
  Fuse = false
  MakeFace = true
  OffsetFill = false
  OffsetIntersection = false
  OffsetJoinType = 0
  OffsetOpenResult = false
  PartialLoad = false
  Relative = true
  Support = -> [<external ../ULZ-P02-14W.FCStd>#Sketch]
  _Version = 2
  expr: Support = <<ULZ-P02-14W>>#<<holes>>._self
FEATURE [Part::FeaturePython] Placment010  # WARN: FeaturePython — macro-defined, semantics opaque (R4)
  AttacherType = Attacher::AttachEngine3D
  AttachmentOffset = pos=(0,450,11) rot=(0,-1,0;1.5708rad)
  ExposePlacement = true
  MapMode = 7
  MarkerShape = 1
  MarkerSize = 20
  NumElements = 1
  Placement = pos=(280.639,195.271,450) rot=(0.834817,-0.389282,-0.389282;1.75037rad)
  Type = lattice2AttachablePlacement.AttachablePlacement
  isLattice = 1
FEATURE [Part::FeaturePython] PlacementSubsequence002  # WARN: FeaturePython — macro-defined, semantics opaque (R4)
  Base = -> Placment006
  CycleMode = 0
  ExposePlacement = false
  MarkerShape = 1
  MarkerSize = 0
  NumElements = 2
  Type = lattice2AttachablePlacement.AttachedPlacementSubsequence
  isLattice = 1
FEATURE [Part::FeaturePython] Mirror001  label="Mirror001 of PlacementSubsequence002"  # WARN: FeaturePython — macro-defined, semantics opaque (R4)
  ExposePlacement = false
  FlipX = true
  FlipY = false
  FlipZ = false
  MarkerShape = 1
  MarkerSize = 20
  NumElements = 2
  Object = -> PlacementSubsequence002
  ObjectTraversal = 0
  Type = lattice2Mirror.LatticeMirror
  isLattice = 1
FEATURE [Part::FeaturePython] Join006  label="sink_front_fix"  # WARN: FeaturePython — macro-defined, semantics opaque (R4)
  ExposePlacement = false
  Interleave = false
  Links = -> [Placment009,Mirror001,PlacementSubsequence002]
  MarkerShape = 1
  MarkerSize = 0
  NumElements = 5
  Type = lattice2JoinArrays.JoinArrays
  isLattice = 1
FEATURE [Part::FeaturePython] Join003  # WARN: FeaturePython — macro-defined, semantics opaque (R4)
  ExposePlacement = false
  Interleave = false
  Links = -> [Mirror,Join006,PlacementSubsequence001]
  MarkerShape = 1
  MarkerSize = 0
  NumElements = 9
  Type = lattice2JoinArrays.JoinArrays
  isLattice = 1
FEATURE [Part::FeaturePython] Populate018  label="Populate Join003 with hole_3.4mm"  # WARN: FeaturePython — macro-defined, semantics opaque (R4)
  Copying = 0
  ExposePlacement = false
  MarkerShape = 1
  MarkerSize = 0
  NumElements = 0
  Object = -> Cylinder
  OutputCompounding = 1
  PlacementsTo = -> Join003
  Referencing = 0
  Type = lattice2PopulateCopies.LatticePopulateCopies
  isLattice = 0
FEATURE [Part::FeaturePython] Populate019  label="Populate LinearArray001 with Join003"  # WARN: FeaturePython — macro-defined, semantics opaque (R4)
  Copying = 0
  ExposePlacement = false
  MarkerShape = 1
  MarkerSize = 0
  NumElements = 18
  Object = -> Join003
  OutputCompounding = 0
  PlacementsTo = -> LinearArray001
  Referencing = 0
  Type = lattice2PopulateCopies.LatticePopulateCopies
  isLattice = 1
FEATURE [Part::FeaturePython] Populate020  label="Populate Custom004 with Populate LinearArray001 with Join003"  # WARN: FeaturePython — macro-defined, semantics opaque (R4)
  Copying = 0
  ExposePlacement = false
  MarkerShape = 1
  MarkerSize = 0
  NumElements = 18
  Object = -> Populate019
  OutputCompounding = 0
  PlacementsTo = -> Placment007
  Referencing = 0
  Type = lattice2PopulateCopies.LatticePopulateCopies
  isLattice = 1
FEATURE [Part::FeaturePython] Populate021  label="face_sink_fix"  # WARN: FeaturePython — macro-defined, semantics opaque (R4)
  Copying = 0
  ExposePlacement = false
  MarkerShape = 1
  MarkerSize = 0
  NumElements = 0
  Object = -> Cylinder
  OutputCompounding = 1
  PlacementsTo = -> Populate020
  Referencing = 0
  Type = lattice2PopulateCopies.LatticePopulateCopies
  isLattice = 0
FEATURE [Part::Compound] Compound014
  Links = -> [Populate018]
FEATURE [PartDesign::Boolean] Boolean006
  BaseFeature = -> Mirrored002
  Group = -> [Compound014]
  Suppressed = false
  Type = 1
  UsePlacement = true
FEATURE [PartDesign::Body] Body003  label="sink"
  Group = -> [Binder001,Local_CS,Sketch005,Sketch006,Sketch007,Local_CS001,Sketch008,Sketch009,Sketch010,Sketch011,Pad,Pad001,Pad002,Pad003,Sketch012,Sketch013,Pad004,Pad005,Sketch014,Local_CS003,Sketch015,Pad006,Sketch016,SketchOnSheet,CornerRelief,CornerRelief001,Sketch017,Sketch018,Sketch019,Pocket,Pocket001,Pocket002,Local_CS004,Sketch054,Pad017,Sketch055,Pocket006,Mirrored002,Boolean006]
  Origin = -> Origin004
  Tip = -> Mirrored002
FEATURE [Part::FeaturePython] Populate023  label="Populate Join004 with hole_3.4mm"  # WARN: FeaturePython — macro-defined, semantics opaque (R4)
  Copying = 0
  ExposePlacement = false
  MarkerShape = 1
  MarkerSize = 0
  NumElements = 0
  Object = -> Cylinder
  OutputCompounding = 1
  PlacementsTo = -> Join006
  Referencing = 0
  Type = lattice2PopulateCopies.LatticePopulateCopies
  isLattice = 0
FEATURE [Part::Compound] Compound015
  Links = -> [Populate023]
FEATURE [TechDraw::DrawViewPart] View005
  CoarseView = false
  Direction = (0.762326,0.639667,0.0984104)
  Focus = 100
  HardHidden = false
  IsoCount = 0
  IsoHidden = false
  IsoVisible = false
  LockPosition = false
  Perspective = false
  Rotation = 0
  Scale = 0.5
  ScaleType = 1
  ScrubCount = 0
  SeamHidden = false
  SeamVisible = true
  SmoothHidden = false
  SmoothVisible = true
  Source = -> [Boolean006]
  X = 108.5
  XDirection = (-0.642787,0.766045,-1.20347e-07)
  Y = 165
FEATURE [TechDraw::DrawViewPart] View011
  CoarseView = false
  Direction = (1,0,0)
  Focus = 100
  HardHidden = false
  IsoCount = 0
  IsoHidden = false
  IsoVisible = false
  LockPosition = false
  Perspective = false
  Rotation = 0
  ScaleType = 0
  ScrubCount = 0
  SeamHidden = false
  SeamVisible = true
  SmoothHidden = false
  SmoothVisible = true
  Source = -> [Body003]
  X = 198.5
  XDirection = (0,1,0)
  Y = 85
FEATURE [TechDraw::DrawViewPart] View012
  CoarseView = false
  Direction = (0,1,0)
  Focus = 100
  HardHidden = false
  IsoCount = 0
  IsoHidden = false
  IsoVisible = false
  LockPosition = false
  Perspective = false
  Rotation = 0
  Scale = 0.375
  ScaleType = 1
  ScrubCount = 0
  SeamHidden = false
  SeamVisible = true
  SmoothHidden = false
  SmoothVisible = true
  Source = -> [Body003]
  X = 148.889
  XDirection = (-1,0,0)
  Y = 20.3888
FEATURE [Sketcher::SketchObject] Sketch067
  AttachmentOffset = pos=(0,0,0) rot=(0,1,0;1.5708rad)
  FullyConstrained = true
  MapMode = 7
  Placement = pos=(299.412,134.005,0) rot=(0.889126,0.323616,0.323616;1.68804rad)
  sketch-geometry (3):
    g0: ArcOfCircle CenterX=3 CenterY=3 CenterZ=0 NormalX=0 NormalY=0 NormalZ=1 AngleXU=0 Radius=3 StartAngle=3.14159 EndAngle=4.71239
    g1: LineSegment StartX=0 StartY=3 StartZ=0 EndX=0 EndY=0 EndZ=0
    g2: LineSegment StartX=0 StartY=0 StartZ=0 EndX=3 EndY=0 EndZ=0
  constraints (7):
    c: Coincident(g1,g2)
    c: Tangent(g0,g1) = -1.5708
    c: Tangent(g2,g0) = -1.5708
    c: Coincident(g1,g-1)
    c: Vertical(g1)
    c: Horizontal(g2)
    c: Radius(g0) = 3
FEATURE [Sketcher::SketchObject] Sketch068
  AttachmentOffset = pos=(0,0,0) rot=(0,1,0;1.5708rad)
  FullyConstrained = true
  MapMode = 7
  Placement = pos=(263.568,197.924,0) rot=(-0.186157,0.694747,0.694747;3.50969rad)
  sketch-geometry (3):
    g0: LineSegment StartX=0 StartY=3 StartZ=0 EndX=0 EndY=0 EndZ=0
    g1: LineSegment StartX=0 StartY=0 StartZ=0 EndX=-3 EndY=0 EndZ=0
    g2: ArcOfCircle CenterX=-3 CenterY=3 CenterZ=0 NormalX=0 NormalY=0 NormalZ=1 AngleXU=0 Radius=3 StartAngle=4.71239 EndAngle=6.28319
  constraints (7):
    c: PointOnObject(g0,g-2)
    c: Coincident(g0,g-1)
    c: Coincident(g0,g1)
    c: Horizontal(g1)
    c: Tangent(g2,g0) = 1.5708
    c: Tangent(g2,g1) = 1.5708
    c: Radius(g2) = 3
FEATURE [PartDesign::Plane] DatumPlane002
  AttachmentOffset = pos=(0,0,450) rot=(0,0,1;0rad)
  Length = 399.987
  MapMode = 5
  Placement = pos=(0,0,450) rot=(0,0,1;0rad)
  ResizeMode = 0
  Width = 284.925
  expr: .AttachmentOffset.Base.z = <<lamp_fix_BaseBend>>.length / 2
FEATURE [PartDesign::Pocket] Pocket018
  BaseFeature = -> BaseBend004
  Direction = (-0.642788,0.766044,0)
  Length = 5
  Length2 = 5
  Profile = -> Sketch067
  ReferenceAxis = -> Sketch067 [N_Axis]
  Reversed = true
  Suppressed = false
  Type = 1
FEATURE [PartDesign::Pocket] Pocket019
  BaseFeature = -> Pocket018
  Direction = (0.5,-0.866025,0)
  Length = 5
  Length2 = 5
  Profile = -> Sketch068
  ReferenceAxis = -> Sketch068 [N_Axis]
  Reversed = true
  Suppressed = false
  Type = 0
FEATURE [PartDesign::Mirrored] Mirrored006
  BaseFeature = -> Pocket019
  MirrorPlane = -> DatumPlane002
  Originals = -> [Pocket018,Pocket019]
  Suppressed = false
FEATURE [Part::FeaturePython] Placment011  # WARN: FeaturePython — macro-defined, semantics opaque (R4)
  AttacherType = Attacher::AttachEngine3D
  AttachmentOffset = pos=(-1,0,10) rot=(0.57735,0.57735,0.57735;2.0944rad)
  ExposePlacement = true
  MapMode = 7
  MarkerShape = 1
  MarkerSize = 50
  NumElements = 1
  Placement = pos=(311.26,144.338,0) rot=(0.671543,-0.313146,0.671543;2.53465rad)
  Type = lattice2AttachablePlacement.AttachablePlacement
  isLattice = 1
FEATURE [PartDesign::CoordinateSystem] Local_CS025  label="face_lamp_fix_LCS"
  AttacherType = Attacher::AttachEngine3D
  AttachmentOffset = pos=(319.563,0,182) rot=(0,0,1;0rad)
  AttachmentSupport = -> [XY_Plane]
  MapMode = 5
  Placement = pos=(319.563,0,182) rot=(0,0,1;0rad)
  expr: AttachmentOffset = <<face_lamp_fix_placement>>.Placement
FEATURE [PartDesign::CoordinateSystem] Local_CS026  label="lamp_fix_base_LCS"
  AttacherType = Attacher::AttachEngine3D
  MapMode = 5
FEATURE [PartDesign::Plane] DatumPlane003
  AttachmentOffset = pos=(0,0,450) rot=(0,0,1;0rad)
  Length = 399.511
  MapMode = 5
  Placement = pos=(0,0,450) rot=(0,0,1;0rad)
  ResizeMode = 0
  Width = 284.889
  expr: .AttachmentOffset.Base.z = <<BaseBend005>>.length / 2
FEATURE [Sketcher::SketchObject] Sketch069
  AttachmentOffset = pos=(0,0,0) rot=(0,1,0;1.5708rad)
  FullyConstrained = true
  MapMode = 7
  Placement = pos=(-299.412,134.005,0) rot=(0.249244,0.684791,0.684791;2.65306rad)
  sketch-geometry (3):
    g0: ArcOfCircle CenterX=3 CenterY=3 CenterZ=0 NormalX=0 NormalY=0 NormalZ=1 AngleXU=0 Radius=3 StartAngle=3.14159 EndAngle=4.71239
    g1: LineSegment StartX=2.6446e-12 StartY=3 StartZ=0 EndX=0 EndY=0 EndZ=0
    g2: LineSegment StartX=0 StartY=0 StartZ=0 EndX=3 EndY=2.6446e-12 EndZ=0
  constraints (7):
    c: Coincident(g1,g2)
    c: Tangent(g2,g0) = -1.5708
    c: Tangent(g0,g1) = -1.5708
    c: Coincident(g1,g-1)
    c: PointOnObject(g0,g-1)
    c: PointOnObject(g0,g-2)
    c: Radius(g0) = 3
FEATURE [Sketcher::SketchObject] Sketch070
  AttachmentOffset = pos=(0,0,0) rot=(0,1,0;1.5708rad)
  FullyConstrained = true
  MapMode = 7
  Placement = pos=(-263.568,197.924,0) rot=(0.935113,-0.250563,-0.250563;1.63783rad)
  sketch-geometry (3):
    g0: LineSegment StartX=-3 StartY=2.571e-13 StartZ=0 EndX=0 EndY=0 EndZ=0
    g1: LineSegment StartX=0 StartY=0 StartZ=0 EndX=0 EndY=3 EndZ=0
    g2: ArcOfCircle CenterX=-3 CenterY=3 CenterZ=0 NormalX=0 NormalY=0 NormalZ=1 AngleXU=0 Radius=3 StartAngle=4.71239 EndAngle=6.28319
  constraints (7):
    c: Coincident(g0,g-1)
    c: Coincident(g0,g1)
    c: Tangent(g2,g0) = -1.5708
    c: Tangent(g2,g1) = -1.5708
    c: Radius(g2) = 3
    c: PointOnObject(g1,g-2)
    c: PointOnObject(g0,g-1)
FEATURE [Part::FeaturePython] Mirror004  label="Mirror004 of Placment010"  # WARN: FeaturePython — macro-defined, semantics opaque (R4)
  ExposePlacement = false
  FlipX = true
  FlipY = false
  FlipZ = false
  MarkerShape = 1
  MarkerSize = 50
  NumElements = 1
  Object = -> Placment010
  ObjectTraversal = 0
  Type = lattice2Mirror.LatticeMirror
  isLattice = 1
FEATURE [PartDesign::CoordinateSystem] Local_CS027
  AttacherType = Attacher::AttachEngine3D
  MapMode = 5
FEATURE [PartDesign::CoordinateSystem] Local_CS028  label="lamp_fix_lamp_LCS"
  AttacherType = Attacher::AttachEngine3D
  MapMode = 2
  Placement = pos=(280.639,195.271,450) rot=(0.834817,-0.389282,-0.389282;1.75037rad)
FEATURE [Part::Feature] Unfold001
  shape: bbox 68.43 x 81.42 x 900 mm, 52 faces (baked)
FEATURE [Sketcher::SketchObject] Unfold_Sketch001  label="lamp_fix_mirror_Group_Sketch"
  FullyConstrained = false
  sketch-geometry (50):
    g0: ArcOfCircle CenterX=-115.039 CenterY=3 CenterZ=0 NormalX=0 NormalY=0 NormalZ=1 AngleXU=1e-16 Radius=3 StartAngle=3.14159 EndAngle=4.71239
    g1: LineSegment StartX=-115.039 StartY=0 StartZ=0 EndX=-15.1723 EndY=0 EndZ=0
    g2: ArcOfCircle CenterX=-15.1723 CenterY=3 CenterZ=0 NormalX=0 NormalY=0 NormalZ=1 AngleXU=1e-16 Radius=3 StartAngle=4.71239 EndAngle=6.28319
    g3: LineSegment StartX=-12.1723 StartY=3 StartZ=0 EndX=-12.1723 EndY=897 EndZ=0
    g4: ArcOfCircle CenterX=-15.1723 CenterY=897 CenterZ=0 NormalX=0 NormalY=0 NormalZ=1 AngleXU=-1e-16 Radius=3 StartAngle=1e-16 EndAngle=1.5708
    g5: LineSegment StartX=-115.039 StartY=900 StartZ=0 EndX=-15.1723 EndY=900 EndZ=0
    g6: ArcOfCircle CenterX=-115.039 CenterY=897 CenterZ=0 NormalX=0 NormalY=0 NormalZ=1 AngleXU=-1e-16 Radius=3 StartAngle=1.5708 EndAngle=3.14159
    g7: LineSegment StartX=-118.039 StartY=842 StartZ=0 EndX=-118.039 EndY=897 EndZ=0
    g8: ArcOfCircle CenterX=-116.039 CenterY=842 CenterZ=0 NormalX=0 NormalY=0 NormalZ=1 AngleXU=1e-16 Radius=2 StartAngle=3.14159 EndAngle=4.71239
    g9: LineSegment StartX=-116.039 StartY=840 StartZ=0 EndX=-91.3045 EndY=840 EndZ=0
    g10: ArcOfCircle CenterX=-91.3045 CenterY=838 CenterZ=0 NormalX=0 NormalY=0 NormalZ=1 AngleXU=-2e-16 Radius=2 StartAngle=2e-16 EndAngle=1.5708
    g11: LineSegment StartX=-89.3045 StartY=838 StartZ=0 EndX=-89.3045 EndY=628.6 EndZ=0
    g12: ArcOfCircle CenterX=-91.3045 CenterY=628.6 CenterZ=0 NormalX=0 NormalY=0 NormalZ=1 AngleXU=-2e-16 Radius=2 StartAngle=4.71239 EndAngle=6.28319
    g13: LineSegment StartX=-91.3045 StartY=626.6 StartZ=0 EndX=-116.039 EndY=626.6 EndZ=0
    g14: ArcOfCircle CenterX=-116.039 CenterY=624.6 CenterZ=0 NormalX=0 NormalY=0 NormalZ=1 AngleXU=1e-16 Radius=2 StartAngle=1.5708 EndAngle=3.14159
    g15: LineSegment StartX=-118.039 StartY=558.7 StartZ=0 EndX=-118.039 EndY=624.6 EndZ=0
    g16: ArcOfCircle CenterX=-116.039 CenterY=558.7 CenterZ=0 NormalX=0 NormalY=0 NormalZ=1 AngleXU=1e-16 Radius=2 StartAngle=3.14159 EndAngle=4.71239
    g17: LineSegment StartX=-116.039 StartY=556.7 StartZ=0 EndX=-91.3045 EndY=556.7 EndZ=0
    g18: ArcOfCircle CenterX=-91.3045 CenterY=554.7 CenterZ=0 NormalX=0 NormalY=0 NormalZ=1 AngleXU=-2e-16 Radius=2 StartAngle=2e-16 EndAngle=1.5708
    g19: LineSegment StartX=-89.3045 StartY=554.7 StartZ=0 EndX=-89.3045 EndY=345.3 EndZ=0
    g20: ArcOfCircle CenterX=-91.3045 CenterY=345.3 CenterZ=0 NormalX=0 NormalY=0 NormalZ=1 AngleXU=-2e-16 Radius=2 StartAngle=4.71239 EndAngle=6.28319
    g21: LineSegment StartX=-91.3045 StartY=343.3 StartZ=0 EndX=-116.039 EndY=343.3 EndZ=0
    g22: ArcOfCircle CenterX=-116.039 CenterY=341.3 CenterZ=0 NormalX=0 NormalY=0 NormalZ=1 AngleXU=1e-16 Radius=2 StartAngle=1.5708 EndAngle=3.14159
    g23: LineSegment StartX=-118.039 StartY=275.4 StartZ=0 EndX=-118.039 EndY=341.3 EndZ=0
    g24: ArcOfCircle CenterX=-116.039 CenterY=275.4 CenterZ=0 NormalX=0 NormalY=0 NormalZ=1 AngleXU=1e-16 Radius=2 StartAngle=3.14159 EndAngle=4.71239
    g25: LineSegment StartX=-116.039 StartY=273.4 StartZ=0 EndX=-91.3045 EndY=273.4 EndZ=0
    g26: ArcOfCircle CenterX=-91.3045 CenterY=271.4 CenterZ=0 NormalX=0 NormalY=0 NormalZ=1 AngleXU=-2e-16 Radius=2 StartAngle=-2.84e-14 EndAngle=1.5708
    g27: LineSegment StartX=-89.3045 StartY=271.4 StartZ=0 EndX=-89.3045 EndY=62 EndZ=0
    g28: ArcOfCircle CenterX=-91.3045 CenterY=62 CenterZ=0 NormalX=0 NormalY=0 NormalZ=1 AngleXU=-2e-16 Radius=2 StartAngle=4.71239 EndAngle=6.28319
    g29: LineSegment StartX=-91.3045 StartY=60 StartZ=0 EndX=-116.039 EndY=60 EndZ=0
    g30: ArcOfCircle CenterX=-116.039 CenterY=58 CenterZ=0 NormalX=0 NormalY=0 NormalZ=1 AngleXU=1e-16 Radius=2 StartAngle=1.5708 EndAngle=3.14159
    g31: LineSegment StartX=-118.039 StartY=3 StartZ=0 EndX=-118.039 EndY=58 EndZ=0
    g32: LineSegment StartX=-114.132 StartY=896 StartZ=0 EndX=-112.438 EndY=892.366 EndZ=0
    g33: LineSegment StartX=-112.438 StartY=892.366 StartZ=0 EndX=-110.744 EndY=896 EndZ=0
    g34: LineSegment StartX=-110.744 StartY=896 StartZ=0 EndX=-109.837 EndY=895.577 EndZ=0
    g35: LineSegment StartX=-109.837 StartY=895.577 StartZ=0 EndX=-112.438 EndY=890 EndZ=0
    g36: LineSegment StartX=-112.438 StartY=890 StartZ=0 EndX=-115.039 EndY=895.577 EndZ=0
    g37: LineSegment StartX=-115.039 StartY=895.577 StartZ=0 EndX=-114.132 EndY=896 EndZ=0
    g38: LineSegment StartX=-115.039 StartY=4.42262 StartZ=0 EndX=-114.132 EndY=4 EndZ=0
    g39: LineSegment StartX=-112.438 StartY=10 StartZ=0 EndX=-115.039 EndY=4.42262 EndZ=0
    g40: LineSegment StartX=-109.837 StartY=4.42262 StartZ=0 EndX=-112.438 EndY=10 EndZ=0
    g41: LineSegment StartX=-110.744 StartY=4 StartZ=0 EndX=-109.837 EndY=4.42262 EndZ=0
    g42: LineSegment StartX=-112.438 StartY=7.6338 StartZ=0 EndX=-110.744 EndY=4 EndZ=0
    g43: LineSegment StartX=-114.132 StartY=4 StartZ=0 EndX=-112.438 EndY=7.6338 EndZ=0
    g44: Circle CenterX=-106.039 CenterY=870 CenterZ=0 NormalX=0 NormalY=0 NormalZ=1 AngleXU=1.5708 Radius=1.7
    g45: Circle CenterX=-106.039 CenterY=590 CenterZ=0 NormalX=0 NormalY=0 NormalZ=1 AngleXU=1.5708 Radius=1.7
    g46: Circle CenterX=-106.039 CenterY=30 CenterZ=0 NormalX=0 NormalY=0 NormalZ=1 AngleXU=1.5708 Radius=1.7
    g47: Circle CenterX=-106.039 CenterY=310 CenterZ=0 NormalX=0 NormalY=0 NormalZ=1 AngleXU=1.5708 Radius=1.7
    g48: Circle CenterX=-38.6545 CenterY=895 CenterZ=0 NormalX=0 NormalY=0 NormalZ=-1 AngleXU=1e-16 Radius=1.6
    g49: Circle CenterX=-30.3545 CenterY=5 CenterZ=0 NormalX=0 NormalY=0 NormalZ=-1 AngleXU=1e-16 Radius=1.6
FEATURE [Sketcher::SketchObject] Unfold_Sketch_Outline001
  FullyConstrained = false
  sketch-geometry (32):
    g0: ArcOfCircle CenterX=-115.039 CenterY=3 CenterZ=0 NormalX=0 NormalY=0 NormalZ=1 AngleXU=1e-16 Radius=3 StartAngle=3.14159 EndAngle=4.71239
    g1: LineSegment StartX=-115.039 StartY=0 StartZ=0 EndX=-15.1723 EndY=0 EndZ=0
    g2: ArcOfCircle CenterX=-15.1723 CenterY=3 CenterZ=0 NormalX=0 NormalY=0 NormalZ=1 AngleXU=1e-16 Radius=3 StartAngle=4.71239 EndAngle=6.28319
    g3: LineSegment StartX=-12.1723 StartY=3 StartZ=0 EndX=-12.1723 EndY=897 EndZ=0
    g4: ArcOfCircle CenterX=-15.1723 CenterY=897 CenterZ=0 NormalX=0 NormalY=0 NormalZ=1 AngleXU=-1e-16 Radius=3 StartAngle=1e-16 EndAngle=1.5708
    g5: LineSegment StartX=-115.039 StartY=900 StartZ=0 EndX=-15.1723 EndY=900 EndZ=0
    g6: ArcOfCircle CenterX=-115.039 CenterY=897 CenterZ=0 NormalX=0 NormalY=0 NormalZ=1 AngleXU=-1e-16 Radius=3 StartAngle=1.5708 EndAngle=3.14159
    g7: LineSegment StartX=-118.039 StartY=842 StartZ=0 EndX=-118.039 EndY=897 EndZ=0
    g8: ArcOfCircle CenterX=-116.039 CenterY=842 CenterZ=0 NormalX=0 NormalY=0 NormalZ=1 AngleXU=1e-16 Radius=2 StartAngle=3.14159 EndAngle=4.71239
    g9: LineSegment StartX=-116.039 StartY=840 StartZ=0 EndX=-91.3045 EndY=840 EndZ=0
    g10: ArcOfCircle CenterX=-91.3045 CenterY=838 CenterZ=0 NormalX=0 NormalY=0 NormalZ=1 AngleXU=-2e-16 Radius=2 StartAngle=2e-16 EndAngle=1.5708
    g11: LineSegment StartX=-89.3045 StartY=838 StartZ=0 EndX=-89.3045 EndY=628.6 EndZ=0
    g12: ArcOfCircle CenterX=-91.3045 CenterY=628.6 CenterZ=0 NormalX=0 NormalY=0 NormalZ=1 AngleXU=-2e-16 Radius=2 StartAngle=4.71239 EndAngle=6.28319
    g13: LineSegment StartX=-91.3045 StartY=626.6 StartZ=0 EndX=-116.039 EndY=626.6 EndZ=0
    g14: ArcOfCircle CenterX=-116.039 CenterY=624.6 CenterZ=0 NormalX=0 NormalY=0 NormalZ=1 AngleXU=1e-16 Radius=2 StartAngle=1.5708 EndAngle=3.14159
    g15: LineSegment StartX=-118.039 StartY=558.7 StartZ=0 EndX=-118.039 EndY=624.6 EndZ=0
    g16: ArcOfCircle CenterX=-116.039 CenterY=558.7 CenterZ=0 NormalX=0 NormalY=0 NormalZ=1 AngleXU=1e-16 Radius=2 StartAngle=3.14159 EndAngle=4.71239
    g17: LineSegment StartX=-116.039 StartY=556.7 StartZ=0 EndX=-91.3045 EndY=556.7 EndZ=0
    g18: ArcOfCircle CenterX=-91.3045 CenterY=554.7 CenterZ=0 NormalX=0 NormalY=0 NormalZ=1 AngleXU=-2e-16 Radius=2 StartAngle=2e-16 EndAngle=1.5708
    g19: LineSegment StartX=-89.3045 StartY=554.7 StartZ=0 EndX=-89.3045 EndY=345.3 EndZ=0
    g20: ArcOfCircle CenterX=-91.3045 CenterY=345.3 CenterZ=0 NormalX=0 NormalY=0 NormalZ=1 AngleXU=-2e-16 Radius=2 StartAngle=4.71239 EndAngle=6.28319
    g21: LineSegment StartX=-91.3045 StartY=343.3 StartZ=0 EndX=-116.039 EndY=343.3 EndZ=0
    g22: ArcOfCircle CenterX=-116.039 CenterY=341.3 CenterZ=0 NormalX=0 NormalY=0 NormalZ=1 AngleXU=1e-16 Radius=2 StartAngle=1.5708 EndAngle=3.14159
    g23: LineSegment StartX=-118.039 StartY=275.4 StartZ=0 EndX=-118.039 EndY=341.3 EndZ=0
    g24: ArcOfCircle CenterX=-116.039 CenterY=275.4 CenterZ=0 NormalX=0 NormalY=0 NormalZ=1 AngleXU=1e-16 Radius=2 StartAngle=3.14159 EndAngle=4.71239
    g25: LineSegment StartX=-116.039 StartY=273.4 StartZ=0 EndX=-91.3045 EndY=273.4 EndZ=0
    g26: ArcOfCircle CenterX=-91.3045 CenterY=271.4 CenterZ=0 NormalX=0 NormalY=0 NormalZ=1 AngleXU=-2e-16 Radius=2 StartAngle=-2.84e-14 EndAngle=1.5708
    g27: LineSegment StartX=-89.3045 StartY=271.4 StartZ=0 EndX=-89.3045 EndY=62 EndZ=0
    g28: ArcOfCircle CenterX=-91.3045 CenterY=62 CenterZ=0 NormalX=0 NormalY=0 NormalZ=1 AngleXU=-2e-16 Radius=2 StartAngle=4.71239 EndAngle=6.28319
    g29: LineSegment StartX=-91.3045 StartY=60 StartZ=0 EndX=-116.039 EndY=60 EndZ=0
    g30: ArcOfCircle CenterX=-116.039 CenterY=58 CenterZ=0 NormalX=0 NormalY=0 NormalZ=1 AngleXU=1e-16 Radius=2 StartAngle=1.5708 EndAngle=3.14159
    g31: LineSegment StartX=-118.039 StartY=3 StartZ=0 EndX=-118.039 EndY=58 EndZ=0
FEATURE [Sketcher::SketchObject] Unfold_Sketch_Internal001
  FullyConstrained = false
  sketch-geometry (18):
    g0: LineSegment StartX=-114.132 StartY=896 StartZ=0 EndX=-112.438 EndY=892.366 EndZ=0
    g1: LineSegment StartX=-112.438 StartY=892.366 StartZ=0 EndX=-110.744 EndY=896 EndZ=0
    g2: LineSegment StartX=-110.744 StartY=896 StartZ=0 EndX=-109.837 EndY=895.577 EndZ=0
    g3: LineSegment StartX=-109.837 StartY=895.577 StartZ=0 EndX=-112.438 EndY=890 EndZ=0
    g4: LineSegment StartX=-112.438 StartY=890 StartZ=0 EndX=-115.039 EndY=895.577 EndZ=0
    g5: LineSegment StartX=-115.039 StartY=895.577 StartZ=0 EndX=-114.132 EndY=896 EndZ=0
    g6: LineSegment StartX=-115.039 StartY=4.42262 StartZ=0 EndX=-114.132 EndY=4 EndZ=0
    g7: LineSegment StartX=-114.132 StartY=4 StartZ=0 EndX=-112.438 EndY=7.6338 EndZ=0
    g8: LineSegment StartX=-112.438 StartY=7.6338 StartZ=0 EndX=-110.744 EndY=4 EndZ=0
    g9: LineSegment StartX=-110.744 StartY=4 StartZ=0 EndX=-109.837 EndY=4.42262 EndZ=0
    g10: LineSegment StartX=-109.837 StartY=4.42262 StartZ=0 EndX=-112.438 EndY=10 EndZ=0
    g11: LineSegment StartX=-112.438 StartY=10 StartZ=0 EndX=-115.039 EndY=4.42262 EndZ=0
    g12: Circle CenterX=-106.039 CenterY=590 CenterZ=0 NormalX=0 NormalY=0 NormalZ=1 AngleXU=1.5708 Radius=1.7
    g13: Circle CenterX=-106.039 CenterY=870 CenterZ=0 NormalX=0 NormalY=0 NormalZ=1 AngleXU=1.5708 Radius=1.7
    g14: Circle CenterX=-106.039 CenterY=30 CenterZ=0 NormalX=0 NormalY=0 NormalZ=1 AngleXU=1.5708 Radius=1.7
    g15: Circle CenterX=-106.039 CenterY=310 CenterZ=0 NormalX=0 NormalY=0 NormalZ=1 AngleXU=1.5708 Radius=1.7
    g16: Circle CenterX=-38.6545 CenterY=895 CenterZ=0 NormalX=0 NormalY=0 NormalZ=-1 AngleXU=1e-16 Radius=1.6
    g17: Circle CenterX=-30.3545 CenterY=5 CenterZ=0 NormalX=0 NormalY=0 NormalZ=-1 AngleXU=1e-16 Radius=1.6
FEATURE [Sketcher::SketchObject] Unfold_Sketch_bends001
  FullyConstrained = false
  sketch-geometry (5):
    g0: LineSegment StartX=-93.2716 StartY=60 StartZ=0 EndX=-93.2716 EndY=0 EndZ=0
    g1: LineSegment StartX=-23.6119 StartY=900 StartZ=0 EndX=-23.6119 EndY=0 EndZ=0
    g2: LineSegment StartX=-93.2716 StartY=900 StartZ=0 EndX=-93.2716 EndY=840 EndZ=0
    g3: LineSegment StartX=-93.2716 StartY=343.3 StartZ=0 EndX=-93.2716 EndY=273.4 EndZ=0
    g4: LineSegment StartX=-93.2716 StartY=626.6 StartZ=0 EndX=-93.2716 EndY=556.7 EndZ=0
FEATURE [Part::FeaturePython] Placment012  # WARN: FeaturePython — macro-defined, semantics opaque (R4)
  AttacherType = Attacher::AttachEngine3D
  ExposePlacement = true
  MarkerShape = 1
  MarkerSize = 50
  NumElements = 1
  Placement = pos=(323,150,0) rot=(0,0,1;0rad)
  Type = lattice2AttachablePlacement.AttachablePlacement
  isLattice = 1
  expr: .Placement.Base.y = <<base_Sketch>>.Constraints.total_depth
FEATURE [Part::FeaturePython] Placment013  label="face_lamp_fix_placement"  # WARN: FeaturePython — macro-defined, semantics opaque (R4)
  AttacherType = Attacher::AttachEngine3D
  ExposePlacement = true
  MarkerShape = 1
  MarkerSize = 50
  NumElements = 1
  Placement = pos=(319.563,0,182) rot=(0,0,1;0rad)
  Type = lattice2AttachablePlacement.AttachablePlacement
  isLattice = 1
  expr: .Placement.Base.x = <<face_section_LCS>>.Placement.Base.x
FEATURE [Part::FeaturePython] Placment014  # WARN: FeaturePython — macro-defined, semantics opaque (R4)
  AttacherType = Attacher::AttachEngine3D
  ExposePlacement = true
  MarkerShape = 1
  MarkerSize = 50
  NumElements = 1
  Placement = pos=(-323,150,0) rot=(0,0,1;0rad)
  Type = lattice2AttachablePlacement.AttachablePlacement
  isLattice = 1
  expr: .Placement.Base.x = -<<Placment012>>.Placement.Base.x
  expr: .Placement.Base.y = <<Placment012>>.Placement.Base.y
  expr: .Placement.Base.z = <<Placment012>>.Placement.Base.z
FEATURE [Part::FeaturePython] Placment015  # WARN: FeaturePython — macro-defined, semantics opaque (R4)
  AttacherType = Attacher::AttachEngine3D
  ExposePlacement = true
  MarkerShape = 1
  MarkerSize = 100
  NumElements = 1
  Placement = pos=(-319.563,0,182) rot=(0,0,1;0rad)
  Type = lattice2AttachablePlacement.AttachablePlacement
  isLattice = 1
  expr: .Placement.Base.x = -<<face_lamp_fix_placement>>.Placement.Base.x
  expr: .Placement.Base.y = <<face_lamp_fix_placement>>.Placement.Base.y
  expr: .Placement.Base.z = <<face_lamp_fix_placement>>.Placement.Base.z
FEATURE [Part::FeaturePython] Join008  # WARN: FeaturePython — macro-defined, semantics opaque (R4)
  ExposePlacement = false
  Interleave = false
  Links = -> [Placment013,Placment015]
  MarkerShape = 1
  MarkerSize = 0
  NumElements = 2
  Type = lattice2JoinArrays.JoinArrays
  isLattice = 1
FEATURE [Part::FeaturePython] Join009  # WARN: FeaturePython — macro-defined, semantics opaque (R4)
  ExposePlacement = false
  Interleave = false
  Links = -> [Placment012,Placment014]
  MarkerShape = 1
  MarkerSize = 0
  NumElements = 2
  Type = lattice2JoinArrays.JoinArrays
  isLattice = 1
FEATURE [Part::FeaturePython] Populate034  label="Populate Join008 with Join009"  # WARN: FeaturePython — macro-defined, semantics opaque (R4)
  Copying = 0
  ExposePlacement = false
  MarkerShape = 1
  MarkerSize = 0
  NumElements = 4
  Object = -> Join009
  OutputCompounding = 0
  PlacementsTo = -> Join008
  Referencing = 0
  Type = lattice2PopulateCopies.LatticePopulateCopies
  isLattice = 1
FEATURE [Sketcher::SketchObject] Sketch072
  FullyConstrained = true
  Placement = pos=(0,0,0) rot=(1,0,0;1.5708rad)
  sketch-geometry (16):
    g0: LineSegment StartX=-1.6 StartY=-1 StartZ=0 EndX=1.6 EndY=-1 EndZ=0
    g1: LineSegment StartX=1.6 StartY=-1 StartZ=0 EndX=1.6 EndY=61 EndZ=0
    g2: LineSegment StartX=1.6 StartY=61 StartZ=0 EndX=-1.6 EndY=61 EndZ=0
    g3: LineSegment StartX=-1.6 StartY=61 StartZ=0 EndX=-1.6 EndY=-1 EndZ=0
    g4: LineSegment StartX=-1.6 StartY=272.4 StartZ=0 EndX=1.6 EndY=272.4 EndZ=0
    g5: LineSegment StartX=1.6 StartY=272.4 StartZ=0 EndX=1.6 EndY=344.3 EndZ=0
    g6: LineSegment StartX=1.6 StartY=344.3 StartZ=0 EndX=-1.6 EndY=344.3 EndZ=0
    g7: LineSegment StartX=-1.6 StartY=344.3 StartZ=0 EndX=-1.6 EndY=272.4 EndZ=0
    g8: LineSegment StartX=-1.6 StartY=555.7 StartZ=0 EndX=1.6 EndY=555.7 EndZ=0
    g9: LineSegment StartX=1.6 StartY=555.7 StartZ=0 EndX=1.6 EndY=627.6 EndZ=0
    g10: LineSegment StartX=1.6 StartY=627.6 StartZ=0 EndX=-1.6 EndY=627.6 EndZ=0
    g11: LineSegment StartX=-1.6 StartY=627.6 StartZ=0 EndX=-1.6 EndY=555.7 EndZ=0
    g12: LineSegment StartX=-1.6 StartY=839 StartZ=0 EndX=1.6 EndY=839 EndZ=0
    g13: LineSegment StartX=1.6 StartY=839 StartZ=0 EndX=1.6 EndY=901 EndZ=0
    g14: LineSegment StartX=1.6 StartY=901 StartZ=0 EndX=-1.6 EndY=901 EndZ=0
    g15: LineSegment StartX=-1.6 StartY=901 StartZ=0 EndX=-1.6 EndY=839 EndZ=0
  constraints (47):
    c: Coincident(g0,g1)
    c: Coincident(g1,g2)
    c: Coincident(g2,g3)
    c: Horizontal(g2)
    c: Vertical(g1)
    c: Vertical(g3)
    c: Coincident(g4,g5)
    c: Coincident(g5,g6)
    c: Coincident(g6,g7)
    c: Coincident(g7,g4)
    c: Horizontal(g4)
    c: Horizontal(g6)
    c: Vertical(g5)
    c: Vertical(g7)
    c: Coincident(g8,g9)
    c: Coincident(g9,g10)
    c: Coincident(g10,g11)
    c: Coincident(g11,g8)
    c: Horizontal(g8)
    c: Horizontal(g10)
    c: Vertical(g9)
    c: Vertical(g11)
    c: Coincident(g12,g13)
    c: Coincident(g13,g14)
    c: Coincident(g14,g15)
    c: Coincident(g15,g12)
    c: Horizontal(g12)
    c: Horizontal(g14)
    c: Vertical(g13)
    c: Vertical(g15)
    c: Coincident(g3,g0)
    c: Distance(g-1,g0) = 1
    c: Vertical(g4,g2)
    c: Vertical(g8,g6)
    c: Vertical(g10,g12)
    c: Vertical(g1,g4)
    c: Vertical(g5,g8)
    c: Vertical(g9,g12)
    c: Symmetric(g0,g0,g-2)
    c: DistanceX(g0,g0) = 3.2
    c: DistanceY(g1,g1) = 62
    c: DistanceY(g4) = 272.4
    c: DistanceY(g5) = 344.3
    c: DistanceY(g8) = 555.7
    c: DistanceY(g9) = 627.6
    c: DistanceY(g12) = 839
    c: DistanceY(g13) = 901
FEATURE [Part::Extrusion] Extrude013
  Base = -> Sketch072
  Dir = (0,-1,2e-16)
  DirMode = 2
  FaceMakerClass = Part::FaceMakerBullseye
  LengthFwd = 10
  LengthRev = 0
  Solid = true
  Symmetric = false
FEATURE [Sketcher::SketchObject] Sketch075
  AttachmentOffset = pos=(0,0,0) rot=(0,0.707107,0.707107;3.14159rad)
  FullyConstrained = true
  MapMode = 5
  Placement = pos=(484.198,20,100) rot=(0,0.707107,0.707107;3.14159rad)
  sketch-geometry (5):
    g0: LineSegment StartX=18.7482 StartY=0 StartZ=0 EndX=-1 EndY=0 EndZ=0
    g1: LineSegment StartX=-1 StartY=0 StartZ=0 EndX=-1 EndY=15 EndZ=0
    g2: LineSegment StartX=-1 StartY=15 StartZ=0 EndX=1 EndY=15 EndZ=0
    g3: ArcOfCircle CenterX=1 CenterY=0 CenterZ=0 NormalX=0 NormalY=0 NormalZ=1 AngleXU=0 Radius=15 StartAngle=0.167448 EndAngle=1.5708
    g4: ArcOfCircle CenterX=18.7482 CenterY=3 CenterZ=0 NormalX=0 NormalY=0 NormalZ=1 AngleXU=0 Radius=3 StartAngle=3.30904 EndAngle=4.71239
  constraints (14):
    c: PointOnObject(g0,g-1)
    c: Horizontal(g0)
    c: Coincident(g0,g1)
    c: Vertical(g1)
    c: Coincident(g1,g2)
    c: Horizontal(g2)
    c: PointOnObject(g3,g-1)
    c: Tangent(g4,g0) = 1.5708
    c: Tangent(g3,g2) = 1.5708
    c: Tangent(g4,g3) = 1.5708
    c: Radius(g4) = 3
    c: Radius(g3) = 15
    c: DistanceX(g2) = 1
    c: DistanceX(g1) = -1
FEATURE [Sketcher::SketchObject] Sketch076
  AttachmentOffset = pos=(0,0,0) rot=(0.889126,0.323616,0.323616;1.68804rad)
  FullyConstrained = true
  MapMode = 5
  Placement = pos=(484.198,20,100) rot=(0.889126,0.323616,0.323616;1.68804rad)
  expr: .AttachmentOffset.Rotation.Yaw = <<base_Sketch>>.Constraints.angle
  sketch-geometry (5):
    g0: LineSegment StartX=18.7482 StartY=0 StartZ=0 EndX=-1 EndY=0 EndZ=0
    g1: LineSegment StartX=-1 StartY=0 StartZ=0 EndX=-1 EndY=15 EndZ=0
    g2: LineSegment StartX=-1 StartY=15 StartZ=0 EndX=1 EndY=15 EndZ=0
    g3: ArcOfCircle CenterX=1 CenterY=0 CenterZ=0 NormalX=0 NormalY=0 NormalZ=1 AngleXU=0 Radius=15 StartAngle=0.167448 EndAngle=1.5708
    g4: ArcOfCircle CenterX=18.7482 CenterY=3 CenterZ=0 NormalX=0 NormalY=0 NormalZ=1 AngleXU=0 Radius=3 StartAngle=3.30904 EndAngle=4.71239
  constraints (14):
    c: PointOnObject(g0,g-1)
    c: PointOnObject(g0,g-1)
    c: Coincident(g0,g1)
    c: Vertical(g1)
    c: Coincident(g1,g2)
    c: Horizontal(g2)
    c: PointOnObject(g3,g-1)
    c: Tangent(g3,g2) = 1.5708
    c: Tangent(g4,g0) = 1.5708
    c: Tangent(g4,g3) = 1.5708
    c: DistanceX(g2) = 1
    c: DistanceY(g1,g1) = 15
    c: DistanceX(g1) = -1
    c: Radius(g4) = 3
FEATURE [PartDesign::Plane] DatumPlane004
  Length = 65.8114
  MapMode = 4
  Placement = pos=(319.563,20,100) rot=(0.57735,0.57735,0.57735;2.0944rad)
  ResizeMode = 0
  Width = 140.811
FEATURE [PartDesign::Plane] DatumPlane005
  Length = 60
  MapMode = 4
  Placement = pos=(0,0,0) rot=(0.57735,0.57735,0.57735;2.0944rad)
  ResizeMode = 0
  Width = 60
FEATURE [PartDesign::Mirrored] Mirrored008
  MirrorPlane = -> DatumPlane004
  Suppressed = false
FEATURE [PartDesign::LinearPattern] LinearPattern004
  Direction = -> Sketch075 [H_Axis]
  Length = 639.126
  Mode = 0
  Occurrences = 2
  Offset = 639.126
  Suppressed = false
  expr: Length = <<Dimensions>>.Constraints.modules_middle_distance * 2
FEATURE [Sketcher::SketchObject] Sketch078
  AttachmentOffset = pos=(0,0,0) rot=(0,1,0;1.5708rad)
  AttachmentSupport = -> [Sketch021]
  FullyConstrained = true
  MapMode = 7
  Placement = pos=(312.163,124.732,0) rot=(0.889126,0.323616,0.323616;1.68804rad)
  sketch-geometry (2):
    g0: Circle CenterX=-15 CenterY=10 CenterZ=0 NormalX=0 NormalY=0 NormalZ=1 AngleXU=0 Radius=1.7
    g1: Circle CenterX=-153 CenterY=10 CenterZ=0 NormalX=0 NormalY=0 NormalZ=1 AngleXU=0 Radius=1.7
  constraints (6):
    c: Diameter(g0) = 3.4
    c: DistanceX(g0) = -15
    c: DistanceY(g0) = 10
    c: Equal(g1,g0)
    c: Horizontal(g0,g1)
    c: DistanceX(g1) = -153
FEATURE [Part::Extrusion] Extrude016
  Base = -> Sketch078
  Dir = (0.642788,-0.766044,2e-16)
  DirMode = 2
  FaceMakerClass = Part::FaceMakerBullseye
  LengthFwd = 10
  LengthRev = 0
  Solid = true
  Symmetric = true
FEATURE [Part::Mirroring] Part__Mirroring018  label="Extrude016 (Mirror #19)"
  Base = (0,0,0)
  Normal = (1,0,0)
  Source = -> Extrude016
FEATURE [Part::Compound] Compound009
  Links = -> [Populate008,Extrude007,Extrude016,Part__Mirroring018]
FEATURE [Sketcher::SketchObject] Sketch079
  FullyConstrained = true
  MapMode = 5
  sketch-geometry (5):
    g0: LineSegment StartX=-1.6 StartY=-50 StartZ=0 EndX=1.6 EndY=-50 EndZ=0
    g1: LineSegment StartX=1.6 StartY=-50 StartZ=0 EndX=1.6 EndY=50 EndZ=0
    g2: LineSegment StartX=1.6 StartY=50 StartZ=0 EndX=-1.6 EndY=50 EndZ=0
    g3: LineSegment StartX=-1.6 StartY=50 StartZ=0 EndX=-1.6 EndY=-50 EndZ=0
    g4: GeomPoint X=0 Y=0 Z=0
  constraints (12):
    c: Coincident(g0,g1)
    c: Coincident(g1,g2)
    c: Coincident(g2,g3)
    c: Coincident(g3,g0)
    c: Horizontal(g0)
    c: Horizontal(g2)
    c: Vertical(g1)
    c: Vertical(g3)
    c: Symmetric(g2,g0,g4)
    c: Coincident(g4,g-1)
    c: DistanceX(g0,g0) = 3.2
    c: DistanceY(g1,g1) = 100
FEATURE [PartDesign::Pad] Pad018
  Direction = (0,0,1)
  Length = 2.4
  Length2 = 10
  Profile = -> Sketch079
  ReferenceAxis = -> Sketch079 [N_Axis]
  Suppressed = false
  Type = 0
FEATURE [Part::MultiFuse] Fusion002
  Shapes = -> [Extrude004,Extrude005]
FEATURE [PartDesign::Boolean] Boolean015
  BaseFeature = -> Pad018
  Group = -> [Fusion002]
  Refine = true
  Suppressed = false
  Type = 0
  UsePlacement = true
FEATURE [PartDesign::Body] Body016
  Group = -> [Sketch079,Pad018,Boolean015]
  Origin = -> Origin018
  Tip = -> Boolean015
FEATURE [Part::FeaturePython] Populate007  label="Populate Populate Populate LinearArray001 with PlacementSubsequence with LinearArray002 with dropper_fix"  # WARN: FeaturePython — macro-defined, semantics opaque (R4)
  Copying = 0
  ExposePlacement = false
  MarkerShape = 1
  MarkerSize = 0
  NumElements = 0
  Object = -> Body016
  OutputCompounding = 1
  PlacementsTo = -> Populate006
  Referencing = 0
  Type = lattice2PopulateCopies.LatticePopulateCopies
  isLattice = 0
FEATURE [Part::MultiFuse] Fusion
  Refine = true
  Shapes = -> [Populate007,Extrude007]
FEATURE [PartDesign::Boolean] Boolean003
  BaseFeature = -> Pad007
  Group = -> [Fusion]
  Suppressed = false
  Type = 1
  UsePlacement = true
FEATURE [PartDesign::Body] Body004  label="dropper_fix_PP"
  Group = -> [Binder007,Pad007,Boolean003,Local_CS012]
  Origin = -> Origin005
  Tip = -> Boolean003
FEATURE [PartDesign::SubShapeBinder] Binder021
  BindCopyOnChange = 0
  BindMode = 0
  ClaimChildren = true
  Context = -> Body017 [Binder021.]
  Fuse = false
  MakeFace = true
  OffsetFill = false
  OffsetIntersection = false
  OffsetJoinType = 0
  OffsetOpenResult = false
  PartialLoad = false
  Placement = pos=(0,0,-10) rot=(0,0,1;0rad)
  Relative = false
  Support = -> [Connect007]
  _Version = 2
FEATURE [PartDesign::FeaturePython] BaseBend006  label="drain_holder_BaseBend"  # WARN: FeaturePython — macro-defined, semantics opaque (R4)
  BendSide = 0
  BendSketch = -> Binder021
  MidPlane = false
  Reverse = false
  Suppressed = false
  length = 110
  radius = 0.1
  thickness = 0.3
FEATURE [Sketcher::SketchObject] Sketch081  label="cap_outer_base_Sketch"
  FullyConstrained = true
  expr: .Constraints.depth = <<Dimensions>>.Constraints.depth + 5 mm
  expr: .Constraints.length = <<Dimensions>>.Constraints.width
  sketch-geometry (3):
    g0: LineSegment StartX=639.126 StartY=0 StartZ=0 EndX=639.126 EndY=155 EndZ=0
    g1: LineSegment StartX=639.126 StartY=155 StartZ=0 EndX=-639.126 EndY=155 EndZ=0
    g2: LineSegment StartX=-639.126 StartY=155 StartZ=0 EndX=-639.126 EndY=0 EndZ=0
  constraints (9):
    c: PointOnObject(g0,g-1)
    c: Vertical(g0)
    c: Coincident(g0,g1)
    c: Coincident(g1,g2)
    c: PointOnObject(g2,g-1)
    c: Vertical(g2)
    c: DistanceY(g0) = 155  'depth'
    c: DistanceX(g1,g1) = 1278.25  'length'
    c: Symmetric(g0,g1,g-2)
FEATURE [PartDesign::SubShapeBinder] Binder022
  BindCopyOnChange = 0
  BindMode = 0
  ClaimChildren = true
  Context = -> Body018 [Binder022.]
  Fuse = false
  MakeFace = true
  OffsetFill = false
  OffsetIntersection = false
  OffsetJoinType = 0
  OffsetOpenResult = false
  PartialLoad = false
  Relative = false
  Support = -> [Sketch081]
  _Version = 2
FEATURE [PartDesign::FeaturePython] BaseBend007  label="cap_outer_BaseBend"  # WARN: FeaturePython — macro-defined, semantics opaque (R4)
  BendSide = 1
  BendSketch = -> Binder022
  MidPlane = false
  Reverse = false
  Suppressed = false
  length = 50
  radius = 0.1
  thickness = 0.3
FEATURE [PartDesign::FeaturePython] Bend005  # WARN: FeaturePython — macro-defined, semantics opaque (R4)
  AutoMiter = false
  BaseFeature = -> BaseBend007
  BendType = 1
  LengthList = [155]
  LengthSpec = 1
  ReliefFactor = 0.7
  Suppressed = false
  UseReliefFactor = false
  angle = 90
  baseObject = -> BaseBend007 [Edge43,Edge29,Edge14]
  bendAList = [90]
  extend1 = 0
  extend2 = 0
  gap1 = 0
  gap2 = 0
  invert = true
  kfactor = 0.5
  length = 155
  maxExtendDist = 5
  minGap = 0.2
  minReliefGap = 1
  miterangle1 = 0
  miterangle2 = 0
  offset = 0
  radius = 0.1
  reliefType = 0
  reliefd = 1
  reliefw = 0.8
  sketchflip = false
  sketchinvert = false
  unfold = false
  expr: length = <<cap_outer_base_Sketch>>.Constraints.depth
  expr: radius = BaseBend007.radius
FEATURE [Sketcher::SketchObject] Sketch082
  ExternalGeometry = -> [Sketch081]
  FullyConstrained = true
  sketch-geometry (4):
    g0: LineSegment StartX=639.126 StartY=155 StartZ=0 EndX=0 EndY=794.126 EndZ=0
    g1: LineSegment StartX=577.852 StartY=93.7258 StartZ=0 EndX=639.126 EndY=155 EndZ=0
    g2: ArcOfCircle CenterX=584.923 CenterY=86.6548 CenterZ=0 NormalX=0 NormalY=0 NormalZ=1 AngleXU=0 Radius=10 StartAngle=2.35619 EndAngle=3.14159
    g3: LineSegment StartX=574.923 StartY=86.6548 StartZ=0 EndX=574.923 EndY=0 EndZ=0
  constraints (11):
    c: PointOnObject(g0,g-2)
    c: Angle(g0) = 2.35619
    c: Coincident(g0,g-3)
    c: Coincident(g1,g0)
    c: Perpendicular(g0,g1)
    c: PointOnObject(g3,g-1)
    c: Vertical(g3)
    c: Tangent(g2,g1) = 1.5708
    c: Tangent(g3,g2) = -1.5708
    c: Equal(g3,g1)
    c: Radius(g2) = 10
FEATURE [Part::Offset2D] Offset2D
  Fill = true
  Intersection = false
  Join = 0
  Mode = 1
  SelfIntersection = false
  Source = -> Sketch082
  Value = 0.05
FEATURE [PartDesign::SubShapeBinder] Binder023
  BindCopyOnChange = 0
  BindMode = 0
  ClaimChildren = true
  Context = -> Body018 [Binder023.]
  Fuse = true
  MakeFace = true
  OffsetFill = false
  OffsetIntersection = false
  OffsetJoinType = 0
  OffsetOpenResult = false
  PartialLoad = false
  Placement = pos=(0,0,50) rot=(0,0,1;0rad)
  Relative = false
  Support = -> [Part__Mirroring019,Offset2D]
  _Version = 2
  expr: .Placement.Base.z = <<cap_outer_BaseBend>>.length
FEATURE [Part::Mirroring] Part__Mirroring019  label="Offset2D (Mirror #20)"
  Base = (0,0,0)
  Normal = (1,0,0)
  Source = -> Offset2D
FEATURE [PartDesign::Pocket] Pocket025
  BaseFeature = -> Bend005
  Direction = (0,0,1)
  Length = 0.8
  Length2 = 5
  Midplane = true
  Profile = -> Binder023
  Refine = true
  Suppressed = false
  Type = 0
FEATURE [Part::FeaturePython] CapCornerCut  # WARN: FeaturePython — macro-defined, semantics opaque (R4)
  CompositBendRadius = 0.1
  CompositThickness = 0.3
  Offset = 0.1
  Source = -> Sketch081
FEATURE [PartDesign::SubShapeBinder] Binder024
  BindCopyOnChange = 0
  BindMode = 0
  ClaimChildren = true
  Context = -> Body018 [Binder024.]
  Fuse = false
  MakeFace = true
  OffsetFill = false
  OffsetIntersection = false
  OffsetJoinType = 0
  OffsetOpenResult = false
  PartialLoad = false
  Placement = pos=(0,0,50) rot=(0,0,1;0rad)
  Relative = true
  Support = -> [CapCornerCut]
  _Version = 2
  expr: Placement = <<Binder023>>.Placement
FEATURE [PartDesign::Pocket] Pocket026
  BaseFeature = -> Pocket025
  Direction = (0,0,1)
  Length = 0.8
  Length2 = 5
  Midplane = true
  Profile = -> Binder024
  Suppressed = false
  Type = 0
  expr: Length = <<Pocket025>>.Length
FEATURE [Sketcher::SketchObject] Sketch083
  ExternalGeometry = -> [Sketch082]
  FullyConstrained = true
  sketch-geometry (17):
    g0: Circle CenterX=589.923 CenterY=20 CenterZ=0 NormalX=0 NormalY=0 NormalZ=1 AngleXU=0 Radius=1.7
    g1: Circle CenterX=559.923 CenterY=20 CenterZ=0 NormalX=0 NormalY=0 NormalZ=1 AngleXU=0 Radius=1.7
    g2: Circle CenterX=589.923 CenterY=84.5837 CenterZ=0 NormalX=0 NormalY=0 NormalZ=1 AngleXU=0 Radius=1.7
    g3: Circle CenterX=624.126 CenterY=118.787 CenterZ=0 NormalX=0 NormalY=0 NormalZ=1 AngleXU=0 Radius=1.7
    g4: Circle CenterX=602.913 CenterY=140 CenterZ=0 NormalX=0 NormalY=0 NormalZ=1 AngleXU=0 Radius=1.7
    g5: Circle CenterX=559.923 CenterY=97.0101 CenterZ=0 NormalX=0 NormalY=0 NormalZ=1 AngleXU=0 Radius=1.7
    g6: LineSegment StartX=574.923 StartY=86.6548 StartZ=0 EndX=574.923 EndY=90.7969 EndZ=0
    g7: LineSegment StartX=574.923 StartY=90.7969 StartZ=0 EndX=577.852 EndY=93.7258 EndZ=0
    g8: LineSegment StartX=559.923 StartY=20 StartZ=0 EndX=589.923 EndY=20 EndZ=0
    g9: LineSegment StartX=589.923 StartY=20 StartZ=0 EndX=589.923 EndY=84.5837 EndZ=0
    g10: LineSegment StartX=589.923 StartY=84.5837 StartZ=0 EndX=624.126 EndY=118.787 EndZ=0
    g11: LineSegment StartX=624.126 StartY=118.787 StartZ=0 EndX=602.913 EndY=140 EndZ=0
    g12: LineSegment StartX=602.913 StartY=140 StartZ=0 EndX=559.923 EndY=97.0101 EndZ=0
    g13: LineSegment StartX=559.923 StartY=97.0101 StartZ=0 EndX=559.923 EndY=20 EndZ=0
    g14: LineSegment StartX=574.923 StartY=90.7969 StartZ=0 EndX=589.923 EndY=84.5837 EndZ=0
    g15: LineSegment StartX=574.923 StartY=86.6548 StartZ=0 EndX=576.387 EndY=90.1903 EndZ=0
    g16: LineSegment StartX=576.387 StartY=90.1903 StartZ=0 EndX=577.852 EndY=93.7258 EndZ=0
  constraints (41):
    c: Coincident(g-3,g6)
    c: Vertical(g6)
    c: Coincident(g6,g7)
    c: Coincident(g7,g-4)
    c: Parallel(g7,g-4)
    c: Coincident(g8,g1)
    c: Coincident(g8,g0)
    c: Coincident(g8,g9)
    c: Coincident(g9,g2)
    c: Coincident(g9,g10)
    c: Coincident(g10,g3)
    c: Coincident(g10,g11)
    c: Coincident(g11,g4)
    c: Coincident(g11,g12)
    c: Coincident(g12,g5)
    c: Coincident(g12,g13)
    c: Coincident(g13,g8)
    c: Parallel(g9,g-3)
    c: Parallel(g-3,g13)
    c: Symmetric(g2,g5,g6)
    c: Perpendicular(g-4,g11)
    c: Perpendicular(g-3,g8)
    c: Coincident(g14,g6)
    c: Coincident(g14,g2)
    c: Coincident(g6,g15)
    c: Coincident(g15,g16)
    c: Coincident(g16,g7)
    c: PointOnObject(g15,g14)
    c: Equal(g15,g16)
    c: Parallel(g16,g15)
    c: DistanceX(g8,g8) = 30
    c: DistanceY(g0) = 20
    c: Parallel(g10,g-4)
    c: Parallel(g-4,g12)
    c: Equal(g0,g1)
    c: Equal(g1,g2)
    c: Equal(g2,g5)
    c: Equal(g5,g3)
    c: Equal(g3,g4)
    c: Diameter(g0) = 3.4
    c: DistanceX(g3,g-4) = 15
FEATURE [Part::Extrusion] Extrude017
  Base = -> Sketch083
  Dir = (0,0,1)
  DirMode = 2
  FaceMakerClass = Part::FaceMakerBullseye
  LengthFwd = 120
  LengthRev = 0
  Solid = true
  Symmetric = false
FEATURE [Part::Mirroring] Part__Mirroring020  label="Extrude017 (Mirror #21)"
  Base = (0,0,0)
  Normal = (1,0,0)
  Source = -> Extrude017
FEATURE [Sketcher::SketchObject] Sketch084  label="cap_inner_sketch"
  ExternalGeometry = -> [Sketch083,Sketch081]
  FullyConstrained = true
  sketch-geometry (11):
    g0: LineSegment StartX=606.427 StartY=152 StartZ=0 EndX=553.923 EndY=99.4954 EndZ=0
    g1: LineSegment StartX=553.923 StartY=99.4954 StartZ=0 EndX=553.923 EndY=0 EndZ=0
    g2: LineSegment StartX=553.923 StartY=0 StartZ=0 EndX=636.126 EndY=0 EndZ=0
    g3: LineSegment StartX=636.126 StartY=0 StartZ=0 EndX=636.126 EndY=152 EndZ=0
    g4: LineSegment StartX=636.126 StartY=152 StartZ=0 EndX=606.427 EndY=152 EndZ=0
    g5: LineSegment StartX=639.126 StartY=152 StartZ=0 EndX=636.126 EndY=152 EndZ=0
    g6: LineSegment StartX=636.126 StartY=152 StartZ=0 EndX=636.126 EndY=155 EndZ=0
    g7: LineSegment StartX=553.923 StartY=97.0101 StartZ=0 EndX=559.923 EndY=97.0101 EndZ=0
    g8: LineSegment StartX=559.923 StartY=97.0101 StartZ=0 EndX=555.68 EndY=101.253 EndZ=0
    g9: LineSegment StartX=602.913 StartY=140 StartZ=0 EndX=598.67 EndY=144.243 EndZ=0
    g10: LineSegment StartX=559.923 StartY=20 StartZ=0 EndX=553.923 EndY=20 EndZ=0
  constraints (34):
    c: Coincident(g0,g1)
    c: Coincident(g1,g2)
    c: Horizontal(g2)
    c: Coincident(g2,g3)
    c: Vertical(g3)
    c: Coincident(g3,g4)
    c: Coincident(g4,g0)
    c: Horizontal(g4)
    c: Horizontal(g2,g-6)
    c: DistanceX(g2,g-6) = 3
    c: PointOnObject(g5,g-6)
    c: Coincident(g5,g3)
    c: Horizontal(g5)
    c: Coincident(g5,g6)
    c: Vertical(g6)
    c: Horizontal(g6,g-6)
    c: PointOnObject(g7,g1)
    c: Coincident(g7,g-5)
    c: Coincident(g7,g8)
    c: PointOnObject(g8,g0)
    c: Horizontal(g7)
    c: Equal(g7,g8)
    c: Perpendicular(g0,g8)
    c: Coincident(g9,g-3)
    c: PointOnObject(g9,g0)
    c: Perpendicular(g0,g9)
    c: Equal(g9,g8)
    c: Coincident(g10,g-4)
    c: PointOnObject(g10,g1)
    c: Horizontal(g10)
    c: Equal(g10,g7)
    c: DistanceX(g10,g10) = 6
    c: DistanceX(g2) = 636.126  'side'
    c: Equal(g5,g6)
FEATURE [PartDesign::SubShapeBinder] Binder025
  BindCopyOnChange = 0
  BindMode = 0
  ClaimChildren = true
  Context = -> Body019 [Binder025.]
  Fuse = false
  MakeFace = true
  OffsetFill = false
  OffsetIntersection = false
  OffsetJoinType = 0
  OffsetOpenResult = false
  PartialLoad = false
  Relative = false
  Support = -> [Sketch084]
  _Version = 2
FEATURE [PartDesign::FeaturePython] BaseBend008  label="cap_inner_BaseBend"  # WARN: FeaturePython — macro-defined, semantics opaque (R4)
  BendSide = 0
  BendSketch = -> Binder025
  MidPlane = false
  Placement = pos=(0,0,46.7) rot=(0,0,1;0rad)
  Reverse = false
  Suppressed = false
  length = 100
  radius = 0.1
  thickness = 0.3
  expr: .Placement.Base.z = <<cap_outer_BaseBend>>.length - 3.3 mm
FEATURE [PartDesign::FeaturePython] Bend006  # WARN: FeaturePython — macro-defined, semantics opaque (R4)
  AutoMiter = true
  BaseFeature = -> BaseBend008
  BendType = 1
  LengthList = [47]
  LengthSpec = 1
  ReliefFactor = 0.7
  Suppressed = false
  UseReliefFactor = false
  angle = 90
  baseObject = -> BaseBend008 [Edge13]
  bendAList = [90]
  extend1 = 0
  extend2 = 0
  gap1 = 0
  gap2 = 0
  invert = true
  kfactor = 0.5
  length = 47
  maxExtendDist = 5
  minGap = 0.2
  minReliefGap = 1
  miterangle1 = 0
  miterangle2 = 0
  offset = 0
  radius = 0.1
  reliefType = 0
  reliefd = 1
  reliefw = 0.8
  sketchflip = false
  sketchinvert = false
  unfold = false
  expr: length = <<cap_outer_BaseBend>>.length - 3 mm
  expr: radius = BaseBend008.radius
FEATURE [PartDesign::SubShapeBinder] Binder026
  BindCopyOnChange = 0
  BindMode = 0
  ClaimChildren = false
  Context = -> Body019 [Binder026.]
  Fuse = false
  MakeFace = true
  OffsetFill = false
  OffsetIntersection = false
  OffsetJoinType = 0
  OffsetOpenResult = false
  PartialLoad = false
  Relative = true
  Support = -> [Sketch027[Edge3]]
  _Version = 2
FEATURE [Sketcher::SketchObject] Sketch085
  AttachmentOffset = pos=(0,0,636.126) rot=(0,0,1;0rad)
  ExternalGeometry = -> [Binder026]
  FullyConstrained = true
  MapMode = 5
  Placement = pos=(636.126,0,0) rot=(0.57735,0.57735,0.57735;2.0944rad)
  expr: .AttachmentOffset.Base.z = <<cap_inner_sketch>>.Constraints.side
  sketch-geometry (8):
    g0: LineSegment StartX=72.8253 StartY=0 StartZ=0 EndX=72.8253 EndY=-2 EndZ=0
    g1: LineSegment StartX=72.8253 StartY=-2 StartZ=0 EndX=70.3253 EndY=-4.5 EndZ=0
    g2: LineSegment StartX=70.3253 StartY=-4.5 StartZ=0 EndX=61.3253 EndY=-4.5 EndZ=0
    g3: LineSegment StartX=61.3253 StartY=-4.5 StartZ=0 EndX=58.8253 EndY=-2 EndZ=0
    g4: LineSegment StartX=58.8253 StartY=-2 StartZ=0 EndX=58.8253 EndY=0 EndZ=0
    g5: LineSegment StartX=72.8253 StartY=0 StartZ=0 EndX=58.8253 EndY=0 EndZ=0
    g6: LineSegment StartX=75.8253 StartY=0 StartZ=0 EndX=72.8253 EndY=0 EndZ=0
    g7: LineSegment StartX=58.8253 StartY=0 StartZ=0 EndX=55.8253 EndY=0 EndZ=0
  constraints (22):
    c: Vertical(g0)
    c: Coincident(g0,g1)
    c: Coincident(g1,g2)
    c: Horizontal(g2)
    c: Coincident(g2,g3)
    c: Coincident(g3,g4)
    c: Vertical(g4)
    c: Equal(g4,g0)
    c: Equal(g1,g3)
    c: DistanceY(g2,g4) = 4.5
    c: DistanceY(g4,g4) = 2
    c: Coincident(g0,g5)
    c: Coincident(g5,g4)
    c: PointOnObject(g4,g-3)
    c: PointOnObject(g0,g-3)
    c: Coincident(g6,g-3)
    c: Coincident(g6,g0)
    c: Coincident(g7,g4)
    c: Coincident(g7,g-3)
    c: Equal(g7,g6)
    c: DistanceX(g7,g4) = 3
    c: Angle(g3) = 2.35619
FEATURE [Sketcher::SketchObject] Sketch086
  FullyConstrained = false
  Placement = pos=(0,0,0) rot=(0.57735,0.57735,0.57735;2.0944rad)
  sketch-geometry (1):
    g0: Circle CenterX=68.276 CenterY=15 CenterZ=0 NormalX=0 NormalY=0 NormalZ=1 AngleXU=0 Radius=1.7
  constraints (1):
    c: Diameter(g0) = 3.4
FEATURE [Part::Extrusion] Extrude018
  Base = -> Sketch086
  Dir = (1,0,0)
  DirMode = 2
  FaceMakerClass = Part::FaceMakerBullseye
  LengthFwd = 10
  LengthRev = 0
  Placement = pos=(639.126,0,0) rot=(0,0,1;0rad)
  Reversed = true
  Solid = true
  Symmetric = false
  expr: .Placement.Base.x = <<cap_outer_base_Sketch>>.Constraints.length / 2
FEATURE [Part::Compound] Compound024
  Links = -> [Extrude017,Extrude018]
FEATURE [PartDesign::CoordinateSystem] Local_CS030  label="cap_outer_LCS"
  AttacherType = Attacher::AttachEngine3D
  MapMode = 5
FEATURE [PartDesign::CoordinateSystem] Local_CS031  label="cap_inner_LCS"
  AttacherType = Attacher::AttachEngine3D
  MapMode = 5
FEATURE [PartDesign::CoordinateSystem] Local_CS032  label="face_top_LCS"
  AttacherType = Attacher::AttachEngine3D
  AttachmentOffset = pos=(0,0,1100) rot=(0,0,1;0rad)
  MapMode = 5
  Placement = pos=(0,0,1100) rot=(0,0,1;0rad)
  expr: .AttachmentOffset.Base.z = <<Properties>>.modules_fix_height
FEATURE [Part::Mirroring] Part__Mirroring021  label="Extrude018 (Mirror #22)"
  Base = (0,0,0)
  Normal = (1,0,0)
  Source = -> Extrude018
FEATURE [Part::Compound] Compound023
  Links = -> [Part__Mirroring020,Extrude017,Extrude018,Part__Mirroring021]
FEATURE [PartDesign::Boolean] Boolean017
  BaseFeature = -> Pocket026
  Group = -> [Compound023]
  Suppressed = false
  Type = 1
  UsePlacement = true
FEATURE [PartDesign::Body] Body018  label="cap_outer"
  Group = -> [Binder022,BaseBend007,Bend005,Binder023,Pocket025,Binder024,Pocket026,Boolean017,Local_CS030]
  Origin = -> Origin020
  Tip = -> Boolean017
FEATURE [PartDesign::Pocket] Pocket027
  BaseFeature = -> BaseBend005
  Direction = (-0.642788,-0.766044,-2e-16)
  Length = 5
  Length2 = 5
  Midplane = true
  Profile = -> Sketch069
  ReferenceAxis = -> Sketch069 [N_Axis]
  Suppressed = false
  Type = 0
FEATURE [PartDesign::Pocket] Pocket021
  BaseFeature = -> Pocket027
  Direction = (0.5,0.866025,0)
  Length = 5
  Length2 = 5
  Midplane = true
  Profile = -> Sketch070
  ReferenceAxis = -> Sketch070 [N_Axis]
  Suppressed = false
  Type = 0
FEATURE [PartDesign::Mirrored] Mirrored007
  BaseFeature = -> Pocket021
  MirrorPlane = -> DatumPlane003
  Originals = -> [Pocket027,Pocket021]
  Suppressed = false
FEATURE [Part::Cylinder] Cylinder001  label="wire_hole"
  Angle = 360
  AttacherType = Attacher::AttachEngine3D
  FirstAngle = 0
  Height = 10
  Radius = 4
  SecondAngle = 0
FEATURE [Part::FeaturePython] Placment016  # WARN: FeaturePython — macro-defined, semantics opaque (R4)
  AttacherType = Attacher::AttachEngine3D
  ExposePlacement = true
  MarkerShape = 1
  MarkerSize = 10
  NumElements = 1
  Placement = pos=(10,6,0) rot=(0,0,1;0rad)
  Type = lattice2AttachablePlacement.AttachablePlacement
  isLattice = 1
FEATURE [Part::FeaturePython] Placment017  # WARN: FeaturePython — macro-defined, semantics opaque (R4)
  AttacherType = Attacher::AttachEngine3D
  ExposePlacement = true
  MarkerShape = 1
  MarkerSize = 10
  NumElements = 1
  Placement = pos=(890,6,0) rot=(0,0,1;0rad)
  Type = lattice2AttachablePlacement.AttachablePlacement
  isLattice = 1
  expr: .Placement.Base.x = 900 mm - <<Placment016>>.Placement.Base.x
  expr: .Placement.Base.y = <<Placment016>>.Placement.Base.y
FEATURE [Part::FeaturePython] Join010  # WARN: FeaturePython — macro-defined, semantics opaque (R4)
  ExposePlacement = false
  Interleave = false
  Links = -> [Placment016,Placment017]
  MarkerShape = 1
  MarkerSize = 0
  NumElements = 2
  Type = lattice2JoinArrays.JoinArrays
  isLattice = 1
FEATURE [Part::FeaturePython] Populate040  label="Populate Placment011 with Join010"  # WARN: FeaturePython — macro-defined, semantics opaque (R4)
  Copying = 0
  ExposePlacement = false
  MarkerShape = 1
  MarkerSize = 0
  NumElements = 2
  Object = -> Join010
  OutputCompounding = 0
  PlacementsTo = -> Placment011
  Referencing = 0
  Type = lattice2PopulateCopies.LatticePopulateCopies
  isLattice = 1
FEATURE [Part::FeaturePython] Populate041  label="Populate Populate Placment011 with Join010 with wire_hole"  # WARN: FeaturePython — macro-defined, semantics opaque (R4)
  Copying = 0
  ExposePlacement = false
  MarkerShape = 1
  MarkerSize = 0
  NumElements = 0
  Object = -> Cylinder001
  OutputCompounding = 1
  PlacementsTo = -> Populate040
  Referencing = 0
  Type = lattice2PopulateCopies.LatticePopulateCopies
  isLattice = 0
FEATURE [Part::FeaturePython] Mirror005  label="Mirror005 of Populate Placment011 with Join010"  # WARN: FeaturePython — macro-defined, semantics opaque (R4)
  ExposePlacement = false
  FlipX = true
  FlipY = false
  FlipZ = false
  MarkerShape = 1
  MarkerSize = 0
  NumElements = 2
  Object = -> Populate040
  ObjectTraversal = 0
  Type = lattice2Mirror.LatticeMirror
  isLattice = 1
FEATURE [Part::FeaturePython] Populate042  label="Populate Mirror005 of Populate Placment011 with Join010 with wire_hole"  # WARN: FeaturePython — macro-defined, semantics opaque (R4)
  Copying = 0
  ExposePlacement = false
  MarkerShape = 1
  MarkerSize = 0
  NumElements = 0
  Object = -> Cylinder001
  OutputCompounding = 1
  PlacementsTo = -> Mirror005
  Referencing = 0
  Type = lattice2PopulateCopies.LatticePopulateCopies
  isLattice = 0
FEATURE [Part::FeaturePython] Populate043  label="Populate Placment011 with Placment017"  # WARN: FeaturePython — macro-defined, semantics opaque (R4)
  Copying = 0
  ExposePlacement = false
  MarkerShape = 1
  MarkerSize = 50
  NumElements = 1
  Object = -> Placment017
  OutputCompounding = 0
  PlacementsTo = -> Placment011
  Referencing = 0
  Type = lattice2PopulateCopies.LatticePopulateCopies
  isLattice = 1
FEATURE [Part::FeaturePython] Mirror006  label="Mirror006 of Populate Placment011 with Placment017"  # WARN: FeaturePython — macro-defined, semantics opaque (R4)
  ExposePlacement = false
  FlipX = true
  FlipY = false
  FlipZ = false
  MarkerShape = 1
  MarkerSize = 50
  NumElements = 1
  Object = -> Populate043
  ObjectTraversal = 0
  Type = lattice2Mirror.LatticeMirror
  isLattice = 1
FEATURE [Part::FeaturePython] Join011  # WARN: FeaturePython — macro-defined, semantics opaque (R4)
  ExposePlacement = false
  Interleave = false
  Links = -> [Mirror006,Populate043]
  MarkerShape = 1
  MarkerSize = 0
  NumElements = 2
  Type = lattice2JoinArrays.JoinArrays
  isLattice = 1
FEATURE [Part::FeaturePython] Populate044  label="Populate Join008 with Join011"  # WARN: FeaturePython — macro-defined, semantics opaque (R4)
  Copying = 0
  ExposePlacement = false
  MarkerShape = 1
  MarkerSize = 0
  NumElements = 4
  Object = -> Join011
  OutputCompounding = 0
  PlacementsTo = -> Join008
  Referencing = 0
  Type = lattice2PopulateCopies.LatticePopulateCopies
  isLattice = 1
FEATURE [Part::FeaturePython] Populate045  label="Populate Populate Join008 with Join011 with wire_hole"  # WARN: FeaturePython — macro-defined, semantics opaque (R4)
  Copying = 0
  ExposePlacement = false
  MarkerShape = 1
  MarkerSize = 0
  NumElements = 0
  Object = -> Cylinder001
  OutputCompounding = 1
  PlacementsTo = -> Populate044
  Referencing = 0
  Type = lattice2PopulateCopies.LatticePopulateCopies
  isLattice = 0
FEATURE [Sketcher::SketchObject] Sketch087
  ExternalGeometry = -> [Binder020]
  FullyConstrained = true
  sketch-geometry (18):
    g0: ArcOfCircle CenterX=4.15 CenterY=-445.4 CenterZ=0 NormalX=0 NormalY=0 NormalZ=1 AngleXU=0 Radius=1.6 StartAngle=3.14159 EndAngle=6.28319
    g1: ArcOfCircle CenterX=4.15 CenterY=-444.6 CenterZ=0 NormalX=0 NormalY=0 NormalZ=1 AngleXU=0 Radius=1.6 StartAngle=1.13e-14 EndAngle=3.14159
    g2: LineSegment StartX=2.55 StartY=-445.4 StartZ=0 EndX=2.55 EndY=-444.6 EndZ=0
    g3: LineSegment StartX=5.75 StartY=-445.4 StartZ=0 EndX=5.75 EndY=-444.6 EndZ=0
    g4: LineSegment StartX=4.15 StartY=-447 StartZ=0 EndX=4.15 EndY=-443 EndZ=0
    g5: ArcOfCircle CenterX=-4.15 CenterY=444.6 CenterZ=0 NormalX=0 NormalY=0 NormalZ=1 AngleXU=0 Radius=1.6 StartAngle=3.14159 EndAngle=6.28319
    g6: ArcOfCircle CenterX=-4.15 CenterY=445.4 CenterZ=0 NormalX=0 NormalY=0 NormalZ=1 AngleXU=0 Radius=1.6 StartAngle=1.01e-14 EndAngle=3.14159
    g7: LineSegment StartX=-5.75 StartY=444.6 StartZ=0 EndX=-5.75 EndY=445.4 EndZ=0
    g8: LineSegment StartX=-2.55 StartY=444.6 StartZ=0 EndX=-2.55 EndY=445.4 EndZ=0
    g9: LineSegment StartX=-4.15 StartY=443 StartZ=0 EndX=-4.15 EndY=447 EndZ=0
    g10: ArcOfCircle CenterX=-4.15 CenterY=-445.4 CenterZ=0 NormalX=0 NormalY=0 NormalZ=1 AngleXU=0 Radius=1.6 StartAngle=3.14159 EndAngle=6.28319
    g11: ArcOfCircle CenterX=-4.15 CenterY=-444.6 CenterZ=0 NormalX=0 NormalY=0 NormalZ=1 AngleXU=0 Radius=1.6 StartAngle=-7.1e-15 EndAngle=3.14159
    g12: LineSegment StartX=-5.75 StartY=-445.4 StartZ=0 EndX=-5.75 EndY=-444.6 EndZ=0
    g13: LineSegment StartX=-2.55 StartY=-445.4 StartZ=0 EndX=-2.55 EndY=-444.6 EndZ=0
    g14: ArcOfCircle CenterX=4.15 CenterY=444.6 CenterZ=0 NormalX=0 NormalY=0 NormalZ=1 AngleXU=0 Radius=1.6 StartAngle=3.14159 EndAngle=6.28319
    g15: ArcOfCircle CenterX=4.15 CenterY=445.4 CenterZ=0 NormalX=0 NormalY=0 NormalZ=1 AngleXU=0 Radius=1.6 StartAngle=-1.51e-14 EndAngle=3.14159
    g16: LineSegment StartX=2.55 StartY=444.6 StartZ=0 EndX=2.55 EndY=445.4 EndZ=0
    g17: LineSegment StartX=5.75 StartY=444.6 StartZ=0 EndX=5.75 EndY=445.4 EndZ=0
  constraints (44):
    c: Tangent(g0,g2) = 1.5708
    c: Tangent(g0,g3) = -1.5708
    c: Tangent(g1,g2) = 1.5708
    c: Tangent(g1,g3) = -1.5708
    c: Equal(g0,g1)
    c: Symmetric(g0,g1,g-4)
    c: Vertical(g2)
    c: Equal(g1,g-4)
    c: PointOnObject(g4,g0)
    c: PointOnObject(g4,g1)
    c: Vertical(g4)
    c: PointOnObject(g-4,g4)
    c: DistanceY(g4,g4) = 4
    c: Tangent(g5,g7) = 1.5708
    c: Tangent(g5,g8) = -1.5708
    c: Tangent(g6,g7) = 1.5708
    c: Tangent(g6,g8) = -1.5708
    c: Equal(g5,g6)
    c: Vertical(g7)
    c: Equal(g6,g-3)
    c: PointOnObject(g9,g5)
    c: PointOnObject(g9,g6)
    c: Vertical(g9)
    c: PointOnObject(g-3,g9)
    c: Symmetric(g5,g6,g-3)
    c: Equal(g9,g4)
    c: Tangent(g10,g12) = 1.5708
    c: Tangent(g10,g13) = -1.5708
    c: Tangent(g11,g12) = 1.5708
    c: Tangent(g11,g13) = -1.5708
    c: Equal(g10,g11)
    c: Tangent(g14,g16) = 1.5708
    c: Tangent(g14,g17) = -1.5708
    c: Tangent(g15,g16) = 1.5708
    c: Tangent(g15,g17) = -1.5708
    c: Equal(g14,g15)
    c: Vertical(g16)
    c: Equal(g15,g6)
    c: Equal(g16,g8)
    c: Symmetric(g15,g6,g-2)
    c: Vertical(g13)
    c: Equal(g1,g11)
    c: Equal(g13,g2)
    c: Symmetric(g11,g1,g-2)
FEATURE [Part::Extrusion] Extrude011
  Base = -> Sketch087
  Dir = (0,0,1)
  DirMode = 2
  FaceMakerClass = Part::FaceMakerBullseye
  LengthFwd = 10
  LengthRev = 0
  Solid = true
  Symmetric = true
FEATURE [Part::FeaturePython] Populate027  label="Populate Placment010 with Extrude011"  # WARN: FeaturePython — macro-defined, semantics opaque (R4)
  Copying = 0
  ExposePlacement = false
  MarkerShape = 1
  MarkerSize = 0
  NumElements = 0
  Object = -> Extrude011
  OutputCompounding = 2
  PlacementsTo = -> Placment010
  Referencing = 0
  Type = lattice2PopulateCopies.LatticePopulateCopies
  isLattice = 0
FEATURE [Part::FeaturePython] Populate033  label="Populate Mirror004 of Placment010 with Extrude011"  # WARN: FeaturePython — macro-defined, semantics opaque (R4)
  Copying = 0
  ExposePlacement = false
  MarkerShape = 1
  MarkerSize = 0
  NumElements = 0
  Object = -> Extrude011
  OutputCompounding = 1
  PlacementsTo = -> Mirror004
  Referencing = 0
  Type = lattice2PopulateCopies.LatticePopulateCopies
  isLattice = 0
FEATURE [Part::Extrusion] Extrude019
  Base = -> Sketch028
  Dir = (0,0,1)
  DirMode = 2
  FaceMakerClass = Part::FaceMakerBullseye
  LengthFwd = 0.4
  LengthRev = 0
  Solid = true
  Symmetric = false
FEATURE [Part::Mirroring] Part__Mirroring007  label="Sketch028 (Mirror #8)"
  Base = (0,0,0)
  Normal = (1,0,0)
  Source = -> Extrude019
FEATURE [Part::Extrusion] Extrude020
  Base = -> Sketch030
  Dir = (0,0,1)
  DirMode = 2
  FaceMakerClass = Part::FaceMakerBullseye
  LengthFwd = 0.4
  LengthRev = 0
  Solid = true
  Symmetric = false
FEATURE [Part::FeaturePython] Populate038  label="Populate Populate Join008 with Join009 with Extrude013"  # WARN: FeaturePython — macro-defined, semantics opaque (R4)
  Copying = 0
  ExposePlacement = false
  MarkerShape = 1
  MarkerSize = 0
  NumElements = 0
  Object = -> Extrude013
  OutputCompounding = 1
  PlacementsTo = -> Populate034
  Referencing = 0
  Type = lattice2PopulateCopies.LatticePopulateCopies
  isLattice = 0
FEATURE [Part::MultiFuse] Fusion004
  Placement = pos=(319.563,0,0) rot=(0,0,1;0rad)
  Refine = true
  Shapes = -> [Part__Mirroring007,Extrude019,Extrude020]
  expr: .Placement.Base.x = <<mid_Sketch>>.Constraints.middle
FEATURE [Part::Mirroring] Part__Mirroring008  label="Compound006 (Mirror #9)"
  Base = (0,0,0)
  Normal = (1,0,0)
  Source = -> Fusion004
FEATURE [Part::MultiFuse] Fusion003
  Placement = pos=(0,0,1100) rot=(0,0,1;0rad)
  Refine = true
  Shapes = -> [Part__Mirroring008,Fusion004]
  expr: .Placement.Base.z = <<Properties>>.modules_fix_height
FEATURE [Part::Compound] Compound007
  Links = -> [Fusion003]
FEATURE [Part::Feature] Unfold007
  shape: bbox 26.6 x 88.07 x 0.7 mm, 17 faces (baked)
FEATURE [Sketcher::SketchObject] Unfold_Sketch_Outline006
  FullyConstrained = false
  sketch-geometry (8):
    g0: LineSegment StartX=-13.3 StartY=-33.0715 StartZ=0 EndX=-13.3 EndY=45 EndZ=0
    g1: ArcOfCircle CenterX=-8.3 CenterY=45 CenterZ=0 NormalX=0 NormalY=0 NormalZ=1 AngleXU=3.14159 Radius=5 StartAngle=4.71239 EndAngle=6.28319
    g2: LineSegment StartX=-8.3 StartY=50 StartZ=0 EndX=8.3 EndY=50 EndZ=0
    g3: ArcOfCircle CenterX=8.3 CenterY=45 CenterZ=0 NormalX=0 NormalY=0 NormalZ=1 AngleXU=0 Radius=5 StartAngle=0 EndAngle=1.5708
    g4: LineSegment StartX=13.3 StartY=-33.0715 StartZ=0 EndX=13.3 EndY=45 EndZ=0
    g5: ArcOfCircle CenterX=8.3 CenterY=-33.0715 CenterZ=0 NormalX=0 NormalY=0 NormalZ=1 AngleXU=0 Radius=5 StartAngle=4.71239 EndAngle=6.28319
    g6: LineSegment StartX=-8.3 StartY=-38.0715 StartZ=0 EndX=8.3 EndY=-38.0715 EndZ=0
    g7: ArcOfCircle CenterX=-8.3 CenterY=-33.0715 CenterZ=0 NormalX=0 NormalY=0 NormalZ=1 AngleXU=3.14159 Radius=5 StartAngle=-2.7e-15 EndAngle=1.5708
FEATURE [Sketcher::SketchObject] Unfold_Sketch_Internal006
  FullyConstrained = false
  sketch-geometry (7):
    g0: Circle CenterX=8e-15 CenterY=45 CenterZ=0 NormalX=0 NormalY=0 NormalZ=-1 AngleXU=-3.14159 Radius=1.7
    g1: Circle CenterX=-9.8 CenterY=-32.0715 CenterZ=0 NormalX=0 NormalY=0 NormalZ=1 AngleXU=0 Radius=1.7
    g2: Circle CenterX=9.8 CenterY=-32.0715 CenterZ=0 NormalX=0 NormalY=0 NormalZ=1 AngleXU=0 Radius=1.7
    g3: Circle CenterX=-9.8 CenterY=-10.0715 CenterZ=0 NormalX=0 NormalY=0 NormalZ=1 AngleXU=0 Radius=1.7
    g4: Circle CenterX=9.8 CenterY=-10.0715 CenterZ=0 NormalX=0 NormalY=0 NormalZ=1 AngleXU=0 Radius=1.7
    g5: Circle CenterX=-10 CenterY=15 CenterZ=0 NormalX=0 NormalY=0 NormalZ=-1 AngleXU=-3.14159 Radius=1.7
    g6: Circle CenterX=10 CenterY=15 CenterZ=0 NormalX=0 NormalY=0 NormalZ=-1 AngleXU=-3.14159 Radius=1.7
FEATURE [Sketcher::SketchObject] Unfold_Sketch_bends007
  FullyConstrained = false
  sketch-geometry (1):
    g0: LineSegment StartX=13.3 StartY=0.96427 StartZ=0 EndX=-13.3 EndY=0.96427 EndZ=0
FEATURE [Sketcher::SketchObject] Unfold_Sketch007
  ExternalGeometry = -> [Unfold_Sketch_bends007]
  FullyConstrained = false
  sketch-geometry (17):
    g0: LineSegment StartX=-13.3 StartY=-33.0715 StartZ=0 EndX=-13.3 EndY=45 EndZ=0
    g1: ArcOfCircle CenterX=-8.3 CenterY=-33.0715 CenterZ=0 NormalX=0 NormalY=0 NormalZ=1 AngleXU=3.14159 Radius=5 StartAngle=-2.7e-15 EndAngle=1.5708
    g2: LineSegment StartX=-8.3 StartY=-38.0715 StartZ=0 EndX=8.3 EndY=-38.0715 EndZ=0
    g3: ArcOfCircle CenterX=8.3 CenterY=-33.0715 CenterZ=0 NormalX=0 NormalY=0 NormalZ=1 AngleXU=0 Radius=5 StartAngle=4.71239 EndAngle=6.28319
    g4: LineSegment StartX=13.3 StartY=-33.0715 StartZ=0 EndX=13.3 EndY=45 EndZ=0
    g5: ArcOfCircle CenterX=8.3 CenterY=45 CenterZ=0 NormalX=0 NormalY=0 NormalZ=1 AngleXU=0 Radius=5 StartAngle=0 EndAngle=1.5708
    g6: LineSegment StartX=-8.3 StartY=50 StartZ=0 EndX=8.3 EndY=50 EndZ=0
    g7: ArcOfCircle CenterX=-8.3 CenterY=45 CenterZ=0 NormalX=0 NormalY=0 NormalZ=1 AngleXU=3.14159 Radius=5 StartAngle=4.71239 EndAngle=6.28319
    g8: Circle CenterX=8e-15 CenterY=45 CenterZ=0 NormalX=0 NormalY=0 NormalZ=-1 AngleXU=-3.14159 Radius=1.7
    g9: Circle CenterX=9.8 CenterY=-32.0715 CenterZ=0 NormalX=0 NormalY=0 NormalZ=1 AngleXU=0 Radius=1.7
    g10: Circle CenterX=-9.8 CenterY=-32.0715 CenterZ=0 NormalX=0 NormalY=0 NormalZ=1 AngleXU=0 Radius=1.7
    g11: Circle CenterX=9.8 CenterY=-10.0715 CenterZ=0 NormalX=0 NormalY=0 NormalZ=1 AngleXU=0 Radius=1.7
    g12: Circle CenterX=-9.8 CenterY=-10.0715 CenterZ=0 NormalX=0 NormalY=0 NormalZ=1 AngleXU=0 Radius=1.7
    g13: Circle CenterX=10 CenterY=15 CenterZ=0 NormalX=0 NormalY=0 NormalZ=-1 AngleXU=-3.14159 Radius=1.7
    g14: Circle CenterX=-10 CenterY=15 CenterZ=0 NormalX=0 NormalY=0 NormalZ=-1 AngleXU=-3.14159 Radius=1.7
    g15: LineSegment StartX=-13.3 StartY=0.96427 StartZ=0 EndX=-11.3 EndY=0.96427 EndZ=0
    g16: LineSegment StartX=11.3 StartY=0.96427 StartZ=0 EndX=13.3 EndY=0.96427 EndZ=0
  constraints (6):
    c: Coincident(g15,g-3)
    c: PointOnObject(g15,g-3)
    c: PointOnObject(g16,g-3)
    c: Coincident(g16,g-3)
    c: Equal(g16,g15)
    c: DistanceX(g15,g15) = 2
FEATURE [TechDraw::DrawViewDimension] Dimension028
  AngleOverride = false
  Arbitrary = false
  ArbitraryTolerances = false
  EqualTolerance = true
  ExtensionAngle = 0
  FormatSpec = %.2w
  FormatSpecOverTolerance = %+.2w
  FormatSpecUnderTolerance = %+.2w
  Inverted = false
  LineAngle = 0
  LockPosition = false
  MeasureType = 1
  OverTolerance = 0
  References2D = -> [View005]
  Rotation = 0
  ScaleType = 0
  TheoreticalExact = false
  Type = 6
  UnderTolerance = 0
  X = -86.9507
  Y = -3.74233
FEATURE [TechDraw::DrawViewDimension] Dimension030
  AngleOverride = false
  Arbitrary = false
  ArbitraryTolerances = false
  EqualTolerance = true
  ExtensionAngle = 0
  FormatSpec = %.2w
  FormatSpecOverTolerance = %+.2w
  FormatSpecUnderTolerance = %+.2w
  Inverted = false
  LineAngle = 0
  LockPosition = false
  MeasureType = 1
  OverTolerance = 0
  References2D = -> [View012]
  Rotation = 0
  ScaleType = 0
  TheoreticalExact = false
  Type = 2
  UnderTolerance = 0
  X = -127.207
  Y = -0.916629
FEATURE [Part::Feature] Unfold009
  shape: bbox 81.46 x 68.51 x 900 mm, 33 faces (baked)
FEATURE [Sketcher::SketchObject] Unfold_Sketch009
  FullyConstrained = false
  sketch-geometry (31):
    g0: ArcOfCircle CenterX=-418.247 CenterY=-3 CenterZ=0 NormalX=0 NormalY=0 NormalZ=1 AngleXU=3.14159 Radius=3 StartAngle=4.71239 EndAngle=6.28319
    g1: LineSegment StartX=-421.247 StartY=-3 StartZ=0 EndX=-421.247 EndY=-897 EndZ=0
    g2: ArcOfCircle CenterX=-418.247 CenterY=-897 CenterZ=0 NormalX=0 NormalY=0 NormalZ=1 AngleXU=-3.14159 Radius=3 StartAngle=0 EndAngle=1.5708
    g3: LineSegment StartX=-318.5 StartY=-900 StartZ=0 EndX=-418.247 EndY=-900 EndZ=0
    g4: ArcOfCircle CenterX=-318.5 CenterY=-897 CenterZ=0 NormalX=0 NormalY=0 NormalZ=1 AngleXU=3.14159 Radius=3 StartAngle=1.5708 EndAngle=3.14159
    g5: LineSegment StartX=-315.5 StartY=-3 StartZ=0 EndX=-315.5 EndY=-897 EndZ=0
    g6: ArcOfCircle CenterX=-318.5 CenterY=-3 CenterZ=0 NormalX=0 NormalY=0 NormalZ=1 AngleXU=-3.14159 Radius=3 StartAngle=3.14159 EndAngle=4.71239
    g7: LineSegment StartX=-318.5 StartY=0 StartZ=0 EndX=-418.247 EndY=0 EndZ=0
    g8: Circle CenterX=-325.218 CenterY=-890 CenterZ=0 NormalX=0 NormalY=0 NormalZ=-1 AngleXU=-1.5708 Radius=4
    g9: Circle CenterX=-325.218 CenterY=-10 CenterZ=0 NormalX=0 NormalY=0 NormalZ=-1 AngleXU=-1.5708 Radius=4
    g10: LineSegment StartX=-393.221 StartY=-895.4 StartZ=0 EndX=-393.221 EndY=-894.6 EndZ=0
    g11: ArcOfCircle CenterX=-394.821 CenterY=-895.4 CenterZ=0 NormalX=0 NormalY=0 NormalZ=1 AngleXU=1e-16 Radius=1.6 StartAngle=3.14159 EndAngle=6.28319
    g12: LineSegment StartX=-396.421 StartY=-895.4 StartZ=0 EndX=-396.421 EndY=-894.6 EndZ=0
    g13: ArcOfCircle CenterX=-394.821 CenterY=-894.6 CenterZ=0 NormalX=0 NormalY=0 NormalZ=1 AngleXU=1e-16 Radius=1.6 StartAngle=0 EndAngle=3.14159
    g14: LineSegment StartX=-401.521 StartY=-895.4 StartZ=0 EndX=-401.521 EndY=-894.6 EndZ=0
    g15: ArcOfCircle CenterX=-403.121 CenterY=-895.4 CenterZ=0 NormalX=0 NormalY=0 NormalZ=1 AngleXU=1e-16 Radius=1.6 StartAngle=3.14159 EndAngle=6.28319
    g16: LineSegment StartX=-404.721 StartY=-895.4 StartZ=0 EndX=-404.721 EndY=-894.6 EndZ=0
    g17: ArcOfCircle CenterX=-403.121 CenterY=-894.6 CenterZ=0 NormalX=0 NormalY=0 NormalZ=1 AngleXU=1e-16 Radius=1.6 StartAngle=0 EndAngle=3.14159
    g18: LineSegment StartX=-393.221 StartY=-5.4 StartZ=0 EndX=-393.221 EndY=-4.6 EndZ=0
    g19: ArcOfCircle CenterX=-394.821 CenterY=-5.4 CenterZ=0 NormalX=0 NormalY=0 NormalZ=1 AngleXU=1e-16 Radius=1.6 StartAngle=3.14159 EndAngle=6.28319
    g20: LineSegment StartX=-396.421 StartY=-5.4 StartZ=0 EndX=-396.421 EndY=-4.6 EndZ=0
    g21: ArcOfCircle CenterX=-394.821 CenterY=-4.6 CenterZ=0 NormalX=0 NormalY=0 NormalZ=1 AngleXU=1e-16 Radius=1.6 StartAngle=1.44e-14 EndAngle=3.14159
    g22: LineSegment StartX=-401.521 StartY=-5.4 StartZ=0 EndX=-401.521 EndY=-4.6 EndZ=0
    g23: ArcOfCircle CenterX=-403.121 CenterY=-5.4 CenterZ=0 NormalX=0 NormalY=0 NormalZ=1 AngleXU=1e-16 Radius=1.6 StartAngle=3.14159 EndAngle=6.28319
    g24: LineSegment StartX=-404.721 StartY=-5.4 StartZ=0 EndX=-404.721 EndY=-4.6 EndZ=0
    g25: ArcOfCircle CenterX=-403.121 CenterY=-4.6 CenterZ=0 NormalX=0 NormalY=0 NormalZ=1 AngleXU=1e-16 Radius=1.6 StartAngle=7.2e-15 EndAngle=3.14159
    g26: Circle CenterX=-331.218 CenterY=-870 CenterZ=0 NormalX=0 NormalY=0 NormalZ=-1 AngleXU=-1.5708 Radius=1.7
    g27: Circle CenterX=-331.218 CenterY=-660 CenterZ=0 NormalX=0 NormalY=0 NormalZ=-1 AngleXU=-1.5708 Radius=1.7
    g28: Circle CenterX=-331.218 CenterY=-30 CenterZ=0 NormalX=0 NormalY=0 NormalZ=-1 AngleXU=-1.5708 Radius=1.7
    g29: Circle CenterX=-331.218 CenterY=-450 CenterZ=0 NormalX=0 NormalY=0 NormalZ=-1 AngleXU=-1.5708 Radius=1.7
    g30: Circle CenterX=-331.218 CenterY=-240 CenterZ=0 NormalX=0 NormalY=0 NormalZ=-1 AngleXU=-1.5708 Radius=1.7
FEATURE [Sketcher::SketchObject] Unfold_Sketch_Outline007
  FullyConstrained = false
  sketch-geometry (8):
    g0: ArcOfCircle CenterX=-418.247 CenterY=-3 CenterZ=0 NormalX=0 NormalY=0 NormalZ=1 AngleXU=3.14159 Radius=3 StartAngle=4.71239 EndAngle=6.28319
    g1: LineSegment StartX=-421.247 StartY=-3 StartZ=0 EndX=-421.247 EndY=-897 EndZ=0
    g2: ArcOfCircle CenterX=-418.247 CenterY=-897 CenterZ=0 NormalX=0 NormalY=0 NormalZ=1 AngleXU=-3.14159 Radius=3 StartAngle=0 EndAngle=1.5708
    g3: LineSegment StartX=-318.5 StartY=-900 StartZ=0 EndX=-418.247 EndY=-900 EndZ=0
    g4: ArcOfCircle CenterX=-318.5 CenterY=-897 CenterZ=0 NormalX=0 NormalY=0 NormalZ=1 AngleXU=3.14159 Radius=3 StartAngle=1.5708 EndAngle=3.14159
    g5: LineSegment StartX=-315.5 StartY=-3 StartZ=0 EndX=-315.5 EndY=-897 EndZ=0
    g6: ArcOfCircle CenterX=-318.5 CenterY=-3 CenterZ=0 NormalX=0 NormalY=0 NormalZ=1 AngleXU=-3.14159 Radius=3 StartAngle=3.14159 EndAngle=4.71239
    g7: LineSegment StartX=-318.5 StartY=0 StartZ=0 EndX=-418.247 EndY=0 EndZ=0
FEATURE [Sketcher::SketchObject] Unfold_Sketch_Internal007
  FullyConstrained = false
  sketch-geometry (23):
    g0: Circle CenterX=-325.218 CenterY=-10 CenterZ=0 NormalX=0 NormalY=0 NormalZ=-1 AngleXU=-1.5708 Radius=4
    g1: Circle CenterX=-325.218 CenterY=-890 CenterZ=0 NormalX=0 NormalY=0 NormalZ=-1 AngleXU=-1.5708 Radius=4
    g2: LineSegment StartX=-401.521 StartY=-895.4 StartZ=0 EndX=-401.521 EndY=-894.6 EndZ=0
    g3: ArcOfCircle CenterX=-403.121 CenterY=-894.6 CenterZ=0 NormalX=0 NormalY=0 NormalZ=1 AngleXU=1e-16 Radius=1.6 StartAngle=0 EndAngle=3.14159
    g4: LineSegment StartX=-404.721 StartY=-895.4 StartZ=0 EndX=-404.721 EndY=-894.6 EndZ=0
    g5: ArcOfCircle CenterX=-403.121 CenterY=-895.4 CenterZ=0 NormalX=0 NormalY=0 NormalZ=1 AngleXU=1e-16 Radius=1.6 StartAngle=3.14159 EndAngle=6.28319
    g6: LineSegment StartX=-393.221 StartY=-895.4 StartZ=0 EndX=-393.221 EndY=-894.6 EndZ=0
    g7: ArcOfCircle CenterX=-394.821 CenterY=-894.6 CenterZ=0 NormalX=0 NormalY=0 NormalZ=1 AngleXU=1e-16 Radius=1.6 StartAngle=0 EndAngle=3.14159
    g8: LineSegment StartX=-396.421 StartY=-895.4 StartZ=0 EndX=-396.421 EndY=-894.6 EndZ=0
    g9: ArcOfCircle CenterX=-394.821 CenterY=-895.4 CenterZ=0 NormalX=0 NormalY=0 NormalZ=1 AngleXU=1e-16 Radius=1.6 StartAngle=3.14159 EndAngle=6.28319
    g10: LineSegment StartX=-401.521 StartY=-5.4 StartZ=0 EndX=-401.521 EndY=-4.6 EndZ=0
    g11: ArcOfCircle CenterX=-403.121 CenterY=-4.6 CenterZ=0 NormalX=0 NormalY=0 NormalZ=1 AngleXU=1e-16 Radius=1.6 StartAngle=7.2e-15 EndAngle=3.14159
    g12: LineSegment StartX=-404.721 StartY=-5.4 StartZ=0 EndX=-404.721 EndY=-4.6 EndZ=0
    g13: ArcOfCircle CenterX=-403.121 CenterY=-5.4 CenterZ=0 NormalX=0 NormalY=0 NormalZ=1 AngleXU=1e-16 Radius=1.6 StartAngle=3.14159 EndAngle=6.28319
    g14: LineSegment StartX=-393.221 StartY=-5.4 StartZ=0 EndX=-393.221 EndY=-4.6 EndZ=0
    g15: ArcOfCircle CenterX=-394.821 CenterY=-4.6 CenterZ=0 NormalX=0 NormalY=0 NormalZ=1 AngleXU=1e-16 Radius=1.6 StartAngle=1.44e-14 EndAngle=3.14159
    g16: LineSegment StartX=-396.421 StartY=-5.4 StartZ=0 EndX=-396.421 EndY=-4.6 EndZ=0
    g17: ArcOfCircle CenterX=-394.821 CenterY=-5.4 CenterZ=0 NormalX=0 NormalY=0 NormalZ=1 AngleXU=1e-16 Radius=1.6 StartAngle=3.14159 EndAngle=6.28319
    g18: Circle CenterX=-331.218 CenterY=-660 CenterZ=0 NormalX=0 NormalY=0 NormalZ=-1 AngleXU=-1.5708 Radius=1.7
    g19: Circle CenterX=-331.218 CenterY=-870 CenterZ=0 NormalX=0 NormalY=0 NormalZ=-1 AngleXU=-1.5708 Radius=1.7
    g20: Circle CenterX=-331.218 CenterY=-30 CenterZ=0 NormalX=0 NormalY=0 NormalZ=-1 AngleXU=-1.5708 Radius=1.7
    g21: Circle CenterX=-331.218 CenterY=-240 CenterZ=0 NormalX=0 NormalY=0 NormalZ=-1 AngleXU=-1.5708 Radius=1.7
    g22: Circle CenterX=-331.218 CenterY=-450 CenterZ=0 NormalX=0 NormalY=0 NormalZ=-1 AngleXU=-1.5708 Radius=1.7
FEATURE [Sketcher::SketchObject] Unfold_Sketch_bends009
  FullyConstrained = false
  sketch-geometry (2):
    g0: LineSegment StartX=-409.836 StartY=-900 StartZ=0 EndX=-409.836 EndY=0 EndZ=0
    g1: LineSegment StartX=-340.235 StartY=-900 StartZ=0 EndX=-340.235 EndY=0 EndZ=0
FEATURE [Sketcher::SketchObject] Sketch088
  ExternalGeometry = -> [Sketch001,Sketch021,Sketch]
  FullyConstrained = false
  expr: Constraints[5] = <<side_Sketch>>.Constraints.distance - 3 mm
  sketch-geometry (3):
    g0: LineSegment StartX=184.237 StartY=20 StartZ=0 EndX=316.563 EndY=20 EndZ=0
    g1: LineSegment StartX=316.563 StartY=20 StartZ=0 EndX=316.563 EndY=131.035 EndZ=0
    g2: LineSegment StartX=316.563 StartY=131.035 StartZ=0 EndX=184.237 EndY=20 EndZ=0
  constraints (6):
    c: Horizontal(g0)
    c: Coincident(g0,g1)
    c: Vertical(g1)
    c: Coincident(g1,g2)
    c: Coincident(g2,g0)
    c: DistanceX(g0) = 316.563
FEATURE [PartDesign::SubShapeBinder] Binder027
  BindCopyOnChange = 0
  BindMode = 0
  ClaimChildren = true
  Context = -> Body020 [Binder027.]
  Fuse = false
  MakeFace = true
  OffsetFill = false
  OffsetIntersection = false
  OffsetJoinType = 0
  OffsetOpenResult = false
  PartialLoad = false
  Relative = true
  Support = -> [Sketch088]
  _Version = 2
FEATURE [PartDesign::Pad] Pad020
  Direction = (0,0,1)
  Length = 0.3
  Length2 = 10
  Profile = -> Binder027
  Suppressed = false
  Type = 0
FEATURE [Sketcher::SketchObject] Sketch089
  FullyConstrained = true
  expr: .Constraints.length = 133 mm + 55 mm + 132 mm
  expr: .Constraints.width = 72 mm + 6 mm + 15 mm
  sketch-geometry (5):
    g0: LineSegment StartX=-46.5 StartY=-160 StartZ=0 EndX=46.5 EndY=-160 EndZ=0
    g1: LineSegment StartX=46.5 StartY=-160 StartZ=0 EndX=46.5 EndY=160 EndZ=0
    g2: LineSegment StartX=46.5 StartY=160 StartZ=0 EndX=-46.5 EndY=160 EndZ=0
    g3: LineSegment StartX=-46.5 StartY=160 StartZ=0 EndX=-46.5 EndY=-160 EndZ=0
    g4: GeomPoint X=0 Y=0 Z=0
  constraints (12):
    c: Coincident(g0,g1)
    c: Coincident(g1,g2)
    c: Coincident(g2,g3)
    c: Coincident(g3,g0)
    c: Horizontal(g0)
    c: Horizontal(g2)
    c: Vertical(g1)
    c: Vertical(g3)
    c: Symmetric(g2,g0,g4)
    c: Coincident(g4,g-1)
    c: DistanceX(g2,g2) = 93  'width'
    c: DistanceY(g1,g1) = 320  'length'
FEATURE [Sketcher::SketchObject] Sketch090
  ExternalGeometry = -> [Sketch089]
  FullyConstrained = true
  sketch-geometry (5):
    g0: LineSegment StartX=-43.5 StartY=-157 StartZ=0 EndX=43.5 EndY=-157 EndZ=0
    g1: LineSegment StartX=43.5 StartY=-157 StartZ=0 EndX=43.5 EndY=157 EndZ=0
    g2: LineSegment StartX=43.5 StartY=157 StartZ=0 EndX=-43.5 EndY=157 EndZ=0
    g3: LineSegment StartX=-43.5 StartY=157 StartZ=0 EndX=-43.5 EndY=-157 EndZ=0
    g4: GeomPoint X=0 Y=0 Z=0
  constraints (14):
    c: Coincident(g0,g1)
    c: Coincident(g1,g2)
    c: Coincident(g2,g3)
    c: Coincident(g3,g0)
    c: Horizontal(g0)
    c: Horizontal(g2)
    c: Vertical(g1)
    c: Vertical(g3)
    c: Symmetric(g2,g0,g4)
    c: Coincident(g4,g-1)
    c: DistanceX(g1,g-4) = 3
    c: DistanceY(g1,g-4) = 3
    c: DistanceX(g2,g2) = 87  'width'
    c: Distance(g1) = 314  'length'
FEATURE [Part::FeaturePython] Placment018  label="shield_placement"  # WARN: FeaturePython — macro-defined, semantics opaque (R4)
  AttacherType = Attacher::AttachEngine3D
  ExposePlacement = true
  MarkerShape = 1
  MarkerSize = 20
  NumElements = 1
  Placement = pos=(-639.126,60,480) rot=(0.57735,-0.57735,-0.57735;2.0944rad)
  Type = lattice2AttachablePlacement.AttachablePlacement
  isLattice = 1
  expr: .Placement.Base.x = -<<Dimensions>>.Constraints.width / 2
FEATURE [PartDesign::SubShapeBinder] Binder028
  BindCopyOnChange = 0
  BindMode = 0
  ClaimChildren = true
  Context = -> Body021 [Binder028.]
  Fuse = false
  MakeFace = true
  OffsetFill = false
  OffsetIntersection = false
  OffsetJoinType = 0
  OffsetOpenResult = false
  PartialLoad = false
  Relative = false
  Support = -> [Sketch089]
  _Version = 2
FEATURE [PartDesign::FeaturePython] BaseBend009  # WARN: FeaturePython — macro-defined, semantics opaque (R4)
  BendSide = 0
  BendSketch = -> Binder028
  MidPlane = false
  Reverse = false
  Suppressed = false
  length = 100
  radius = 0.1
  thickness = 0.3
FEATURE [PartDesign::FeaturePython] Bend007  # WARN: FeaturePython — macro-defined, semantics opaque (R4)
  AutoMiter = false
  BaseFeature = -> BaseBend009
  BendType = 1
  LengthList = [30]
  LengthSpec = 1
  ReliefFactor = 0.7
  Suppressed = false
  UseReliefFactor = false
  angle = 90
  baseObject = -> BaseBend009 [Edge6,Edge9,Edge3,Edge11]
  bendAList = [90]
  extend1 = 0
  extend2 = 0
  gap1 = 0
  gap2 = 0
  invert = false
  kfactor = 0.5
  length = 30
  maxExtendDist = 5
  minGap = 0.2
  minReliefGap = 1
  miterangle1 = 0
  miterangle2 = 0
  offset = 0
  radius = 0.1
  reliefType = 0
  reliefd = 1
  reliefw = 0.8
  sketchflip = false
  sketchinvert = false
  unfold = false
  expr: radius = BaseBend009.radius
FEATURE [Part::Offset2D] Offset2D001
  Fill = true
  Intersection = false
  Join = 1
  Mode = 1
  SelfIntersection = false
  Source = -> Sketch090
  Value = 1
FEATURE [PartDesign::SubShapeBinder] Binder029
  BindCopyOnChange = 0
  BindMode = 0
  ClaimChildren = true
  Context = -> Body022 [Binder029.]
  Fuse = false
  MakeFace = true
  OffsetFill = false
  OffsetIntersection = false
  OffsetJoinType = 0
  OffsetOpenResult = false
  PartialLoad = false
  Relative = true
  Support = -> [Offset2D001]
  _Version = 2
FEATURE [PartDesign::FeaturePython] BaseBend010  # WARN: FeaturePython — macro-defined, semantics opaque (R4)
  BendSide = 0
  BendSketch = -> Binder029
  MidPlane = false
  Reverse = true
  Suppressed = false
  length = 100
  radius = 0.1
  thickness = 0.3
FEATURE [PartDesign::FeaturePython] Bend008  # WARN: FeaturePython — macro-defined, semantics opaque (R4)
  AutoMiter = false
  BaseFeature = -> BaseBend010
  BendType = 0
  LengthList = [30]
  LengthSpec = 0
  ReliefFactor = 0.7
  Suppressed = false
  UseReliefFactor = false
  angle = 90
  baseObject = -> BaseBend010 [Edge15,Edge18,Edge21,Edge23]
  bendAList = [90]
  extend1 = 0
  extend2 = 0
  gap1 = 3
  gap2 = 3
  invert = false
  kfactor = 0.5
  length = 30
  maxExtendDist = 5
  minGap = 0.2
  minReliefGap = 1
  miterangle1 = 45
  miterangle2 = 45
  offset = 0
  radius = 0.1
  reliefType = 0
  reliefd = 0.1
  reliefw = 0.8
  sketchflip = false
  sketchinvert = false
  unfold = false
  expr: radius = BaseBend010.radius
FEATURE [Part::Extrusion] Extrude021
  Base = -> Sketch090
  Dir = (0,0,1)
  DirMode = 2
  FaceMakerClass = Part::FaceMakerBullseye
  LengthFwd = 30
  LengthRev = 0
  Reversed = true
  Solid = true
  Symmetric = false
FEATURE [Part::FeaturePython] Populate046  label="Populate shield_placement with Extrude021"  # WARN: FeaturePython — macro-defined, semantics opaque (R4)
  Copying = 0
  ExposePlacement = false
  MarkerShape = 1
  MarkerSize = 0
  NumElements = 0
  Object = -> Extrude021
  OutputCompounding = 2
  PlacementsTo = -> Placment018
  Referencing = 0
  Type = lattice2PopulateCopies.LatticePopulateCopies
  isLattice = 0
FEATURE [Sketcher::SketchObject] Sketch091
  ExternalGeometry = -> [Sketch090]
  FullyConstrained = true
  Placement = pos=(43.1,0,-15) rot=(0.57735,0.57735,0.57735;2.0944rad)
  expr: .Placement.Base.x = <<Sketch090>>.Constraints.width / 2 - 0.4 mm
  sketch-geometry (6):
    g0: Circle CenterX=78.5796 CenterY=0 CenterZ=0 NormalX=0 NormalY=0 NormalZ=1 AngleXU=0 Radius=1.7
    g1: Circle CenterX=-78.5796 CenterY=0 CenterZ=0 NormalX=0 NormalY=0 NormalZ=1 AngleXU=0 Radius=1.7
    g2: LineSegment StartX=-157 StartY=5 StartZ=0 EndX=-78.5796 EndY=0 EndZ=0
    g3: LineSegment StartX=-78.5796 StartY=0 StartZ=0 EndX=0 EndY=0 EndZ=0
    g4: LineSegment StartX=0 StartY=0 StartZ=0 EndX=78.5796 EndY=0 EndZ=0
    g5: LineSegment StartX=78.5796 StartY=0 StartZ=0 EndX=157 EndY=5 EndZ=0
  constraints (14):
    c: PointOnObject(g0,g-1)
    c: PointOnObject(g1,g-1)
    c: Coincident(g-3,g2)
    c: Coincident(g2,g1)
    c: Coincident(g2,g3)
    c: Coincident(g3,g-1)
    c: Coincident(g3,g4)
    c: Coincident(g4,g0)
    c: Coincident(g4,g5)
    c: Coincident(g5,g-3)
    c: Equal(g5,g4)
    c: Equal(g4,g3)
    c: Equal(g1,g0)
    c: Diameter(g0) = 3.4
FEATURE [Sketcher::SketchObject] Sketch092
  ExternalGeometry = -> [Sketch090]
  FullyConstrained = true
  Placement = pos=(0,-156.6,-15) rot=(1,0,0;1.5708rad)
  expr: .Placement.Base.y = -(<<Sketch090>>.Constraints.length / 2 - 0.4 mm)
  expr: .Placement.Base.z = <<Sketch091>>.Placement.Base.z
  sketch-geometry (1):
    g0: Circle CenterX=0 CenterY=0 CenterZ=0 NormalX=0 NormalY=0 NormalZ=1 AngleXU=0 Radius=1.7
  constraints (2):
    c: Coincident(g0,g-1)
    c: Diameter(g0) = 3.4
FEATURE [Part::Extrusion] Extrude022
  Base = -> Sketch091
  Dir = (1,0,0)
  DirMode = 2
  FaceMakerClass = Part::FaceMakerBullseye
  LengthFwd = 10
  LengthRev = 0
  Solid = true
  Symmetric = false
FEATURE [Part::Extrusion] Extrude023
  Base = -> Sketch092
  Dir = (0,-1,2e-16)
  DirMode = 2
  FaceMakerClass = Part::FaceMakerBullseye
  LengthFwd = 10
  LengthRev = 0
  Solid = true
  Symmetric = false
FEATURE [Part::FeaturePython] PolarArray  label="2_elem_PolarArray"  # WARN: FeaturePython — macro-defined, semantics opaque (R4)
  Alignment = 0
  AttacherType = Attacher::AttachEngine3D
  CellStart = A1
  Count = 2
  DistributionLaw = 0
  EndInclusive = false
  ExposePlacement = false
  FlipX = false
  FlipZ = false
  GeneratorMode = 0
  MarkerShape = 1
  MarkerSize = 20
  NumElements = 2
  OrientMode = 2
  Radius = 0
  Reverse = false
  SpanEnd = 360
  SpanStart = 0
  Step = 180
  Type = lattice2PolarArray2.PolarArray
  UseArcRadius = false
  UseArcRange = 0
  VSGVersion = 1
  Values = 0.0 | 180.0
  ValuesSource = 2
  isLattice = 1
FEATURE [Part::Compound] Compound025
  Links = -> [Extrude022,Extrude023]
FEATURE [Part::FeaturePython] Populate048  label="Populate 2_elem_PolarArray with Compound025"  # WARN: FeaturePython — macro-defined, semantics opaque (R4)
  Copying = 0
  ExposePlacement = false
  MarkerShape = 1
  MarkerSize = 0
  NumElements = 0
  Object = -> Compound025
  OutputCompounding = 1
  PlacementsTo = -> PolarArray
  Referencing = 0
  Type = lattice2PopulateCopies.LatticePopulateCopies
  isLattice = 0
FEATURE [Part::Compound] Compound026
  Links = -> [Populate048]
FEATURE [PartDesign::Boolean] Boolean019
  BaseFeature = -> Bend008
  Group = -> [Compound026]
  Suppressed = false
  Type = 1
  UsePlacement = true
FEATURE [PartDesign::Body] Body022
  Group = -> [Binder029,BaseBend010,Bend008,Boolean019]
  Origin = -> Origin024
  Tip = -> Boolean019
FEATURE [Part::FeaturePython] Populate047  label="Populate shield_placement with Body022"  # WARN: FeaturePython — macro-defined, semantics opaque (R4)
  Copying = 0
  ExposePlacement = false
  MarkerShape = 1
  MarkerSize = 0
  NumElements = 0
  Object = -> Body022
  OutputCompounding = 2
  PlacementsTo = -> Placment018
  Referencing = 0
  Type = lattice2PopulateCopies.LatticePopulateCopies
  isLattice = 0
FEATURE [Part::Compound] Compound005  label="face_fuse1"
  Links = -> [Cut,Populate047]
FEATURE [Part::Extrusion] Extrude024
  Base = -> Sketch025
  Dir = (0,0,1)
  DirMode = 2
  FaceMakerClass = Part::FaceMakerBullseye
  LengthFwd = 10
  LengthRev = 0
  Solid = true
  Symmetric = false
FEATURE [Part::Extrusion] Extrude025
  Base = -> Sketch027
  Dir = (0,0,1)
  DirMode = 2
  FaceMakerClass = Part::FaceMakerBullseye
  LengthFwd = 10
  LengthRev = 0
  Solid = true
  Symmetric = false
FEATURE [Part::Compound] Compound027
  Links = -> [Extrude024,Extrude025]
FEATURE [PartDesign::Boolean] Boolean020
  BaseFeature = -> Pad020
  Group = -> [Compound027]
  Suppressed = false
  Type = 1
  UsePlacement = true
FEATURE [PartDesign::Body] Body020  label="top_triangle"
  Group = -> [Binder027,Pad020,Boolean020]
  Origin = -> Origin022
  Tip = -> Boolean020
FEATURE [PartDesign::SubShapeBinder] Binder030
  BindCopyOnChange = 0
  BindMode = 0
  ClaimChildren = true
  Context = -> Body023 [Binder030.]
  Fuse = false
  MakeFace = true
  OffsetFill = false
  OffsetIntersection = false
  OffsetJoinType = 0
  OffsetOpenResult = false
  PartialLoad = false
  Relative = false
  Support = -> [Sketch044]
  _Version = 2
FEATURE [PartDesign::Pad] Pad021
  Direction = (0,0,1)
  Length = 100
  Length2 = 10
  Profile = -> Binder030
  Suppressed = false
  Type = 0
FEATURE [Sketcher::SketchObject] Sketch093
  ExternalGeometry = -> [Sketch]
  FullyConstrained = true
  sketch-geometry (4):
    g0: LineSegment StartX=-164.635 StartY=20 StartZ=0 EndX=-319.563 EndY=150 EndZ=0
    g1: LineSegment StartX=-319.563 StartY=150 StartZ=0 EndX=-319.563 EndY=-21.1296 EndZ=0
    g2: LineSegment StartX=-319.563 StartY=-21.1296 StartZ=0 EndX=-175.968 EndY=150 EndZ=0
    g3: LineSegment StartX=-175.968 StartY=150 StartZ=0 EndX=-319.563 EndY=150 EndZ=0
  constraints (10):
    c: Symmetric(g0,g-3,g-2)
    c: Symmetric(g0,g-3,g-2)
    c: Coincident(g0,g1)
    c: Vertical(g1)
    c: Coincident(g1,g2)
    c: Coincident(g2,g3)
    c: Coincident(g3,g1)
    c: Horizontal(g3)
    c: Perpendicular(g0,g2)
    c: Distance(g1,g2) = 110
FEATURE [PartDesign::SubShapeBinder] Binder031
  BindCopyOnChange = 0
  BindMode = 0
  ClaimChildren = true
  Context = -> Body023 [Binder031.]
  Fuse = false
  MakeFace = true
  OffsetFill = false
  OffsetIntersection = false
  OffsetJoinType = 0
  OffsetOpenResult = false
  PartialLoad = false
  Placement = pos=(0,0,100) rot=(0,0,1;0rad)
  Relative = false
  Support = -> [Sketch093]
  _Version = 2
  expr: .Placement.Base.z = <<Pad021>>.Length
FEATURE [PartDesign::Pocket] Pocket028
  BaseFeature = -> Pad021
  Direction = (0,0,-1)
  Length = 30
  Length2 = 5
  Profile = -> Binder031
  Suppressed = false
  Type = 0
FEATURE [Sketcher::SketchObject] Sketch094  label="drain"
  FullyConstrained = true
  Placement = pos=(0,63,0) rot=(0,0,1;0rad)
  expr: .Placement.Base.y = 43 mm + <<base_Sketch>>.Constraints.offset
  sketch-geometry (1):
    g0: Circle CenterX=0 CenterY=0 CenterZ=0 NormalX=0 NormalY=0 NormalZ=1 AngleXU=0 Radius=37.5
  constraints (2):
    c: Coincident(g0,g-1)
    c: Diameter(g0) = 75  'd'
FEATURE [Sketcher::SketchObject] Sketch045  label="drain_holder_base_sketch"
  ExternalGeometry = -> [Part__Mirroring,Sketch093,Sketch094]
  FullyConstrained = true
  Placement = pos=(-319.563,0,0) rot=(0,0,1;0rad)
  expr: .Placement.Base.x = -<<mid_Sketch>>.Constraints.middle
  sketch-geometry (4):
    g0: LineSegment StartX=0 StartY=105 StartZ=0 EndX=58.2961 EndY=105 EndZ=0
    g1: LineSegment StartX=58.2961 StartY=105 StartZ=0 EndX=86.1933 EndY=81.5915 EndZ=0
    g2: LineSegment StartX=56.3677 StartY=102.702 StartZ=0 EndX=58.2961 EndY=105 EndZ=0
    g3: LineSegment StartX=0 StartY=100.5 StartZ=0 EndX=319.563 EndY=100.5 EndZ=0
  constraints (14):
    c: PointOnObject(g0,g-2)
    c: Horizontal(g0)
    c: Coincident(g0,g1)
    c: PointOnObject(g2,g-3)
    c: Coincident(g2,g0)
    c: Perpendicular(g1,g2)
    c: Perpendicular(g-3,g2)
    c: PointOnObject(g1,g-4)
    c: Tangent(g3,g-5) = 1.5708
    c: Horizontal(g3)
    c: PointOnObject(g3,g-2)
    c: DistanceY(g0) = 105  'offset'
    c: DistanceY(g-5,g0) = 42
    c: Distance(g2) = 3
FEATURE [PartDesign::Fillet] Fillet
  Base = -> Pocket028 [Edge14]
  BaseFeature = -> Pocket028
  Radius = 5
  SupportTransform = false
  Suppressed = false
  UseAllEdges = false
FEATURE [PartDesign::Body] Body023  label="bottom_cut_Body"
  Group = -> [Binder030,Pad021,Binder031,Pocket028,Fillet]
  Origin = -> Origin025
  Placement = pos=(319.563,0,0) rot=(0,0,1;0rad)
  Tip = -> Fillet
  expr: .Placement.Base.x = <<mid_Sketch>>.Constraints.middle
FEATURE [Part::Mirroring] Part__Mirroring012  label="bottom_cut_Body (Mirror #13)"
  Base = (0,0,0)
  Normal = (1,0,0)
  Source = -> Body023
FEATURE [PartDesign::CoordinateSystem] Local_CS033  label="drain_holder_LCS"
  AttacherType = Attacher::AttachEngine3D
  MapMode = 5
FEATURE [Sketcher::SketchObject] Sketch097
  AttachmentOffset = pos=(0,0,0) rot=(0,1,0;1.5708rad)
  FullyConstrained = true
  MapMode = 7
  Placement = pos=(86.1933,81.5915,-10) rot=(0.889126,-0.323616,-0.323616;1.68804rad)
  sketch-geometry (3):
    g0: ArcOfCircle CenterX=-5 CenterY=5 CenterZ=0 NormalX=0 NormalY=0 NormalZ=1 AngleXU=0 Radius=5 StartAngle=4.71239 EndAngle=6.28319
    g1: LineSegment StartX=-5 StartY=6.505e-12 StartZ=0 EndX=0 EndY=0 EndZ=0
    g2: LineSegment StartX=0 StartY=0 StartZ=0 EndX=-6.505e-12 EndY=5 EndZ=0
  constraints (7):
    c: PointOnObject(g0,g-1)
    c: PointOnObject(g0,g-2)
    c: Coincident(g1,g2)
    c: Tangent(g2,g0) = -1.5708
    c: Tangent(g0,g1) = -1.5708
    c: Coincident(g1,g-1)
    c: Radius(g0) = 5
FEATURE [PartDesign::Plane] DatumPlane006
  AttachmentOffset = pos=(0,0,45) rot=(0,0,1;0rad)
  Length = 202.327
  MapMode = 5
  Placement = pos=(0,0,45) rot=(0,0,1;0rad)
  ResizeMode = 0
  Width = 159.94
  expr: .AttachmentOffset.Base.z = <<drain_holder_BaseBend>>.length / 2 + <<Binder021>>.Placement.Base.z
FEATURE [PartDesign::Pocket] Pocket029
  BaseFeature = -> BaseBend006
  Direction = (0.642788,0.766044,0)
  Length = 5
  Length2 = 5
  Midplane = true
  Profile = -> Sketch097
  ReferenceAxis = -> Sketch097 [N_Axis]
  Suppressed = false
  Type = 0
FEATURE [PartDesign::Mirrored] Mirrored010
  MirrorPlane = -> DatumPlane006
  Suppressed = false
FEATURE [PartDesign::Mirrored] Mirrored011
  MirrorPlane = -> YZ_Plane019
  Suppressed = false
FEATURE [PartDesign::MultiTransform] MultiTransform005
  BaseFeature = -> Pocket029
  Originals = -> [Pocket029]
  Refine = true
  Suppressed = false
  Transformations = -> [Mirrored010,Mirrored011]
FEATURE [PartDesign::CoordinateSystem] Local_CS034
  AttacherType = Attacher::AttachEngine3D
  AttachmentOffset = pos=(-639.126,60,480) rot=(0.57735,-0.57735,-0.57735;2.0944rad)
  MapMode = 5
  Placement = pos=(-639.126,60,480) rot=(0.57735,-0.57735,-0.57735;2.0944rad)
  expr: AttachmentOffset = <<shield_placement>>.Placement
FEATURE [PartDesign::CoordinateSystem] Local_CS035  label="electric_shield_LCS"
  AttacherType = Attacher::AttachEngine3D
  AttachmentOffset = pos=(0,0,33) rot=(0,0,1;0rad)
  AttachmentSupport = -> [XY_Plane023]
  MapMode = 5
  Placement = pos=(0,0,33) rot=(0,0,1;0rad)
  expr: .AttachmentOffset.Base.z = <<Bend007>>.length + 3 mm
FEATURE [Part::Compound] Compound028
  Links = -> [Populate048]
  Placement = pos=(0,0,33) rot=(0,0,1;0rad)
FEATURE [Part::Compound] Compound029
  Links = -> [Compound028]
FEATURE [PartDesign::Boolean] Boolean021
  BaseFeature = -> Bend007
  Group = -> [Compound029]
  Suppressed = false
  Type = 1
  UsePlacement = true
FEATURE [PartDesign::Body] Body021  label="electric_shield"
  Group = -> [Binder028,BaseBend009,Bend007,Local_CS035,Boolean021]
  Origin = -> Origin023
  Tip = -> Boolean021
FEATURE [PartDesign::FeaturePython] Bend011  # WARN: FeaturePython — macro-defined, semantics opaque (R4)
  AutoMiter = true
  BaseFeature = -> Bend006
  BendType = 0
  LengthList = [40]
  LengthSpec = 0
  ReliefFactor = 0.7
  Suppressed = false
  UseReliefFactor = false
  angle = 90
  baseObject = -> Bend006 [Edge12]
  bendAList = [90]
  extend1 = 0
  extend2 = 0
  gap1 = 20
  gap2 = 3
  invert = true
  kfactor = 0.5
  length = 40
  maxExtendDist = 5
  minGap = 0.2
  minReliefGap = 1
  miterangle1 = 0
  miterangle2 = 0
  offset = 0
  radius = 0.1
  reliefType = 0
  reliefd = 1
  reliefw = 0.8
  sketchflip = false
  sketchinvert = false
  unfold = false
  expr: radius = <<cap_outer_BaseBend>>.radius
FEATURE [PartDesign::FeaturePython] Bend012  # WARN: FeaturePython — macro-defined, semantics opaque (R4)
  AutoMiter = true
  BaseFeature = -> Bend011
  BendType = 0
  LengthList = [20]
  LengthSpec = 0
  ReliefFactor = 0.7
  Suppressed = false
  UseReliefFactor = false
  angle = 90
  baseObject = -> Bend011 [Edge12]
  bendAList = [90]
  extend1 = 0
  extend2 = 0
  gap1 = 0
  gap2 = 3.2
  invert = true
  kfactor = 0.5
  length = 20
  maxExtendDist = 5
  minGap = 0.2
  minReliefGap = 1
  miterangle1 = 0
  miterangle2 = 0
  offset = 0
  radius = 0.1
  reliefType = 0
  reliefd = 1
  reliefw = 0.8
  sketchflip = false
  sketchinvert = false
  unfold = false
  expr: radius = <<cap_outer_BaseBend>>.radius
FEATURE [PartDesign::Boolean] Boolean018
  BaseFeature = -> Bend012
  Group = -> [Compound024]
  Suppressed = false
  Type = 1
  UsePlacement = true
FEATURE [PartDesign::Pad] Pad019
  BaseFeature = -> Boolean018
  Direction = (1,0,0)
  Length = 0.3
  Length2 = 10
  Profile = -> Sketch085
  ReferenceAxis = -> Sketch085 [N_Axis]
  Refine = true
  Reversed = true
  Suppressed = false
  Type = 0
FEATURE [PartDesign::Body] Body019  label="cap_inner"
  Group = -> [Binder025,BaseBend008,Bend006,Bend011,Bend012,Boolean018,Sketch085,Binder026,Pad019,Local_CS031]
  Origin = -> Origin021
  Tip = -> Pad019
FEATURE [Sketcher::SketchObject] Sketch098
  FullyConstrained = true
  expr: Constraints[5] = <<drain>>.Constraints.d + 6 mm + 2 mm
  sketch-geometry (3):
    g0: LineSegment StartX=-41.5 StartY=15 StartZ=0 EndX=-41.5 EndY=60 EndZ=0
    g1: LineSegment StartX=-41.5 StartY=60 StartZ=0 EndX=41.5 EndY=60 EndZ=0
    g2: LineSegment StartX=41.5 StartY=60 StartZ=0 EndX=41.5 EndY=15 EndZ=0
  constraints (8):
    c: Coincident(g0,g1)
    c: Coincident(g1,g2)
    c: Vertical(g2)
    c: Symmetric(g0,g2,g-2)
    c: Symmetric(g0,g1,g-2)
    c: DistanceX(g1,g1) = 83
    c: DistanceY(g2,g2) = 45
    c: DistanceY(g2) = 15
FEATURE [PartDesign::SubShapeBinder] Binder033
  BindCopyOnChange = 0
  BindMode = 0
  ClaimChildren = true
  Context = -> Body025 [Binder033.]
  Fuse = false
  MakeFace = true
  OffsetFill = false
  OffsetIntersection = false
  OffsetJoinType = 0
  OffsetOpenResult = false
  PartialLoad = false
  Placement = pos=(0,101.6,0) rot=(1,0,0;1.5708rad)
  Relative = false
  Support = -> [Sketch098]
  _Version = 2
  expr: .Placement.Base.y = <<drain_holder_base_sketch>>.Constraints.offset - 3.4 mm
FEATURE [PartDesign::FeaturePython] BaseBend012  # WARN: FeaturePython — macro-defined, semantics opaque (R4)
  BendSide = 0
  BendSketch = -> Binder033
  MidPlane = false
  Reverse = false
  Suppressed = false
  length = 80
  radius = 0.1
  thickness = 0.3
FEATURE [PartDesign::FeaturePython] Bend013  # WARN: FeaturePython — macro-defined, semantics opaque (R4)
  AutoMiter = true
  BaseFeature = -> BaseBend012
  BendType = 0
  LengthList = [20]
  LengthSpec = 0
  ReliefFactor = 0.7
  Suppressed = false
  UseReliefFactor = false
  angle = 90
  baseObject = -> BaseBend012 [Edge32,Edge3]
  bendAList = [90]
  extend1 = 0
  extend2 = 0
  gap1 = 4
  gap2 = 4
  invert = false
  kfactor = 0.5
  length = 20
  maxExtendDist = 5
  minGap = 0.2
  minReliefGap = 1
  miterangle1 = 0
  miterangle2 = 0
  offset = 0
  radius = 0.1
  reliefType = 0
  reliefd = 1
  reliefw = 0.8
  sketchflip = false
  sketchinvert = false
  unfold = false
  expr: radius = BaseBend012.radius
FEATURE [Part::Cylinder] Cylinder002  label="Cylinder"
  Angle = 360
  AttacherType = Attacher::AttachEngine3D
  FirstAngle = 0
  Height = 130
  Placement = pos=(0,63,0) rot=(0,0,1;0rad)
  Radius = 23.5
  SecondAngle = 0
  expr: Placement = <<drain>>.Placement
FEATURE [App::DocumentObjectGroup] Group010  label="Group"
FEATURE [Sketcher::SketchObject] Sketch099
  ExternalGeometry = -> [Binder033]
  FullyConstrained = true
  MapMode = 5
  Placement = pos=(0,0,0) rot=(0.57735,0.57735,0.57735;2.0944rad)
  expr: Constraints[8] = <<BaseBend012>>.length
  sketch-geometry (3):
    g0: LineSegment StartX=21.6 StartY=57 StartZ=0 EndX=98.6 EndY=15 EndZ=0
    g1: LineSegment StartX=98.6 StartY=15 StartZ=0 EndX=21.6 EndY=15 EndZ=0
    g2: LineSegment StartX=21.6 StartY=15 StartZ=0 EndX=21.6 EndY=57 EndZ=0
  constraints (9):
    c: Coincident(g0,g1)
    c: Horizontal(g1)
    c: Coincident(g1,g2)
    c: Coincident(g2,g0)
    c: Vertical(g2)
    c: Horizontal(g0,g-3)
    c: DistanceX(g0,g-3) = 3
    c: DistanceY(g0,g-3) = 3
    c: DistanceX(g1,g-3) = 80
FEATURE [PartDesign::Pocket] Pocket030
  BaseFeature = -> Bend013
  Direction = (-1,0,0)
  Length = 5
  Length2 = 5
  Midplane = true
  Profile = -> Sketch099
  ReferenceAxis = -> Sketch099 [N_Axis]
  Suppressed = false
  Type = 1
FEATURE [PartDesign::CoordinateSystem] Local_CS036
  AttacherType = Attacher::AttachEngine3D
  MapMode = 5
FEATURE [Part::FeaturePython] Placment019  # WARN: FeaturePython — macro-defined, semantics opaque (R4)
  AttacherType = Attacher::AttachEngine3D
  AttachmentOffset = pos=(0,0,-30) rot=(0,1,0;1.5708rad)
  ExposePlacement = true
  MapMode = 7
  MarkerShape = 1
  MarkerSize = 20
  NumElements = 1
  Placement = pos=(30,105,0) rot=(1,0,0;1.5708rad)
  Type = lattice2AttachablePlacement.AttachablePlacement
  isLattice = 1
FEATURE [Part::FeaturePython] LinearArray010  # WARN: FeaturePython — macro-defined, semantics opaque (R4)
  Alignment = 0
  CellStart = A1
  Count = 2
  Dir = (0,0,1)
  DirIsDriven = true
  DistributionLaw = 0
  DrivenProperty = 1
  EndInclusive = true
  ExposePlacement = false
  GeneratorMode = 0
  MarkerShape = 1
  MarkerSize = 0
  NumElements = 2
  OrientMode = 0
  Point = (0,0,0)
  PointIsDriven = true
  Reverse = false
  SpanEnd = 50
  SpanStart = 27
  Step = 23
  Type = lattice2LinearArray.LinearArray
  VSGVersion = 1
  Values = 27.0 | 50.0
  ValuesSource = 2
  isLattice = 1
FEATURE [Part::FeaturePython] Mirror007  label="Mirror007 of Placment019"  # WARN: FeaturePython — macro-defined, semantics opaque (R4)
  ExposePlacement = false
  FlipX = true
  FlipY = false
  FlipZ = false
  MarkerShape = 1
  MarkerSize = 10
  NumElements = 1
  Object = -> Placment019
  ObjectTraversal = 0
  Type = lattice2Mirror.LatticeMirror
  isLattice = 1
FEATURE [Part::FeaturePython] Join012  # WARN: FeaturePython — macro-defined, semantics opaque (R4)
  ExposePlacement = false
  Interleave = false
  Links = -> [Placment019,Mirror007]
  MarkerShape = 1
  MarkerSize = 0
  NumElements = 2
  Type = lattice2JoinArrays.JoinArrays
  isLattice = 1
FEATURE [Part::FeaturePython] Populate049  label="Populate LinearArray010 with Join012"  # WARN: FeaturePython — macro-defined, semantics opaque (R4)
  Copying = 0
  ExposePlacement = false
  MarkerShape = 1
  MarkerSize = 0
  NumElements = 4
  Object = -> Join012
  OutputCompounding = 0
  PlacementsTo = -> LinearArray010
  Referencing = 0
  Type = lattice2PopulateCopies.LatticePopulateCopies
  isLattice = 1
FEATURE [Part::FeaturePython] Populate050  label="Populate Populate LinearArray010 with Join012 with hole_3.4mm"  # WARN: FeaturePython — macro-defined, semantics opaque (R4)
  Copying = 0
  ExposePlacement = false
  MarkerShape = 1
  MarkerSize = 0
  NumElements = 0
  Object = -> Cylinder
  OutputCompounding = 1
  PlacementsTo = -> Populate049
  Referencing = 0
  Type = lattice2PopulateCopies.LatticePopulateCopies
  isLattice = 0
FEATURE [Part::Compound] Compound030
  Links = -> [Populate050,Cylinder002]
FEATURE [PartDesign::Boolean] Boolean022
  BaseFeature = -> Pocket030
  Group = -> [Compound030]
  Suppressed = false
  Type = 1
  UsePlacement = true
FEATURE [PartDesign::Body] Body025  label="drain_holder_back"
  Group = -> [Binder033,BaseBend012,Bend013,Sketch099,Pocket030,Local_CS036,Boolean022]
  Origin = -> Origin027
  Tip = -> Pocket030
FEATURE [Part::Cylinder] Cylinder003
  Angle = 360
  AttacherType = Attacher::AttachEngine3D
  FirstAngle = 0
  Height = 10
  Placement = pos=(0,110,15) rot=(1,0,0;1.5708rad)
  Radius = 4
  SecondAngle = 0
FEATURE [Part::Compound] Compound022
  Links = -> [Populate025,Cylinder003]
FEATURE [PartDesign::Boolean] Boolean016
  BaseFeature = -> MultiTransform005
  Group = -> [Compound022]
  Suppressed = false
  Type = 1
  UsePlacement = true
FEATURE [PartDesign::Body] Body017  label="drain_holder"
  Group = -> [Binder021,BaseBend006,DatumPlane006,Pocket029,MultiTransform005,Mirrored010,Mirrored011,Boolean016,Local_CS033,Sketch097]
  Origin = -> Origin019
  Tip = -> Boolean016
FEATURE [Part::FeaturePython] Placment020  # WARN: FeaturePython — macro-defined, semantics opaque (R4)
  AttacherType = Attacher::AttachEngine3D
  ExposePlacement = true
  MarkerShape = 1
  MarkerSize = 10
  NumElements = 1
  Placement = pos=(0,8,0) rot=(0,0,1;0rad)
  Type = lattice2AttachablePlacement.AttachablePlacement
  isLattice = 1
FEATURE [Part::FeaturePython] Placment021  # WARN: FeaturePython — macro-defined, semantics opaque (R4)
  AttacherType = Attacher::AttachEngine3D
  ExposePlacement = true
  MarkerShape = 1
  MarkerSize = 10
  NumElements = 1
  Placement = pos=(210,0,0) rot=(0,0,1;0rad)
  Type = lattice2AttachablePlacement.AttachablePlacement
  isLattice = 1
FEATURE [Part::FeaturePython] Join013  # WARN: FeaturePython — macro-defined, semantics opaque (R4)
  ExposePlacement = false
  Interleave = false
  Links = -> [Placment020,Placment021]
  MarkerShape = 1
  MarkerSize = 0
  NumElements = 2
  Type = lattice2JoinArrays.JoinArrays
  isLattice = 1
FEATURE [Part::FeaturePython] LinearArray011  # WARN: FeaturePython — macro-defined, semantics opaque (R4)
  Alignment = 0
  CellStart = A1
  Count = 3
  Dir = (1,0,0)
  DirIsDriven = true
  DistributionLaw = 0
  DrivenProperty = 1
  EndInclusive = true
  ExposePlacement = false
  GeneratorMode = 0
  MarkerShape = 1
  MarkerSize = 0
  NumElements = 3
  OrientMode = 1
  Point = (0,0,0)
  PointIsDriven = true
  Reverse = false
  SpanEnd = 870
  SpanStart = 30
  Step = 420
  Type = lattice2LinearArray.LinearArray
  VSGVersion = 1
  Values = 30.0 | 450.0 | 870.0
  ValuesSource = 2
  isLattice = 1
FEATURE [Part::FeaturePython] Populate051  label="Populate LinearArray011 with Join013"  # WARN: FeaturePython — macro-defined, semantics opaque (R4)
  Copying = 0
  ExposePlacement = false
  MarkerShape = 1
  MarkerSize = 0
  NumElements = 6
  Object = -> Join013
  OutputCompounding = 0
  PlacementsTo = -> LinearArray011
  Referencing = 0
  Type = lattice2PopulateCopies.LatticePopulateCopies
  isLattice = 1
FEATURE [Part::FeaturePython] Populate028  label="Populate Placment011 with LinearArray009"  # WARN: FeaturePython — macro-defined, semantics opaque (R4)
  Copying = 0
  ExposePlacement = false
  MarkerShape = 1
  MarkerSize = 0
  NumElements = 6
  Object = -> Populate051
  OutputCompounding = 0
  PlacementsTo = -> Placment011
  Referencing = 0
  Type = lattice2PopulateCopies.LatticePopulateCopies
  isLattice = 1
FEATURE [Part::FeaturePython] Populate029  label="Populate Populate Placment011 with LinearArray009 with hole_3.4mm"  # WARN: FeaturePython — macro-defined, semantics opaque (R4)
  Copying = 0
  ExposePlacement = false
  MarkerShape = 1
  MarkerSize = 0
  NumElements = 0
  Object = -> Cylinder
  OutputCompounding = 1
  PlacementsTo = -> Populate028
  Referencing = 0
  Type = lattice2PopulateCopies.LatticePopulateCopies
  isLattice = 0
FEATURE [Part::Compound] Compound018
  Links = -> [Populate027,Populate029,Populate041]
FEATURE [PartDesign::Boolean] Boolean010
  BaseFeature = -> Mirrored006
  Group = -> [Compound018]
  Suppressed = false
  Type = 1
  UsePlacement = true
FEATURE [PartDesign::Body] Body012  label="lamp_fix"
  Group = -> [Binder016,BaseBend004,Sketch065,Sketch067,Sketch068,DatumPlane002,Pocket018,Pocket019,Mirrored006,Local_CS026,Sketch066,Boolean010,Local_CS028]
  Origin = -> Origin014
  Tip = -> Boolean010
FEATURE [Part::FeaturePython] Mirror003  label="Mirror003 of Populate Placment011 with LinearArray009"  # WARN: FeaturePython — macro-defined, semantics opaque (R4)
  ExposePlacement = false
  FlipX = true
  FlipY = false
  FlipZ = false
  MarkerShape = 1
  MarkerSize = 0
  NumElements = 6
  Object = -> Populate028
  ObjectTraversal = 0
  Type = lattice2Mirror.LatticeMirror
  isLattice = 1
FEATURE [Part::FeaturePython] Populate032  label="Populate Mirror003 of Populate Placment011 with LinearArray009 with hole_3.4mm"  # WARN: FeaturePython — macro-defined, semantics opaque (R4)
  Copying = 0
  ExposePlacement = false
  MarkerShape = 1
  MarkerSize = 0
  NumElements = 0
  Object = -> Cylinder
  OutputCompounding = 1
  PlacementsTo = -> Mirror003
  Referencing = 0
  Type = lattice2PopulateCopies.LatticePopulateCopies
  isLattice = 0
FEATURE [Part::Compound] Compound019
  Links = -> [Populate032,Populate033,Populate042]
FEATURE [PartDesign::Boolean] Boolean011
  BaseFeature = -> Mirrored007
  Group = -> [Compound019]
  Suppressed = false
  Type = 1
  UsePlacement = true
FEATURE [PartDesign::Body] Body013  label="lamp_fix_mirror"
  Group = -> [Binder017,BaseBend005,DatumPlane003,Sketch069,Sketch070,Pocket027,Pocket021,Mirrored007,Boolean011,Local_CS027]
  Origin = -> Origin015
  Tip = -> Pocket027
FEATURE [TechDraw::DrawViewPart] View013
  CoarseView = false
  Direction = (0,0,1)
  Focus = 100
  HardHidden = false
  IsoCount = 0
  IsoHidden = false
  IsoVisible = false
  LockPosition = false
  Perspective = false
  Rotation = 0
  ScaleType = 0
  ScrubCount = 0
  SeamHidden = false
  SeamVisible = true
  SmoothHidden = false
  SmoothVisible = true
  Source = -> [Body012]
  X = 148.5
  XDirection = (-0.642788,0.766044,0)
  Y = 105
FEATURE [TechDraw::DrawViewPart] View015
  CoarseView = false
  Direction = (0,0,1)
  Focus = 100
  HardHidden = false
  IsoCount = 0
  IsoHidden = false
  IsoVisible = false
  LockPosition = false
  Perspective = false
  Rotation = 0
  ScaleType = 0
  ScrubCount = 0
  SeamHidden = false
  SeamVisible = true
  SmoothHidden = false
  SmoothVisible = true
  Source = -> [Body013]
  X = 148.5
  XDirection = (-0.642788,-0.766044,0)
  Y = 105
FEATURE [TechDraw::DrawViewPart] View016
  CoarseView = false
  Direction = (-0.642788,-0.766044,0)
  Focus = 100
  HardHidden = false
  IsoCount = 0
  IsoHidden = false
  IsoVisible = false
  LockPosition = false
  Perspective = false
  Rotation = 90
  Scale = 0.32
  ScaleType = 2
  ScrubCount = 0
  SeamHidden = false
  SeamVisible = true
  SmoothHidden = false
  SmoothVisible = true
  Source = -> [Body013]
  X = 148.5
  XDirection = (0.766044,-0.642788,0)
  Y = 165
FEATURE [TechDraw::DrawPage] Page005  label="lamp_fix_mirror_Page"
  KeepUpdated = true
  NextBalloonIndex = 1
  ProjectionType = 0
  Template = -> Template
  Views = -> [View015,View016]
FEATURE [App::DocumentObjectGroup] Group009  label="lamp_fix_mirror_Group"
  Group = -> [Page005,Unfold001,Unfold_Sketch001,Unfold_Sketch_Outline001,Unfold_Sketch_Internal001,Unfold_Sketch_bends001]
FEATURE [TechDraw::DrawViewDimension] Dimension009
  AngleOverride = false
  Arbitrary = false
  ArbitraryTolerances = false
  EqualTolerance = true
  ExtensionAngle = 0
  FormatSpec = %.2w
  FormatSpecOverTolerance = %+.2w
  FormatSpecUnderTolerance = %+.2w
  Inverted = false
  LineAngle = 0
  LockPosition = false
  MeasureType = 1
  OverTolerance = 0
  References2D = -> [View013]
  Rotation = 0
  ScaleType = 0
  TheoreticalExact = false
  Type = 2
  UnderTolerance = 0
  X = -50
  Y = 0
FEATURE [TechDraw::DrawViewDimension] Dimension022
  AngleOverride = false
  Arbitrary = false
  ArbitraryTolerances = false
  EqualTolerance = true
  ExtensionAngle = 0
  FormatSpec = %.2w
  FormatSpecOverTolerance = %+.2w
  FormatSpecUnderTolerance = %+.2w
  Inverted = false
  LineAngle = 0
  LockPosition = false
  MeasureType = 1
  OverTolerance = 0
  References2D = -> [View013]
  Rotation = 0
  ScaleType = 0
  TheoreticalExact = false
  Type = 6
  UnderTolerance = 0
  X = 27.8896
  Y = 3.46171
FEATURE [TechDraw::DrawSVGTemplate] Template001
  Height = 210
  Orientation = 1
  Template = <path>
  Width = 297
FEATURE [Sketcher::SketchObject] Sketch101
  FullyConstrained = true
  sketch-geometry (5):
    g0: LineSegment StartX=240 StartY=0 StartZ=0 EndX=240 EndY=215 EndZ=0
    g1: LineSegment StartX=0 StartY=245 StartZ=0 EndX=210 EndY=245 EndZ=0
    g2: GeomPoint X=-240 Y=245 Z=0
    g3: GeomPoint X=240 Y=245 Z=0
    g4: LineSegment StartX=240 StartY=215 StartZ=0 EndX=210 EndY=245 EndZ=0
  constraints (13):
    c: PointOnObject(g0,g-1)
    c: Vertical(g0)
    c: DistanceY(g0,g3) = 245
    c: Horizontal(g1)
    c: Symmetric(g2,g3,g-2)
    c: DistanceX(g2,g3) = 480
    c: PointOnObject(g1,g-2)
    c: PointOnObject(g3,g0)
    c: PointOnObject(g3,g1)
    c: Coincident(g4,g0)
    c: Coincident(g4,g1)
    c: Angle(g4) = 2.35619
    c: DistanceY(g0,g3) = 30
FEATURE [Part::Mirroring] Part__Mirroring024  label="Sketch101 (Mirror #22)"
  Base = (0,0,0)
  Normal = (1,0,0)
  Source = -> Sketch101
FEATURE [Part::FeaturePython] Connect009  # WARN: FeaturePython — macro-defined, semantics opaque (R4)
  Objects = -> [Sketch101,Part__Mirroring024]
  Tolerance = 0
FEATURE [PartDesign::SubShapeBinder] Binder034
  BindCopyOnChange = 0
  BindMode = 0
  ClaimChildren = true
  Context = -> Body026 [Binder034.]
  Fuse = false
  MakeFace = true
  OffsetFill = false
  OffsetIntersection = false
  OffsetJoinType = 0
  OffsetOpenResult = false
  PartialLoad = false
  Relative = true
  Support = -> [Connect009]
  _Version = 2
FEATURE [PartDesign::FeaturePython] BaseBend013  # WARN: FeaturePython — macro-defined, semantics opaque (R4)
  BendSide = 0
  BendSketch = -> Binder034
  MidPlane = false
  Reverse = false
  Suppressed = false
  length = 245
  radius = 0.1
  thickness = 0.3
FEATURE [PartDesign::FeaturePython] Extend002  # WARN: FeaturePython — macro-defined, semantics opaque (R4)
  BaseFeature = -> BaseBend013
  Offset = 0.02
  Refine = true
  Suppressed = false
  UseSubtraction = false
  baseObject = -> BaseBend013 [Face1]
  gap1 = 0
  gap2 = 0
  length = 0
FEATURE [PartDesign::FeaturePython] Bend014  # WARN: FeaturePython — macro-defined, semantics opaque (R4)
  AutoMiter = true
  BaseFeature = -> Extend002
  BendType = 0
  LengthList = [20]
  LengthSpec = 1
  ReliefFactor = 0.7
  Suppressed = false
  UseReliefFactor = false
  angle = 90
  baseObject = -> Extend002 [Edge73,Edge58,Edge76,Edge29,Edge14]
  bendAList = [90]
  extend1 = 0
  extend2 = 0
  gap1 = 0
  gap2 = 0
  invert = false
  kfactor = 0.5
  length = 20
  maxExtendDist = 5
  minGap = 0.2
  minReliefGap = 1
  miterangle1 = 0
  miterangle2 = 0
  offset = 0
  radius = 0.1
  reliefType = 0
  reliefd = 1
  reliefw = 0.8
  sketchflip = false
  sketchinvert = false
  unfold = false
  expr: radius = BaseBend013.radius
FEATURE [Sketcher::SketchObject] Sketch102
  ExternalGeometry = -> [Sketch101]
  FullyConstrained = true
  sketch-geometry (7):
    g0: LineSegment StartX=0 StartY=244.99 StartZ=0 EndX=209.996 EndY=244.99 EndZ=0
    g1: LineSegment StartX=209.996 StartY=244.99 StartZ=0 EndX=239.99 EndY=214.996 EndZ=0
    g2: LineSegment StartX=239.99 StartY=214.996 StartZ=0 EndX=239.99 EndY=0 EndZ=0
    g3: LineSegment StartX=239.99 StartY=0 StartZ=0 EndX=0 EndY=0 EndZ=0
    g4: LineSegment StartX=209.996 StartY=245 StartZ=0 EndX=209.996 EndY=244.99 EndZ=0
    g5: LineSegment StartX=209.996 StartY=244.99 StartZ=0 EndX=210.003 EndY=244.997 EndZ=0
    g6: LineSegment StartX=239.99 StartY=214.996 StartZ=0 EndX=240 EndY=214.996 EndZ=0
  constraints (21):
    c: PointOnObject(g0,g-2)
    c: Horizontal(g0)
    c: Coincident(g0,g1)
    c: Coincident(g1,g2)
    c: PointOnObject(g2,g-1)
    c: Vertical(g2)
    c: Coincident(g2,g3)
    c: Coincident(g3,g-1)
    c: Parallel(g1,g-3)
    c: Distance(g1,g-3) = 0.01
    c: Coincident(g4,g0)
    c: Coincident(g4,g5)
    c: PointOnObject(g5,g-3)
    c: Coincident(g1,g6)
    c: Horizontal(g6)
    c: Vertical(g4)
    c: Horizontal(g4,g-3)
    c: Perpendicular(g-3,g5)
    c: Vertical(g6,g-3)
    c: Equal(g6,g5)
    c: Equal(g5,g4)
FEATURE [Part::Mirroring] Part__Mirroring025  label="Sketch102 (Mirror #23)"
  Base = (0,0,0)
  Normal = (1,0,0)
  Source = -> Sketch102
FEATURE [Part::FeaturePython] Connect010  # WARN: FeaturePython — macro-defined, semantics opaque (R4)
  Objects = -> [Sketch102,Part__Mirroring025]
  Tolerance = 0
FEATURE [PartDesign::SubShapeBinder] Binder035
  BindCopyOnChange = 0
  BindMode = 0
  ClaimChildren = true
  Context = -> Body027 [Binder035.]
  Fuse = false
  MakeFace = true
  OffsetFill = false
  OffsetIntersection = false
  OffsetJoinType = 0
  OffsetOpenResult = false
  PartialLoad = false
  Relative = true
  Support = -> [Connect010]
  _Version = 2
FEATURE [PartDesign::FeaturePython] BaseBend014  # WARN: FeaturePython — macro-defined, semantics opaque (R4)
  BendSide = 0
  BendSketch = -> Binder035
  MidPlane = false
  Reverse = false
  Suppressed = false
  length = 100
  radius = 0.1
  thickness = 0.3
FEATURE [Sketcher::SketchObject] Sketch103
  ExternalGeometry = -> [Sketch102]
  FullyConstrained = true
  sketch-geometry (14):
    g0: Circle CenterX=217.922 CenterY=222.922 CenterZ=0 NormalX=0 NormalY=0 NormalZ=1 AngleXU=0 Radius=1.7
    g1: Circle CenterX=229.99 CenterY=199.996 CenterZ=0 NormalX=0 NormalY=0 NormalZ=1 AngleXU=0 Radius=1.7
    g2: Circle CenterX=229.99 CenterY=15 CenterZ=0 NormalX=0 NormalY=0 NormalZ=1 AngleXU=0 Radius=1.7
    g3: Circle CenterX=194.996 CenterY=234.99 CenterZ=0 NormalX=0 NormalY=0 NormalZ=1 AngleXU=0 Radius=1.7
    g4: Circle CenterX=97.4979 CenterY=234.99 CenterZ=0 NormalX=0 NormalY=0 NormalZ=1 AngleXU=0 Radius=1.7
    g5: LineSegment StartX=239.99 StartY=214.996 StartZ=0 EndX=239.99 EndY=0 EndZ=0
    g6: LineSegment StartX=209.996 StartY=244.99 StartZ=0 EndX=0 EndY=244.99 EndZ=0
    g7: LineSegment StartX=209.996 StartY=244.99 StartZ=0 EndX=217.922 EndY=222.922 EndZ=0
    g8: LineSegment StartX=217.922 StartY=222.922 StartZ=0 EndX=239.99 EndY=214.996 EndZ=0
    g9: LineSegment StartX=0 StartY=234.99 StartZ=0 EndX=97.4979 EndY=234.99 EndZ=0
    g10: LineSegment StartX=97.4979 StartY=234.99 StartZ=0 EndX=194.996 EndY=234.99 EndZ=0
    g11: Circle CenterX=229.99 CenterY=107.498 CenterZ=0 NormalX=0 NormalY=0 NormalZ=1 AngleXU=0 Radius=1.7
    g12: LineSegment StartX=229.99 StartY=199.996 StartZ=0 EndX=229.99 EndY=107.498 EndZ=0
    g13: LineSegment StartX=229.99 StartY=107.498 StartZ=0 EndX=229.99 EndY=15 EndZ=0
  constraints (37):
    c: Coincident(g5,g-3)
    c: PointOnObject(g5,g-1)
    c: Coincident(g6,g-3)
    c: PointOnObject(g6,g-2)
    c: Horizontal(g6)
    c: Diameter(g4) = 3.4
    c: DistanceY(g2) = 15
    c: DistanceY(g1,g5) = 15
    c: Distance(g0,g-3) = 10
    c: Coincident(g6,g7)
    c: Coincident(g7,g0)
    c: Coincident(g7,g8)
    c: Coincident(g8,g5)
    c: Equal(g8,g7)
    c: PointOnObject(g9,g-2)
    c: Horizontal(g10)
    c: Equal(g10,g9)
    c: Horizontal(g9)
    c: Vertical(g12)
    c: Equal(g13,g12)
    c: Equal(g11,g4)
    c: Coincident(g13,g2)
    c: Coincident(g13,g11)
    c: Coincident(g12,g11)
    c: Coincident(g12,g1)
    c: Vertical(g13)
    c: Vertical(g5)
    c: Coincident(g9,g4)
    c: Coincident(g4,g10)
    c: DistanceX(g3,g6) = 15
    c: Equal(g3,g4)
    c: Equal(g3,g0)
    c: Equal(g0,g1)
    c: Equal(g11,g2)
    c: DistanceY(g3,g6) = 10
    c: DistanceX(g1,g5) = 10
    c: Coincident(g10,g3)
FEATURE [Part::FeaturePython] Downgrade  label="Wires of Sketch103"  # WARN: FeaturePython — macro-defined, semantics opaque (R4)
  Base = -> Sketch103
  Mode = 7
FEATURE [App::DocumentObjectGroup] Group002  label="util"
  Group = -> [Sketch046,Sketch047,Sketch049,LinearArray008,Sketch056,Populate038,Downgrade,Binder020]
FEATURE [Part::FeaturePython] ArrayFromShape001  label="Array from Wires of Sketch103"  # WARN: FeaturePython — macro-defined, semantics opaque (R4)
  CompoundTraversal = 2
  ExposePlacement = false
  MarkerShape = 1
  MarkerSize = 20
  NumElements = 3
  OrientElementIndex = 0
  OrientMode = 2
  ShapeLink = -> Downgrade
  TranslateElementIndex = 0
  TranslateMode = 3
  Type = lattice2ArrayFromShape.LatticeArrayFromShape
  isLattice = 1
FEATURE [Part::FeaturePython] Mirror008  label="Mirror008 of Array from Wires of Sketch103"  # WARN: FeaturePython — macro-defined, semantics opaque (R4)
  ExposePlacement = false
  FlipX = true
  FlipY = false
  FlipZ = false
  MarkerShape = 1
  MarkerSize = 0
  NumElements = 3
  Object = -> ArrayFromShape001
  ObjectTraversal = 0
  Type = lattice2Mirror.LatticeMirror
  isLattice = 1
FEATURE [Part::FeaturePython] Join014  # WARN: FeaturePython — macro-defined, semantics opaque (R4)
  ExposePlacement = false
  Interleave = false
  Links = -> [ArrayFromShape001,Mirror008]
  MarkerShape = 1
  MarkerSize = 0
  NumElements = 6
  Type = lattice2JoinArrays.JoinArrays
  isLattice = 1
FEATURE [Part::FeaturePython] Populate052  label="Populate Join014 with hole_3.4mm"  # WARN: FeaturePython — macro-defined, semantics opaque (R4)
  Copying = 0
  ExposePlacement = false
  MarkerShape = 1
  MarkerSize = 0
  NumElements = 0
  Object = -> Cylinder
  OutputCompounding = 1
  PlacementsTo = -> Join014
  Referencing = 0
  Type = lattice2PopulateCopies.LatticePopulateCopies
  isLattice = 0
FEATURE [Part::FeaturePython] Placment022  # WARN: FeaturePython — macro-defined, semantics opaque (R4)
  AttacherType = Attacher::AttachEngine3D
  AttachmentOffset = pos=(0,0,236.7) rot=(0,0,1;0rad)
  ExposePlacement = true
  MarkerShape = 1
  MarkerSize = 50
  NumElements = 1
  Placement = pos=(0,0,241.7) rot=(0,0,1;0rad)
  Type = lattice2AttachablePlacement.AttachablePlacement
  isLattice = 1
FEATURE [Sketcher::SketchObject] Sketch106
  ExternalGeometry = -> [Binder011]
  FullyConstrained = true
  sketch-geometry (3):
    g0: LineSegment StartX=0 StartY=120 StartZ=0 EndX=63.2961 EndY=120 EndZ=0
    g1: LineSegment StartX=63.2961 StartY=120 StartZ=0 EndX=96.1933 EndY=92.396 EndZ=0
    g2: LineSegment StartX=96.1933 StartY=92.396 StartZ=0 EndX=96.1933 EndY=0 EndZ=0
  constraints (10):
    c: PointOnObject(g0,g-2)
    c: Horizontal(g0)
    c: Coincident(g0,g1)
    c: PointOnObject(g2,g-1)
    c: DistanceX(g-3,g0) = 5
    c: DistanceY(g-3,g0) = 15
    c: Coincident(g1,g2)
    c: Parallel(g-3,g1)
    c: Vertical(g2)
    c: DistanceX(g-3,g1) = 10
FEATURE [Sketcher::SketchObject] Sketch107
  ExternalGeometry = -> [Sketch106]
  FullyConstrained = true
  sketch-geometry (6):
    g0: LineSegment StartX=0 StartY=117 StartZ=0 EndX=62.2042 EndY=117 EndZ=0
    g1: LineSegment StartX=93.1933 StartY=0 StartZ=0 EndX=0 EndY=0 EndZ=0
    g2: LineSegment StartX=62.2042 StartY=120 StartZ=0 EndX=62.2042 EndY=117 EndZ=0
    g3: LineSegment StartX=62.2042 StartY=117 StartZ=0 EndX=64.1325 EndY=119.298 EndZ=0
    g4: LineSegment StartX=62.2042 StartY=117 StartZ=0 EndX=93.1933 EndY=90.9971 EndZ=0
    g5: LineSegment StartX=93.1933 StartY=90.9971 StartZ=0 EndX=93.1933 EndY=0 EndZ=0
  constraints (18):
    c: PointOnObject(g0,g-2)
    c: Horizontal(g0)
    c: Coincident(g0,g4)
    c: PointOnObject(g5,g-1)
    c: Coincident(g5,g1)
    c: Coincident(g1,g-1)
    c: Coincident(g2,g0)
    c: Coincident(g2,g3)
    c: PointOnObject(g3,g-3)
    c: Equal(g2,g3)
    c: Distance(g3) = 3
    c: Horizontal(g2,g-3)
    c: Vertical(g2)
    c: Perpendicular(g-3,g3)
    c: Coincident(g4,g5)
    c: Perpendicular(g4,g3)
    c: DistanceX(g4,g-3) = 3
    c: Vertical(g5)
FEATURE [Part::Mirroring] Part__Mirroring026  label="Sketch107 (Mirror #24)"
  Base = (0,0,0)
  Normal = (1,0,0)
  Source = -> Sketch107
FEATURE [Part::FeaturePython] Connect011  # WARN: FeaturePython — macro-defined, semantics opaque (R4)
  Objects = -> [Sketch107,Part__Mirroring026]
  Tolerance = 0
FEATURE [Part::Extrusion] Extrude026
  Base = -> Connect011
  Dir = (0,0,1)
  DirMode = 2
  FaceMakerClass = Part::FaceMakerBullseye
  LengthFwd = 10
  LengthRev = 0
  Solid = true
  Symmetric = false
FEATURE [Part::Compound] Compound031
  Links = -> [Extrude026]
FEATURE [PartDesign::Boolean] Boolean023
  BaseFeature = -> BaseBend014
  Group = -> [Compound031]
  Refine = true
  Suppressed = false
  Type = 1
  UsePlacement = true
FEATURE [PartDesign::FeaturePython] Bend015  # WARN: FeaturePython — macro-defined, semantics opaque (R4)
  AutoMiter = false
  BaseFeature = -> Boolean023
  BendType = 0
  LengthList = [25]
  LengthSpec = 0
  ReliefFactor = 0.7
  Suppressed = false
  UseReliefFactor = false
  angle = 90
  baseObject = -> Boolean023 [Edge15,Edge17,Edge19]
  bendAList = [90]
  extend1 = 0
  extend2 = 0
  gap1 = 2.5
  gap2 = 2.5
  invert = false
  kfactor = 0.5
  length = 25
  maxExtendDist = 5
  minGap = 0.2
  minReliefGap = 1
  miterangle1 = 30
  miterangle2 = 30
  offset = 0
  radius = 0.1
  reliefType = 0
  reliefd = 1
  reliefw = 0.8
  sketchflip = false
  sketchinvert = false
  unfold = false
  expr: radius = BaseBend014.radius
FEATURE [PartDesign::SubShapeBinder] Binder038
  BindCopyOnChange = 0
  BindMode = 0
  ClaimChildren = true
  Context = -> Body030 [Binder038.]
  Fuse = false
  MakeFace = true
  OffsetFill = false
  OffsetIntersection = false
  OffsetJoinType = 0
  OffsetOpenResult = false
  PartialLoad = false
  Relative = true
  Support = -> [Connect012]
  _Version = 2
FEATURE [PartDesign::FeaturePython] BaseBend017  # WARN: FeaturePython — macro-defined, semantics opaque (R4)
  BendSide = 0
  BendSketch = -> Binder038
  MidPlane = false
  Reverse = false
  Suppressed = false
  length = 262
  radius = 0.1
  thickness = 0.3
FEATURE [Part::Mirroring] Part__Mirroring027  label="Sketch106 (Mirror #25)"
  Base = (0,0,0)
  Normal = (1,0,0)
  Source = -> Sketch106
FEATURE [Part::FeaturePython] Connect012  # WARN: FeaturePython — macro-defined, semantics opaque (R4)
  Objects = -> [Sketch106,Part__Mirroring027]
  Tolerance = 0
FEATURE [PartDesign::FeaturePython] Extend003  # WARN: FeaturePython — macro-defined, semantics opaque (R4)
  BaseFeature = -> BaseBend017
  Offset = 0.02
  Refine = true
  Suppressed = false
  UseSubtraction = false
  baseObject = -> BaseBend017 [Face1]
  gap1 = 0
  gap2 = 0
  length = 0
FEATURE [Part::FeaturePython] Placment024  # WARN: FeaturePython — macro-defined, semantics opaque (R4)
  AttacherType = Attacher::AttachEngine3D
  AttachmentOffset = pos=(0,0,0) rot=(0,1,0;1.5708rad)
  ExposePlacement = true
  MapMode = 7
  MarkerShape = 1
  MarkerSize = 10
  NumElements = 1
  Placement = pos=(0,120,0) rot=(1,0,0;1.5708rad)
  Type = lattice2AttachablePlacement.AttachablePlacement
  isLattice = 1
FEATURE [Sketcher::SketchObject] Sketch108
  FullyConstrained = true
  MapMode = 5
  Placement = pos=(0,0,0) rot=(0.57735,0.57735,0.57735;2.0944rad)
  sketch-geometry (11):
    g0: LineSegment StartX=0 StartY=0 StartZ=0 EndX=40 EndY=0 EndZ=0
    g1: LineSegment StartX=40 StartY=0 StartZ=0 EndX=40 EndY=70 EndZ=0
    g2: LineSegment StartX=40 StartY=70 StartZ=0 EndX=0 EndY=70 EndZ=0
    g3: LineSegment StartX=0 StartY=70 StartZ=0 EndX=0 EndY=0 EndZ=0
    g4: LineSegment StartX=50 StartY=0 StartZ=0 EndX=0 EndY=0 EndZ=0
    g5: LineSegment StartX=0 StartY=0 StartZ=0 EndX=0 EndY=80 EndZ=0
    g6: ArcOfCircle CenterX=10 CenterY=80 CenterZ=0 NormalX=0 NormalY=0 NormalZ=1 AngleXU=0 Radius=10 StartAngle=3.14159 EndAngle=4.71239
    g7: ArcOfCircle CenterX=50 CenterY=10 CenterZ=0 NormalX=0 NormalY=0 NormalZ=1 AngleXU=0 Radius=10 StartAngle=3.14159 EndAngle=4.71239
    g8: ArcOfCircle CenterX=-314.75 CenterY=10 CenterZ=0 NormalX=0 NormalY=0 NormalZ=1 AngleXU=0 Radius=354.75 StartAngle=2e-16 EndAngle=0.142615
    g9: ArcOfCircle CenterX=26.5 CenterY=59 CenterZ=0 NormalX=0 NormalY=0 NormalZ=1 AngleXU=0 Radius=10 StartAngle=0.142615 EndAngle=1.44973
    g10: ArcOfCircle CenterX=10 CenterY=-76.625 CenterZ=0 NormalX=0 NormalY=0 NormalZ=1 AngleXU=0 Radius=146.625 StartAngle=1.44973 EndAngle=1.5708
  constraints (28):
    c: Coincident(g0,g1)
    c: Coincident(g1,g2)
    c: Coincident(g2,g3)
    c: Coincident(g3,g0)
    c: Horizontal(g0)
    c: Horizontal(g2)
    c: Vertical(g1)
    c: Vertical(g3)
    c: Distance(g1,g3) = 40
    c: Distance(g0,g2) = 70
    c: Coincident(g0,g-1)
    c: PointOnObject(g4,g-1)
    c: Coincident(g4,g0)
    c: Coincident(g4,g5)
    c: PointOnObject(g5,g-2)
    c: Tangent(g6,g5) = 1.5708
    c: Tangent(g7,g4) = 1.5708
    c: Tangent(g8,g7) = 1.5708
    c: Tangent(g10,g6) = 1.5708
    c: Tangent(g10,g9) = -1.5708
    c: Tangent(g9,g8) = -1.5708
    c: Equal(g6,g7)
    c: Radius(g6) = 10
    c: Tangent(g7,g1) = 1.5708
    c: Tangent(g6,g2) = 1.5708
    c: Equal(g9,g6)
    c: DistanceX(g9) = 26.5
    c: DistanceY(g9) = 59
FEATURE [PartDesign::Pocket] Pocket031
  BaseFeature = -> Bend014
  Direction = (-1,0,0)
  Length = 5
  Length2 = 5
  Midplane = true
  Profile = -> Sketch108
  ReferenceAxis = -> Sketch108 [N_Axis]
  Suppressed = false
  Type = 1
FEATURE [Part::FeaturePython] Placment025  # WARN: FeaturePython — macro-defined, semantics opaque (R4)
  AttacherType = Attacher::AttachEngine3D
  AttachmentOffset = pos=(0,0,0) rot=(0,1,0;1.5708rad)
  ExposePlacement = true
  MapMode = 45
  MarkerShape = 1
  MarkerSize = 20
  NumElements = 1
  Placement = pos=(96.1933,46.198,0) rot=(0.57735,-0.57735,-0.57735;2.0944rad)
  Type = lattice2AttachablePlacement.AttachablePlacement
  isLattice = 1
FEATURE [Part::FeaturePython] Join016  # WARN: FeaturePython — macro-defined, semantics opaque (R4)
  ExposePlacement = false
  Interleave = false
  Links = -> [Placment025]
  MarkerShape = 1
  MarkerSize = 20
  NumElements = 1
  Type = lattice2JoinArrays.JoinArrays
  isLattice = 1
FEATURE [Part::FeaturePython] Mirror009  label="Mirror009 of Placment023"  # WARN: FeaturePython — macro-defined, semantics opaque (R4)
  ExposePlacement = false
  FlipX = true
  FlipY = false
  FlipZ = false
  MarkerShape = 1
  MarkerSize = 20
  NumElements = 1
  Object = -> Join016
  ObjectTraversal = 0
  Type = lattice2Mirror.LatticeMirror
  isLattice = 1
FEATURE [Part::FeaturePython] Join015  # WARN: FeaturePython — macro-defined, semantics opaque (R4)
  ExposePlacement = false
  Interleave = false
  Links = -> [Mirror009,Placment024,Join016]
  MarkerShape = 1
  MarkerSize = 0
  NumElements = 3
  Placement = pos=(0,0,15) rot=(0,0,1;0rad)
  Type = lattice2JoinArrays.JoinArrays
  isLattice = 1
FEATURE [Part::FeaturePython] Populate054  label="Populate Join015 with hole_3.4mm"  # WARN: FeaturePython — macro-defined, semantics opaque (R4)
  Copying = 0
  ExposePlacement = false
  MarkerShape = 1
  MarkerSize = 0
  NumElements = 0
  Object = -> Cylinder
  OutputCompounding = 1
  PlacementsTo = -> Join015
  Referencing = 0
  Type = lattice2PopulateCopies.LatticePopulateCopies
  isLattice = 0
FEATURE [Part::Compound] Compound036
  Links = -> [Populate054]
FEATURE [PartDesign::Boolean] Boolean028
  BaseFeature = -> Extend003
  Group = -> [Compound036]
  Suppressed = false
  Type = 1
  UsePlacement = true
FEATURE [PartDesign::Body] Body030  label="basin_shield_corrugation"
  Group = -> [Binder038,BaseBend017,Extend003,Boolean028]
  Origin = -> Origin032
  Tip = -> Boolean028
FEATURE [Sketcher::SketchObject] Sketch109
  AttachmentOffset = pos=(3,0,0) rot=(0,-1,0;1.5708rad)
  FullyConstrained = true
  MapMode = 7
  Placement = pos=(84.2649,79.2934,0) rot=(0.249244,0.684791,0.684791;2.65306rad)
  sketch-geometry (7):
    g0: LineSegment StartX=25 StartY=0 StartZ=0 EndX=115 EndY=0 EndZ=0
    g1: LineSegment StartX=115 StartY=0 StartZ=0 EndX=115 EndY=100 EndZ=0
    g2: LineSegment StartX=115 StartY=100 StartZ=0 EndX=25 EndY=100 EndZ=0
    g3: LineSegment StartX=25 StartY=70 StartZ=0 EndX=25 EndY=0 EndZ=0
    g4: LineSegment StartX=25 StartY=100 StartZ=0 EndX=25 EndY=75 EndZ=0
    g5: LineSegment StartX=25 StartY=70 StartZ=0 EndX=20 EndY=70 EndZ=0
    g6: ArcOfCircle CenterX=20 CenterY=75 CenterZ=0 NormalX=0 NormalY=0 NormalZ=1 AngleXU=0 Radius=5 StartAngle=4.71239 EndAngle=6.28319
  constraints (20):
    c: Coincident(g0,g1)
    c: Coincident(g1,g2)
    c: Coincident(g2,g4)
    c: Coincident(g3,g0)
    c: Horizontal(g0)
    c: Horizontal(g2)
    c: Vertical(g1)
    c: PointOnObject(g0,g-1)
    c: DistanceX(g0) = 25
    c: Vertical(g3)
    c: Vertical(g4)
    c: Coincident(g5,g3)
    c: Horizontal(g5)
    c: Vertical(g4,g3)
    c: Tangent(g6,g5) = 1.5708
    c: Radius(g6) = 5
    c: Tangent(g6,g4) = 1.5708
    c: DistanceY(g3) = 70
    c: DistanceY(g2) = 100
    c: DistanceX(g0) = 115
FEATURE [Part::Extrusion] Extrude028
  Base = -> Sketch109
  Dir = (0.642788,0.766044,0)
  DirMode = 2
  FaceMakerClass = Part::FaceMakerBullseye
  LengthFwd = 10
  LengthRev = 0
  Reversed = true
  Solid = true
  Symmetric = false
FEATURE [Part::Mirroring] Part__Mirroring028  label="Extrude028 (Mirror #26)"
  Base = (0,0,0)
  Normal = (1,0,0)
  Source = -> Extrude028
FEATURE [Part::MultiFuse] Fusion006
  Refine = true
  Shapes = -> [Part__Mirroring012,Body023,Part__Mirroring028,Extrude028]
FEATURE [Sketcher::SketchObject] Sketch110
  FullyConstrained = false
  sketch-geometry (1):
    g0: Circle CenterX=0 CenterY=234.99 CenterZ=0 NormalX=0 NormalY=0 NormalZ=1 AngleXU=0 Radius=1.7
  constraints (2):
    c: PointOnObject(g0,g-2)
    c: Diameter(g0) = 3.4
FEATURE [Part::Extrusion] Extrude029
  Base = -> Sketch110
  Dir = (0,0,1)
  DirMode = 2
  FaceMakerClass = Part::FaceMakerBullseye
  LengthFwd = 10
  LengthRev = 0
  Solid = true
  Symmetric = false
FEATURE [Part::MultiFuse] Fusion007
  Shapes = -> [Populate052,Extrude029]
FEATURE [Part::FeaturePython] Populate053  label="Populate Placment022 with Populate Join014 with hole_3.4mm"  # WARN: FeaturePython — macro-defined, semantics opaque (R4)
  Copying = 0
  ExposePlacement = false
  MarkerShape = 1
  MarkerSize = 0
  NumElements = 0
  Object = -> Fusion007
  OutputCompounding = 2
  PlacementsTo = -> Placment022
  Referencing = 0
  Type = lattice2PopulateCopies.LatticePopulateCopies
  isLattice = 0
FEATURE [Part::Compound] Compound032
  Links = -> [Populate053]
FEATURE [PartDesign::Boolean] Boolean024
  BaseFeature = -> Pocket031
  Group = -> [Compound032]
  Suppressed = false
  Type = 1
  UsePlacement = true
FEATURE [PartDesign::Body] Body026  label="basin_shield_wall"
  Group = -> [Binder034,BaseBend013,Extend002,Bend014,Sketch108,Pocket031,Boolean024]
  Origin = -> Origin028
  Tip = -> Boolean024
FEATURE [Part::Compound] Compound035
  Links = -> [Populate054,Fusion007]
FEATURE [PartDesign::Boolean] Boolean027
  BaseFeature = -> Bend015
  Group = -> [Compound035]
  Suppressed = false
  Type = 1
  UsePlacement = true
FEATURE [PartDesign::Body] Body027  label="basin_shield_top"
  Group = -> [Binder035,BaseBend014,Boolean023,Bend015,Boolean027]
  Origin = -> Origin029
  Tip = -> Boolean027
FEATURE [Sketcher::SketchObject] Sketch111
  ExternalGeometry = -> [Sketch090]
  FullyConstrained = true
  sketch-geometry (4):
    g0: LineSegment StartX=0 StartY=167 StartZ=0 EndX=48.5 EndY=167 EndZ=0
    g1: LineSegment StartX=53.5 StartY=162 StartZ=0 EndX=53.5 EndY=0 EndZ=0
    g2: ArcOfCircle CenterX=48.5 CenterY=162 CenterZ=0 NormalX=0 NormalY=0 NormalZ=1 AngleXU=0 Radius=5 StartAngle=2e-15 EndAngle=1.5708
    g3: GeomPoint X=53.5 Y=167 Z=0
  constraints (11):
    c: PointOnObject(g0,g-2)
    c: Horizontal(g0)
    c: PointOnObject(g1,g-1)
    c: Vertical(g1)
    c: PointOnObject(g3,g0)
    c: PointOnObject(g3,g1)
    c: Tangent(g0,g2) = 1.5708
    c: Tangent(g1,g2) = 1.5708
    c: DistanceX(g-3,g3) = 10
    c: DistanceY(g-3,g3) = 10
    c: Radius(g2) = 5
FEATURE [Part::Mirroring] Part__Mirroring029  label="Sketch111 (Mirror #27)"
  Base = (0,0,0)
  Normal = (1,0,0)
  Source = -> Sketch111
FEATURE [Part::Mirroring] Part__Mirroring030  label="Sketch111 (Mirror #28)"
  Base = (0,0,0)
  Normal = (0,1,0)
  Source = -> Sketch111
FEATURE [Part::FeaturePython] Mirror010  label="Mirror010 of Sketch111"  # WARN: FeaturePython — macro-defined, semantics opaque (R4)
  ExposePlacement = false
  FlipX = true
  FlipY = true
  FlipZ = false
  MarkerShape = 1
  MarkerSize = 0
  NumElements = 0
  Object = -> Sketch111
  ObjectTraversal = 0
  Type = lattice2Mirror.LatticeMirror
  isLattice = 0
FEATURE [Part::FeaturePython] Connect013  # WARN: FeaturePython — macro-defined, semantics opaque (R4)
  Objects = -> [Sketch111,Part__Mirroring029,Part__Mirroring030,Mirror010]
  Tolerance = 0
FEATURE [Part::FeaturePython] Placment026  # WARN: FeaturePython — macro-defined, semantics opaque (R4)
  AttacherType = Attacher::AttachEngine3D
  ExposePlacement = true
  MarkerShape = 1
  MarkerSize = 50
  NumElements = 1
  Placement = pos=(49,161,0) rot=(0,0,1;0rad)
  Type = lattice2AttachablePlacement.AttachablePlacement
  isLattice = 1
FEATURE [Part::FeaturePython] Mirror011  label="Mirror011 of Placment026"  # WARN: FeaturePython — macro-defined, semantics opaque (R4)
  ExposePlacement = false
  FlipX = true
  FlipY = false
  FlipZ = false
  MarkerShape = 1
  MarkerSize = 50
  NumElements = 1
  Object = -> Placment026
  ObjectTraversal = 0
  Type = lattice2Mirror.LatticeMirror
  isLattice = 1
FEATURE [Part::FeaturePython] Mirror012  label="Mirror012 of Placment026"  # WARN: FeaturePython — macro-defined, semantics opaque (R4)
  ExposePlacement = false
  FlipX = false
  FlipY = true
  FlipZ = false
  MarkerShape = 1
  MarkerSize = 50
  NumElements = 1
  Object = -> Placment026
  ObjectTraversal = 0
  Type = lattice2Mirror.LatticeMirror
  isLattice = 1
FEATURE [Part::FeaturePython] Mirror013  label="Mirror013 of Placment026"  # WARN: FeaturePython — macro-defined, semantics opaque (R4)
  ExposePlacement = false
  FlipX = true
  FlipY = true
  FlipZ = false
  MarkerShape = 1
  MarkerSize = 50
  NumElements = 1
  Object = -> Placment026
  ObjectTraversal = 0
  Type = lattice2Mirror.LatticeMirror
  isLattice = 1
FEATURE [PartDesign::SubShapeBinder] Binder039
  BindCopyOnChange = 0
  BindMode = 0
  ClaimChildren = false
  Context = -> Body031 [Binder039.]
  Fuse = false
  MakeFace = true
  OffsetFill = false
  OffsetIntersection = false
  OffsetJoinType = 0
  OffsetOpenResult = false
  PartialLoad = false
  Relative = true
  Support = -> [Connect013]
  _Version = 2
FEATURE [PartDesign::Pad] Pad022
  Direction = (0,0,1)
  Length = 1
  Length2 = 10
  Profile = -> Binder039
  Refine = true
  Suppressed = false
  Type = 0
FEATURE [Part::FeaturePython] Placment027  # WARN: FeaturePython — macro-defined, semantics opaque (R4)
  AttacherType = Attacher::AttachEngine3D
  ExposePlacement = true
  MarkerShape = 1
  MarkerSize = 50
  NumElements = 1
  Placement = pos=(49,0,0) rot=(0,0,1;0rad)
  Type = lattice2AttachablePlacement.AttachablePlacement
  isLattice = 1
  expr: .Placement.Base.x = <<Placment026>>.Placement.Base.x
FEATURE [Part::FeaturePython] Mirror014  label="Mirror014 of Placment027"  # WARN: FeaturePython — macro-defined, semantics opaque (R4)
  ExposePlacement = false
  FlipX = true
  FlipY = false
  FlipZ = false
  MarkerShape = 1
  MarkerSize = 50
  NumElements = 1
  Object = -> Placment027
  ObjectTraversal = 0
  Type = lattice2Mirror.LatticeMirror
  isLattice = 1
FEATURE [Part::FeaturePython] Join017  # WARN: FeaturePython — macro-defined, semantics opaque (R4)
  ExposePlacement = false
  Interleave = false
  Links = -> [Placment026,Mirror011,Mirror012,Mirror013,Placment027,Mirror014]
  MarkerShape = 1
  MarkerSize = 0
  NumElements = 6
  Type = lattice2JoinArrays.JoinArrays
  isLattice = 1
FEATURE [Part::FeaturePython] Populate055  label="Populate Join017 with hole_3.4mm"  # WARN: FeaturePython — macro-defined, semantics opaque (R4)
  Copying = 0
  ExposePlacement = false
  MarkerShape = 1
  MarkerSize = 0
  NumElements = 0
  Object = -> Cylinder
  OutputCompounding = 1
  PlacementsTo = -> Join017
  Referencing = 0
  Type = lattice2PopulateCopies.LatticePopulateCopies
  isLattice = 0
FEATURE [Part::FeaturePython] LinearArray012  # WARN: FeaturePython — macro-defined, semantics opaque (R4)
  Alignment = 0
  CellStart = A1
  Count = 15
  Dir = (0,1,0)
  DirIsDriven = true
  DistributionLaw = 0
  DrivenProperty = 1
  EndInclusive = true
  ExposePlacement = false
  GeneratorMode = 2
  MarkerShape = 1
  MarkerSize = 0
  NumElements = 15
  OrientMode = 0
  Placement = pos=(0,-140,0) rot=(0,0,1;0rad)
  Point = (0,0,0)
  PointIsDriven = true
  Reverse = false
  SpanEnd = 280
  SpanStart = 0
  Step = 20
  Type = lattice2LinearArray.LinearArray
  VSGVersion = 1
  Values = 0.0 | 20.0 | 40.0 | 60.0 | 80.0 | 100.0 | 120.0 | 140.0 | 160.0 | 180.0 | 200.0 | 220.0 | 240.0 | 260.0 | 280.0
  ValuesSource = 2
  isLattice = 1
  expr: .Placement.Base.y = -SpanEnd / 2
FEATURE [Sketcher::SketchObject] Sketch112
  FullyConstrained = true
  sketch-geometry (4):
    g0: ArcOfCircle CenterX=-35 CenterY=0 CenterZ=0 NormalX=0 NormalY=0 NormalZ=1 AngleXU=0 Radius=1.6 StartAngle=1.5708 EndAngle=4.71239
    g1: ArcOfCircle CenterX=35 CenterY=0 CenterZ=0 NormalX=0 NormalY=0 NormalZ=1 AngleXU=0 Radius=1.6 StartAngle=4.71239 EndAngle=7.85398
    g2: LineSegment StartX=-35 StartY=1.6 StartZ=0 EndX=35 EndY=1.6 EndZ=0
    g3: LineSegment StartX=-35 StartY=-1.6 StartZ=0 EndX=35 EndY=-1.6 EndZ=0
  constraints (9):
    c: Tangent(g0,g2) = 1.5708
    c: Tangent(g0,g3) = -1.5708
    c: Tangent(g1,g2) = 1.5708
    c: Tangent(g1,g3) = -1.5708
    c: Equal(g0,g1)
    c: PointOnObject(g0,g-1)
    c: Symmetric(g0,g1,g-2)
    c: DistanceX(g0,g1) = 70
    c: Diameter(g1) = 3.2
FEATURE [Part::Extrusion] Extrude030
  Base = -> Sketch112
  Dir = (0,0,1)
  DirMode = 2
  FaceMakerClass = Part::FaceMakerBullseye
  LengthFwd = 10
  LengthRev = 0
  Solid = true
  Symmetric = false
FEATURE [Part::FeaturePython] Populate056  label="Populate LinearArray012 with Extrude030"  # WARN: FeaturePython — macro-defined, semantics opaque (R4)
  Copying = 0
  ExposePlacement = false
  MarkerShape = 1
  MarkerSize = 0
  NumElements = 0
  Object = -> Extrude030
  OutputCompounding = 1
  PlacementsTo = -> LinearArray012
  Referencing = 0
  Type = lattice2PopulateCopies.LatticePopulateCopies
  isLattice = 0
FEATURE [Part::Compound] Compound037
  Links = -> [Populate055,Populate056]
FEATURE [PartDesign::Boolean] Boolean029
  BaseFeature = -> Pad022
  Group = -> [Compound037]
  Suppressed = false
  Type = 1
  UsePlacement = true
FEATURE [PartDesign::Body] Body031  label="Body"
  Group = -> [Binder039,Pad022,Boolean029]
  Origin = -> Origin033
  Tip = -> Boolean029
FEATURE [Part::Mirroring] Part__Mirroring031  label="Populate Populate LinearArray001 with LinearArray003 with hole_3.4mm (Mirror #29)"
  Base = (0,0,0)
  Normal = (1,0,0)
  Source = -> Populate013
FEATURE [Part::Compound] Compound012
  Links = -> [Populate013,Populate014,Part__Mirroring031]
FEATURE [PartDesign::Boolean] Boolean004
  BaseFeature = -> Pad008
  Group = -> [Compound012]
  Refine = true
  Suppressed = false
  Type = 1
  UsePlacement = true
FEATURE [PartDesign::Pocket] Pocket007
  BaseFeature = -> Boolean004
  Direction = (0,1,-2e-16)
  Length = 5
  Length2 = 5
  Profile = -> Sketch057
  ReferenceAxis = -> Sketch057 [N_Axis]
  Suppressed = false
  Type = 1
FEATURE [PartDesign::MultiTransform] MultiTransform
  BaseFeature = -> Pocket007
  Originals = -> [Pocket007]
  Suppressed = false
  Transformations = -> [Mirrored003,Mirrored004]
FEATURE [Sketcher::SketchObject] Sketch113
  AttachmentOffset = pos=(0,97,0) rot=(0,0,1;0rad)
  FullyConstrained = true
  MapMode = 5
  Placement = pos=(0,2.2e-14,97) rot=(1,0,0;1.5708rad)
  sketch-geometry (10):
    g0: LineSegment StartX=-18.1 StartY=-50 StartZ=0 EndX=-13 EndY=-50 EndZ=0
    g1: LineSegment StartX=-11 StartY=-48 StartZ=0 EndX=-11 EndY=48 EndZ=0
    g2: LineSegment StartX=-13 StartY=50 StartZ=0 EndX=-18.1 EndY=50 EndZ=0
    g3: LineSegment StartX=-20.1 StartY=48 StartZ=0 EndX=-20.1 EndY=-48 EndZ=0
    g4: ArcOfCircle CenterX=-18.1 CenterY=-48 CenterZ=0 NormalX=0 NormalY=0 NormalZ=1 AngleXU=0 Radius=2 StartAngle=3.14159 EndAngle=4.71239
    g5: ArcOfCircle CenterX=-13 CenterY=-48 CenterZ=0 NormalX=0 NormalY=0 NormalZ=1 AngleXU=0 Radius=2 StartAngle=4.71239 EndAngle=6.28319
    g6: ArcOfCircle CenterX=-13 CenterY=48 CenterZ=0 NormalX=0 NormalY=0 NormalZ=1 AngleXU=0 Radius=2 StartAngle=7e-16 EndAngle=1.5708
    g7: ArcOfCircle CenterX=-18.1 CenterY=48 CenterZ=0 NormalX=0 NormalY=0 NormalZ=1 AngleXU=0 Radius=2 StartAngle=1.5708 EndAngle=3.14159
    g8: GeomPoint X=-20.1 Y=-50 Z=0
    g9: GeomPoint X=-11 Y=50 Z=0
  constraints (23):
    c: Tangent(g0,g4) = -1.5708
    c: Tangent(g0,g5) = -1.5708
    c: Tangent(g1,g5) = -1.5708
    c: Tangent(g1,g6) = -1.5708
    c: Tangent(g2,g6) = -1.5708
    c: Tangent(g2,g7) = -1.5708
    c: Tangent(g3,g7) = -1.5708
    c: Tangent(g3,g4) = -1.5708
    c: Horizontal(g0)
    c: Horizontal(g2)
    c: Vertical(g1)
    c: Vertical(g3)
    c: Equal(g4,g5)
    c: Equal(g6,g7)
    c: PointOnObject(g8,g0)
    c: PointOnObject(g8,g3)
    c: PointOnObject(g9,g1)
    c: PointOnObject(g9,g2)
    c: DistanceX(g2) = -13
    c: DistanceX(g2) = -18.1
    c: Radius(g6) = 2
    c: Symmetric(g5,g6,g-1)
    c: DistanceY(g8,g9) = 100
FEATURE [PartDesign::Pocket] Pocket032
  BaseFeature = -> MultiTransform
  Direction = (0,1,-2e-16)
  Length = 5
  Length2 = 5
  Profile = -> Sketch113
  ReferenceAxis = -> Sketch113 [N_Axis]
  Suppressed = false
  Type = 1
FEATURE [PartDesign::LinearPattern] LinearPattern
  BaseFeature = -> Pocket032
  Direction = -> Sketch113 [V_Axis]
  Length = 1078.25
  Mode = 0
  Occurrences = 2
  Offset = 1078.25
  Originals = -> [Pocket032]
  Suppressed = false
  expr: Length = <<bar_pad>>.Length - <<Sketch113>>.AttachmentOffset.Base.y * 2
FEATURE [PartDesign::Body] Body005  label="bar"
  Group = -> [Binder008,Pad008,Boolean004,Local_CS016,Local_CS018,Sketch057,Pocket007,DatumPlane001,MultiTransform,Mirrored003,Mirrored004,Sketch058,Sketch113,Pocket032,LinearPattern]
  Origin = -> Origin006
  Tip = -> LinearPattern
FEATURE [TechDraw::DrawViewPart] View
  CoarseView = false
  Direction = (0,-1,0)
  Focus = 100
  HardHidden = false
  IsoCount = 0
  IsoHidden = false
  IsoVisible = false
  LockPosition = false
  Perspective = false
  Rotation = 90
  Scale = 0.2
  ScaleType = 2
  ScrubCount = 0
  SeamHidden = false
  SeamVisible = true
  SmoothHidden = false
  SmoothVisible = true
  Source = -> [Body005]
  X = 148.5
  XDirection = (1,0,0)
  Y = 185
FEATURE [TechDraw::DrawViewPart] View001
  CoarseView = false
  Direction = (0.57735,-0.57735,0.57735)
  Focus = 100
  HardHidden = false
  IsoCount = 0
  IsoHidden = false
  IsoVisible = false
  LockPosition = false
  Perspective = false
  Rotation = 90
  Scale = 0.25
  ScaleType = 2
  ScrubCount = 0
  SeamHidden = false
  SeamVisible = true
  SmoothHidden = false
  SmoothVisible = true
  Source = -> [Body005]
  X = 148.5
  XDirection = (0.707107,0.707107,0)
  Y = 115
FEATURE [TechDraw::DrawViewPart] View002
  CoarseView = false
  Direction = (0,0,1)
  Focus = 100
  HardHidden = false
  IsoCount = 0
  IsoHidden = false
  IsoVisible = false
  LockPosition = false
  Perspective = false
  Rotation = 0
  ScaleType = 0
  ScrubCount = 0
  SeamHidden = false
  SeamVisible = true
  SmoothHidden = false
  SmoothVisible = true
  Source = -> [Body005]
  X = 148.5
  XDirection = (1,0,0)
  Y = 35
FEATURE [TechDraw::DrawViewDimension] Dimension002
  AngleOverride = false
  Arbitrary = false
  ArbitraryTolerances = false
  EqualTolerance = true
  ExtensionAngle = 0
  FormatSpec = %.2w
  FormatSpecOverTolerance = %+.2w
  FormatSpecUnderTolerance = %+.2w
  Inverted = false
  LineAngle = 0
  LockPosition = false
  MeasureType = 1
  OverTolerance = 0
  References2D = -> [View002]
  Rotation = 0
  ScaleType = 0
  TheoreticalExact = false
  Type = 2
  UnderTolerance = 0
  X = 45.1185
  Y = 3.07494
FEATURE [TechDraw::DrawViewDimension] Dimension004
  AngleOverride = false
  Arbitrary = false
  ArbitraryTolerances = false
  EqualTolerance = true
  ExtensionAngle = 0
  FormatSpec = %.2w
  FormatSpecOverTolerance = %+.2w
  FormatSpecUnderTolerance = %+.2w
  Inverted = false
  LineAngle = 0
  LockPosition = false
  MeasureType = 1
  OverTolerance = 0
  References2D = -> [View002]
  Rotation = 0
  ScaleType = 0
  TheoreticalExact = false
  Type = 1
  UnderTolerance = 0
  X = -0.580213
  Y = 23.0526
FEATURE [TechDraw::DrawViewDimension] Dimension039
  AngleOverride = false
  Arbitrary = false
  ArbitraryTolerances = false
  BoxCorners = (2) [(-30,-8.5,-1e-07),(30,8.5,1e-07)]
  EqualTolerance = true
  ExtensionAngle = 0
  FormatSpec = %.2w
  FormatSpecOverTolerance = %+.2w
  FormatSpecUnderTolerance = %+.2w
  Inverted = false
  LineAngle = 0
  LockPosition = false
  MeasureType = 1
  OverTolerance = 0
  References2D = -> [View002]
  Rotation = 0
  ScaleType = 0
  TheoreticalExact = false
  Type = 0
  UnderTolerance = 0
  X = -0.466215
  Y = 34.5607
FEATURE [TechDraw::DrawViewDimension] Dimension040
  AngleOverride = false
  Arbitrary = false
  ArbitraryTolerances = false
  EqualTolerance = true
  ExtensionAngle = 0
  FormatSpec = R%.2w
  FormatSpecOverTolerance = %+.2w
  FormatSpecUnderTolerance = %+.2w
  Inverted = false
  LineAngle = 0
  LockPosition = false
  MeasureType = 1
  OverTolerance = 0
  References2D = -> [View002]
  Rotation = 0
  ScaleType = 0
  TheoreticalExact = false
  Type = 4
  UnderTolerance = 0
  X = -0.407273
  Y = 5.97333
FEATURE [TechDraw::DrawPage] Page
  KeepUpdated = true
  NextBalloonIndex = 1
  ProjectionType = 0
  Template = -> Template
  Views = -> [View,View001,View002,Dimension002,Dimension004,Dimension039,Dimension040]
FEATURE [Part::Feature] Unfold
  shape: bbox 720.7 x 0.5564 x 223 mm, 84 faces (baked)
FEATURE [Sketcher::SketchObject] Unfold_Sketch_bends
  FullyConstrained = false
  sketch-geometry (9):
    g0: LineSegment StartX=-130.132 StartY=318.805 StartZ=0 EndX=-2.3012 EndY=168.234 EndZ=0
    g1: LineSegment StartX=0.975152 StartY=159.422 StartZ=0 EndX=0.975152 EndY=142.82 EndZ=0
    g2: LineSegment StartX=0.975152 StartY=103.18 StartZ=0 EndX=0.975152 EndY=81.3195 EndZ=0
    g3: LineSegment StartX=0.975152 StartY=41.6805 StartZ=0 EndX=0.975152 EndY=19.8195 EndZ=0
    g4: LineSegment StartX=0.975152 StartY=-19.8195 StartZ=0 EndX=0.975152 EndY=-41.6805 EndZ=0
    g5: LineSegment StartX=0.975152 StartY=-81.3195 StartZ=0 EndX=0.975152 EndY=-103.18 EndZ=0
    g6: LineSegment StartX=-130.132 StartY=-318.805 StartZ=0 EndX=-2.2915 EndY=-168.222 EndZ=0
    g7: LineSegment StartX=-133.518 StartY=317.576 StartZ=0 EndX=-133.518 EndY=-317.576 EndZ=0
    g8: LineSegment StartX=0.975152 StartY=-142.82 StartZ=0 EndX=0.975152 EndY=-159.437 EndZ=0
FEATURE [Sketcher::SketchObject] Unfold_Sketch
  ExternalGeometry = -> [Unfold_Sketch_bends]
  FullyConstrained = false
  sketch-geometry (59):
    g0: LineSegment StartX=-140.957 StartY=-317.576 StartZ=0 EndX=-131.579 EndY=-317.576 EndZ=0
    g1: LineSegment StartX=-128.685 StartY=-320.034 StartZ=0 EndX=-131.579 EndY=-317.576 EndZ=0
    g2: LineSegment StartX=-90.3069 StartY=-359.745 StartZ=0 EndX=-128.685 EndY=-320.034 EndZ=0
    g3: ArcOfCircle CenterX=-88.8687 CenterY=-358.355 CenterZ=0 NormalX=0 NormalY=0 NormalZ=1 AngleXU=0.76833 Radius=2 StartAngle=3.14159 EndAngle=4.71239
    g4: LineSegment StartX=54.0624 StartY=-223.003 StartZ=0 EndX=-87.4789 EndY=-359.793 EndZ=0
    g5: ArcOfCircle CenterX=52.6725 CenterY=-221.565 CenterZ=0 NormalX=0 NormalY=0 NormalZ=1 AngleXU=0.76833 Radius=2 StartAngle=4.71239 EndAngle=6.28319
    g6: LineSegment StartX=4.05254 StartY=-168.378 StartZ=0 EndX=54.1107 EndY=-220.175 EndZ=0
    g7: LineSegment StartX=5.92419 StartY=-163.725 StartZ=0 EndX=78 EndY=-163.725 EndZ=0
    g8: ArcOfCircle CenterX=78 CenterY=-161.725 CenterZ=0 NormalX=0 NormalY=0 NormalZ=1 AngleXU=1.5708 Radius=2 StartAngle=3.14159 EndAngle=4.71239
    g9: LineSegment StartX=80 StartY=-161.725 StartZ=0 EndX=80 EndY=161.725 EndZ=0
    g10: ArcOfCircle CenterX=78 CenterY=161.725 CenterZ=0 NormalX=0 NormalY=0 NormalZ=1 AngleXU=1.5708 Radius=2 StartAngle=4.71239 EndAngle=6.28319
    g11: LineSegment StartX=78 StartY=163.725 StartZ=0 EndX=5.88592 EndY=163.725 EndZ=0
    g12: LineSegment StartX=4.02697 StartY=168.351 StartZ=0 EndX=54.1107 EndY=220.175 EndZ=0
    g13: ArcOfCircle CenterX=52.6725 CenterY=221.565 CenterZ=0 NormalX=0 NormalY=0 NormalZ=1 AngleXU=2.37326 Radius=2 StartAngle=3.14159 EndAngle=4.71239
    g14: LineSegment StartX=54.0624 StartY=223.003 StartZ=0 EndX=-87.4789 EndY=359.793 EndZ=0
    g15: ArcOfCircle CenterX=-88.8687 CenterY=358.355 CenterZ=0 NormalX=0 NormalY=0 NormalZ=1 AngleXU=2.37326 Radius=2 StartAngle=4.71239 EndAngle=6.28319
    g16: LineSegment StartX=-90.3069 StartY=359.745 StartZ=0 EndX=-128.685 EndY=320.034 EndZ=0
    g17: LineSegment StartX=-131.579 StartY=317.576 StartZ=0 EndX=-128.685 EndY=320.034 EndZ=0
    g18: LineSegment StartX=-140.957 StartY=317.576 StartZ=0 EndX=-131.579 EndY=317.576 EndZ=0
    g19: ArcOfCircle CenterX=-140.957 CenterY=315.576 CenterZ=0 NormalX=0 NormalY=0 NormalZ=1 AngleXU=1.5708 Radius=2 StartAngle=6.28318 EndAngle=7.85398
    g20: LineSegment StartX=-142.957 StartY=-315.576 StartZ=0 EndX=-142.957 EndY=315.576 EndZ=0
    g21: ArcOfCircle CenterX=-140.957 CenterY=-315.576 CenterZ=0 NormalX=0 NormalY=0 NormalZ=1 AngleXU=-1.5708 Radius=2 StartAngle=4.71239 EndAngle=6.28319
    g22: LineSegment StartX=2.9503 StartY=-17 StartZ=0 EndX=2.9503 EndY=17 EndZ=0
    g23: LineSegment StartX=-3.0497 StartY=-17 StartZ=0 EndX=-3.0497 EndY=17 EndZ=0
    g24: LineSegment StartX=2.9503 StartY=-140 StartZ=0 EndX=2.9503 EndY=-106 EndZ=0
    g25: LineSegment StartX=-3.0497 StartY=-140 StartZ=0 EndX=-3.0497 EndY=-106 EndZ=0
    g26: LineSegment StartX=2.9503 StartY=44.5 StartZ=0 EndX=2.9503 EndY=78.5 EndZ=0
    g27: LineSegment StartX=-3.0497 StartY=44.5 StartZ=0 EndX=-3.0497 EndY=78.5 EndZ=0
    g28: LineSegment StartX=2.9503 StartY=106 StartZ=0 EndX=2.9503 EndY=140 EndZ=0
    g29: LineSegment StartX=-3.0497 StartY=106 StartZ=0 EndX=-3.0497 EndY=140 EndZ=0
    g30: LineSegment StartX=2.9503 StartY=-78.5 StartZ=0 EndX=2.9503 EndY=-44.5 EndZ=0
    g31: LineSegment StartX=-3.0497 StartY=-78.5 StartZ=0 EndX=-3.0497 EndY=-44.5 EndZ=0
    g32: Circle CenterX=73 CenterY=0 CenterZ=0 NormalX=0 NormalY=0 NormalZ=-1 AngleXU=1.5708 Radius=1.7
    g33: Circle CenterX=47.0406 CenterY=220.054 CenterZ=0 NormalX=0 NormalY=0 NormalZ=-1 AngleXU=0.76833 Radius=1.7
    g34: Circle CenterX=-86.5908 CenterY=349.2 CenterZ=0 NormalX=0 NormalY=0 NormalZ=-1 AngleXU=0.76833 Radius=1.7
    g35: Circle CenterX=73 CenterY=-158.725 CenterZ=0 NormalX=0 NormalY=0 NormalZ=-1 AngleXU=-1.5708 Radius=1.7
    g36: Circle CenterX=73 CenterY=158.725 CenterZ=0 NormalX=0 NormalY=0 NormalZ=-1 AngleXU=1.5708 Radius=1.7
    g37: Circle CenterX=-86.5908 CenterY=-349.2 CenterZ=0 NormalX=0 NormalY=0 NormalZ=-1 AngleXU=-0.76833 Radius=1.7
    g38: Circle CenterX=47.0406 CenterY=-220.054 CenterZ=0 NormalX=0 NormalY=0 NormalZ=-1 AngleXU=-0.76833 Radius=1.7
    g39: Circle CenterX=21 CenterY=-158.725 CenterZ=0 NormalX=0 NormalY=0 NormalZ=-1 AngleXU=-1.5708 Radius=1.7
    g40: Circle CenterX=21 CenterY=158.725 CenterZ=0 NormalX=0 NormalY=0 NormalZ=-1 AngleXU=1.5708 Radius=1.7
    g41: ArcOfCircle CenterX=0.975152 CenterY=-164.437 CenterZ=0 NormalX=0 NormalY=0 NormalZ=1 AngleXU=0 Radius=5 StartAngle=0.142892 EndAngle=5.37538
    g42: ArcOfCircle CenterX=-0.0496964 CenterY=-140 CenterZ=0 NormalX=0 NormalY=0 NormalZ=1 AngleXU=0 Radius=3 StartAngle=3.14159 EndAngle=6.28319
    g43: ArcOfCircle CenterX=-0.0496964 CenterY=-106 CenterZ=0 NormalX=0 NormalY=0 NormalZ=1 AngleXU=0 Radius=3 StartAngle=2.3e-15 EndAngle=3.14159
    g44: ArcOfCircle CenterX=-0.0496964 CenterY=-78.5 CenterZ=0 NormalX=0 NormalY=0 NormalZ=1 AngleXU=0 Radius=3 StartAngle=3.14159 EndAngle=6.28319
    g45: ArcOfCircle CenterX=-0.0496964 CenterY=-44.5 CenterZ=0 NormalX=0 NormalY=0 NormalZ=1 AngleXU=0 Radius=3 StartAngle=9e-16 EndAngle=3.14159
    g46: ArcOfCircle CenterX=-0.0496964 CenterY=-17 CenterZ=0 NormalX=0 NormalY=0 NormalZ=1 AngleXU=0 Radius=3 StartAngle=3.14159 EndAngle=6.28319
    g47: ArcOfCircle CenterX=-0.0496964 CenterY=17 CenterZ=0 NormalX=0 NormalY=0 NormalZ=1 AngleXU=0 Radius=3 StartAngle=0 EndAngle=3.14159
    g48: ArcOfCircle CenterX=-0.0496964 CenterY=44.5 CenterZ=0 NormalX=0 NormalY=0 NormalZ=1 AngleXU=0 Radius=3 StartAngle=3.14159 EndAngle=6.28319
    g49: ArcOfCircle CenterX=-0.0496964 CenterY=78.5 CenterZ=0 NormalX=0 NormalY=0 NormalZ=1 AngleXU=0 Radius=3 StartAngle=0 EndAngle=3.14159
    g50: ArcOfCircle CenterX=-0.0496964 CenterY=106 CenterZ=0 NormalX=0 NormalY=0 NormalZ=1 AngleXU=0 Radius=3 StartAngle=3.14159 EndAngle=6.28319
    g51: ArcOfCircle CenterX=-0.0496964 CenterY=140 CenterZ=0 NormalX=0 NormalY=0 NormalZ=1 AngleXU=0 Radius=3 StartAngle=-1.8e-15 EndAngle=3.14159
    g52: ArcOfCircle CenterX=0.934762 CenterY=164.422 CenterZ=0 NormalX=0 NormalY=0 NormalZ=1 AngleXU=0 Radius=5 StartAngle=0.904038 EndAngle=6.14329
    g53: LineSegment StartX=-130.132 StartY=-318.805 StartZ=0 EndX=-128.838 EndY=-317.28 EndZ=0
    g54: LineSegment StartX=-3.58589 StartY=-169.747 StartZ=0 EndX=-2.2915 EndY=-168.222 EndZ=0
    g55: LineSegment StartX=0.975152 StartY=-159.437 StartZ=0 EndX=0.975152 EndY=-157.437 EndZ=0
    g56: LineSegment StartX=0.975152 StartY=157.422 StartZ=0 EndX=0.975152 EndY=159.422 EndZ=0
    g57: LineSegment StartX=-3.59559 StartY=169.759 StartZ=0 EndX=-2.3012 EndY=168.234 EndZ=0
    g58: LineSegment StartX=-130.132 StartY=318.805 StartZ=0 EndX=-128.838 EndY=317.28 EndZ=0
  constraints (82):
    c: Coincident(g20,g21)
    c: Coincident(g19,g20)
    c: Coincident(g0,g21)
    c: Coincident(g18,g19)
    c: Coincident(g0,g1)
    c: Coincident(g17,g18)
    c: Coincident(g1,g2)
    c: Coincident(g16,g17)
    c: Coincident(g2,g3)
    c: Coincident(g15,g16)
    c: Coincident(g3,g4)
    c: Coincident(g14,g15)
    c: Coincident(g4,g5)
    c: Coincident(g13,g14)
    c: Coincident(g5,g6)
    c: Coincident(g12,g13)
    c: Coincident(g7,g8)
    c: Coincident(g10,g11)
    c: Coincident(g8,g9)
    c: Coincident(g9,g10)
    c: Block(g11)
    c: Block(g12)
    c: Block(g6)
    c: Block(g7)
    c: Block(g24)
    c: Block(g25)
    c: Block(g30)
    c: Block(g31)
    c: Block(g22)
    c: Block(g23)
    c: Block(g26)
    c: Block(g27)
    c: Block(g28)
    c: Block(g29)
    c: Coincident(g41,g7)
    c: Coincident(g41,g6)
    c: Diameter(g41) = 10
    c: Coincident(g42,g25)
    c: Coincident(g43,g25)
    c: Coincident(g44,g31)
    c: Coincident(g45,g31)
    c: Coincident(g46,g23)
    c: Coincident(g47,g23)
    c: Coincident(g48,g27)
    c: Coincident(g49,g27)
    c: Coincident(g50,g29)
    c: Coincident(g51,g29)
    c: Coincident(g52,g12)
    c: Coincident(g52,g11)
    c: Equal(g52,g41)
    c: Tangent(g42,g24) = -1.5708
    c: Tangent(g43,g24) = -1.5708
    c: Tangent(g44,g30) = -1.5708
    c: Tangent(g45,g30) = -1.5708
    c: Tangent(g46,g22) = -1.5708
    c: Tangent(g47,g22) = -1.5708
    c: Tangent(g48,g26) = -1.5708
    c: Tangent(g49,g26) = -1.5708
    c: Tangent(g50,g28) = -1.5708
    c: Tangent(g51,g28) = -1.5708
    c: Coincident(g53,g-5)
    c: PointOnObject(g53,g-5)
    c: PointOnObject(g54,g-5)
    c: PointOnObject(g54,g41)
    c: PointOnObject(g-5,g54)
    c: PointOnObject(g55,g41)
    c: PointOnObject(g55,g-6)
    c: PointOnObject(g-6,g55)
    c: PointOnObject(g56,g-4)
    c: PointOnObject(g56,g52)
    c: PointOnObject(g-4,g56)
    c: PointOnObject(g57,g-3)
    c: PointOnObject(g57,g52)
    c: Coincident(g58,g-3)
    c: PointOnObject(g58,g-3)
    c: PointOnObject(g-3,g57)
    c: Equal(g58,g57)
    c: Equal(g57,g56)
    c: Equal(g56,g55)
    c: Equal(g55,g54)
    c: Equal(g54,g53)
    c: DistanceY(g55,g55) = 2
FEATURE [TechDraw::DrawViewDimension] Dimension041
  AngleOverride = false
  Arbitrary = false
  ArbitraryTolerances = false
  BoxCorners = (2) [(-67.3904,-39.7929,-1e-07),(67.3904,39.7926,1e-07)]
  EqualTolerance = true
  ExtensionAngle = 0
  FormatSpec = %.2w
  FormatSpecOverTolerance = %+.2w
  FormatSpecUnderTolerance = %+.2w
  Inverted = false
  LineAngle = 0
  LockPosition = false
  MeasureType = 1
  OverTolerance = 0
  References2D = -> [View011]
  Rotation = 0
  ScaleType = 0
  TheoreticalExact = false
  Type = 6
  UnderTolerance = 0
  X = -56.7343
  Y = 15.4932
FEATURE [TechDraw::DrawPage] Page002
  KeepUpdated = true
  NextBalloonIndex = 1
  ProjectionType = 0
  Template = -> Template
  Views = -> [View005,View011,View012,Dimension028,Dimension030,Dimension041]
FEATURE [App::DocumentObjectGroup] Group006  label="sink_unfolds_Group"
  Group = -> [Page002,Unfold,Unfold_Sketch,Unfold_Sketch_bends]
FEATURE [Part::Feature] Unfold011
  shape: bbox 87.71 x 1 x 1272 mm, 42 faces (baked)
FEATURE [Sketcher::SketchObject] Unfold_Sketch011
  FullyConstrained = false
  sketch-geometry (40):
    g0: ArcOfCircle CenterX=-1267.25 CenterY=-38.854 CenterZ=0 NormalX=0 NormalY=0 NormalZ=1 AngleXU=-1.5708 Radius=5 StartAngle=4.71239 EndAngle=6.28319
    g1: LineSegment StartX=-5 StartY=-43.854 StartZ=0 EndX=-1267.25 EndY=-43.854 EndZ=0
    g2: ArcOfCircle CenterX=-5 CenterY=-38.854 CenterZ=0 NormalX=0 NormalY=0 NormalZ=1 AngleXU=-1.5708 Radius=5 StartAngle=9.921e-13 EndAngle=1.5708
    g3: LineSegment StartX=0 StartY=38.854 StartZ=0 EndX=0 EndY=-38.854 EndZ=0
    g4: ArcOfCircle CenterX=-5 CenterY=38.854 CenterZ=0 NormalX=0 NormalY=0 NormalZ=1 AngleXU=1.5708 Radius=5 StartAngle=4.71239 EndAngle=6.28319
    g5: LineSegment StartX=-5 StartY=43.854 StartZ=0 EndX=-1267.25 EndY=43.854 EndZ=0
    g6: ArcOfCircle CenterX=-1267.25 CenterY=38.854 CenterZ=0 NormalX=0 NormalY=0 NormalZ=1 AngleXU=1.5708 Radius=5 StartAngle=9.921e-13 EndAngle=1.5708
    g7: LineSegment StartX=-1272.25 StartY=38.854 StartZ=0 EndX=-1272.25 EndY=-38.854 EndZ=0
    g8: ArcOfCircle CenterX=-1223.25 CenterY=-13 CenterZ=0 NormalX=0 NormalY=0 NormalZ=1 AngleXU=1.5708 Radius=2 StartAngle=0 EndAngle=1.5708
    g9: LineSegment StartX=-1127.25 StartY=-11 StartZ=0 EndX=-1223.25 EndY=-11 EndZ=0
    g10: ArcOfCircle CenterX=-1127.25 CenterY=-13 CenterZ=0 NormalX=0 NormalY=0 NormalZ=1 AngleXU=1.5708 Radius=2 StartAngle=4.71239 EndAngle=6.28319
    g11: LineSegment StartX=-1125.25 StartY=-31.954 StartZ=0 EndX=-1125.25 EndY=-13 EndZ=0
    g12: ArcOfCircle CenterX=-1127.25 CenterY=-31.954 CenterZ=0 NormalX=0 NormalY=0 NormalZ=1 AngleXU=1.5708 Radius=2 StartAngle=3.14159 EndAngle=4.71239
    g13: LineSegment StartX=-1223.25 StartY=-33.954 StartZ=0 EndX=-1127.25 EndY=-33.954 EndZ=0
    g14: ArcOfCircle CenterX=-1223.25 CenterY=-31.954 CenterZ=0 NormalX=0 NormalY=0 NormalZ=1 AngleXU=1.5708 Radius=2 StartAngle=1.5708 EndAngle=3.14159
    g15: LineSegment StartX=-1225.25 StartY=-13 StartZ=0 EndX=-1225.25 EndY=-31.954 EndZ=0
    g16: LineSegment StartX=-147 StartY=-13 StartZ=0 EndX=-147 EndY=-31.954 EndZ=0
    g17: ArcOfCircle CenterX=-145 CenterY=-13 CenterZ=0 NormalX=0 NormalY=0 NormalZ=1 AngleXU=1.5708 Radius=2 StartAngle=0 EndAngle=1.5708
    g18: LineSegment StartX=-49 StartY=-11 StartZ=0 EndX=-145 EndY=-11 EndZ=0
    g19: ArcOfCircle CenterX=-49 CenterY=-13 CenterZ=0 NormalX=0 NormalY=0 NormalZ=1 AngleXU=1.5708 Radius=2 StartAngle=4.71239 EndAngle=6.28319
    g20: LineSegment StartX=-47 StartY=-31.954 StartZ=0 EndX=-47 EndY=-13 EndZ=0
    g21: ArcOfCircle CenterX=-49 CenterY=-31.954 CenterZ=0 NormalX=0 NormalY=0 NormalZ=1 AngleXU=1.5708 Radius=2 StartAngle=3.14159 EndAngle=4.71239
    g22: LineSegment StartX=-145 StartY=-33.954 StartZ=0 EndX=-49 EndY=-33.954 EndZ=0
    g23: ArcOfCircle CenterX=-145 CenterY=-31.954 CenterZ=0 NormalX=0 NormalY=0 NormalZ=1 AngleXU=1.5708 Radius=2 StartAngle=1.5708 EndAngle=3.14159
    g24: Circle CenterX=-1113.51 CenterY=-37.854 CenterZ=0 NormalX=0 NormalY=0 NormalZ=1 AngleXU=0 Radius=1.7
    g25: Circle CenterX=-797.871 CenterY=-37.854 CenterZ=0 NormalX=0 NormalY=0 NormalZ=1 AngleXU=0 Radius=1.7
    g26: Circle CenterX=-797.871 CenterY=37.854 CenterZ=0 NormalX=0 NormalY=0 NormalZ=1 AngleXU=0 Radius=1.7
    g27: Circle CenterX=-1113.51 CenterY=37.854 CenterZ=0 NormalX=0 NormalY=0 NormalZ=1 AngleXU=0 Radius=1.7
    g28: Circle CenterX=-1260.25 CenterY=-9.5 CenterZ=0 NormalX=0 NormalY=0 NormalZ=-1 AngleXU=-1.5708 Radius=1.7
    g29: Circle CenterX=-1238.25 CenterY=-9.5 CenterZ=0 NormalX=0 NormalY=0 NormalZ=-1 AngleXU=-1.5708 Radius=1.7
    g30: Circle CenterX=-1260.25 CenterY=9.5 CenterZ=0 NormalX=0 NormalY=0 NormalZ=-1 AngleXU=-1.5708 Radius=1.7
    g31: Circle CenterX=-1238.25 CenterY=9.5 CenterZ=0 NormalX=0 NormalY=0 NormalZ=-1 AngleXU=-1.5708 Radius=1.7
    g32: Circle CenterX=-34 CenterY=-9.5 CenterZ=0 NormalX=0 NormalY=0 NormalZ=-1 AngleXU=1.5708 Radius=1.7
    g33: Circle CenterX=-34 CenterY=9.5 CenterZ=0 NormalX=0 NormalY=0 NormalZ=-1 AngleXU=1.5708 Radius=1.7
    g34: Circle CenterX=-12 CenterY=-9.5 CenterZ=0 NormalX=0 NormalY=0 NormalZ=-1 AngleXU=1.5708 Radius=1.7
    g35: Circle CenterX=-12 CenterY=9.5 CenterZ=0 NormalX=0 NormalY=0 NormalZ=-1 AngleXU=1.5708 Radius=1.7
    g36: Circle CenterX=-158.745 CenterY=-37.854 CenterZ=0 NormalX=0 NormalY=0 NormalZ=1 AngleXU=0 Radius=1.7
    g37: Circle CenterX=-474.38 CenterY=-37.854 CenterZ=0 NormalX=0 NormalY=0 NormalZ=1 AngleXU=0 Radius=1.7
    g38: Circle CenterX=-474.38 CenterY=37.854 CenterZ=0 NormalX=0 NormalY=0 NormalZ=1 AngleXU=0 Radius=1.7
    g39: Circle CenterX=-158.745 CenterY=37.854 CenterZ=0 NormalX=0 NormalY=0 NormalZ=1 AngleXU=0 Radius=1.7
FEATURE [Sketcher::SketchObject] Unfold_Sketch_Outline
  FullyConstrained = false
  sketch-geometry (8):
    g0: ArcOfCircle CenterX=-1267.25 CenterY=-38.854 CenterZ=0 NormalX=0 NormalY=0 NormalZ=1 AngleXU=-1.5708 Radius=5 StartAngle=4.71239 EndAngle=6.28319
    g1: LineSegment StartX=-5 StartY=-43.854 StartZ=0 EndX=-1267.25 EndY=-43.854 EndZ=0
    g2: ArcOfCircle CenterX=-5 CenterY=-38.854 CenterZ=0 NormalX=0 NormalY=0 NormalZ=1 AngleXU=-1.5708 Radius=5 StartAngle=9.921e-13 EndAngle=1.5708
    g3: LineSegment StartX=0 StartY=38.854 StartZ=0 EndX=0 EndY=-38.854 EndZ=0
    g4: ArcOfCircle CenterX=-5 CenterY=38.854 CenterZ=0 NormalX=0 NormalY=0 NormalZ=1 AngleXU=1.5708 Radius=5 StartAngle=4.71239 EndAngle=6.28319
    g5: LineSegment StartX=-5 StartY=43.854 StartZ=0 EndX=-1267.25 EndY=43.854 EndZ=0
    g6: ArcOfCircle CenterX=-1267.25 CenterY=38.854 CenterZ=0 NormalX=0 NormalY=0 NormalZ=1 AngleXU=1.5708 Radius=5 StartAngle=9.921e-13 EndAngle=1.5708
    g7: LineSegment StartX=-1272.25 StartY=38.854 StartZ=0 EndX=-1272.25 EndY=-38.854 EndZ=0
FEATURE [Sketcher::SketchObject] Unfold_Sketch_Internal
  FullyConstrained = false
  sketch-geometry (32):
    g0: LineSegment StartX=-147 StartY=-13 StartZ=0 EndX=-147 EndY=-31.954 EndZ=0
    g1: ArcOfCircle CenterX=-145 CenterY=-31.954 CenterZ=0 NormalX=0 NormalY=0 NormalZ=1 AngleXU=1.5708 Radius=2 StartAngle=1.5708 EndAngle=3.14159
    g2: LineSegment StartX=-145 StartY=-33.954 StartZ=0 EndX=-49 EndY=-33.954 EndZ=0
    g3: ArcOfCircle CenterX=-49 CenterY=-31.954 CenterZ=0 NormalX=0 NormalY=0 NormalZ=1 AngleXU=1.5708 Radius=2 StartAngle=3.14159 EndAngle=4.71239
    g4: LineSegment StartX=-47 StartY=-31.954 StartZ=0 EndX=-47 EndY=-13 EndZ=0
    g5: ArcOfCircle CenterX=-49 CenterY=-13 CenterZ=0 NormalX=0 NormalY=0 NormalZ=1 AngleXU=1.5708 Radius=2 StartAngle=4.71239 EndAngle=6.28319
    g6: LineSegment StartX=-49 StartY=-11 StartZ=0 EndX=-145 EndY=-11 EndZ=0
    g7: ArcOfCircle CenterX=-145 CenterY=-13 CenterZ=0 NormalX=0 NormalY=0 NormalZ=1 AngleXU=1.5708 Radius=2 StartAngle=0 EndAngle=1.5708
    g8: ArcOfCircle CenterX=-1223.25 CenterY=-13 CenterZ=0 NormalX=0 NormalY=0 NormalZ=1 AngleXU=1.5708 Radius=2 StartAngle=0 EndAngle=1.5708
    g9: LineSegment StartX=-1225.25 StartY=-13 StartZ=0 EndX=-1225.25 EndY=-31.954 EndZ=0
    g10: ArcOfCircle CenterX=-1223.25 CenterY=-31.954 CenterZ=0 NormalX=0 NormalY=0 NormalZ=1 AngleXU=1.5708 Radius=2 StartAngle=1.5708 EndAngle=3.14159
    g11: LineSegment StartX=-1223.25 StartY=-33.954 StartZ=0 EndX=-1127.25 EndY=-33.954 EndZ=0
    g12: ArcOfCircle CenterX=-1127.25 CenterY=-31.954 CenterZ=0 NormalX=0 NormalY=0 NormalZ=1 AngleXU=1.5708 Radius=2 StartAngle=3.14159 EndAngle=4.71239
    g13: LineSegment StartX=-1125.25 StartY=-31.954 StartZ=0 EndX=-1125.25 EndY=-13 EndZ=0
    g14: ArcOfCircle CenterX=-1127.25 CenterY=-13 CenterZ=0 NormalX=0 NormalY=0 NormalZ=1 AngleXU=1.5708 Radius=2 StartAngle=4.71239 EndAngle=6.28319
    g15: LineSegment StartX=-1127.25 StartY=-11 StartZ=0 EndX=-1223.25 EndY=-11 EndZ=0
    g16: Circle CenterX=-1113.51 CenterY=37.854 CenterZ=0 NormalX=0 NormalY=0 NormalZ=1 AngleXU=0 Radius=1.7
    g17: Circle CenterX=-797.871 CenterY=37.854 CenterZ=0 NormalX=0 NormalY=0 NormalZ=1 AngleXU=0 Radius=1.7
    g18: Circle CenterX=-797.871 CenterY=-37.854 CenterZ=0 NormalX=0 NormalY=0 NormalZ=1 AngleXU=0 Radius=1.7
    g19: Circle CenterX=-1113.51 CenterY=-37.854 CenterZ=0 NormalX=0 NormalY=0 NormalZ=1 AngleXU=0 Radius=1.7
    g20: Circle CenterX=-34 CenterY=9.5 CenterZ=0 NormalX=0 NormalY=0 NormalZ=-1 AngleXU=1.5708 Radius=1.7
    g21: Circle CenterX=-34 CenterY=-9.5 CenterZ=0 NormalX=0 NormalY=0 NormalZ=-1 AngleXU=1.5708 Radius=1.7
    g22: Circle CenterX=-12 CenterY=9.5 CenterZ=0 NormalX=0 NormalY=0 NormalZ=-1 AngleXU=1.5708 Radius=1.7
    g23: Circle CenterX=-12 CenterY=-9.5 CenterZ=0 NormalX=0 NormalY=0 NormalZ=-1 AngleXU=1.5708 Radius=1.7
    g24: Circle CenterX=-158.745 CenterY=37.854 CenterZ=0 NormalX=0 NormalY=0 NormalZ=1 AngleXU=0 Radius=1.7
    g25: Circle CenterX=-474.38 CenterY=37.854 CenterZ=0 NormalX=0 NormalY=0 NormalZ=1 AngleXU=0 Radius=1.7
    g26: Circle CenterX=-474.38 CenterY=-37.854 CenterZ=0 NormalX=0 NormalY=0 NormalZ=1 AngleXU=0 Radius=1.7
    g27: Circle CenterX=-158.745 CenterY=-37.854 CenterZ=0 NormalX=0 NormalY=0 NormalZ=1 AngleXU=0 Radius=1.7
    g28: Circle CenterX=-1238.25 CenterY=9.5 CenterZ=0 NormalX=0 NormalY=0 NormalZ=-1 AngleXU=-1.5708 Radius=1.7
    g29: Circle CenterX=-1260.25 CenterY=9.5 CenterZ=0 NormalX=0 NormalY=0 NormalZ=-1 AngleXU=-1.5708 Radius=1.7
    g30: Circle CenterX=-1238.25 CenterY=-9.5 CenterZ=0 NormalX=0 NormalY=0 NormalZ=-1 AngleXU=-1.5708 Radius=1.7
    g31: Circle CenterX=-1260.25 CenterY=-9.5 CenterZ=0 NormalX=0 NormalY=0 NormalZ=-1 AngleXU=-1.5708 Radius=1.7
FEATURE [Sketcher::SketchObject] Unfold_Sketch_bends011
  FullyConstrained = false
  sketch-geometry (8):
    g0: LineSegment StartX=-1272.25 StartY=-14.9635 StartZ=0 EndX=-1225.25 EndY=-14.9635 EndZ=0
    g1: LineSegment StartX=-1272.25 StartY=-29.8905 StartZ=0 EndX=-1225.25 EndY=-29.8905 EndZ=0
    g2: LineSegment StartX=-1125.25 StartY=-14.9635 StartZ=0 EndX=-147 EndY=-14.9635 EndZ=0
    g3: LineSegment StartX=-1125.25 StartY=-29.8905 StartZ=0 EndX=-147 EndY=-29.8905 EndZ=0
    g4: LineSegment StartX=-47 StartY=-29.8905 StartZ=0 EndX=0 EndY=-29.8905 EndZ=0
    g5: LineSegment StartX=-47 StartY=-14.9635 StartZ=0 EndX=0 EndY=-14.9635 EndZ=0
    g6: LineSegment StartX=-1272.25 StartY=29.8905 StartZ=0 EndX=0 EndY=29.8905 EndZ=0
    g7: LineSegment StartX=-1272.25 StartY=14.9635 StartZ=0 EndX=0 EndY=14.9635 EndZ=0
FEATURE [App::DocumentObjectGroup] Group004  label="bar_unfolds_Group"
  Group = -> [Page,Unfold011,Unfold_Sketch011,Unfold_Sketch_Outline,Unfold_Sketch_Internal,Unfold_Sketch_bends011]
FEATURE [TechDraw::DrawViewDimension] Dimension042  label="Dimension3D042"
  AngleOverride = true
  Arbitrary = true
  ArbitraryTolerances = false
  BoxCorners = (2) [(-25.8345,-30.4658,-1e-07),(25.8345,30.4658,1e-07)]
  EqualTolerance = true
  ExtensionAngle = 30
  FormatSpec = 50
  FormatSpecOverTolerance = %+.2w
  FormatSpecUnderTolerance = %+.2w
  Inverted = false
  LineAngle = 150
  LockPosition = false
  MeasureType = 1
  OverTolerance = 0
  References2D = -> [View003]
  Rotation = 0
  ScaleType = 0
  TheoreticalExact = false
  Type = 0
  UnderTolerance = 0
  X = -17.7544
  Y = -19.821
FEATURE [TechDraw::DrawViewDimension] Dimension043  label="Dimension3D043"
  AngleOverride = true
  Arbitrary = true
  ArbitraryTolerances = false
  BoxCorners = (2) [(-25.8345,-30.4658,-1e-07),(25.8345,30.4658,1e-07)]
  EqualTolerance = true
  ExtensionAngle = 30
  FormatSpec = 40
  FormatSpecOverTolerance = %+.2w
  FormatSpecUnderTolerance = %+.2w
  Inverted = false
  LineAngle = 90
  LockPosition = false
  MeasureType = 1
  OverTolerance = 0
  References2D = -> [View003]
  Rotation = 0
  ScaleType = 0
  TheoreticalExact = false
  Type = 0
  UnderTolerance = 0
  X = -39.5465
  Y = 1.60005
FEATURE [TechDraw::DrawPage] Page001
  KeepUpdated = true
  NextBalloonIndex = 1
  ProjectionType = 0
  Template = -> Template
  Views = -> [View003,View004,Dimension042,Dimension043]
FEATURE [App::DocumentObjectGroup] Group005  label="bar_fix_unfolds_Group"
  Group = -> [Page001,Unfold007,Unfold_Sketch007,Unfold_Sketch_Outline006,Unfold_Sketch_Internal006,Unfold_Sketch_bends007]
FEATURE [PartDesign::FeaturePython] Bend016  # WARN: FeaturePython — macro-defined, semantics opaque (R4)
  AutoMiter = false
  BaseFeature = -> Pad010
  BendType = 0
  LengthList = [26]
  LengthSpec = 0
  ReliefFactor = 0.7
  Suppressed = false
  UseReliefFactor = false
  angle = 90
  baseObject = -> Pad010 [Edge25]
  bendAList = [90]
  extend1 = 2
  extend2 = 2
  gap1 = 0
  gap2 = 0
  invert = true
  kfactor = 0.5
  length = 26
  maxExtendDist = 5
  minGap = 0.2
  minReliefGap = 1
  miterangle1 = -35
  miterangle2 = 0
  offset = 0
  radius = 1
  reliefType = 0
  reliefd = 1
  reliefw = 0.8
  sketchflip = false
  sketchinvert = false
  unfold = false
  expr: miterangle1 = -<<sink_back_base_Sketch>>.Constraints.angle
FEATURE [Sketcher::SketchObject] Sketch114
  AttachmentOffset = pos=(0,0,205) rot=(0,0,1;0rad)
  AttachmentSupport = -> [YZ_Plane008]
  ExternalGeometry = -> [Sketch043]
  FullyConstrained = true
  MapMode = 5
  Placement = pos=(205,0,0) rot=(0.57735,0.57735,0.57735;2.0944rad)
  expr: Constraints[23] = 90 deg - <<sink_back_base_Sketch>>.Constraints.angle
  sketch-geometry (10):
    g0: LineSegment StartX=-1 StartY=0 StartZ=0 EndX=-1 EndY=-30 EndZ=0
    g1: LineSegment StartX=38.7813 StartY=-30 StartZ=0 EndX=38.7813 EndY=0 EndZ=0
    g2: LineSegment StartX=38.7813 StartY=0 StartZ=0 EndX=-1 EndY=0 EndZ=0
    g3: LineSegment StartX=-1 StartY=-30 StartZ=0 EndX=-0.5 EndY=-30 EndZ=0
    g4: LineSegment StartX=37.7813 StartY=-30 StartZ=0 EndX=38.7813 EndY=-30 EndZ=0
    g5: LineSegment StartX=-0.5 StartY=-30 StartZ=0 EndX=-0.5 EndY=-32 EndZ=0
    g6: LineSegment StartX=1.5 StartY=-30 StartZ=0 EndX=33.9394 EndY=-30 EndZ=0
    g7: LineSegment StartX=35.5777 StartY=-33.1472 StartZ=0 EndX=37.7813 EndY=-30 EndZ=0
    g8: ArcOfCircle CenterX=1.5 CenterY=-32 CenterZ=0 NormalX=0 NormalY=0 NormalZ=1 AngleXU=0 Radius=2 StartAngle=1.5708 EndAngle=3.14159
    g9: ArcOfCircle CenterX=33.9394 CenterY=-32 CenterZ=0 NormalX=0 NormalY=0 NormalZ=1 AngleXU=0 Radius=2 StartAngle=5.67232 EndAngle=7.85398
  constraints (30):
    c: Coincident(g0,g3)
    c: Coincident(g4,g1)
    c: Coincident(g1,g2)
    c: Coincident(g2,g0)
    c: Vertical(g0)
    c: Vertical(g1)
    c: Horizontal(g2)
    c: PointOnObject(g0,g-1)
    c: DistanceX(g0) = -1
    c: DistanceY(g4) = -30
    c: DistanceX(g1) = 38.7813
    c: Coincident(g3,g5)
    c: Horizontal(g3)
    c: Coincident(g7,g4)
    c: Horizontal(g4)
    c: Horizontal(g6)
    c: Horizontal(g0,g6)
    c: Vertical(g5)
    c: Tangent(g8,g5) = -1.5708
    c: Tangent(g8,g6) = 1.5708
    c: DistanceX(g3) = -0.5
    c: Tangent(g9,g6) = 1.5708
    c: Tangent(g9,g7) = -1.5708
    c: Angle(g7) = 0.959931
    c: Equal(g9,g8)
    c: Radius(g9) = 2
    c: Horizontal(g6,g1)
    c: DistanceX(g4) = 37.7813
    c: DistanceX(g4,g4) = 1
    c: DistanceX(g-3,g4) = 0.0252
FEATURE [PartDesign::Pocket] Pocket033
  BaseFeature = -> Bend016
  Direction = (-1,0,0)
  Length = 5
  Length2 = 5
  Profile = -> Sketch114
  ReferenceAxis = -> Sketch114 [N_Axis]
  Reversed = true
  Suppressed = false
  Type = 0
FEATURE [PartDesign::Pad] Pad011
  BaseFeature = -> Pocket033
  Direction = (0.996988,-0.0635308,0.0444847)
  Length = 515.751
  Length2 = 10
  Profile = -> Sketch043
  ReferenceAxis = -> Sketch043 [N_Axis]
  Reversed = true
  Suppressed = false
  Type = 0
  expr: Length = Sketch041.Constraints.end
FEATURE [PartDesign::Pocket] Pocket011
  BaseFeature = -> Pad011
  Direction = (0,1,-2e-16)
  Length = 5
  Length2 = 5
  Midplane = true
  Profile = -> Sketch061
  ReferenceAxis = -> Sketch061 [N_Axis]
  Suppressed = false
  Type = 1
FEATURE [PartDesign::Pocket] Pocket012
  BaseFeature = -> Pocket011
  Direction = (-0.0775567,-0.816685,0.571849)
  Length = 5
  Length2 = 5
  Profile = -> Sketch062
  ReferenceAxis = -> Sketch062 [N_Axis]
  Reversed = true
  Suppressed = false
  Type = 1
FEATURE [PartDesign::Pocket] Pocket013
  BaseFeature = -> Pocket012
  Direction = (0,1,-2e-16)
  Length = 5
  Length2 = 5
  Midplane = true
  Profile = -> Sketch063
  ReferenceAxis = -> Sketch063 [N_Axis]
  Suppressed = false
  Type = 1
FEATURE [PartDesign::Boolean] Boolean007
  BaseFeature = -> Pocket013
  Group = -> [Compound015]
  Suppressed = false
  Type = 1
  UsePlacement = true
FEATURE [PartDesign::Body] Body007  label="sink_back"
  Group = -> [Local_CS020,Binder010,Sketch041,Sketch042,Sketch043,Pad009,Pad010,Bend016,Sketch114,Pocket033,Pad011,Sketch061,Pocket011,Sketch062,Pocket012,Sketch063,Pocket013,Boolean007]
  Origin = -> Origin008
  Tip = -> Boolean007
FEATURE [TechDraw::DrawViewPart] View008
  CoarseView = false
  Direction = (0,1,0)
  Focus = 100
  HardHidden = false
  IsoCount = 0
  IsoHidden = false
  IsoVisible = false
  LockPosition = false
  Perspective = false
  Rotation = 0
  Scale = 0.5
  ScaleType = 1
  ScrubCount = 0
  SeamHidden = false
  SeamVisible = true
  SmoothHidden = false
  SmoothVisible = true
  Source = -> [Body007]
  X = 148.5
  XDirection = (-1,0,0)
  Y = 165
FEATURE [Part::Mirroring] Part__Mirroring023  label="sink_back (Mirror #21)"
  Base = (0,0,0)
  Normal = (1,0,0)
  Source = -> Body007
FEATURE [TechDraw::DrawViewPart] View018
  CoarseView = false
  Direction = (-1,0,0)
  Focus = 100
  HardHidden = false
  IsoCount = 0
  IsoHidden = false
  IsoVisible = false
  LockPosition = false
  Perspective = false
  Rotation = 0
  ScaleType = 0
  ScrubCount = 0
  SeamHidden = false
  SeamVisible = true
  SmoothHidden = false
  SmoothVisible = true
  Source = -> [Part__Mirroring023]
  X = 48.5
  XDirection = (0,-1,0)
  Y = 67
FEATURE [TechDraw::DrawViewPart] View020
  CoarseView = false
  Direction = (0,1,0)
  Focus = 100
  HardHidden = false
  IsoCount = 0
  IsoHidden = false
  IsoVisible = false
  LockPosition = false
  Perspective = false
  Rotation = 0
  Scale = 0.5
  ScaleType = 2
  ScrubCount = 0
  SeamHidden = false
  SeamVisible = true
  SmoothHidden = false
  SmoothVisible = true
  Source = -> [Part__Mirroring023]
  X = 148.5
  XDirection = (-1,0,0)
  Y = 162
FEATURE [Sketcher::SketchObject] Unfold_Sketch013
  FullyConstrained = false
  sketch-geometry (74):
    g0: LineSegment StartX=-53.5 StartY=-162 StartZ=0 EndX=-53.5 EndY=162 EndZ=0
    g1: ArcOfCircle CenterX=-48.5 CenterY=-162 CenterZ=0 NormalX=0 NormalY=0 NormalZ=1 AngleXU=-3.14159 Radius=5 StartAngle=2.7e-15 EndAngle=1.5708
    g2: ArcOfCircle CenterX=-48.5 CenterY=162 CenterZ=0 NormalX=0 NormalY=0 NormalZ=1 AngleXU=-3.14159 Radius=5 StartAngle=4.71239 EndAngle=6.28319
    g3: LineSegment StartX=48.5 StartY=-167 StartZ=0 EndX=-48.5 EndY=-167 EndZ=0
    g4: LineSegment StartX=-48.5 StartY=167 StartZ=0 EndX=48.5 EndY=167 EndZ=0
    g5: ArcOfCircle CenterX=48.5 CenterY=-162 CenterZ=0 NormalX=0 NormalY=0 NormalZ=1 AngleXU=0 Radius=5 StartAngle=4.71239 EndAngle=6.28319
    g6: ArcOfCircle CenterX=48.5 CenterY=162 CenterZ=0 NormalX=0 NormalY=0 NormalZ=1 AngleXU=0 Radius=5 StartAngle=2.7e-15 EndAngle=1.5708
    g7: LineSegment StartX=53.5 StartY=162 StartZ=0 EndX=53.5 EndY=-162 EndZ=0
    g8: Circle CenterX=-49 CenterY=-161 CenterZ=0 NormalX=0 NormalY=0 NormalZ=-1 AngleXU=0 Radius=1.7
    g9: LineSegment StartX=35 StartY=-141.6 StartZ=0 EndX=-35 EndY=-141.6 EndZ=0
    g10: ArcOfCircle CenterX=35 CenterY=-140 CenterZ=0 NormalX=0 NormalY=0 NormalZ=1 AngleXU=0 Radius=1.6 StartAngle=4.71239 EndAngle=7.85398
    g11: LineSegment StartX=35 StartY=-138.4 StartZ=0 EndX=-35 EndY=-138.4 EndZ=0
    g12: ArcOfCircle CenterX=-35 CenterY=-140 CenterZ=0 NormalX=0 NormalY=0 NormalZ=1 AngleXU=0 Radius=1.6 StartAngle=1.5708 EndAngle=4.71239
    g13: LineSegment StartX=35 StartY=-121.6 StartZ=0 EndX=-35 EndY=-121.6 EndZ=0
    g14: ArcOfCircle CenterX=35 CenterY=-120 CenterZ=0 NormalX=0 NormalY=0 NormalZ=1 AngleXU=0 Radius=1.6 StartAngle=4.71239 EndAngle=7.85398
    g15: LineSegment StartX=35 StartY=-118.4 StartZ=0 EndX=-35 EndY=-118.4 EndZ=0
    g16: ArcOfCircle CenterX=-35 CenterY=-120 CenterZ=0 NormalX=0 NormalY=0 NormalZ=1 AngleXU=0 Radius=1.6 StartAngle=1.5708 EndAngle=4.71239
    g17: LineSegment StartX=35 StartY=-101.6 StartZ=0 EndX=-35 EndY=-101.6 EndZ=0
    g18: ArcOfCircle CenterX=35 CenterY=-100 CenterZ=0 NormalX=0 NormalY=0 NormalZ=1 AngleXU=0 Radius=1.6 StartAngle=4.71239 EndAngle=7.85398
    g19: LineSegment StartX=35 StartY=-98.4 StartZ=0 EndX=-35 EndY=-98.4 EndZ=0
    g20: ArcOfCircle CenterX=-35 CenterY=-100 CenterZ=0 NormalX=0 NormalY=0 NormalZ=1 AngleXU=0 Radius=1.6 StartAngle=1.5708 EndAngle=4.71239
    g21: Circle CenterX=49 CenterY=-161 CenterZ=0 NormalX=0 NormalY=0 NormalZ=-1 AngleXU=-3.14159 Radius=1.7
    g22: LineSegment StartX=35 StartY=-81.6 StartZ=0 EndX=-35 EndY=-81.6 EndZ=0
    g23: ArcOfCircle CenterX=35 CenterY=-80 CenterZ=0 NormalX=0 NormalY=0 NormalZ=1 AngleXU=0 Radius=1.6 StartAngle=4.71239 EndAngle=7.85398
    g24: LineSegment StartX=35 StartY=-78.4 StartZ=0 EndX=-35 EndY=-78.4 EndZ=0
    g25: ArcOfCircle CenterX=-35 CenterY=-80 CenterZ=0 NormalX=0 NormalY=0 NormalZ=1 AngleXU=0 Radius=1.6 StartAngle=1.5708 EndAngle=4.71239
    g26: LineSegment StartX=35 StartY=-61.6 StartZ=0 EndX=-35 EndY=-61.6 EndZ=0
    g27: ArcOfCircle CenterX=35 CenterY=-60 CenterZ=0 NormalX=0 NormalY=0 NormalZ=1 AngleXU=0 Radius=1.6 StartAngle=4.71239 EndAngle=7.85398
    g28: LineSegment StartX=35 StartY=-58.4 StartZ=0 EndX=-35 EndY=-58.4 EndZ=0
    g29: ArcOfCircle CenterX=-35 CenterY=-60 CenterZ=0 NormalX=0 NormalY=0 NormalZ=1 AngleXU=0 Radius=1.6 StartAngle=1.5708 EndAngle=4.71239
    g30: LineSegment StartX=35 StartY=-41.6 StartZ=0 EndX=-35 EndY=-41.6 EndZ=0
    g31: ArcOfCircle CenterX=35 CenterY=-40 CenterZ=0 NormalX=0 NormalY=0 NormalZ=1 AngleXU=0 Radius=1.6 StartAngle=4.71239 EndAngle=7.85398
    g32: LineSegment StartX=35 StartY=-38.4 StartZ=0 EndX=-35 EndY=-38.4 EndZ=0
    g33: ArcOfCircle CenterX=-35 CenterY=-40 CenterZ=0 NormalX=0 NormalY=0 NormalZ=1 AngleXU=0 Radius=1.6 StartAngle=1.5708 EndAngle=4.71239
    g34: LineSegment StartX=35 StartY=-21.6 StartZ=0 EndX=-35 EndY=-21.6 EndZ=0
    g35: ArcOfCircle CenterX=35 CenterY=-20 CenterZ=0 NormalX=0 NormalY=0 NormalZ=1 AngleXU=0 Radius=1.6 StartAngle=4.71239 EndAngle=7.85398
    g36: LineSegment StartX=35 StartY=-18.4 StartZ=0 EndX=-35 EndY=-18.4 EndZ=0
    g37: ArcOfCircle CenterX=-35 CenterY=-20 CenterZ=0 NormalX=0 NormalY=0 NormalZ=1 AngleXU=0 Radius=1.6 StartAngle=1.5708 EndAngle=4.71239
    g38: Circle CenterX=-49 CenterY=0 CenterZ=0 NormalX=0 NormalY=0 NormalZ=-1 AngleXU=0 Radius=1.7
    g39: Circle CenterX=-49 CenterY=161 CenterZ=0 NormalX=0 NormalY=0 NormalZ=-1 AngleXU=0 Radius=1.7
    g40: LineSegment StartX=35 StartY=-1.6 StartZ=0 EndX=-35 EndY=-1.6 EndZ=0
    g41: ArcOfCircle CenterX=35 CenterY=0 CenterZ=0 NormalX=0 NormalY=0 NormalZ=1 AngleXU=0 Radius=1.6 StartAngle=4.71239 EndAngle=7.85398
    g42: LineSegment StartX=35 StartY=1.6 StartZ=0 EndX=-35 EndY=1.6 EndZ=0
    g43: ArcOfCircle CenterX=-35 CenterY=0 CenterZ=0 NormalX=0 NormalY=0 NormalZ=1 AngleXU=0 Radius=1.6 StartAngle=1.5708 EndAngle=4.71239
    g44: LineSegment StartX=35 StartY=18.4 StartZ=0 EndX=-35 EndY=18.4 EndZ=0
    g45: ArcOfCircle CenterX=35 CenterY=20 CenterZ=0 NormalX=0 NormalY=0 NormalZ=1 AngleXU=0 Radius=1.6 StartAngle=4.71239 EndAngle=7.85398
    g46: LineSegment StartX=35 StartY=21.6 StartZ=0 EndX=-35 EndY=21.6 EndZ=0
    g47: ArcOfCircle CenterX=-35 CenterY=20 CenterZ=0 NormalX=0 NormalY=0 NormalZ=1 AngleXU=0 Radius=1.6 StartAngle=1.5708 EndAngle=4.71239
    g48: LineSegment StartX=35 StartY=38.4 StartZ=0 EndX=-35 EndY=38.4 EndZ=0
    g49: ArcOfCircle CenterX=35 CenterY=40 CenterZ=0 NormalX=0 NormalY=0 NormalZ=1 AngleXU=0 Radius=1.6 StartAngle=4.71239 EndAngle=7.85398
    g50: LineSegment StartX=35 StartY=41.6 StartZ=0 EndX=-35 EndY=41.6 EndZ=0
    g51: ArcOfCircle CenterX=-35 CenterY=40 CenterZ=0 NormalX=0 NormalY=0 NormalZ=1 AngleXU=0 Radius=1.6 StartAngle=1.5708 EndAngle=4.71239
    g52: LineSegment StartX=35 StartY=58.4 StartZ=0 EndX=-35 EndY=58.4 EndZ=0
    g53: ArcOfCircle CenterX=35 CenterY=60 CenterZ=0 NormalX=0 NormalY=0 NormalZ=1 AngleXU=0 Radius=1.6 StartAngle=4.71239 EndAngle=7.85398
    g54: LineSegment StartX=35 StartY=61.6 StartZ=0 EndX=-35 EndY=61.6 EndZ=0
    g55: ArcOfCircle CenterX=-35 CenterY=60 CenterZ=0 NormalX=0 NormalY=0 NormalZ=1 AngleXU=0 Radius=1.6 StartAngle=1.5708 EndAngle=4.71239
    g56: LineSegment StartX=35 StartY=78.4 StartZ=0 EndX=-35 EndY=78.4 EndZ=0
    g57: ArcOfCircle CenterX=35 CenterY=80 CenterZ=0 NormalX=0 NormalY=0 NormalZ=1 AngleXU=0 Radius=1.6 StartAngle=4.71239 EndAngle=7.85398
    g58: LineSegment StartX=35 StartY=81.6 StartZ=0 EndX=-35 EndY=81.6 EndZ=0
    g59: ArcOfCircle CenterX=-35 CenterY=80 CenterZ=0 NormalX=0 NormalY=0 NormalZ=1 AngleXU=0 Radius=1.6 StartAngle=1.5708 EndAngle=4.71239
    g60: Circle CenterX=49 CenterY=0 CenterZ=0 NormalX=0 NormalY=0 NormalZ=-1 AngleXU=-3.14159 Radius=1.7
    g61: LineSegment StartX=35 StartY=98.4 StartZ=0 EndX=-35 EndY=98.4 EndZ=0
    g62: ArcOfCircle CenterX=35 CenterY=100 CenterZ=0 NormalX=0 NormalY=0 NormalZ=1 AngleXU=0 Radius=1.6 StartAngle=4.71239 EndAngle=7.85398
    g63: LineSegment StartX=35 StartY=101.6 StartZ=0 EndX=-35 EndY=101.6 EndZ=0
    g64: ArcOfCircle CenterX=-35 CenterY=100 CenterZ=0 NormalX=0 NormalY=0 NormalZ=1 AngleXU=0 Radius=1.6 StartAngle=1.5708 EndAngle=4.71239
    g65: LineSegment StartX=35 StartY=118.4 StartZ=0 EndX=-35 EndY=118.4 EndZ=0
    g66: ArcOfCircle CenterX=35 CenterY=120 CenterZ=0 NormalX=0 NormalY=0 NormalZ=1 AngleXU=0 Radius=1.6 StartAngle=4.71239 EndAngle=7.85398
    g67: LineSegment StartX=35 StartY=121.6 StartZ=0 EndX=-35 EndY=121.6 EndZ=0
    g68: ArcOfCircle CenterX=-35 CenterY=120 CenterZ=0 NormalX=0 NormalY=0 NormalZ=1 AngleXU=0 Radius=1.6 StartAngle=1.5708 EndAngle=4.71239
    g69: LineSegment StartX=35 StartY=138.4 StartZ=0 EndX=-35 EndY=138.4 EndZ=0
    g70: ArcOfCircle CenterX=35 CenterY=140 CenterZ=0 NormalX=0 NormalY=0 NormalZ=1 AngleXU=0 Radius=1.6 StartAngle=4.71239 EndAngle=7.85398
    g71: LineSegment StartX=35 StartY=141.6 StartZ=0 EndX=-35 EndY=141.6 EndZ=0
    g72: ArcOfCircle CenterX=-35 CenterY=140 CenterZ=0 NormalX=0 NormalY=0 NormalZ=1 AngleXU=0 Radius=1.6 StartAngle=1.5708 EndAngle=4.71239
    g73: Circle CenterX=49 CenterY=161 CenterZ=0 NormalX=0 NormalY=0 NormalZ=-1 AngleXU=-3.14159 Radius=1.7
FEATURE [TechDraw::DrawViewPart] View021
  CoarseView = false
  Direction = (-0.57735,0.57735,0.57735)
  Focus = 100
  HardHidden = false
  IsoCount = 0
  IsoHidden = false
  IsoVisible = false
  LockPosition = false
  Perspective = false
  Rotation = 90
  Scale = 0.35
  ScaleType = 2
  ScrubCount = 0
  SeamHidden = false
  SeamVisible = true
  SmoothHidden = false
  SmoothVisible = true
  Source = -> [Body012]
  X = 148.5
  XDirection = (-0.707107,-0.707107,0)
  Y = 165
FEATURE [TechDraw::DrawViewBalloon] Balloon
  BubbleShape = 3
  EndType = 0
  EndTypeScale = 1
  KinkLength = 5
  LockPosition = false
  OriginX = 9.87065
  OriginY = 5.35045
  Rotation = 0
  ScaleType = 0
  ShapeScale = 1
  SourceView = -> View021
  Text = Оборотная сторона
  TextWrapLen = -1
  X = 145.227
  Y = 60.9445
FEATURE [TechDraw::DrawViewBalloon] Balloon001
  BubbleShape = 3
  EndType = 0
  EndTypeScale = 1
  KinkLength = 5
  LockPosition = false
  OriginX = 45.7716
  OriginY = -9.88963
  Rotation = 0
  ScaleType = 0
  ShapeScale = 1
  SourceView = -> View021
  Text = Лицевая сторона
  TextWrapLen = -1
  X = 159.445
  Y = -92.1377
FEATURE [TechDraw::DrawViewDimension] Dimension051
  AngleOverride = false
  Arbitrary = false
  ArbitraryTolerances = false
  BoxCorners = (2) [(-36.6972,-12.85,-1e-07),(36.6972,12.85,1e-07)]
  EqualTolerance = true
  ExtensionAngle = 0
  FormatSpec = %.2w
  FormatSpecOverTolerance = %+.2w
  FormatSpecUnderTolerance = %+.2w
  Inverted = false
  LineAngle = 0
  LockPosition = false
  MeasureType = 1
  OverTolerance = 0
  References2D = -> [View013]
  Rotation = 0
  ScaleType = 0
  TheoreticalExact = false
  Type = 0
  UnderTolerance = 0
  X = -1.39356
  Y = -16.5141
FEATURE [TechDraw::DrawViewDimension] Dimension052
  AngleOverride = false
  Arbitrary = false
  ArbitraryTolerances = false
  BoxCorners = (2) [(-36.6972,-12.85,-1e-07),(36.6972,12.85,1e-07)]
  EqualTolerance = true
  ExtensionAngle = 0
  FormatSpec = %.2w
  FormatSpecOverTolerance = %+.2w
  FormatSpecUnderTolerance = %+.2w
  Inverted = false
  LineAngle = 0
  LockPosition = false
  MeasureType = 1
  OverTolerance = 0
  References2D = -> [View013]
  Rotation = 0
  ScaleType = 0
  TheoreticalExact = false
  Type = 0
  UnderTolerance = 0
  X = 41.6655
  Y = -6.39334
FEATURE [TechDraw::DrawPage] Page004  label="lamp_fix_Page"
  KeepUpdated = true
  NextBalloonIndex = 4
  ProjectionType = 0
  Template = -> Template
  Views = -> [View013,Dimension009,Dimension022,View021,Balloon,Balloon001,Dimension051,Dimension052]
FEATURE [App::DocumentObjectGroup] Group008  label="lamp_fix_Group"
  Group = -> [Page004,Unfold009,Unfold_Sketch009,Unfold_Sketch_Outline007,Unfold_Sketch_Internal007,Unfold_Sketch_bends009]
FEATURE [TechDraw::DrawViewPart] View022
  CoarseView = false
  Direction = (1,0,0)
  Focus = 100
  HardHidden = false
  IsoCount = 0
  IsoHidden = false
  IsoVisible = false
  LockPosition = false
  Perspective = false
  Rotation = 0
  ScaleType = 0
  ScrubCount = 0
  SeamHidden = false
  SeamVisible = true
  SmoothHidden = false
  SmoothVisible = true
  Source = -> [Boolean007]
  X = 68.5
  XDirection = (0,1,0)
  Y = 65
FEATURE [TechDraw::DrawViewPart] View023
  CoarseView = false
  Direction = (0.996988,-0.0635308,0.0444847)
  Focus = 100
  HardHidden = false
  IsoCount = 0
  IsoHidden = false
  IsoVisible = false
  LockPosition = false
  Perspective = false
  Rotation = 0
  ScaleType = 0
  ScrubCount = 0
  SeamHidden = false
  SeamVisible = true
  SmoothHidden = false
  SmoothVisible = true
  Source = -> [Boolean007]
  X = 228.5
  XDirection = (0,1,0)
  Y = 62
FEATURE [Sketcher::SketchObject] Sketch115
  ExternalGeometry = -> [Sketch021]
  FullyConstrained = true
  Placement = pos=(0,0,0.4) rot=(0,0,1;0rad)
  sketch-geometry (2):
    g0: LineSegment StartX=163.286 StartY=8.2 StartZ=0 EndX=177.953 EndY=8.2 EndZ=0
    g1: LineSegment StartX=177.953 StartY=8.2 StartZ=0 EndX=200.934 EndY=27.4836 EndZ=0
  constraints (7):
    c: Horizontal(g0)
    c: Coincident(g0,g1)
    c: Parallel(g1,g-3)
    c: Distance(g1,g-3) = 3
    c: PointOnObject(g-3,g0)
    c: Distance(g1) = 30
    c: DistanceX(g0,g-3) = 10
FEATURE [Sketcher::SketchObject] Sketch116
  ExternalGeometry = -> [Sketch021]
  FullyConstrained = true
  Placement = pos=(0,0,0.4) rot=(0,0,1;0rad)
  sketch-geometry (3):
    g0: LineSegment StartX=302.163 StartY=150 StartZ=0 EndX=312.163 EndY=150 EndZ=0
    g1: LineSegment StartX=312.163 StartY=150 StartZ=0 EndX=312.163 EndY=120.815 EndZ=0
    g2: LineSegment StartX=312.163 StartY=120.815 StartZ=0 EndX=296.842 EndY=107.96 EndZ=0
  constraints (9):
    c: PointOnObject(g0,g-4)
    c: Coincident(g0,g-4)
    c: Coincident(g0,g1)
    c: Vertical(g1)
    c: Coincident(g1,g2)
    c: Parallel(g2,g-3)
    c: Distance(g1,g-3) = 3
    c: DistanceX(g0,g0) = 10
    c: Distance(g2) = 20
FEATURE [Part::FeaturePython] BaseBend018  # WARN: FeaturePython — macro-defined, semantics opaque (R4)
  BendSide = 1
  BendSketch = -> Sketch115
  MidPlane = false
  Reverse = false
  length = 15
  radius = 0.1
  thickness = 0.3
FEATURE [Part::FeaturePython] BaseBend019  # WARN: FeaturePython — macro-defined, semantics opaque (R4)
  BendSide = 0
  BendSketch = -> Sketch116
  MidPlane = false
  Reverse = false
  length = 15
  radius = 0.1
  thickness = 0.3
FEATURE [Part::Mirroring] Part__Mirroring032  label="Sketch115 (Mirror #30)"
  Base = (0,0,0)
  Normal = (1,0,0)
  Source = -> Sketch115
FEATURE [Part::Mirroring] Part__Mirroring033  label="Sketch116 (Mirror #31)"
  Base = (0,0,0)
  Normal = (1,0,0)
  Source = -> Sketch116
FEATURE [Part::FeaturePython] BaseBend020  # WARN: FeaturePython — macro-defined, semantics opaque (R4)
  BendSide = 0
  BendSketch = -> Part__Mirroring032
  MidPlane = false
  Reverse = false
  length = 15
  radius = 0.1
  thickness = 0.3
FEATURE [Part::FeaturePython] BaseBend021  # WARN: FeaturePython — macro-defined, semantics opaque (R4)
  BendSide = 1
  BendSketch = -> Part__Mirroring033
  MidPlane = false
  Reverse = false
  length = 15
  radius = 0.1
  thickness = 0.3
FEATURE [Part::Compound] Compound038
  Links = -> [BaseBend018,BaseBend019,BaseBend020,BaseBend021]
FEATURE [Sketcher::SketchObject] Sketch118
  ExternalGeometry = -> [Sketch021]
  FullyConstrained = true
  sketch-geometry (8):
    g0: LineSegment StartX=172.194 StartY=11.2 StartZ=0 EndX=172.194 EndY=8.6 EndZ=0
    g1: LineSegment StartX=172.194 StartY=8.6 StartZ=0 EndX=173.763 EndY=8.6 EndZ=0
    g2: LineSegment StartX=173.763 StartY=8.6 StartZ=0 EndX=174.122 EndY=8.90187 EndZ=0
    g3: LineSegment StartX=174.122 StartY=8.90187 StartZ=0 EndX=172.194 EndY=11.2 EndZ=0
    g4: LineSegment StartX=173.286 StartY=8.2 StartZ=0 EndX=177.953 EndY=8.2 EndZ=0
    g5: LineSegment StartX=172.194 StartY=11.2 StartZ=0 EndX=174.096 EndY=12.7963 EndZ=0
    g6: LineSegment StartX=174.096 StartY=12.7963 StartZ=0 EndX=176.025 EndY=10.4981 EndZ=0
    g7: LineSegment StartX=176.025 StartY=10.4981 StartZ=0 EndX=174.122 EndY=8.90187 EndZ=0
  constraints (23):
    c: Vertical(g0)
    c: Coincident(g0,g1)
    c: Horizontal(g1)
    c: PointOnObject(g2,g-3)
    c: Coincident(g2,g3)
    c: Coincident(g3,g0)
    c: Horizontal(g4)
    c: Distance(g4,g-3) = 3
    c: Coincident(g0,g5)
    c: Coincident(g5,g6)
    c: PointOnObject(g6,g-3)
    c: Coincident(g6,g7)
    c: Coincident(g7,g2)
    c: PointOnObject(g4,g6)
    c: Perpendicular(g7,g6)
    c: Perpendicular(g5,g6)
    c: DistanceY(g0,g0) = 2.6
    c: Parallel(g3,g6)
    c: Coincident(g4,g-3)
    c: PointOnObject(g2,g-3)
    c: Coincident(g1,g2)
    c: DistanceY(g4,g0) = 0.4
    c: Distance(g3) = 3
FEATURE [Sketcher::SketchObject] Sketch119
  AttachmentOffset = pos=(0,0,0) rot=(0,1,0;1.5708rad)
  AttachmentSupport = -> [Sketch021]
  FullyConstrained = true
  MapMode = 7
  Placement = pos=(173.286,8.2,0) rot=(0.889126,0.323616,0.323616;1.68804rad)
  sketch-geometry (5):
    g0: LineSegment StartX=6 StartY=0 StartZ=0 EndX=6 EndY=0.4 EndZ=0
    g1: LineSegment StartX=6 StartY=0.4 StartZ=0 EndX=53.1934 EndY=40 EndZ=0
    g2: LineSegment StartX=53.1934 StartY=40 StartZ=0 EndX=0 EndY=40 EndZ=0
    g3: LineSegment StartX=0 StartY=40 StartZ=0 EndX=0 EndY=0 EndZ=0
    g4: LineSegment StartX=0 StartY=0 StartZ=0 EndX=6 EndY=0 EndZ=0
  constraints (14):
    c: PointOnObject(g0,g-1)
    c: Vertical(g0)
    c: Coincident(g0,g1)
    c: Coincident(g1,g2)
    c: PointOnObject(g2,g-2)
    c: Horizontal(g2)
    c: Coincident(g2,g3)
    c: Coincident(g3,g-1)
    c: Coincident(g3,g4)
    c: Coincident(g4,g0)
    c: Angle(g1) = 0.698132
    c: DistanceY(g0) = 0.4
    c: DistanceY(g2) = 40
    c: DistanceX(g0) = 6
FEATURE [Part::Extrusion] Extrude033
  Base = -> Sketch119
  Dir = (0.642788,-0.766044,2e-16)
  DirMode = 2
  FaceMakerClass = Part::FaceMakerBullseye
  LengthFwd = 0.5
  LengthRev = 0
  Reversed = true
  Solid = true
  Symmetric = false
FEATURE [Part::Mirroring] Part__Mirroring034  label="Extrude033 (Mirror #32)"
  Base = (0,0,0)
  Normal = (1,0,0)
  Source = -> Extrude033
FEATURE [Part::Compound] Compound039
  Links = -> [Extrude033,Part__Mirroring034]
FEATURE [PartDesign::Boolean] Boolean031
  BaseFeature = -> Mirrored
  Group = -> [Compound039]
  Suppressed = false
  Type = 1
  UsePlacement = true
FEATURE [PartDesign::Boolean] Boolean030
  BaseFeature = -> Boolean031
  Group = -> [Compound038]
  Refine = true
  Suppressed = false
  Type = 0
  UsePlacement = true
FEATURE [PartDesign::Boolean] Boolean002
  BaseFeature = -> Boolean030
  Group = -> [Compound009]
  Suppressed = false
  Type = 1
  UsePlacement = true
FEATURE [PartDesign::Body] Body002  label="dropper_fix_composit"
  Group = -> [Binder003,BaseBend001,Extend001,Sketch031,Bend001,Pocket003,Mirrored,Boolean031,Boolean030,Boolean002,Local_CS008,Local_CS013]
  Origin = -> Origin003
  Tip = -> Boolean002
FEATURE [App::DocumentObjectGroup] Group  label="parts"
  Group = -> [Link001,Body003,Body002,Body004,Body005,Body006,Body007,Part,Body009,Body010,Body012,Body013,Body017,Body018,Body019,Body020,Body021,Body025,Body026,Body027,Body030,Body031]
FEATURE [TechDraw::DrawViewDimension] Dimension
  AngleOverride = false
  Arbitrary = false
  ArbitraryTolerances = false
  BoxCorners = (2) [(-35.6221,-51.0333,-1e-07),(35.6221,51.0333,1e-07)]
  EqualTolerance = true
  ExtensionAngle = 0
  FormatSpec = %.2w
  FormatSpecOverTolerance = %+.2w
  FormatSpecUnderTolerance = %+.2w
  Inverted = false
  LineAngle = 0
  LockPosition = false
  MeasureType = 1
  OverTolerance = 0
  References2D = -> [View023]
  Rotation = 0
  ScaleType = 0
  TheoreticalExact = false
  Type = 0
  UnderTolerance = 0
  X = 30.845
  Y = -41.1206
FEATURE [TechDraw::DrawViewDimension] Dimension053
  AngleOverride = false
  Arbitrary = false
  ArbitraryTolerances = false
  BoxCorners = (2) [(-35.5652,-54.3694,-1e-07),(35.5652,54.3694,1e-07)]
  EqualTolerance = true
  ExtensionAngle = 0
  FormatSpec = %.2w
  FormatSpecOverTolerance = %+.2w
  FormatSpecUnderTolerance = %+.2w
  Inverted = false
  LineAngle = 0
  LockPosition = false
  MeasureType = 1
  OverTolerance = 0
  References2D = -> [View022]
  Rotation = 0
  ScaleType = 0
  TheoreticalExact = false
  Type = 0
  UnderTolerance = 0
  X = -48.3395
  Y = 21.3522
FEATURE [TechDraw::DrawViewPart] View024
  CoarseView = false
  Direction = (-0.996988,-0.0635308,0.0444847)
  Focus = 100
  HardHidden = false
  IsoCount = 0
  IsoHidden = false
  IsoVisible = false
  LockPosition = false
  Perspective = false
  Rotation = 0
  ScaleType = 0
  ScrubCount = 0
  SeamHidden = false
  SeamVisible = true
  SmoothHidden = false
  SmoothVisible = true
  Source = -> [Part__Mirroring023]
  X = 177.5
  XDirection = (0.063594,-0.997976,2.0307e-08)
  Y = 64
FEATURE [Part::Feature] Unfold014
  shape: bbox 539.1 x 0.5 x 163 mm, 27 faces (baked)
FEATURE [Sketcher::SketchObject] Unfold_Sketch_Outline011
  FullyConstrained = false
  sketch-geometry (23):
    g0: ArcOfCircle CenterX=-83.7611 CenterY=201.381 CenterZ=0 NormalX=0 NormalY=0 NormalZ=1 AngleXU=1.49316 Radius=5 StartAngle=0 EndAngle=1.5708
    g1: LineSegment StartX=-88.746 StartY=201.769 StartZ=0 EndX=-127.97 EndY=-302.459 EndZ=0
    g2: ArcOfCircle CenterX=-122.986 CenterY=-302.847 CenterZ=0 NormalX=0 NormalY=0 NormalZ=1 AngleXU=1.49316 Radius=5 StartAngle=1.5708 EndAngle=3.14159
    g3: LineSegment StartX=-101.119 StartY=-309.563 StartZ=0 EndX=-123.373 EndY=-307.832 EndZ=0
    g4: LineSegment StartX=-101.119 StartY=-309.563 StartZ=0 EndX=4.5 EndY=-309.563 EndZ=0
    g5: ArcOfCircle CenterX=4.5 CenterY=-307.063 CenterZ=0 NormalX=0 NormalY=0 NormalZ=1 AngleXU=1.5708 Radius=2.5 StartAngle=3.14159 EndAngle=4.71239
    g6: LineSegment StartX=7 StartY=-307.063 StartZ=0 EndX=7 EndY=-167.135 EndZ=0
    g7: ArcOfCircle CenterX=9.5 CenterY=-167.135 CenterZ=0 NormalX=0 NormalY=0 NormalZ=1 AngleXU=1.5708 Radius=2.5 StartAngle=0 EndAngle=1.5708
    g8: LineSegment StartX=9.5 StartY=-164.635 StartZ=0 EndX=32.5 EndY=-164.635 EndZ=0
    g9: ArcOfCircle CenterX=32.5 CenterY=-162.135 CenterZ=0 NormalX=0 NormalY=0 NormalZ=1 AngleXU=1.5708 Radius=2.5 StartAngle=3.14159 EndAngle=4.71239
    g10: LineSegment StartX=35 StartY=-162.135 StartZ=0 EndX=35 EndY=199.635 EndZ=0
    g11: ArcOfCircle CenterX=30 CenterY=199.635 CenterZ=0 NormalX=0 NormalY=0 NormalZ=1 AngleXU=1.5708 Radius=5 StartAngle=4.71239 EndAngle=6.28319
    g12: LineSegment StartX=-36.1187 StartY=204.635 StartZ=0 EndX=30 EndY=204.635 EndZ=0
    g13: LineSegment StartX=-36.1187 StartY=204.635 StartZ=0 EndX=-36.1187 EndY=206.599 EndZ=0
    g14: LineSegment StartX=-36.1187 StartY=206.599 StartZ=0 EndX=-34.1187 EndY=206.599 EndZ=0
    g15: LineSegment StartX=-34.1187 StartY=206.599 StartZ=0 EndX=-32.5901 EndY=208.782 EndZ=0
    g16: ArcOfCircle CenterX=-34.5856 CenterY=208.916 CenterZ=0 NormalX=0 NormalY=0 NormalZ=1 AngleXU=2.53073 Radius=2 StartAngle=3.68502 EndAngle=4.71239
    g17: LineSegment StartX=-33.4384 StartY=210.555 StartZ=0 EndX=-60.0112 EndY=229.161 EndZ=0
    g18: ArcOfCircle CenterX=-61.1583 CenterY=227.523 CenterZ=0 NormalX=0 NormalY=0 NormalZ=1 AngleXU=2.53073 Radius=2 StartAngle=4.71239 EndAngle=6.69463
    g19: LineSegment StartX=-63.1187 StartY=227.919 StartZ=0 EndX=-63.1187 EndY=206.599 EndZ=0
    g20: LineSegment StartX=-63.1187 StartY=206.599 StartZ=0 EndX=-61.1187 EndY=206.599 EndZ=0
    g21: LineSegment StartX=-61.1187 StartY=206.599 StartZ=0 EndX=-61.1187 EndY=204.635 EndZ=0
    g22: LineSegment StartX=-83.3733 StartY=206.366 StartZ=0 EndX=-61.1187 EndY=204.635 EndZ=0
FEATURE [Sketcher::SketchObject] Unfold_Sketch_Internal011
  FullyConstrained = false
  sketch-geometry (2):
    g0: Circle CenterX=21 CenterY=-158.725 CenterZ=0 NormalX=0 NormalY=0 NormalZ=1 AngleXU=-1.5708 Radius=1.7
    g1: Circle CenterX=21 CenterY=158.725 CenterZ=0 NormalX=0 NormalY=0 NormalZ=1 AngleXU=1.5708 Radius=1.7
FEATURE [Sketcher::SketchObject] Unfold_Sketch_bends014
  FullyConstrained = false
  sketch-geometry (3):
    g0: LineSegment StartX=-36.1187 StartY=205.617 StartZ=0 EndX=-61.1187 EndY=205.617 EndZ=0
    g1: LineSegment StartX=-102.881 StartY=-309.426 StartZ=0 EndX=-62.8805 EndY=204.772 EndZ=0
    g2: LineSegment StartX=-35.0388 StartY=204.635 StartZ=0 EndX=-35.0388 EndY=-309.563 EndZ=0
FEATURE [Sketcher::SketchObject] Unfold_Sketch015  label="sink_back_Unfold_Sketch"
  ExternalGeometry = -> [Unfold_Sketch_bends014]
  FullyConstrained = false
  sketch-geometry (29):
    g0: ArcOfCircle CenterX=-83.7611 CenterY=201.381 CenterZ=0 NormalX=0 NormalY=0 NormalZ=1 AngleXU=1.49316 Radius=5 StartAngle=0 EndAngle=1.5708
    g1: LineSegment StartX=-88.746 StartY=201.769 StartZ=0 EndX=-127.97 EndY=-302.459 EndZ=0
    g2: ArcOfCircle CenterX=-122.986 CenterY=-302.847 CenterZ=0 NormalX=0 NormalY=0 NormalZ=1 AngleXU=1.49316 Radius=5 StartAngle=1.5708 EndAngle=3.14159
    g3: LineSegment StartX=-101.119 StartY=-309.563 StartZ=0 EndX=-123.373 EndY=-307.832 EndZ=0
    g4: LineSegment StartX=-101.119 StartY=-309.563 StartZ=0 EndX=4.5 EndY=-309.563 EndZ=0
    g5: ArcOfCircle CenterX=4.5 CenterY=-307.063 CenterZ=0 NormalX=0 NormalY=0 NormalZ=1 AngleXU=1.5708 Radius=2.5 StartAngle=3.14159 EndAngle=4.71239
    g6: LineSegment StartX=7 StartY=-307.063 StartZ=0 EndX=7 EndY=-167.135 EndZ=0
    g7: ArcOfCircle CenterX=9.5 CenterY=-167.135 CenterZ=0 NormalX=0 NormalY=0 NormalZ=1 AngleXU=1.5708 Radius=2.5 StartAngle=0 EndAngle=1.5708
    g8: LineSegment StartX=9.5 StartY=-164.635 StartZ=0 EndX=32.5 EndY=-164.635 EndZ=0
    g9: ArcOfCircle CenterX=32.5 CenterY=-162.135 CenterZ=0 NormalX=0 NormalY=0 NormalZ=1 AngleXU=1.5708 Radius=2.5 StartAngle=3.14159 EndAngle=4.71239
    g10: LineSegment StartX=35 StartY=-162.135 StartZ=0 EndX=35 EndY=199.635 EndZ=0
    g11: ArcOfCircle CenterX=30 CenterY=199.635 CenterZ=0 NormalX=0 NormalY=0 NormalZ=1 AngleXU=1.5708 Radius=5 StartAngle=4.71239 EndAngle=6.28319
    g12: LineSegment StartX=-36.1187 StartY=204.635 StartZ=0 EndX=30 EndY=204.635 EndZ=0
    g13: LineSegment StartX=-36.1187 StartY=204.635 StartZ=0 EndX=-36.1187 EndY=206.599 EndZ=0
    g14: LineSegment StartX=-36.1187 StartY=206.599 StartZ=0 EndX=-34.1187 EndY=206.599 EndZ=0
    g15: LineSegment StartX=-34.1187 StartY=206.599 StartZ=0 EndX=-32.5901 EndY=208.782 EndZ=0
    g16: ArcOfCircle CenterX=-34.5856 CenterY=208.916 CenterZ=0 NormalX=0 NormalY=0 NormalZ=1 AngleXU=2.53073 Radius=2 StartAngle=3.68502 EndAngle=4.71239
    g17: LineSegment StartX=-33.4384 StartY=210.555 StartZ=0 EndX=-60.0112 EndY=229.161 EndZ=0
    g18: ArcOfCircle CenterX=-61.1583 CenterY=227.523 CenterZ=0 NormalX=0 NormalY=0 NormalZ=1 AngleXU=2.53073 Radius=2 StartAngle=4.71239 EndAngle=6.69463
    g19: LineSegment StartX=-63.1187 StartY=227.919 StartZ=0 EndX=-63.1187 EndY=206.599 EndZ=0
    g20: LineSegment StartX=-63.1187 StartY=206.599 StartZ=0 EndX=-61.1187 EndY=206.599 EndZ=0
    g21: LineSegment StartX=-61.1187 StartY=206.599 StartZ=0 EndX=-61.1187 EndY=204.635 EndZ=0
    g22: LineSegment StartX=-83.3733 StartY=206.366 StartZ=0 EndX=-61.1187 EndY=204.635 EndZ=0
    g23: Circle CenterX=21 CenterY=158.725 CenterZ=0 NormalX=0 NormalY=0 NormalZ=1 AngleXU=1.5708 Radius=1.7
    g24: Circle CenterX=21 CenterY=-158.725 CenterZ=0 NormalX=0 NormalY=0 NormalZ=1 AngleXU=-1.5708 Radius=1.7
    g25: LineSegment StartX=-102.881 StartY=-309.426 StartZ=0 EndX=-102.725 EndY=-307.432 EndZ=0
    g26: LineSegment StartX=-35.0388 StartY=-309.563 StartZ=0 EndX=-35.0388 EndY=-307.563 EndZ=0
    g27: LineSegment StartX=-62.8805 StartY=204.772 StartZ=0 EndX=-63.0356 EndY=202.778 EndZ=0
    g28: LineSegment StartX=-35.0388 StartY=204.635 StartZ=0 EndX=-35.0388 EndY=202.635 EndZ=0
  constraints (35):
    c: Coincident(g1,g2)
    c: Coincident(g2,g3)
    c: Coincident(g3,g4)
    c: Coincident(g0,g1)
    c: Coincident(g0,g22)
    c: Coincident(g19,g20)
    c: Coincident(g18,g19)
    c: Coincident(g21,g22)
    c: Coincident(g20,g21)
    c: Coincident(g17,g18)
    c: Coincident(g12,g13)
    c: Coincident(g13,g14)
    c: Coincident(g14,g15)
    c: Coincident(g16,g17)
    c: Coincident(g15,g16)
    c: Coincident(g4,g5)
    c: Coincident(g5,g6)
    c: Coincident(g6,g7)
    c: Coincident(g7,g8)
    c: Coincident(g11,g12)
    c: Coincident(g8,g9)
    c: Coincident(g9,g10)
    c: Coincident(g10,g11)
    c: Coincident(g25,g-3)
    c: PointOnObject(g25,g-3)
    c: Coincident(g26,g-4)
    c: PointOnObject(g26,g-4)
    c: Coincident(g27,g-3)
    c: PointOnObject(g27,g-3)
    c: Coincident(g28,g-4)
    c: PointOnObject(g28,g-4)
    c: Equal(g28,g27)
    c: Equal(g27,g25)
    c: Equal(g25,g26)
    c: DistanceY(g26,g26) = 2
FEATURE [Part::Mirroring] Part__Mirroring022  label="sink_back_Sketch010 (Mirror #20)"
  Base = (0,0,0)
  Normal = (1,0,0)
  Source = -> Unfold_Sketch015
  expr: Source = <<sink_back_Unfold_Sketch>>._self
FEATURE [TechDraw::DrawViewBalloon] Balloon002
  BubbleShape = 3
  EndType = 0
  EndTypeScale = 1
  KinkLength = 5
  LockPosition = false
  OriginX = -129.426
  OriginY = 40.4275
  Rotation = 0
  ScaleType = 0
  ShapeScale = 1
  SourceView = -> View008
  Text = Лицевая сторона
  TextWrapLen = -1
  X = -35.7334
  Y = 69.7525
FEATURE [TechDraw::DrawViewBalloon] Balloon003
  BubbleShape = 3
  EndType = 0
  EndTypeScale = 1
  KinkLength = 5
  LockPosition = false
  OriginX = -22.4143
  OriginY = 9.58765
  Rotation = 0
  ScaleType = 0
  ShapeScale = 1
  SourceView = -> View023
  Text = Оборотная сторона
  TextWrapLen = -1
  X = -77.7821
  Y = 9.72345
FEATURE [TechDraw::DrawViewDimension] Dimension054
  AngleOverride = false
  Arbitrary = false
  ArbitraryTolerances = false
  BoxCorners = (2) [(-35.5652,-54.3694,-1e-07),(35.5652,54.3694,1e-07)]
  EqualTolerance = true
  ExtensionAngle = 0
  FormatSpec = %.2w
  FormatSpecOverTolerance = %+.2w
  FormatSpecUnderTolerance = %+.2w
  Inverted = false
  LineAngle = 0
  LockPosition = false
  MeasureType = 1
  OverTolerance = 0
  References2D = -> [View018]
  Rotation = 0
  ScaleType = 0
  TheoreticalExact = false
  Type = 2
  UnderTolerance = 0
  X = 44.4864
  Y = 22.7687
FEATURE [TechDraw::DrawViewDimension] Dimension055
  AngleOverride = false
  Arbitrary = false
  ArbitraryTolerances = false
  BoxCorners = (2) [(-35.6492,-50.9687,-1e-07),(35.6492,50.9687,1e-07)]
  EqualTolerance = true
  ExtensionAngle = 0
  FormatSpec = %.2w
  FormatSpecOverTolerance = %+.2w
  FormatSpecUnderTolerance = %+.2w
  Inverted = false
  LineAngle = 0
  LockPosition = false
  MeasureType = 1
  OverTolerance = 0
  References2D = -> [View024]
  Rotation = 0
  ScaleType = 0
  TheoreticalExact = false
  Type = 0
  UnderTolerance = 0
  X = -32.5296
  Y = -40.8743
FEATURE [TechDraw::DrawViewBalloon] Balloon004
  BubbleShape = 3
  EndType = 0
  EndTypeScale = 1
  KinkLength = 5
  LockPosition = false
  OriginX = -15.6807
  OriginY = 32.1503
  Rotation = 0
  ScaleType = 0
  ShapeScale = 1
  SourceView = -> View020
  Text = Лицевая сторона
  TextWrapLen = -1
  X = 68.8384
  Y = 72.1503
FEATURE [TechDraw::DrawViewBalloon] Balloon005
  BubbleShape = 3
  EndType = 0
  EndTypeScale = 1
  KinkLength = 5
  LockPosition = false
  OriginX = 26.277
  OriginY = 12.5512
  Rotation = 0
  ScaleType = 0
  ShapeScale = 1
  SourceView = -> View024
  Text = Оборотная\nсторона
  TextWrapLen = -1
  X = 67.9102
  Y = 27.8862
FEATURE [TechDraw::DrawViewDimension] Dimension056
  AngleOverride = false
  Arbitrary = false
  ArbitraryTolerances = false
  BoxCorners = (2) [(-35.5652,-54.3694,-1e-07),(35.5652,54.3694,1e-07)]
  EqualTolerance = true
  ExtensionAngle = 0
  FormatSpec = %.2w
  FormatSpecOverTolerance = %+.2w
  FormatSpecUnderTolerance = %+.2w
  Inverted = false
  LineAngle = 0
  LockPosition = false
  MeasureType = 1
  OverTolerance = 0
  References2D = -> [View022]
  Rotation = 0
  ScaleType = 0
  TheoreticalExact = false
  Type = 6
  UnderTolerance = 0
  X = -25.5859
  Y = 4.55408
FEATURE [TechDraw::DrawViewDimension] Dimension057
  AngleOverride = false
  Arbitrary = false
  ArbitraryTolerances = false
  BoxCorners = (2) [(-35.6221,-51.0333,-1e-07),(35.6221,51.0333,1e-07)]
  EqualTolerance = true
  ExtensionAngle = 0
  FormatSpec = %.2w
  FormatSpecOverTolerance = %+.2w
  FormatSpecUnderTolerance = %+.2w
  Inverted = false
  LineAngle = 0
  LockPosition = false
  MeasureType = 1
  OverTolerance = 0
  References2D = -> [View023]
  Rotation = 0
  ScaleType = 0
  TheoreticalExact = false
  Type = 6
  UnderTolerance = 0
  X = 18.1291
  Y = -33.0331
FEATURE [TechDraw::DrawPage] Page003
  KeepUpdated = true
  NextBalloonIndex = 3
  ProjectionType = 0
  Template = -> Template
  Views = -> [View008,View022,View023,Dimension,Dimension053,Balloon002,Balloon003,Dimension056,Dimension057]
FEATURE [TechDraw::DrawViewDimension] Dimension058
  AngleOverride = false
  Arbitrary = false
  ArbitraryTolerances = false
  BoxCorners = (2) [(-35.6492,-50.9687,-1e-07),(35.6492,50.9687,1e-07)]
  EqualTolerance = true
  ExtensionAngle = 0
  FormatSpec = %.2w
  FormatSpecOverTolerance = %+.2w
  FormatSpecUnderTolerance = %+.2w
  Inverted = false
  LineAngle = 0
  LockPosition = false
  MeasureType = 1
  OverTolerance = 0
  References2D = -> [View024]
  Rotation = 0
  ScaleType = 0
  TheoreticalExact = false
  Type = 6
  UnderTolerance = 0
  X = -20.8061
  Y = -33.278
FEATURE [TechDraw::DrawViewDimension] Dimension059
  AngleOverride = false
  Arbitrary = false
  ArbitraryTolerances = false
  BoxCorners = (2) [(-35.5652,-54.3694,-1e-07),(35.5652,54.3694,1e-07)]
  EqualTolerance = true
  ExtensionAngle = 0
  FormatSpec = %.2w
  FormatSpecOverTolerance = %+.2w
  FormatSpecUnderTolerance = %+.2w
  Inverted = false
  LineAngle = 0
  LockPosition = false
  MeasureType = 1
  OverTolerance = 0
  References2D = -> [View018]
  Rotation = 0
  ScaleType = 0
  TheoreticalExact = false
  Type = 6
  UnderTolerance = 0
  X = 27.4865
  Y = 10.6758
FEATURE [TechDraw::DrawPage] Page006
  KeepUpdated = true
  NextBalloonIndex = 3
  ProjectionType = 0
  Template = -> Template001
  Views = -> [View018,View020,View024,Dimension054,Dimension055,Balloon004,Balloon005,Dimension058,Dimension059]
FEATURE [App::DocumentObjectGroup] Group007  label="sink_back_unfolds_Group"
  Group = -> [Page003,Page006,Part__Mirroring022,Part__Mirroring023,Unfold014,Unfold_Sketch015,Unfold_Sketch_Outline011,Unfold_Sketch_Internal011,Unfold_Sketch_bends014]
FEATURE [Sketcher::SketchObject] Sketch120
  ExternalGeometry = -> [Sketch]
  FullyConstrained = true
  sketch-geometry (4):
    g0: LineSegment StartX=318.143 StartY=151.42 StartZ=0 EndX=259.563 EndY=210 EndZ=0
    g1: LineSegment StartX=259.563 StartY=210 StartZ=0 EndX=239.563 EndY=210 EndZ=0
    g2: LineSegment StartX=319.563 StartY=150 StartZ=0 EndX=445.428 EndY=0 EndZ=0
    g3: LineSegment StartX=306.653 StartY=141.778 StartZ=0 EndX=318.143 EndY=151.42 EndZ=0
  constraints (13):
    c: Coincident(g0,g1)
    c: Horizontal(g1)
    c: Angle(g0) = 2.35619
    c: DistanceX(g1,g1) = 20
    c: Coincident(g2,g-3)
    c: Perpendicular(g-3,g2)
    c: Distance(g0,g-3) = 2
    c: PointOnObject(g2,g0)
    c: DistanceY(g2,g0) = 60
    c: Coincident(g3,g0)
    c: Parallel(g3,g-3)
    c: Distance(g3) = 15
    c: PointOnObject(g2,g-1)
FEATURE [Sketcher::SketchObject] Sketch121
  ExternalGeometry = -> [Sketch,Sketch120]
  FullyConstrained = false
  sketch-geometry (5):
    g0: LineSegment StartX=306.674 StartY=161.656 StartZ=0 EndX=317.828 EndY=150.502 EndZ=0
    g1: LineSegment StartX=317.828 StartY=150.502 StartZ=0 EndX=305.744 EndY=140.363 EndZ=0
    g2: GeomPoint X=313.391 Y=150.696 Z=0
    g3: LineSegment StartX=313.391 StartY=150.696 StartZ=0 EndX=315.32 EndY=148.397 EndZ=0
    g4: LineSegment StartX=313.391 StartY=150.696 StartZ=0 EndX=315.513 EndY=152.817 EndZ=0
  constraints (14):
    c: Coincident(g0,g1)
    c: Distance(g2,g1) = 3
    c: Distance(g2,g0) = 3
    c: Parallel(g1,g-3)
    c: Distance(g0,g-3) = 1.5
    c: Coincident(g3,g2)
    c: PointOnObject(g3,g1)
    c: Coincident(g4,g2)
    c: PointOnObject(g4,g0)
    c: Perpendicular(g0,g4)
    c: Perpendicular(g1,g3)
    c: Distance(g3,g1) = 12.5
    c: Distance(g4,g0) = 12.5
    c: Parallel(g0,g-4)
FEATURE [Part::FeaturePython] Placment028  # WARN: FeaturePython — macro-defined, semantics opaque (R4)
  AttacherType = Attacher::AttachEngine3D
  AttachmentOffset = pos=(0,0,0) rot=(0.707107,-0.707107,0;3.14159rad)
  AttachmentSupport = -> [Sketch121]
  ExposePlacement = true
  MapMode = 7
  MarkerShape = 1
  MarkerSize = 2
  NumElements = 1
  Placement = pos=(315.513,152.817,0) rot=(0.357407,-0.862856,-0.357407;4.56541rad)
  Type = lattice2AttachablePlacement.AttachablePlacement
  isLattice = 1
FEATURE [Part::FeaturePython] Placment029  # WARN: FeaturePython — macro-defined, semantics opaque (R4)
  AttacherType = Attacher::AttachEngine3D
  AttachmentOffset = pos=(0,0,0) rot=(-0.707107,-0.707107,0;3.14159rad)
  AttachmentSupport = -> [Sketch121]
  ExposePlacement = true
  MapMode = 7
  MarkerShape = 1
  MarkerSize = 5
  NumElements = 1
  Placement = pos=(315.32,148.397,0) rot=(0.671543,-0.313146,0.671543;2.53465rad)
  Type = lattice2AttachablePlacement.AttachablePlacement
  isLattice = 1
FEATURE [PartDesign::SubShapeBinder] Binder040
  BindCopyOnChange = 0
  BindMode = 0
  ClaimChildren = true
  Fuse = false
  MakeFace = true
  OffsetFill = false
  OffsetIntersection = false
  OffsetJoinType = 0
  OffsetOpenResult = false
  PartialLoad = false
  Relative = false
  Support = -> [<external ../hinge.FCStd>#Sketch]
  _Version = 2
  expr: Support = <<hinge>>#Sketch._self
FEATURE [Part::FeaturePython] LinearArray013  # WARN: FeaturePython — macro-defined, semantics opaque (R4)
  Alignment = 0
  CellStart = A1
  Count = 2
  Dir = (0,0,1)
  DirIsDriven = true
  DistributionLaw = 0
  DrivenProperty = 1
  EndInclusive = true
  ExposePlacement = false
  GeneratorMode = 0
  MarkerShape = 1
  MarkerSize = 50
  NumElements = 2
  OrientMode = 0
  Point = (0,0,0)
  PointIsDriven = true
  Reverse = false
  SpanEnd = 1020
  SpanStart = 270
  Step = 750
  Type = lattice2LinearArray.LinearArray
  VSGVersion = 1
  Values = 270.0 | 1020.0
  ValuesSource = 2
  isLattice = 1
FEATURE [Sketcher::SketchObject] Sketch122
  ExternalGeometry = -> [Binder040]
  FullyConstrained = true
  sketch-geometry (2):
    g0: Circle CenterX=14 CenterY=12.5 CenterZ=0 NormalX=0 NormalY=0 NormalZ=1 AngleXU=0 Radius=1.7
    g1: Circle CenterX=-14 CenterY=12.5 CenterZ=0 NormalX=0 NormalY=0 NormalZ=1 AngleXU=0 Radius=1.7
  constraints (4):
    c: Symmetric(g0,g1,g-2)
    c: Equal(g1,g0)
    c: Coincident(g0,g-3)
    c: Diameter(g0) = 3.4
FEATURE [Part::Extrusion] Extrude034
  Base = -> Sketch122
  Dir = (0,0,1)
  DirMode = 2
  FaceMakerClass = Part::FaceMakerBullseye
  LengthFwd = 10
  LengthRev = 0
  Solid = true
  Symmetric = false
FEATURE [Sketcher::SketchObject] Sketch124
  ExternalGeometry = -> [Sketch120]
  FullyConstrained = true
  sketch-geometry (1):
    g0: LineSegment StartX=0 StartY=210 StartZ=0 EndX=258.563 EndY=210 EndZ=0
  constraints (4):
    c: PointOnObject(g0,g-2)
    c: Horizontal(g0)
    c: DistanceX(g0,g-3) = 1
    c: DistanceY(g0,g-3) = 0
FEATURE [PartDesign::SubShapeBinder] Binder041
  BindCopyOnChange = 0
  BindMode = 0
  ClaimChildren = true
  Context = -> Body032 [Binder041.]
  Fuse = false
  MakeFace = true
  OffsetFill = false
  OffsetIntersection = false
  OffsetJoinType = 0
  OffsetOpenResult = false
  PartialLoad = false
  Relative = false
  Support = -> [Sketch124]
  _Version = 2
FEATURE [PartDesign::FeaturePython] BaseBend022  # WARN: FeaturePython — macro-defined, semantics opaque (R4)
  BendSide = 0
  BendSketch = -> Binder041
  MidPlane = false
  Reverse = false
  Suppressed = false
  length = 900
  radius = 1
  thickness = 4
  expr: length = <<BaseBend023>>.length
FEATURE [PartDesign::SubShapeBinder] Binder042
  BindCopyOnChange = 0
  BindMode = 0
  ClaimChildren = true
  Context = -> Body033 [Binder042.]
  Fuse = false
  MakeFace = true
  OffsetFill = false
  OffsetIntersection = false
  OffsetJoinType = 0
  OffsetOpenResult = false
  PartialLoad = false
  Relative = false
  Support = -> [Sketch120]
  _Version = 2
FEATURE [PartDesign::FeaturePython] BaseBend023  # WARN: FeaturePython — macro-defined, semantics opaque (R4)
  BendSide = 0
  BendSketch = -> Binder042
  MidPlane = false
  Reverse = false
  Suppressed = false
  length = 900
  radius = 1
  thickness = 1
FEATURE [Part::FeaturePython] Placment030  # WARN: FeaturePython — macro-defined, semantics opaque (R4)
  AttacherType = Attacher::AttachEngine3D
  ExposePlacement = true
  MarkerShape = 1
  MarkerSize = 20
  NumElements = 1
  Placement = pos=(220,10,0) rot=(0,0,1;0rad)
  Type = lattice2AttachablePlacement.AttachablePlacement
  isLattice = 1
  expr: .Placement.Base.x = <<LinearArray014>>.Step / 2
FEATURE [Part::FeaturePython] Placment031  # WARN: FeaturePython — macro-defined, semantics opaque (R4)
  AttacherType = Attacher::AttachEngine3D
  ExposePlacement = true
  MarkerShape = 1
  MarkerSize = 20
  NumElements = 1
  Type = lattice2AttachablePlacement.AttachablePlacement
  isLattice = 1
FEATURE [Part::FeaturePython] LinearArray014  # WARN: FeaturePython — macro-defined, semantics opaque (R4)
  Alignment = 0
  CellStart = A1
  Count = 3
  Dir = (1,0,0)
  DirIsDriven = true
  DistributionLaw = 0
  DrivenProperty = 1
  EndInclusive = true
  ExposePlacement = false
  GeneratorMode = 0
  MarkerShape = 1
  MarkerSize = 0
  NumElements = 3
  OrientMode = 1
  Placement = pos=(10,0,0) rot=(0,0,1;0rad)
  Point = (0,0,0)
  PointIsDriven = true
  Reverse = false
  SpanEnd = 880
  SpanStart = 0
  Step = 440
  Type = lattice2LinearArray.LinearArray
  VSGVersion = 1
  Values = 0.0 | 440.0 | 880.0
  ValuesSource = 2
  isLattice = 1
  expr: SpanEnd = <<BaseBend023>>.length - .Placement.Base.x * 2
FEATURE [Part::FeaturePython] Join018  # WARN: FeaturePython — macro-defined, semantics opaque (R4)
  ExposePlacement = false
  Interleave = false
  Links = -> [Placment030,Placment031]
  MarkerShape = 1
  MarkerSize = 0
  NumElements = 2
  Type = lattice2JoinArrays.JoinArrays
  isLattice = 1
FEATURE [Part::FeaturePython] Populate062  label="Populate LinearArray014 with Join018"  # WARN: FeaturePython — macro-defined, semantics opaque (R4)
  Copying = 0
  ExposePlacement = false
  MarkerShape = 1
  MarkerSize = 0
  NumElements = 6
  Object = -> Join018
  OutputCompounding = 0
  PlacementsTo = -> LinearArray014
  Referencing = 0
  Type = lattice2PopulateCopies.LatticePopulateCopies
  isLattice = 1
FEATURE [Part::Box] Box  label="Cube"
  AttacherType = Attacher::AttachEngine3D
  Height = 10
  Length = 891
  Placement = pos=(-1,-1,0) rot=(0,0,1;0rad)
  Width = 11
  expr: Length = <<LinearArray014>>.SpanEnd - .Placement.Base.x + <<LinearArray014>>.Placement.Base.x
  expr: Width = <<Placment030>>.Placement.Base.y - .Placement.Base.y
FEATURE [Part::FeaturePython] ArrayFilter  # WARN: FeaturePython — macro-defined, semantics opaque (R4)
  Base = -> Populate062
  ExposePlacement = false
  FilterType = 2
  Invert = false
  MarkerShape = 1
  MarkerSize = 0
  NumElements = 5
  Stencil = -> Box
  Type = lattice2ArrayFilter.LatticeArrayFilter
  WindowFrom = 0
  WindowTo = 1
  isLattice = 1
FEATURE [Part::FeaturePython] Placment032  # WARN: FeaturePython — macro-defined, semantics opaque (R4)
  AttacherType = Attacher::AttachEngine3D
  AttachmentOffset = pos=(1,0,-4) rot=(0.57735,0.57735,-0.57735;4.18879rad)
  AttachmentSupport = -> [Sketch120]
  ExposePlacement = true
  MapMode = 7
  MarkerShape = 1
  MarkerSize = 20
  NumElements = 1
  Placement = pos=(255.563,211,0) rot=(-0.57735,0.57735,-0.57735;4.18879rad)
  Type = lattice2AttachablePlacement.AttachablePlacement
  isLattice = 1
FEATURE [Part::FeaturePython] Populate063  label="Populate Placment032 with ArrayFilter"  # WARN: FeaturePython — macro-defined, semantics opaque (R4)
  Copying = 0
  ExposePlacement = false
  MarkerShape = 1
  MarkerSize = 0
  NumElements = 5
  Object = -> ArrayFilter
  OutputCompounding = 0
  PlacementsTo = -> Placment032
  Referencing = 0
  Type = lattice2PopulateCopies.LatticePopulateCopies
  isLattice = 1
FEATURE [Part::FeaturePython] Populate064  label="Populate Populate Placment032 with ArrayFilter with hole_3.4mm"  # WARN: FeaturePython — macro-defined, semantics opaque (R4)
  Copying = 0
  ExposePlacement = false
  MarkerShape = 1
  MarkerSize = 0
  NumElements = 0
  Object = -> Cylinder
  OutputCompounding = 1
  PlacementsTo = -> Populate063
  Referencing = 0
  Type = lattice2PopulateCopies.LatticePopulateCopies
  isLattice = 0
FEATURE [Part::Compound] Compound042
  Links = -> [Populate064]
FEATURE [PartDesign::Boolean] Boolean033
  BaseFeature = -> BaseBend022
  Group = -> [Compound042]
  Suppressed = false
  Type = 1
  UsePlacement = true
FEATURE [PartDesign::Body] Body032
  Group = -> [Binder041,BaseBend022,Boolean033]
  Origin = -> Origin034
  Tip = -> Boolean033
FEATURE [Sketcher::SketchObject] Sketch125
  FullyConstrained = true
  sketch-geometry (3):
    g0: ArcOfCircle CenterX=-5 CenterY=-5 CenterZ=0 NormalX=0 NormalY=0 NormalZ=1 AngleXU=0 Radius=5 StartAngle=-4.33076e-11 EndAngle=1.5708
    g1: LineSegment StartX=-1.4909e-11 StartY=-5 StartZ=0 EndX=0 EndY=0 EndZ=0
    g2: LineSegment StartX=0 StartY=0 StartZ=0 EndX=-5 EndY=-1.4909e-11 EndZ=0
  constraints (7):
    c: PointOnObject(g0,g-1)
    c: PointOnObject(g0,g-2)
    c: Coincident(g1,g2)
    c: Tangent(g2,g0) = -1.5708
    c: Tangent(g0,g1) = -1.5708
    c: Coincident(g1,g-1)
    c: Radius(g0) = 5
FEATURE [Part::Extrusion] Extrude036
  Base = -> Sketch125
  Dir = (0,0,1)
  DirMode = 2
  FaceMakerClass = Part::FaceMakerBullseye
  LengthFwd = 10
  LengthRev = 0
  Solid = true
  Symmetric = true
FEATURE [Part::FeaturePython] Placment033  # WARN: FeaturePython — macro-defined, semantics opaque (R4)
  AttacherType = Attacher::AttachEngine3D
  AttachmentOffset = pos=(0,0,0) rot=(0.707107,0,-0.707107;3.14159rad)
  AttachmentSupport = -> [Sketch120]
  ExposePlacement = true
  MapMode = 7
  MarkerShape = 1
  MarkerSize = 10
  NumElements = 1
  Placement = pos=(239.563,210,0) rot=(0,0.707107,-0.707107;3.14159rad)
  Type = lattice2AttachablePlacement.AttachablePlacement
  isLattice = 1
FEATURE [Part::FeaturePython] Placment034  # WARN: FeaturePython — macro-defined, semantics opaque (R4)
  AttacherType = Attacher::AttachEngine3D
  AttachmentOffset = pos=(0,0,0) rot=(0.707107,0,0.707107;3.14159rad)
  AttachmentSupport = -> [Sketch120]
  ExposePlacement = true
  MapMode = 7
  MarkerShape = 1
  MarkerSize = 10
  NumElements = 1
  Placement = pos=(306.653,141.778,0) rot=(0.249244,-0.684791,0.684791;3.63013rad)
  Type = lattice2AttachablePlacement.AttachablePlacement
  isLattice = 1
FEATURE [Part::FeaturePython] Join019  # WARN: FeaturePython — macro-defined, semantics opaque (R4)
  ExposePlacement = false
  Interleave = false
  Links = -> [Placment033,Placment034]
  MarkerShape = 1
  MarkerSize = 0
  NumElements = 2
  Type = lattice2JoinArrays.JoinArrays
  isLattice = 1
FEATURE [Part::FeaturePython] Populate065  label="Populate Join019 with Extrude036"  # WARN: FeaturePython — macro-defined, semantics opaque (R4)
  Copying = 0
  ExposePlacement = false
  MarkerShape = 1
  MarkerSize = 0
  NumElements = 0
  Object = -> Extrude036
  OutputCompounding = 1
  PlacementsTo = -> Join019
  Referencing = 0
  Type = lattice2PopulateCopies.LatticePopulateCopies
  isLattice = 0
FEATURE [Part::FeaturePython] Mirror016  label="Mirror016 of Populate Join019 with Extrude036"  # WARN: FeaturePython — macro-defined, semantics opaque (R4)
  ExposePlacement = false
  FlipX = false
  FlipY = false
  FlipZ = true
  MarkerShape = 1
  MarkerSize = 0
  NumElements = 0
  Object = -> Populate065
  ObjectTraversal = 0
  PivotPlacement = pos=(0,0,450) rot=(0,0,1;0rad)
  Type = lattice2Mirror.LatticeMirror
  isLattice = 0
  expr: .PivotPlacement.Base.z = <<BaseBend023>>.length / 2
FEATURE [Part::FeaturePython] LinearArray015  # WARN: FeaturePython — macro-defined, semantics opaque (R4)
  Alignment = 0
  CellStart = A1
  Count = 2
  Dir = (0,0,1)
  DirIsDriven = true
  DistributionLaw = 0
  DrivenProperty = 1
  EndInclusive = true
  ExposePlacement = false
  GeneratorMode = 0
  MarkerShape = 1
  MarkerSize = 0
  NumElements = 2
  OrientMode = 0
  Point = (0,0,0)
  PointIsDriven = true
  Reverse = false
  SpanEnd = 850
  SpanStart = 50
  Step = 800
  Type = lattice2LinearArray.LinearArray
  VSGVersion = 1
  Values = 50.0 | 850.0
  ValuesSource = 2
  isLattice = 1
  expr: SpanEnd = <<BaseBend023>>.length - SpanStart
FEATURE [Part::FeaturePython] Placment035  # WARN: FeaturePython — macro-defined, semantics opaque (R4)
  AttacherType = Attacher::AttachEngine3D
  ExposePlacement = true
  MarkerShape = 1
  MarkerSize = 20
  NumElements = 1
  Placement = pos=(0,0,220) rot=(0,0,1;0rad)
  Type = lattice2AttachablePlacement.AttachablePlacement
  isLattice = 1
FEATURE [Part::FeaturePython] Populate067  label="Populate Placment035 with LinearArray015"  # WARN: FeaturePython — macro-defined, semantics opaque (R4)
  Copying = 0
  ExposePlacement = false
  MarkerShape = 1
  MarkerSize = 0
  NumElements = 2
  Object = -> LinearArray015
  OutputCompounding = 0
  PlacementsTo = -> Placment035
  Referencing = 0
  Type = lattice2PopulateCopies.LatticePopulateCopies
  isLattice = 1
FEATURE [Part::FeaturePython] Populate059  label="Populate LinearArray013 with Placment029"  # WARN: FeaturePython — macro-defined, semantics opaque (R4)
  Copying = 0
  ExposePlacement = false
  MarkerShape = 1
  MarkerSize = 0
  NumElements = 2
  Object = -> Placment029
  OutputCompounding = 0
  PlacementsTo = -> Populate067
  Referencing = 0
  Type = lattice2PopulateCopies.LatticePopulateCopies
  isLattice = 1
FEATURE [Part::FeaturePython] Populate060  label="Populate Populate LinearArray013 with Placment029 with Extrude034"  # WARN: FeaturePython — macro-defined, semantics opaque (R4)
  Copying = 0
  ExposePlacement = false
  MarkerShape = 1
  MarkerSize = 0
  NumElements = 0
  Object = -> Extrude034
  OutputCompounding = 1
  PlacementsTo = -> Populate059
  Referencing = 0
  Type = lattice2PopulateCopies.LatticePopulateCopies
  isLattice = 0
FEATURE [Part::FeaturePython] Mirror015  label="Mirror015 of Populate Populate LinearArray013 with Placment029 with Extrude034"  # WARN: FeaturePython — macro-defined, semantics opaque (R4)
  ExposePlacement = false
  FlipX = true
  FlipY = false
  FlipZ = false
  MarkerShape = 1
  MarkerSize = 0
  NumElements = 0
  Object = -> Populate060
  ObjectTraversal = 0
  Type = lattice2Mirror.LatticeMirror
  isLattice = 0
FEATURE [Part::Compound] Compound040
  Links = -> [Populate060,Mirror015]
FEATURE [Part::FeaturePython] Populate061  label="Populate sections_LinearArray with Compound040"  # WARN: FeaturePython — macro-defined, semantics opaque (R4)
  Copying = 0
  ExposePlacement = false
  MarkerShape = 1
  MarkerSize = 0
  NumElements = 0
  Object = -> Compound040
  OutputCompounding = 1
  PlacementsTo = -> LinearArray001
  Referencing = 0
  Type = lattice2PopulateCopies.LatticePopulateCopies
  isLattice = 0
FEATURE [Part::Compound] Compound001  label="face_cut1"
  Links = -> [Populate004,Populate012,Populate021,Populate025,Populate045,Populate046,Fusion006,Populate061]
FEATURE [PartDesign::Boolean] Boolean
  BaseFeature = -> Bend
  Group = -> [Compound001]
  Refine = true
  Suppressed = false
  Type = 1
  UsePlacement = false
FEATURE [PartDesign::Boolean] Boolean013
  BaseFeature = -> Boolean
  Group = -> [Compound007]
  Suppressed = false
  Type = 1
  UsePlacement = true
FEATURE [PartDesign::Boolean] Boolean014
  BaseFeature = -> Boolean013
  Group = -> [Compound005]
  Refine = true
  Suppressed = false
  Type = 0
  UsePlacement = true
FEATURE [PartDesign::Pocket] Pocket022
  BaseFeature = -> Boolean014
  Direction = (0,-1,2e-16)
  Length = 5
  Length2 = 0.1
  Profile = -> Sketch075
  ReferenceAxis = -> Sketch075 [N_Axis]
  Suppressed = false
  Type = 4
FEATURE [PartDesign::Pocket] Pocket023
  BaseFeature = -> Pocket022
  Direction = (-0.642788,0.766044,0)
  Length = 0.1
  Length2 = 5
  Midplane = true
  Profile = -> Sketch076
  ReferenceAxis = -> Sketch076 [N_Axis]
  Suppressed = false
  Type = 4
FEATURE [PartDesign::MultiTransform] MultiTransform004
  BaseFeature = -> Pocket023
  Originals = -> [Pocket022,Pocket023]
  Suppressed = false
  Transformations = -> [Mirrored008,LinearPattern004]
FEATURE [PartDesign::Body] Body  label="face"
  Group = -> [Binder,BaseBend,Extend,Bend,Boolean,Boolean013,Local_CS009,Local_CS005,Local_CS006,Local_CS007,Local_CS010,Local_CS011,Local_CS014,Local_CS015,Local_CS024,Local_CS025,Boolean014,Sketch075,Sketch076,Pocket022,Pocket023,DatumPlane004,DatumPlane005,MultiTransform004,Mirrored008,LinearPattern004,Local_CS032,Local_CS034]
  Origin = -> Origin
  Tip = -> MultiTransform004
FEATURE [Sketcher::SketchObject] Sketch123
  ExternalGeometry = -> [Boolean013]
  FullyConstrained = true
  Placement = pos=(0,0,240) rot=(0,0,1;0rad)
  sketch-geometry (4):
    g0: LineSegment StartX=608.484 StartY=124.288 StartZ=0 EndX=620.474 EndY=110 EndZ=0
    g1: LineSegment StartX=620.474 StartY=110 StartZ=0 EndX=639.126 EndY=110 EndZ=0
    g2: LineSegment StartX=639.126 StartY=110 StartZ=0 EndX=639.126 EndY=150 EndZ=0
    g3: LineSegment StartX=639.126 StartY=150 StartZ=0 EndX=608.484 EndY=124.288 EndZ=0
  constraints (12):
    c: PointOnObject(g0,g-4)
    c: Coincident(g0,g1)
    c: PointOnObject(g1,g-3)
    c: Horizontal(g1)
    c: Coincident(g1,g2)
    c: Vertical(g2)
    c: Coincident(g2,g3)
    c: Coincident(g3,g0)
    c: PointOnObject(g-4,g3)
    c: Perpendicular(g3,g0)
    c: Equal(g1,g0)
    c: Distance(g3) = 40
FEATURE [Part::Extrusion] Extrude035
  Base = -> Sketch123
  Dir = (0,0,1)
  DirMode = 2
  FaceMakerClass = Part::FaceMakerBullseye
  LengthFwd = 60
  LengthRev = 0
  Solid = true
  Symmetric = false
FEATURE [Part::MultiCommon] Common
  Shapes = -> [Body,Extrude035]
FEATURE [Sketcher::SketchObject] Sketch126
  FullyConstrained = true
  sketch-geometry (9):
    g0: LineSegment StartX=-25 StartY=-15 StartZ=0 EndX=25 EndY=-15 EndZ=0
    g1: LineSegment StartX=25 StartY=-15 StartZ=0 EndX=25 EndY=3 EndZ=0
    g2: LineSegment StartX=23 StartY=5 StartZ=0 EndX=-23 EndY=5 EndZ=0
    g3: LineSegment StartX=-25 StartY=3 StartZ=0 EndX=-25 EndY=-15 EndZ=0
    g4: GeomPoint X=0 Y=-5 Z=0
    g5: ArcOfCircle CenterX=23 CenterY=3 CenterZ=0 NormalX=0 NormalY=0 NormalZ=1 AngleXU=0 Radius=2 StartAngle=1.764e-13 EndAngle=1.5708
    g6: GeomPoint X=25 Y=5 Z=0
    g7: ArcOfCircle CenterX=-23 CenterY=3 CenterZ=0 NormalX=0 NormalY=0 NormalZ=1 AngleXU=0 Radius=2 StartAngle=1.5708 EndAngle=3.14159
    g8: GeomPoint X=-25 Y=5 Z=0
  constraints (21):
    c: Coincident(g0,g1)
    c: Coincident(g3,g0)
    c: Horizontal(g0)
    c: Horizontal(g2)
    c: Vertical(g1)
    c: Vertical(g3)
    c: Symmetric(g6,g0,g4)
    c: PointOnObject(g4,g-2)
    c: DistanceX(g8,g6) = 50
    c: DistanceY(g1,g6) = 20
    c: DistanceY(g6) = 5
    c: PointOnObject(g6,g1)
    c: PointOnObject(g6,g2)
    c: Tangent(g1,g5) = -1.5708
    c: Tangent(g2,g5) = -1.5708
    c: PointOnObject(g8,g2)
    c: PointOnObject(g8,g3)
    c: Tangent(g2,g7) = -1.5708
    c: Tangent(g3,g7) = -1.5708
    c: Equal(g5,g7)
    c: Radius(g5) = 2
FEATURE [Part::Extrusion] Extrude037
  Base = -> Sketch126
  Dir = (0,0,1)
  DirMode = 2
  FaceMakerClass = Part::FaceMakerBullseye
  LengthFwd = 30
  LengthRev = 0
  Solid = true
  Symmetric = true
FEATURE [Part::Compound] Compound043
  Links = -> [Extrude034,Extrude037]
FEATURE [Part::FeaturePython] Populate058  label="Populate Placment028 with Extrude034"  # WARN: FeaturePython — macro-defined, semantics opaque (R4)
  Copying = 0
  ExposePlacement = false
  MarkerShape = 1
  MarkerSize = 0
  NumElements = 0
  Object = -> Compound043
  OutputCompounding = 2
  PlacementsTo = -> Placment028
  Referencing = 0
  Type = lattice2PopulateCopies.LatticePopulateCopies
  isLattice = 0
FEATURE [Part::FeaturePython] Populate066  label="Populate LinearArray015 with Populate Placment028 with Extrude034"  # WARN: FeaturePython — macro-defined, semantics opaque (R4)
  Copying = 0
  ExposePlacement = false
  MarkerShape = 1
  MarkerSize = 0
  NumElements = 0
  Object = -> Populate058
  OutputCompounding = 1
  PlacementsTo = -> LinearArray015
  Referencing = 0
  Type = lattice2PopulateCopies.LatticePopulateCopies
  isLattice = 0
FEATURE [Sketcher::SketchObject] Sketch127
  AttachmentOffset = pos=(0,0,0) rot=(0,1,0;1.5708rad)
  AttachmentSupport = -> [Sketch120]
  ExternalGeometry = -> [Sketch120]
  FullyConstrained = true
  MapMode = 7
  Placement = pos=(306.653,141.778,0) rot=(0.889126,0.323616,0.323616;1.68804rad)
  sketch-geometry (4):
    g0: LineSegment StartX=16 StartY=-3.5e-15 StartZ=0 EndX=16 EndY=-25 EndZ=0
    g1: LineSegment StartX=16 StartY=-25 StartZ=0 EndX=5 EndY=-25 EndZ=0
    g2: LineSegment StartX=0 StartY=-30 StartZ=0 EndX=-5.68e-14 EndY=0 EndZ=0
    g3: ArcOfCircle CenterX=5 CenterY=-30 CenterZ=0 NormalX=0 NormalY=0 NormalZ=1 AngleXU=0 Radius=5 StartAngle=1.5708 EndAngle=3.14159
  constraints (11):
    c: Vertical(g0)
    c: Coincident(g0,g1)
    c: Horizontal(g1)
    c: PointOnObject(g2,g-2)
    c: Coincident(g2,g-3)
    c: Tangent(g3,g2) = 1.5708
    c: Tangent(g3,g1) = -1.5708
    c: DistanceX(g-3,g0) = 1
    c: DistanceY(g-3,g0) = 0
    c: DistanceY(g0) = -25
    c: Radius(g3) = 5
FEATURE [Part::Mirroring] Part__Mirroring035  label="Sketch127 (Mirror #33)"
  Base = (0,0,0)
  Normal = (0,0,1)
  Source = -> Sketch127
FEATURE [Part::FeaturePython] Connect014  # WARN: FeaturePython — macro-defined, semantics opaque (R4)
  Objects = -> [Sketch127,Part__Mirroring035]
  Tolerance = 0
FEATURE [Part::Extrusion] Extrude038
  Base = -> Connect014
  Dir = (-0.642788,0.766044,0)
  DirMode = 2
  FaceMakerClass = Part::FaceMakerBullseye
  LengthFwd = 10
  LengthRev = 0
  Solid = true
  Symmetric = true
FEATURE [Part::FeaturePython] Populate068  label="Populate LinearArray015 with Extrude038"  # WARN: FeaturePython — macro-defined, semantics opaque (R4)
  Copying = 0
  ExposePlacement = false
  MarkerShape = 1
  MarkerSize = 0
  NumElements = 0
  Object = -> Extrude038
  OutputCompounding = 1
  PlacementsTo = -> LinearArray015
  Referencing = 0
  Type = lattice2PopulateCopies.LatticePopulateCopies
  isLattice = 0
FEATURE [Part::FeaturePython] Placment036  # WARN: FeaturePython — macro-defined, semantics opaque (R4)
  AttacherType = Attacher::AttachEngine3D
  AttachmentOffset = pos=(0,450,14) rot=(0,-1,0;1.5708rad)
  AttachmentSupport = -> [Sketch120]
  ExposePlacement = true
  MapMode = 7
  MarkerShape = 1
  MarkerSize = 5
  NumElements = 1
  Placement = pos=(269.462,200.101,450) rot=(0.862856,-0.357407,-0.357407;1.71777rad)
  Type = lattice2AttachablePlacement.AttachablePlacement
  isLattice = 1
  expr: .AttachmentOffset.Base.y = <<BaseBend023>>.length / 2
FEATURE [Part::FeaturePython] Populate069  label="Populate Placment036 with Extrude011"  # WARN: FeaturePython — macro-defined, semantics opaque (R4)
  Copying = 0
  ExposePlacement = false
  MarkerShape = 1
  MarkerSize = 0
  NumElements = 0
  Object = -> Extrude011
  OutputCompounding = 2
  PlacementsTo = -> Placment036
  Referencing = 0
  Type = lattice2PopulateCopies.LatticePopulateCopies
  isLattice = 0
FEATURE [Part::FeaturePython] Placment037  # WARN: FeaturePython — macro-defined, semantics opaque (R4)
  AttacherType = Attacher::AttachEngine3D
  ExposePlacement = true
  MarkerShape = 1
  MarkerSize = 100
  NumElements = 1
  Placement = pos=(0,0,630) rot=(0,0,1;0rad)
  Type = lattice2AttachablePlacement.AttachablePlacement
  isLattice = 1
FEATURE [Sketcher::SketchObject] Sketch128
  AttachmentOffset = pos=(0,0,0) rot=(0,1,0;1.5708rad)
  AttachmentSupport = -> [Sketch120]
  ExternalGeometry = -> [Sketch127]
  FullyConstrained = true
  MapMode = 7
  Placement = pos=(318.143,151.42,0) rot=(0.281085,0.678598,0.678598;2.59356rad)
  sketch-geometry (5):
    g0: LineSegment StartX=0 StartY=0 StartZ=0 EndX=-0.0871557 EndY=-25 EndZ=0
    g1: LineSegment StartX=-0.0871557 StartY=-25 StartZ=0 EndX=3 EndY=-25 EndZ=0
    g2: LineSegment StartX=5 StartY=-23 StartZ=0 EndX=5 EndY=0 EndZ=0
    g3: ArcOfCircle CenterX=3 CenterY=-23 CenterZ=0 NormalX=0 NormalY=0 NormalZ=1 AngleXU=0 Radius=2 StartAngle=4.71239 EndAngle=6.28319
    g4: GeomPoint X=5 Y=-25 Z=0
  constraints (12):
    c: Coincident(g-1,g0)
    c: Coincident(g0,g-3)
    c: Coincident(g0,g1)
    c: Horizontal(g1)
    c: PointOnObject(g2,g-1)
    c: Vertical(g2)
    c: PointOnObject(g4,g1)
    c: PointOnObject(g4,g2)
    c: Tangent(g1,g3) = -1.5708
    c: Tangent(g2,g3) = -1.5708
    c: Radius(g3) = 2
    c: DistanceX(g2) = 5
FEATURE [Part::Mirroring] Part__Mirroring036  label="Sketch128 (Mirror #34)"
  Base = (0,0,0)
  Normal = (0,0,1)
  Source = -> Sketch128
FEATURE [Part::FeaturePython] Connect015  # WARN: FeaturePython — macro-defined, semantics opaque (R4)
  Objects = -> [Sketch128,Part__Mirroring036]
  Tolerance = 0
FEATURE [PartDesign::SubShapeBinder] Binder043
  BindCopyOnChange = 0
  BindMode = 0
  ClaimChildren = true
  Context = -> Body034 [Binder043.]
  Fuse = false
  MakeFace = true
  OffsetFill = false
  OffsetIntersection = false
  OffsetJoinType = 0
  OffsetOpenResult = false
  PartialLoad = false
  Relative = false
  Support = -> [Connect014]
  _Version = 2
  expr: Support = Connect014._self
FEATURE [PartDesign::Pad] Pad023
  Direction = (-0.642788,0.766044,0)
  Length = 3
  Length2 = 10
  Midplane = true
  Profile = -> Binder043 [Face1]
  Suppressed = false
  Type = 0
FEATURE [PartDesign::SubShapeBinder] Binder044
  BindCopyOnChange = 0
  BindMode = 0
  ClaimChildren = true
  Context = -> Body034 [Binder044.]
  Fuse = false
  MakeFace = true
  OffsetFill = false
  OffsetIntersection = false
  OffsetJoinType = 0
  OffsetOpenResult = false
  PartialLoad = false
  Relative = false
  Support = -> [Connect015]
  _Version = 2
FEATURE [PartDesign::Pad] Pad024
  BaseFeature = -> Pad023
  Direction = (0.707107,0.707107,0)
  Length = 3
  Length2 = 10
  Midplane = true
  Profile = -> Binder044
  Refine = true
  Suppressed = false
  Type = 0
FEATURE [PartDesign::Body] Body034
  Group = -> [Binder043,Pad023,Binder044,Pad024]
  Origin = -> Origin036
  Tip = -> Pad024
FEATURE [Part::FeaturePython] Populate070  label="Populate Placment037 with Body034"  # WARN: FeaturePython — macro-defined, semantics opaque (R4)
  Copying = 0
  ExposePlacement = false
  MarkerShape = 1
  MarkerSize = 0
  NumElements = 0
  Object = -> Body034
  OutputCompounding = 2
  PlacementsTo = -> Placment037
  Referencing = 0
  Type = lattice2PopulateCopies.LatticePopulateCopies
  isLattice = 0
FEATURE [Part::MultiFuse] Fusion008
  Shapes = -> [Populate064,Populate068,Populate065,Mirror016,Populate066,Populate069,Populate070]
FEATURE [PartDesign::Boolean] Boolean032
  BaseFeature = -> BaseBend023
  Group = -> [Fusion008]
  Suppressed = false
  Type = 1
  UsePlacement = true
FEATURE [PartDesign::Body] Body033
  Group = -> [Binder042,BaseBend023,Boolean032]
  Origin = -> Origin035
  Tip = -> Boolean032
FEATURE [TechDraw::DrawSVGTemplate] Template002
  Height = 210
  Orientation = 1
  Template = <path>
  Width = 297
FEATURE [TechDraw::DrawViewPart] View025
  CoarseView = false
  Direction = (0,0,1)
  Focus = 100
  HardHidden = false
  IsoCount = 0
  IsoHidden = false
  IsoVisible = false
  LockPosition = false
  Perspective = false
  Rotation = 0
  ScaleType = 0
  ScrubCount = 0
  SeamHidden = false
  SeamVisible = true
  SmoothHidden = false
  SmoothVisible = true
  Source = -> [Body033]
  X = 148.5
  XDirection = (1,0,0)
  Y = 105
FEATURE [TechDraw::DrawViewPart] View026
  CoarseView = false
  Direction = (0,-1,0)
  Focus = 100
  HardHidden = false
  IsoCount = 0
  IsoHidden = false
  IsoVisible = false
  LockPosition = false
  Perspective = false
  Rotation = 0
  Scale = 0.2
  ScaleType = 1
  ScrubCount = 0
  SeamHidden = false
  SeamVisible = true
  SmoothHidden = false
  SmoothVisible = true
  Source = -> [Body033]
  X = 58.5
  XDirection = (1,0,0)
  Y = 105
FEATURE [TechDraw::DrawViewDimension] Dimension060
  AngleOverride = false
  Arbitrary = false
  ArbitraryTolerances = false
  BoxCorners = (2) [(-39.5508,-34.9941,-1e-07),(39.5508,34.9941,1e-07)]
  EqualTolerance = true
  ExtensionAngle = 0
  FormatSpec = %.2w
  FormatSpecOverTolerance = %+.2w
  FormatSpecUnderTolerance = %+.2w
  Inverted = false
  LineAngle = 0
  LockPosition = false
  MeasureType = 1
  OverTolerance = 0
  References2D = -> [View025]
  Rotation = 0
  ScaleType = 0
  TheoreticalExact = false
  Type = 0
  UnderTolerance = 0
  X = 37.87
  Y = -31.2391
FEATURE [TechDraw::DrawViewDimension] Dimension061
  AngleOverride = false
  Arbitrary = false
  ArbitraryTolerances = false
  BoxCorners = (2) [(-39.5508,-34.9941,-1e-07),(39.5508,34.9941,1e-07)]
  EqualTolerance = true
  ExtensionAngle = 0
  FormatSpec = %.2w
  FormatSpecOverTolerance = %+.2w
  FormatSpecUnderTolerance = %+.2w
  Inverted = false
  LineAngle = 0
  LockPosition = false
  MeasureType = 1
  OverTolerance = 0
  References2D = -> [View025]
  Rotation = 0
  ScaleType = 0
  TheoreticalExact = false
  Type = 0
  UnderTolerance = 0
  X = 19.5056
  Y = 13.7964
FEATURE [TechDraw::DrawViewDimension] Dimension062
  AngleOverride = false
  Arbitrary = false
  ArbitraryTolerances = false
  BoxCorners = (2) [(-39.5508,-34.9941,-1e-07),(39.5508,34.9941,1e-07)]
  EqualTolerance = true
  ExtensionAngle = 0
  FormatSpec = %.2w
  FormatSpecOverTolerance = %+.2w
  FormatSpecUnderTolerance = %+.2w
  Inverted = false
  LineAngle = 0
  LockPosition = false
  MeasureType = 1
  OverTolerance = 0
  References2D = -> [View025]
  Rotation = 0
  ScaleType = 0
  TheoreticalExact = false
  Type = 0
  UnderTolerance = 0
  X = -29.7539
  Y = 49.0491
FEATURE [TechDraw::DrawViewDimension] Dimension063
  AngleOverride = false
  Arbitrary = false
  ArbitraryTolerances = false
  BoxCorners = (2) [(-39.5508,-34.9941,-1e-07),(39.5508,34.9941,1e-07)]
  EqualTolerance = true
  ExtensionAngle = 0
  FormatSpec = %.2w
  FormatSpecOverTolerance = %+.2w
  FormatSpecUnderTolerance = %+.2w
  Inverted = false
  LineAngle = 0
  LockPosition = false
  MeasureType = 1
  OverTolerance = 0
  References2D = -> [View025]
  Rotation = 0
  ScaleType = 0
  TheoreticalExact = false
  Type = 6
  UnderTolerance = 0
  X = 18.3829
  Y = -11.3836
FEATURE [TechDraw::DrawViewDimension] Dimension064
  AngleOverride = false
  Arbitrary = false
  ArbitraryTolerances = false
  BoxCorners = (2) [(-39.5508,-34.9941,-1e-07),(39.5508,34.9941,1e-07)]
  EqualTolerance = true
  ExtensionAngle = 0
  FormatSpec = %.2w
  FormatSpecOverTolerance = %+.2w
  FormatSpecUnderTolerance = %+.2w
  Inverted = false
  LineAngle = 0
  LockPosition = false
  MeasureType = 1
  OverTolerance = 0
  References2D = -> [View025]
  Rotation = 0
  ScaleType = 0
  TheoreticalExact = false
  Type = 6
  UnderTolerance = 0
  X = -21.5679
  Y = 26.1491
FEATURE [TechDraw::DrawViewBalloon] Balloon006
  BubbleShape = 3
  EndType = 0
  EndTypeScale = 1
  KinkLength = 5
  LockPosition = false
  OriginX = 12.8216
  OriginY = 414.679
  Rotation = 0
  ScaleType = 0
  ShapeScale = 1
  SourceView = -> View026
  Text = Оборотная сторона
  TextWrapLen = -1
  X = 248.1
  Y = 440.16
FEATURE [Part::Mirroring] Part__Mirroring037  label="Body033 (Mirror #35)"
  Base = (0,0,0)
  Normal = (1,0,0)
  Source = -> Body033
FEATURE [TechDraw::DrawPage] Page008
  KeepUpdated = true
  NextBalloonIndex = 3
  ProjectionType = 0
  Template = -> Template002
  Views = -> [View025,View026,Dimension060,Dimension061,Dimension062,Dimension063,Dimension064,Balloon006]
FEATURE [TechDraw::DrawViewPart] View027
  CoarseView = false
  Direction = (0,-1,0)
  Focus = 100
  HardHidden = false
  IsoCount = 0
  IsoHidden = false
  IsoVisible = false
  LockPosition = false
  Perspective = false
  Rotation = 0
  Scale = 0.2
  ScaleType = 1
  ScrubCount = 0
  SeamHidden = false
  SeamVisible = true
  SmoothHidden = false
  SmoothVisible = true
  Source = -> [Part__Mirroring037]
  X = 68.5
  XDirection = (1,0,0)
  Y = 105
FEATURE [TechDraw::DrawViewPart] View028
  CoarseView = false
  Direction = (0,0,1)
  Focus = 100
  HardHidden = false
  IsoCount = 0
  IsoHidden = false
  IsoVisible = false
  LockPosition = false
  Perspective = false
  Rotation = 0
  ScaleType = 0
  ScrubCount = 0
  SeamHidden = false
  SeamVisible = true
  SmoothHidden = false
  SmoothVisible = true
  Source = -> [Part__Mirroring037]
  X = 198.5
  XDirection = (1,0,0)
  Y = 105
FEATURE [TechDraw::DrawViewBalloon] Balloon007
  BubbleShape = 3
  EndType = 0
  EndTypeScale = 1
  KinkLength = 5
  LockPosition = false
  OriginX = 0
  OriginY = 389.835
  Rotation = 0
  ScaleType = 0
  ShapeScale = 1
  SourceView = -> View027
  Text = Оборотная сторона
  TextWrapLen = -1
  X = 318.895
  Y = 362.432
FEATURE [TechDraw::DrawViewDimension] Dimension065
  AngleOverride = false
  Arbitrary = false
  ArbitraryTolerances = false
  BoxCorners = (2) [(-39.5508,-34.9941,-1e-07),(39.5508,34.9941,1e-07)]
  EqualTolerance = true
  ExtensionAngle = 0
  FormatSpec = %.2w
  FormatSpecOverTolerance = %+.2w
  FormatSpecUnderTolerance = %+.2w
  Inverted = false
  LineAngle = 0
  LockPosition = false
  MeasureType = 1
  OverTolerance = 0
  References2D = -> [View028]
  Rotation = 0
  ScaleType = 0
  TheoreticalExact = false
  Type = 6
  UnderTolerance = 0
  X = -15.8371
  Y = -16.8403
FEATURE [TechDraw::DrawViewDimension] Dimension066
  AngleOverride = false
  Arbitrary = false
  ArbitraryTolerances = false
  BoxCorners = (2) [(-39.5508,-34.9941,-1e-07),(39.5508,34.9941,1e-07)]
  EqualTolerance = true
  ExtensionAngle = 0
  FormatSpec = %.2w
  FormatSpecOverTolerance = %+.2w
  FormatSpecUnderTolerance = %+.2w
  Inverted = false
  LineAngle = 0
  LockPosition = false
  MeasureType = 1
  OverTolerance = 0
  References2D = -> [View028]
  Rotation = 0
  ScaleType = 0
  TheoreticalExact = false
  Type = 6
  UnderTolerance = 0
  X = 18.2948
  Y = 24.382
FEATURE [TechDraw::DrawViewDimension] Dimension067
  AngleOverride = false
  Arbitrary = false
  ArbitraryTolerances = false
  BoxCorners = (2) [(-39.5508,-34.9941,-1e-07),(39.5508,34.9941,1e-07)]
  EqualTolerance = true
  ExtensionAngle = 0
  FormatSpec = %.2w
  FormatSpecOverTolerance = %+.2w
  FormatSpecUnderTolerance = %+.2w
  Inverted = false
  LineAngle = 0
  LockPosition = false
  MeasureType = 1
  OverTolerance = 0
  References2D = -> [View028]
  Rotation = 0
  ScaleType = 0
  TheoreticalExact = false
  Type = 0
  UnderTolerance = 0
  X = 28.7991
  Y = 46.2084
FEATURE [TechDraw::DrawViewDimension] Dimension068
  AngleOverride = false
  Arbitrary = false
  ArbitraryTolerances = false
  BoxCorners = (2) [(-39.5508,-34.9941,-1e-07),(39.5508,34.9941,1e-07)]
  EqualTolerance = true
  ExtensionAngle = 0
  FormatSpec = %.2w
  FormatSpecOverTolerance = %+.2w
  FormatSpecUnderTolerance = %+.2w
  Inverted = false
  LineAngle = 0
  LockPosition = false
  MeasureType = 1
  OverTolerance = 0
  References2D = -> [View028]
  Rotation = 0
  ScaleType = 0
  TheoreticalExact = false
  Type = 0
  UnderTolerance = 0
  X = -19.2857
  Y = 17.5456
FEATURE [TechDraw::DrawViewDimension] Dimension069
  AngleOverride = false
  Arbitrary = false
  ArbitraryTolerances = false
  BoxCorners = (2) [(-39.5508,-34.9941,-1e-07),(39.5508,34.9941,1e-07)]
  EqualTolerance = true
  ExtensionAngle = 0
  FormatSpec = %.2w
  FormatSpecOverTolerance = %+.2w
  FormatSpecUnderTolerance = %+.2w
  Inverted = false
  LineAngle = 0
  LockPosition = false
  MeasureType = 1
  OverTolerance = 0
  References2D = -> [View028]
  Rotation = 0
  ScaleType = 0
  TheoreticalExact = false
  Type = 0
  UnderTolerance = 0
  X = -38.8637
  Y = -31.9893
FEATURE [TechDraw::DrawPage] Page007
  KeepUpdated = true
  NextBalloonIndex = 4
  ProjectionType = 0
  Template = -> Template002
  Views = -> [View027,View028,Balloon007,Dimension065,Dimension066,Dimension067,Dimension068,Dimension069]
FEATURE [Part::Feature] Unfold015
  shape: bbox 118.5 x 1 x 900 mm, 59 faces (baked)
FEATURE [Sketcher::SketchObject] Unfold_Sketch016
  FullyConstrained = false
  sketch-geometry (57):
    g0: LineSegment StartX=-900 StartY=353.062 StartZ=0 EndX=-900 EndY=244.563 EndZ=0
    g1: ArcOfCircle CenterX=-895 CenterY=244.563 CenterZ=0 NormalX=0 NormalY=0 NormalZ=1 AngleXU=-1.5708 Radius=5 StartAngle=4.71239 EndAngle=6.28319
    g2: LineSegment StartX=-5 StartY=239.563 StartZ=0 EndX=-895 EndY=239.563 EndZ=0
    g3: ArcOfCircle CenterX=-5 CenterY=244.563 CenterZ=0 NormalX=0 NormalY=0 NormalZ=1 AngleXU=-1.5708 Radius=5 StartAngle=-4.33076e-11 EndAngle=1.5708
    g4: LineSegment StartX=0 StartY=353.062 StartZ=0 EndX=0 EndY=244.563 EndZ=0
    g5: ArcOfCircle CenterX=-5 CenterY=353.062 CenterZ=0 NormalX=0 NormalY=0 NormalZ=1 AngleXU=1.5708 Radius=5 StartAngle=4.71239 EndAngle=6.28319
    g6: LineSegment StartX=-5 StartY=358.062 StartZ=0 EndX=-20 EndY=358.062 EndZ=0
    g7: ArcOfCircle CenterX=-20 CenterY=353.062 CenterZ=0 NormalX=0 NormalY=0 NormalZ=1 AngleXU=-1.5708 Radius=5 StartAngle=3.14159 EndAngle=4.71239
    g8: LineSegment StartX=-25 StartY=353.062 StartZ=0 EndX=-25 EndY=336.91 EndZ=0
    g9: ArcOfCircle CenterX=-27 CenterY=336.91 CenterZ=0 NormalX=0 NormalY=0 NormalZ=1 AngleXU=-2e-16 Radius=2 StartAngle=4.71239 EndAngle=6.28319
    g10: LineSegment StartX=-27 StartY=334.91 StartZ=0 EndX=-73 EndY=334.91 EndZ=0
    g11: ArcOfCircle CenterX=-73 CenterY=336.91 CenterZ=0 NormalX=0 NormalY=0 NormalZ=1 AngleXU=-2e-16 Radius=2 StartAngle=3.14159 EndAngle=4.71239
    g12: LineSegment StartX=-75 StartY=336.91 StartZ=0 EndX=-75 EndY=353.062 EndZ=0
    g13: ArcOfCircle CenterX=-80 CenterY=353.062 CenterZ=0 NormalX=0 NormalY=0 NormalZ=1 AngleXU=-1.5708 Radius=5 StartAngle=1.5708 EndAngle=3.14159
    g14: LineSegment StartX=-80 StartY=358.062 StartZ=0 EndX=-600 EndY=358.062 EndZ=0
    g15: ArcOfCircle CenterX=-600 CenterY=353.062 CenterZ=0 NormalX=0 NormalY=0 NormalZ=1 AngleXU=-1.5708 Radius=5 StartAngle=3.14159 EndAngle=4.71239
    g16: LineSegment StartX=-605 StartY=339.758 StartZ=0 EndX=-605 EndY=353.062 EndZ=0
    g17: ArcOfCircle CenterX=-607 CenterY=339.758 CenterZ=0 NormalX=0 NormalY=0 NormalZ=1 AngleXU=-1.5708 Radius=2 StartAngle=0 EndAngle=1.5708
    g18: LineSegment StartX=-653 StartY=337.758 StartZ=0 EndX=-607 EndY=337.758 EndZ=0
    g19: ArcOfCircle CenterX=-653 CenterY=339.758 CenterZ=0 NormalX=0 NormalY=0 NormalZ=1 AngleXU=-1.5708 Radius=2 StartAngle=4.71239 EndAngle=6.28319
    g20: LineSegment StartX=-655 StartY=353.062 StartZ=0 EndX=-655 EndY=339.758 EndZ=0
    g21: ArcOfCircle CenterX=-660 CenterY=353.062 CenterZ=0 NormalX=0 NormalY=0 NormalZ=1 AngleXU=-1.5708 Radius=5 StartAngle=1.5708 EndAngle=3.14159
    g22: LineSegment StartX=-660 StartY=358.062 StartZ=0 EndX=-820 EndY=358.062 EndZ=0
    g23: ArcOfCircle CenterX=-820 CenterY=353.062 CenterZ=0 NormalX=0 NormalY=0 NormalZ=1 AngleXU=-1.5708 Radius=5 StartAngle=3.14159 EndAngle=4.71239
    g24: LineSegment StartX=-825 StartY=353.062 StartZ=0 EndX=-825 EndY=336.91 EndZ=0
    g25: ArcOfCircle CenterX=-827 CenterY=336.91 CenterZ=0 NormalX=0 NormalY=0 NormalZ=1 AngleXU=-2e-16 Radius=2 StartAngle=4.71239 EndAngle=6.28319
    g26: LineSegment StartX=-827 StartY=334.91 StartZ=0 EndX=-873 EndY=334.91 EndZ=0
    g27: ArcOfCircle CenterX=-873 CenterY=336.91 CenterZ=0 NormalX=0 NormalY=0 NormalZ=1 AngleXU=-2e-16 Radius=2 StartAngle=3.14159 EndAngle=4.71239
    g28: LineSegment StartX=-875 StartY=336.91 StartZ=0 EndX=-875 EndY=353.062 EndZ=0
    g29: ArcOfCircle CenterX=-880 CenterY=353.062 CenterZ=0 NormalX=0 NormalY=0 NormalZ=1 AngleXU=-1.5708 Radius=5 StartAngle=1.5708 EndAngle=3.14159
    g30: LineSegment StartX=-880 StartY=358.062 StartZ=0 EndX=-895 EndY=358.062 EndZ=0
    g31: ArcOfCircle CenterX=-895 CenterY=353.062 CenterZ=0 NormalX=0 NormalY=0 NormalZ=1 AngleXU=1.5708 Radius=5 StartAngle=-4.33147e-11 EndAngle=1.5708
    g32: LineSegment StartX=-895.4 StartY=279.663 StartZ=0 EndX=-894.6 EndY=279.663 EndZ=0
    g33: ArcOfCircle CenterX=-894.6 CenterY=278.063 CenterZ=0 NormalX=0 NormalY=0 NormalZ=1 AngleXU=1.5708 Radius=1.6 StartAngle=3.14159 EndAngle=6.28319
    g34: LineSegment StartX=-895.4 StartY=276.463 StartZ=0 EndX=-894.6 EndY=276.463 EndZ=0
    g35: ArcOfCircle CenterX=-895.4 CenterY=278.063 CenterZ=0 NormalX=0 NormalY=0 NormalZ=1 AngleXU=1.5708 Radius=1.6 StartAngle=0 EndAngle=3.14159
    g36: LineSegment StartX=-895.4 StartY=271.363 StartZ=0 EndX=-894.6 EndY=271.363 EndZ=0
    g37: ArcOfCircle CenterX=-894.6 CenterY=269.763 CenterZ=0 NormalX=0 NormalY=0 NormalZ=1 AngleXU=1.5708 Radius=1.6 StartAngle=3.14159 EndAngle=6.28319
    g38: LineSegment StartX=-895.4 StartY=268.163 StartZ=0 EndX=-894.6 EndY=268.163 EndZ=0
    g39: ArcOfCircle CenterX=-895.4 CenterY=269.763 CenterZ=0 NormalX=0 NormalY=0 NormalZ=1 AngleXU=1.5708 Radius=1.6 StartAngle=0 EndAngle=3.14159
    g40: LineSegment StartX=-5.4 StartY=279.663 StartZ=0 EndX=-4.6 EndY=279.663 EndZ=0
    g41: ArcOfCircle CenterX=-4.6 CenterY=278.063 CenterZ=0 NormalX=0 NormalY=0 NormalZ=1 AngleXU=1.5708 Radius=1.6 StartAngle=3.14159 EndAngle=6.28319
    g42: LineSegment StartX=-5.4 StartY=276.463 StartZ=0 EndX=-4.6 EndY=276.463 EndZ=0
    g43: ArcOfCircle CenterX=-5.4 CenterY=278.063 CenterZ=0 NormalX=0 NormalY=0 NormalZ=1 AngleXU=1.5708 Radius=1.6 StartAngle=1.15e-14 EndAngle=3.14159
    g44: LineSegment StartX=-5.4 StartY=271.363 StartZ=0 EndX=-4.6 EndY=271.363 EndZ=0
    g45: ArcOfCircle CenterX=-4.6 CenterY=269.763 CenterZ=0 NormalX=0 NormalY=0 NormalZ=1 AngleXU=1.5708 Radius=1.6 StartAngle=3.14159 EndAngle=6.28319
    g46: LineSegment StartX=-5.4 StartY=268.163 StartZ=0 EndX=-4.6 EndY=268.163 EndZ=0
    g47: ArcOfCircle CenterX=-5.4 CenterY=269.763 CenterZ=0 NormalX=0 NormalY=0 NormalZ=1 AngleXU=1.5708 Radius=1.6 StartAngle=-7.1e-15 EndAngle=3.14159
    g48: Circle CenterX=-864 CenterY=327.41 CenterZ=0 NormalX=0 NormalY=0 NormalZ=1 AngleXU=-2e-16 Radius=1.7
    g49: Circle CenterX=-836 CenterY=327.41 CenterZ=0 NormalX=0 NormalY=0 NormalZ=1 AngleXU=-2e-16 Radius=1.7
    g50: Circle CenterX=-890 CenterY=255.563 CenterZ=0 NormalX=0 NormalY=0 NormalZ=-1 AngleXU=0 Radius=1.7
    g51: Circle CenterX=-670 CenterY=245.563 CenterZ=0 NormalX=0 NormalY=0 NormalZ=-1 AngleXU=0 Radius=1.7
    g52: Circle CenterX=-64 CenterY=327.41 CenterZ=0 NormalX=0 NormalY=0 NormalZ=1 AngleXU=-2e-16 Radius=1.7
    g53: Circle CenterX=-36 CenterY=327.41 CenterZ=0 NormalX=0 NormalY=0 NormalZ=1 AngleXU=-2e-16 Radius=1.7
    g54: Circle CenterX=-10 CenterY=255.563 CenterZ=0 NormalX=0 NormalY=0 NormalZ=-1 AngleXU=0 Radius=1.7
    g55: Circle CenterX=-450 CenterY=255.563 CenterZ=0 NormalX=0 NormalY=0 NormalZ=-1 AngleXU=0 Radius=1.7
    g56: Circle CenterX=-230 CenterY=245.563 CenterZ=0 NormalX=0 NormalY=0 NormalZ=-1 AngleXU=0 Radius=1.7
FEATURE [Sketcher::SketchObject] Unfold_Sketch_Outline012
  FullyConstrained = false
  sketch-geometry (32):
    g0: LineSegment StartX=-900 StartY=353.062 StartZ=0 EndX=-900 EndY=244.563 EndZ=0
    g1: ArcOfCircle CenterX=-895 CenterY=244.563 CenterZ=0 NormalX=0 NormalY=0 NormalZ=1 AngleXU=-1.5708 Radius=5 StartAngle=4.71239 EndAngle=6.28319
    g2: LineSegment StartX=-5 StartY=239.563 StartZ=0 EndX=-895 EndY=239.563 EndZ=0
    g3: ArcOfCircle CenterX=-5 CenterY=244.563 CenterZ=0 NormalX=0 NormalY=0 NormalZ=1 AngleXU=-1.5708 Radius=5 StartAngle=-4.33076e-11 EndAngle=1.5708
    g4: LineSegment StartX=0 StartY=353.062 StartZ=0 EndX=0 EndY=244.563 EndZ=0
    g5: ArcOfCircle CenterX=-5 CenterY=353.062 CenterZ=0 NormalX=0 NormalY=0 NormalZ=1 AngleXU=1.5708 Radius=5 StartAngle=4.71239 EndAngle=6.28319
    g6: LineSegment StartX=-5 StartY=358.062 StartZ=0 EndX=-20 EndY=358.062 EndZ=0
    g7: ArcOfCircle CenterX=-20 CenterY=353.062 CenterZ=0 NormalX=0 NormalY=0 NormalZ=1 AngleXU=-1.5708 Radius=5 StartAngle=3.14159 EndAngle=4.71239
    g8: LineSegment StartX=-25 StartY=353.062 StartZ=0 EndX=-25 EndY=336.91 EndZ=0
    g9: ArcOfCircle CenterX=-27 CenterY=336.91 CenterZ=0 NormalX=0 NormalY=0 NormalZ=1 AngleXU=-2e-16 Radius=2 StartAngle=4.71239 EndAngle=6.28319
    g10: LineSegment StartX=-27 StartY=334.91 StartZ=0 EndX=-73 EndY=334.91 EndZ=0
    g11: ArcOfCircle CenterX=-73 CenterY=336.91 CenterZ=0 NormalX=0 NormalY=0 NormalZ=1 AngleXU=-2e-16 Radius=2 StartAngle=3.14159 EndAngle=4.71239
    g12: LineSegment StartX=-75 StartY=336.91 StartZ=0 EndX=-75 EndY=353.062 EndZ=0
    g13: ArcOfCircle CenterX=-80 CenterY=353.062 CenterZ=0 NormalX=0 NormalY=0 NormalZ=1 AngleXU=-1.5708 Radius=5 StartAngle=1.5708 EndAngle=3.14159
    g14: LineSegment StartX=-80 StartY=358.062 StartZ=0 EndX=-600 EndY=358.062 EndZ=0
    g15: ArcOfCircle CenterX=-600 CenterY=353.062 CenterZ=0 NormalX=0 NormalY=0 NormalZ=1 AngleXU=-1.5708 Radius=5 StartAngle=3.14159 EndAngle=4.71239
    g16: LineSegment StartX=-605 StartY=339.758 StartZ=0 EndX=-605 EndY=353.062 EndZ=0
    g17: ArcOfCircle CenterX=-607 CenterY=339.758 CenterZ=0 NormalX=0 NormalY=0 NormalZ=1 AngleXU=-1.5708 Radius=2 StartAngle=0 EndAngle=1.5708
    g18: LineSegment StartX=-653 StartY=337.758 StartZ=0 EndX=-607 EndY=337.758 EndZ=0
    g19: ArcOfCircle CenterX=-653 CenterY=339.758 CenterZ=0 NormalX=0 NormalY=0 NormalZ=1 AngleXU=-1.5708 Radius=2 StartAngle=4.71239 EndAngle=6.28319
    g20: LineSegment StartX=-655 StartY=353.062 StartZ=0 EndX=-655 EndY=339.758 EndZ=0
    g21: ArcOfCircle CenterX=-660 CenterY=353.062 CenterZ=0 NormalX=0 NormalY=0 NormalZ=1 AngleXU=-1.5708 Radius=5 StartAngle=1.5708 EndAngle=3.14159
    g22: LineSegment StartX=-660 StartY=358.062 StartZ=0 EndX=-820 EndY=358.062 EndZ=0
    g23: ArcOfCircle CenterX=-820 CenterY=353.062 CenterZ=0 NormalX=0 NormalY=0 NormalZ=1 AngleXU=-1.5708 Radius=5 StartAngle=3.14159 EndAngle=4.71239
    g24: LineSegment StartX=-825 StartY=353.062 StartZ=0 EndX=-825 EndY=336.91 EndZ=0
    g25: ArcOfCircle CenterX=-827 CenterY=336.91 CenterZ=0 NormalX=0 NormalY=0 NormalZ=1 AngleXU=-2e-16 Radius=2 StartAngle=4.71239 EndAngle=6.28319
    g26: LineSegment StartX=-827 StartY=334.91 StartZ=0 EndX=-873 EndY=334.91 EndZ=0
    g27: ArcOfCircle CenterX=-873 CenterY=336.91 CenterZ=0 NormalX=0 NormalY=0 NormalZ=1 AngleXU=-2e-16 Radius=2 StartAngle=3.14159 EndAngle=4.71239
    g28: LineSegment StartX=-875 StartY=336.91 StartZ=0 EndX=-875 EndY=353.062 EndZ=0
    g29: ArcOfCircle CenterX=-880 CenterY=353.062 CenterZ=0 NormalX=0 NormalY=0 NormalZ=1 AngleXU=-1.5708 Radius=5 StartAngle=1.5708 EndAngle=3.14159
    g30: LineSegment StartX=-880 StartY=358.062 StartZ=0 EndX=-895 EndY=358.062 EndZ=0
    g31: ArcOfCircle CenterX=-895 CenterY=353.062 CenterZ=0 NormalX=0 NormalY=0 NormalZ=1 AngleXU=1.5708 Radius=5 StartAngle=-4.33147e-11 EndAngle=1.5708
FEATURE [Sketcher::SketchObject] Unfold_Sketch_Internal012
  FullyConstrained = false
  sketch-geometry (25):
    g0: LineSegment StartX=-895.4 StartY=271.363 StartZ=0 EndX=-894.6 EndY=271.363 EndZ=0
    g1: ArcOfCircle CenterX=-894.6 CenterY=269.763 CenterZ=0 NormalX=0 NormalY=0 NormalZ=1 AngleXU=1.5708 Radius=1.6 StartAngle=3.14159 EndAngle=6.28319
    g2: LineSegment StartX=-895.4 StartY=268.163 StartZ=0 EndX=-894.6 EndY=268.163 EndZ=0
    g3: ArcOfCircle CenterX=-895.4 CenterY=269.763 CenterZ=0 NormalX=0 NormalY=0 NormalZ=1 AngleXU=1.5708 Radius=1.6 StartAngle=0 EndAngle=3.14159
    g4: LineSegment StartX=-895.4 StartY=279.663 StartZ=0 EndX=-894.6 EndY=279.663 EndZ=0
    g5: ArcOfCircle CenterX=-894.6 CenterY=278.063 CenterZ=0 NormalX=0 NormalY=0 NormalZ=1 AngleXU=1.5708 Radius=1.6 StartAngle=3.14159 EndAngle=6.28319
    g6: LineSegment StartX=-895.4 StartY=276.463 StartZ=0 EndX=-894.6 EndY=276.463 EndZ=0
    g7: ArcOfCircle CenterX=-895.4 CenterY=278.063 CenterZ=0 NormalX=0 NormalY=0 NormalZ=1 AngleXU=1.5708 Radius=1.6 StartAngle=0 EndAngle=3.14159
    g8: LineSegment StartX=-5.4 StartY=279.663 StartZ=0 EndX=-4.6 EndY=279.663 EndZ=0
    g9: ArcOfCircle CenterX=-4.6 CenterY=278.063 CenterZ=0 NormalX=0 NormalY=0 NormalZ=1 AngleXU=1.5708 Radius=1.6 StartAngle=3.14159 EndAngle=6.28319
    g10: LineSegment StartX=-5.4 StartY=276.463 StartZ=0 EndX=-4.6 EndY=276.463 EndZ=0
    g11: ArcOfCircle CenterX=-5.4 CenterY=278.063 CenterZ=0 NormalX=0 NormalY=0 NormalZ=1 AngleXU=1.5708 Radius=1.6 StartAngle=1.15e-14 EndAngle=3.14159
    g12: LineSegment StartX=-5.4 StartY=271.363 StartZ=0 EndX=-4.6 EndY=271.363 EndZ=0
    g13: ArcOfCircle CenterX=-4.6 CenterY=269.763 CenterZ=0 NormalX=0 NormalY=0 NormalZ=1 AngleXU=1.5708 Radius=1.6 StartAngle=3.14159 EndAngle=6.28319
    g14: LineSegment StartX=-5.4 StartY=268.163 StartZ=0 EndX=-4.6 EndY=268.163 EndZ=0
    g15: ArcOfCircle CenterX=-5.4 CenterY=269.763 CenterZ=0 NormalX=0 NormalY=0 NormalZ=1 AngleXU=1.5708 Radius=1.6 StartAngle=-7.1e-15 EndAngle=3.14159
    g16: Circle CenterX=-836 CenterY=327.41 CenterZ=0 NormalX=0 NormalY=0 NormalZ=1 AngleXU=-2e-16 Radius=1.7
    g17: Circle CenterX=-864 CenterY=327.41 CenterZ=0 NormalX=0 NormalY=0 NormalZ=1 AngleXU=-2e-16 Radius=1.7
    g18: Circle CenterX=-890 CenterY=255.563 CenterZ=0 NormalX=0 NormalY=0 NormalZ=-1 AngleXU=0 Radius=1.7
    g19: Circle CenterX=-670 CenterY=245.563 CenterZ=0 NormalX=0 NormalY=0 NormalZ=-1 AngleXU=0 Radius=1.7
    g20: Circle CenterX=-36 CenterY=327.41 CenterZ=0 NormalX=0 NormalY=0 NormalZ=1 AngleXU=-2e-16 Radius=1.7
    g21: Circle CenterX=-64 CenterY=327.41 CenterZ=0 NormalX=0 NormalY=0 NormalZ=1 AngleXU=-2e-16 Radius=1.7
    g22: Circle CenterX=-10 CenterY=255.563 CenterZ=0 NormalX=0 NormalY=0 NormalZ=-1 AngleXU=0 Radius=1.7
    g23: Circle CenterX=-450 CenterY=255.563 CenterZ=0 NormalX=0 NormalY=0 NormalZ=-1 AngleXU=0 Radius=1.7
    g24: Circle CenterX=-230 CenterY=245.563 CenterZ=0 NormalX=0 NormalY=0 NormalZ=-1 AngleXU=0 Radius=1.7
FEATURE [Sketcher::SketchObject] Unfold_Sketch_bends015
  FullyConstrained = false
  sketch-geometry (5):
    g0: LineSegment StartX=-900 StartY=342.91 StartZ=0 EndX=-875 EndY=342.91 EndZ=0
    g1: LineSegment StartX=-825 StartY=342.91 StartZ=0 EndX=-655 EndY=342.91 EndZ=0
    g2: LineSegment StartX=-605 StartY=342.91 StartZ=0 EndX=-75 EndY=342.91 EndZ=0
    g3: LineSegment StartX=-25 StartY=342.91 StartZ=0 EndX=0 EndY=342.91 EndZ=0
    g4: LineSegment StartX=-900 StartY=259.738 StartZ=0 EndX=0 EndY=259.738 EndZ=0
FEATURE [Part::Mirroring] Part__Mirroring038  label="Unfold_Sketch016 (Mirror #36)"
  Base = (0,0,0)
  Normal = (1,0,0)
  Source = -> Unfold_Sketch016
FEATURE [App::DocumentObjectGroup] Group011  label="door_ss_Group"
  Group = -> [Page008,Page007,Part__Mirroring037,Unfold015,Unfold_Sketch016,Unfold_Sketch_Outline012,Unfold_Sketch_Internal012,Unfold_Sketch_bends015,Part__Mirroring038]
FEATURE [App::DocumentObjectGroup] Group003  label="ss_Group"
  Group = -> [Group004,Group005,Group006,Group007,Group008,Group009,Unfold_Sketch013,Group011]
note: 3 file-system paths scrubbed to <path> (originals preserved in the JSON sidecar)

RESOLVED EXTERNAL PARTS (link-assembly join: the EXTERNAL_REF files above that resolve inside this repo's crawl, each included once):
---- part ../ULZ-P02-14W.FCStd = doc fcstd_d946428e1785 ----
FCSTD DOCUMENT  (FreeCAD 1.1R38827 (Git))
Label: ULZ-P02-14W
License: All rights reserved
LicenseURL: http://en.wikipedia.org/wiki/All_rights_reserved
objects: Sketcher::SketchObject×4, Part::FeaturePython×4, App::DocumentObjectGroup×3, Path::FeaturePython×3, App::FeaturePython×1, Part::Part2DObjectPython×1, PartDesign::SubShapeBinder×1, PartDesign::Pad×1, PartDesign::CoordinateSystem×1, PartDesign::Body×1
note: 20 computed .brp shape members not serialized (recipe doc carries the construction recipe); baked Part::Feature solids carry a one-line shape summary decoded from their .brp

FEATURE [Sketcher::SketchObject] Sketch  label="holes"
  ArcFitTolerance = 0
  FullyConstrained = true
  MakeInternals = false
  sketch-geometry (3):
    g0: Circle CenterX=-4.15 CenterY=445 CenterZ=0 NormalX=0 NormalY=0 NormalZ=1 AngleXU=0 Radius=1.6
    g1: Circle CenterX=4.15 CenterY=-445 CenterZ=0 NormalX=0 NormalY=0 NormalZ=1 AngleXU=0 Radius=1.6
    g2: GeomPoint [constr] X=-9.05 Y=0 Z=0
  constraints (8):
    c: Symmetric(g1,g0,g-1)
    c: Distance(g0,g1) = 890.039
    c: PointOnObject(g2,g-1)
    c: DistanceX(g2,g0) = 4.9
    c: DistanceX(g2) = -9.05
    c: DistanceY(g1,g0) = 890
    c: Equal(g1,g0)
    c: Diameter(g1) = 3.2
FEATURE [App::FeaturePython] SetupSheet  # Path/CAM operation (typed FeaturePython)
  ClearanceHeightExpression = OpStockZMax+SetupSheet.ClearanceHeightOffset
  ClearanceHeightOffset = 5
  CoolantMode = 0
  CoolantModes = None | Flood | Mist
  FinalDepthExpression = -0.1 mm
  HorizRapid = 0
  ProfileDirection = 1
  ProfileSide = 0
  ProfileUseComp = true
  ProfileprocessCircles = true
  ProfileprocessHoles = true
  ProfileprocessPerimeter = true
  SafeHeightExpression = OpStockZMax+SetupSheet.SafeHeightOffset
  SafeHeightOffset = 3
  StartDepthExpression = 3 mm
  StepDownExpression = 4 mm
  VertRapid = 0
FEATURE [Part::Part2DObjectPython] Clone2D  label="Model-Sketch"  # Draft 2D object (typed FeaturePython)
  Fuse = false
  Objects = -> [Sketch]
  PathResource = Model
  Placement = pos=(-5.75,446.581,0) rot=(0,0,1;0rad)
  Scale = (1,1,1)
FEATURE [App::DocumentObjectGroup] Model
  Group = -> [Clone2D]
FEATURE [Part::FeaturePython] ToolBit  label="3.175mm Endmill"  # Path/CAM toolbit (typed FeaturePython)
  BitPropertyNames = Chipload | CuttingEdgeHeight | Diameter | Flutes | Length | Material | ShankDiameter | SpindleDirection
  BitShape = <path>
  Chipload = 0
  CuttingEdgeHeight = 30
  Diameter = 3.175
  Flutes = 0
  Length = 10
  Material = 0
  ShankDiameter = 3
  ShapeName = endmill
  SpindleDirection = 0
FEATURE [Path::FeaturePython] __175mm_Endmill  label="3.175mm Endmill001"  # Path/CAM operation (typed FeaturePython)
  HorizFeed = 33.3333
  HorizRapid = 0
  SpindleDir = 0
  SpindleSpeed = 18000
  Tool = -> ToolBit
  ToolNumber = 1
  VertFeed = 8.33333
  VertRapid = 0
  expr: HorizRapid = SetupSheet.HorizRapid
  expr: VertRapid = SetupSheet.VertRapid
FEATURE [App::DocumentObjectGroup] Tools
  Group = -> [__175mm_Endmill]
FEATURE [Part::FeaturePython] Stock  # WARN: FeaturePython — macro-defined, semantics opaque (R4)
  Base = -> Model
  ExtXneg = 1
  ExtXpos = 1
  ExtYneg = 1
  ExtYpos = 1
  ExtZneg = 0
  ExtZpos = 1
  Placement = pos=(-5.89217,-448.284,0) rot=(0,0,1;0rad)
  StockType = FromBase
FEATURE [Path::FeaturePython] Profile  # Path/CAM operation (typed FeaturePython)
  Active = true
  AreaParams:
    Tolerance = 1e-07
    FitArcs = True
    Simplify = False
    CleanDistance = 0.0
    Accuracy = 0.01
    Unit = 1.0
    MinArcPoints = 4
    MaxArcPoints = 100
    ClipperScale = 10000000.0
    Fill = 0
    Coplanar = 0
    Reorient = True
    Outline = False
    Explode = False
    OpenMode = 0
    Deflection = 0.01
    SubjectFill = 0
    ClipFill = 0
    Offset = -1.5875
    ExtraPass = 0
    Stepover = 0.0
    LastStepover = 0.0
    JoinType = 0
    EndType = 0
    MiterLimit = 2.0
    RoundPrecision = 0.0
    PocketMode = 0
    ToolRadius = 1.0
    PocketExtraOffset = 0.0
    PocketStepover = 0.0
    PocketLastStepover = 0.0
    FromCenter = False
    Angle = 45.0
    AngleShift = 0.0
    Shift = 0.0
    Thicken = False
    SectionCount = -1
    Stepdown = 1.0
    SectionOffset = 0.0
    SectionTolerance = 1e-06
    SectionMode = 2
    Project = False
  ClearanceHeight = 6
  CoolantMode = 0
  CycleTime = 00:00:57
  Direction = 1
  FinalDepth = -0.1
  HandleMultipleFeatures = 0
  JoinType = 0
  MiterLimit = 0.1
  OffsetExtra = 0
  OpFinalDepth = 0
  OpStartDepth = 1
  OpStockZMax = 1
  OpStockZMin = 0
  OpToolDiameter = 3.175
  PathParams = {'orientation': 1, 'feedrate': 33.333333333333336, 'feedrate_v': 8.333333333333334, 'verbose': True, 'resume_height': 4.0, 'retraction': 6.0, 'return_end': True, 'preamble': False}
  SafeHeight = 4
  Side = 1
  SplitArcs = false
  StartDepth = 3
  StartPoint = (0,0,0)
  StepDown = 4
  ToolController = -> __175mm_Endmill
  UseComp = true
  UseStartPoint = false
  processCircles = true
  processHoles = true
  processPerimeter = true
  expr: ClearanceHeight = OpStockZMax + SetupSheet.ClearanceHeightOffset
  expr: FinalDepth = -0.1 mm
  expr: SafeHeight = OpStockZMax + SetupSheet.SafeHeightOffset
  expr: StartDepth = 3 mm
  expr: StepDown = 4 mm
FEATURE [App::DocumentObjectGroup] Operations
  Group = -> [Profile]
FEATURE [Path::FeaturePython] Job  # Path/CAM operation (typed FeaturePython)
  CycleTime = 00:00:57
  Fixtures = G54
  GeometryTolerance = 0.01
  JobType = 0
  LastPostProcessDate = 2023-12-11 14:23:56.391449
  LastPostProcessOutput = <userpath>/2CAF-B51C/Job-0.tap
  Model = -> Model
  Operations = -> Operations
  OrderOutputBy = 2
  PostProcessor = 3
  PostProcessorOutputFile = %j.tap
  SetupSheet = -> SetupSheet
  SplitOutput = true
  Stock = -> Stock
  Tools = -> Tools
FEATURE [Part::FeaturePython] BoundBox  label="BoundBox of Model-Sketch"  # WARN: FeaturePython — macro-defined, semantics opaque (R4)
  Center = (-5.75,446.581,0)
  CompoundTraversal = 0
  OrientMode = 0
  Padding = 0
  Precision = false
  ScaleFactor = 1
  ShapeLink = -> Clone2D
  Size = (11.5,893.177,0)
FEATURE [Sketcher::SketchObject] Sketch001
  ArcFitTolerance = 0
  FullyConstrained = true
  MakeInternals = false
  Placement = pos=(0,0,0) rot=(1,0,0;1.5708rad)
  sketch-geometry (7):
    g0: LineSegment StartX=-7.3 StartY=1.25 StartZ=0 EndX=7.3 EndY=1.25 EndZ=0
    g1: GeomPoint [constr] X=0 Y=9.25 Z=0
    g2: ArcOfEllipse CenterX=5.1e-15 CenterY=1.25 CenterZ=0 NormalX=0 NormalY=0 NormalZ=1 MajorRadius=8 MinorRadius=7.3 AngleXU=-1.5708 StartAngle=1.5708 EndAngle=4.71239
    g3: LineSegment [constr] StartX=1e-14 StartY=-6.75 StartZ=0 EndX=0 EndY=9.25 EndZ=0
    g4: LineSegment [constr] StartX=7.3 StartY=1.25 StartZ=0 EndX=-7.3 EndY=1.25 EndZ=0
    g5: GeomPoint [constr] X=7.7e-15 Y=-2.02261 Z=0
    g6: GeomPoint [constr] X=3e-15 Y=4.52261 Z=0
  constraints (9):
    c: DistanceX(g0,g0) = 14.6
    c: PointOnObject(g1,g-2)
    c: InternalAlignment(g3-g6 -> g2) x4
    c: Coincident(g3,g1)
    c: Perpendicular(g2,g0) = 4.71239
    c: Perpendicular(g2,g0) = 1.5708
    c: Horizontal(g0)
    c: DistanceY(g2,g1) = 8
    c: DistanceY(g-1,g2) = 1.25
FEATURE [Sketcher::SketchObject] Sketch002
  ArcFitTolerance = 0
  FullyConstrained = true
  MakeInternals = false
  Placement = pos=(0,0,0) rot=(1,0,0;1.5708rad)
  sketch-geometry (8):
    g0: LineSegment StartX=-9 StartY=-5e-16 StartZ=0 EndX=9 EndY=-5e-16 EndZ=0
    g1: LineSegment [constr] StartX=-9 StartY=-5e-16 StartZ=0 EndX=0 EndY=11 EndZ=0
    g2: LineSegment [constr] StartX=7e-16 StartY=11 StartZ=0 EndX=9 EndY=0 EndZ=0
    g3: ArcOfEllipse CenterX=0 CenterY=0 CenterZ=0 NormalX=0 NormalY=0 NormalZ=1 MajorRadius=11 MinorRadius=9 AngleXU=1.5708 StartAngle=4.71239 EndAngle=7.85398
    g4: LineSegment [constr] StartX=7e-16 StartY=11 StartZ=0 EndX=-7e-16 EndY=-11 EndZ=0
    g5: LineSegment [constr] StartX=-9 StartY=6e-16 StartZ=0 EndX=9 EndY=-6e-16 EndZ=0
    g6: GeomPoint [constr] X=7e-16 Y=6.32456 Z=0
    g7: GeomPoint [constr] X=-4e-16 Y=-6.32456 Z=0
  constraints (12):
    c: DistanceX(g0,g0) = 18
    c: Coincident(g0,g1)
    c: Coincident(g1,g2)
    c: Coincident(g2,g0)
    c: Distance(g1,g0) = 11
    c: InternalAlignment(g4-g7 -> g3) x4
    c: Perpendicular(g3,g0) = 1.5708
    c: Equal(g1,g2)
    c: Horizontal(g0)
    c: Coincident(g3,g0)
    c: Coincident(g4,g1)
    c: Coincident(g3,g-1)
FEATURE [PartDesign::SubShapeBinder] Binder
  BindCopyOnChange = 0
  BindMode = 0
  ClaimChildren = true
  Context = -> Body [Binder.]
  Fuse = false
  MakeFace = true
  OffsetFill = false
  OffsetIntersection = false
  OffsetJoinType = 0
  OffsetOpenResult = false
  PartialLoad = false
  Relative = true
  Support = -> [Sketch001]
  _Version = 2
FEATURE [PartDesign::Pad] Pad
  Direction = (0,1,0)
  Length = 820
  Length2 = 10
  Midplane = true
  Profile = -> Binder
  Suppressed = false
  Type = 0
FEATURE [PartDesign::CoordinateSystem] Local_CS
  AttacherType = Attacher::AttachEngine3D
  AttachmentSupport = -> [XY_Plane]
  MapMode = 5
FEATURE [PartDesign::Body] Body
  AllowCompound = false
  Group = -> [Binder,Pad,Local_CS]
  Origin = -> Origin
  Tip = -> Pad
FEATURE [Sketcher::SketchObject] Sketch003
  ArcFitTolerance = 0
  FullyConstrained = true
  MakeInternals = false
  Placement = pos=(0,416,0) rot=(0,0,1;0rad)
  sketch-geometry (8):
    g0: LineSegment StartX=-9 StartY=29.05 StartZ=0 EndX=-9 EndY=0 EndZ=0
    g1: LineSegment StartX=-9 StartY=0 StartZ=0 EndX=9 EndY=0 EndZ=0
    g2: LineSegment StartX=9 StartY=0 StartZ=0 EndX=9 EndY=21.4 EndZ=0
    g3: LineSegment StartX=9 StartY=21.4 StartZ=0 EndX=0.256748 EndY=32.3031 EndZ=0
    g4: ArcOfCircle CenterX=-3.8 CenterY=29.05 CenterZ=0 NormalX=0 NormalY=0 NormalZ=1 AngleXU=0 Radius=5.2 StartAngle=0.675901 EndAngle=3.14159
    g5: GeomPoint [constr] X=-9 Y=43.8466 Z=0
    g6: LineSegment [constr] StartX=0 StartY=34.25 StartZ=0 EndX=-3.8 EndY=34.25 EndZ=0
    g7: Circle CenterX=-3.8 CenterY=29.05 CenterZ=0 NormalX=0 NormalY=0 NormalZ=1 AngleXU=0 Radius=2
  constraints (20):
    c: Vertical(g0)
    c: Coincident(g0,g1)
    c: PointOnObject(g1,g-1)
    c: Coincident(g1,g2)
    c: Vertical(g2)
    c: Coincident(g2,g3)
    c: Symmetric(g0,g1,g-2)
    c: PointOnObject(g5,g0)
    c: PointOnObject(g5,g3)
    c: Tangent(g0,g4) = -1.5708
    c: Tangent(g3,g4) = -1.5708
    c: PointOnObject(g6,g-2)
    c: Tangent(g6,g4) = -1.5708
    c: Horizontal(g6)
    c: DistanceY(g6) = 34.25
    c: DistanceX(g0,g1) = 18
    c: DistanceY(g2,g2) = 21.4
    c: Radius(g4) = 5.2
    c: Coincident(g7,g4)
    c: Diameter(g7) = 4
FEATURE [Part::FeaturePython] Array  # Draft array (typed FeaturePython)
  Angle = 360
  ArrayType = 1
  Axis = (0,0,1)
  Base = -> Sketch003
  Center = (0,0,0)
  Count = 2
  Fuse = true
  IntervalAxis = (0,0,0)
  IntervalX = (50,0,0)
  IntervalY = (0,50,0)
  IntervalZ = (0,0,50)
  NumberCircles = 3
  NumberPolar = 2
  NumberX = 2
  NumberY = 2
  NumberZ = 1
  RadialDistance = 50
  Symmetry = 1
  TangentialDistance = 25
note: 1 file-system path scrubbed to <path> (originals preserved in the JSON sidecar)
---- part ../dropper.FCStd = doc fcstd_03601a3bb068 ----
FCSTD DOCUMENT  (FreeCAD 1.1R38827 (Git))
Label: dropper
License: All rights reserved
LicenseURL: http://en.wikipedia.org/wiki/All_rights_reserved
objects: Sketcher::SketchObject×9, Part::FeaturePython×4, PartDesign::Revolution×3, PartDesign::Body×2, PartDesign::CoordinateSystem×1, Spreadsheet::Sheet×1, PartDesign::SubShapeBinder×1, PartDesign::Pad×1, PartDesign::Pocket×1, PartDesign::Groove×1, App::Part×1
note: 44 computed .brp shape members not serialized (recipe doc carries the construction recipe); baked Part::Feature solids carry a one-line shape summary decoded from their .brp

FEATURE [Sketcher::SketchObject] Sketch005
  ArcFitTolerance = 0
  AttachmentSupport = -> [YZ_Plane001]
  FullyConstrained = true
  MakeInternals = false
  MapMode = 5
  Placement = pos=(0,0,0) rot=(0.57735,0.57735,0.57735;2.0944rad)
  sketch-geometry (14):
    g0: LineSegment StartX=11.3 StartY=0 StartZ=0 EndX=11.3 EndY=1 EndZ=0
    g1: LineSegment StartX=11.3 StartY=1 StartZ=0 EndX=10.7 EndY=1 EndZ=0
    g2: LineSegment StartX=10.7 StartY=1 StartZ=0 EndX=10.7 EndY=9.9 EndZ=0
    g3: LineSegment StartX=10.7 StartY=9.9 StartZ=0 EndX=6.6 EndY=9.9 EndZ=0
    g4: LineSegment StartX=6.6 StartY=9.9 StartZ=0 EndX=6.6 EndY=3 EndZ=0
    g5: LineSegment StartX=6.6 StartY=3 StartZ=0 EndX=2.5 EndY=3 EndZ=0
    g6: LineSegment StartX=2.5 StartY=3 StartZ=0 EndX=2.5 EndY=20 EndZ=0
    g7: LineSegment StartX=2.5 StartY=20 StartZ=0 EndX=1.45 EndY=20 EndZ=0
    g8: LineSegment StartX=1.45 StartY=20 StartZ=0 EndX=1.45 EndY=2.5 EndZ=0
    g9: LineSegment StartX=1.45 StartY=2.5 StartZ=0 EndX=7 EndY=-0.6 EndZ=0
    g10: LineSegment StartX=7 StartY=-0.6 StartZ=0 EndX=7 EndY=8.85 EndZ=0
    g11: LineSegment StartX=7 StartY=8.85 StartZ=0 EndX=9.5 EndY=8.85 EndZ=0
    g12: LineSegment StartX=9.5 StartY=8.85 StartZ=0 EndX=9.5 EndY=0 EndZ=0
    g13: LineSegment StartX=9.5 StartY=0 StartZ=0 EndX=11.3 EndY=0 EndZ=0
  constraints (43):
    c: PointOnObject(g0,g-1)
    c: Vertical(g0)
    c: Coincident(g0,g1)
    c: Horizontal(g1)
    c: Coincident(g1,g2)
    c: Vertical(g2)
    c: Coincident(g2,g3)
    c: Horizontal(g3)
    c: Coincident(g3,g4)
    c: Vertical(g4)
    c: Coincident(g4,g5)
    c: Coincident(g5,g6)
    c: Vertical(g6)
    c: Coincident(g6,g7)
    c: Horizontal(g7)
    c: Coincident(g7,g8)
    c: Vertical(g8)
    c: Coincident(g8,g9)
    c: Coincident(g9,g10)
    c: Vertical(g10)
    c: Coincident(g10,g11)
    c: Horizontal(g11)
    c: Coincident(g11,g12)
    c: Vertical(g12)
    c: Coincident(g12,g13)
    c: Coincident(g13,g0)
    c: Horizontal(g13)
    c: DistanceX(g0) = 11.3  'outer_r'
    c: DistanceY(g0) = 1
    c: DistanceY(g2) = 9.9
    c: DistanceX(g1,g0) = 0.6
    c: DistanceX(g3,g2) = 4.1
    c: DistanceY(g4,g3) = 6.9
    c: DistanceX(g6) = 2.5
    c: DistanceX(g7) = 1.45
    c: DistanceY(g9,g3) = 10.5
    c: DistanceX(g12,g0) = 1.8
    c: DistanceY(g11) = 8.85
    c: DistanceX(g9) = 7
    c: DistanceY(g9,g6) = 20.6
    c: Horizontal(g5)
    c: DistanceY(g8,g5) = 0.5
    c: DistanceY(g7) = 20
FEATURE [PartDesign::Revolution] Revolution002
  Angle = 360
  Angle2 = 60
  Axis = (0,0,1)
  Base = (0,0,0)
  Placement = pos=(0,0,0) rot=(1,1,1;2.0944rad)
  Profile = -> Sketch005
  ReferenceAxis = -> Sketch005 [V_Axis]
  Reversed = true
  Suppressed = false
  Type = 0
FEATURE [Sketcher::SketchObject] Sketch006
  ArcFitTolerance = 0
  AttachmentSupport = -> [YZ_Plane001]
  FullyConstrained = true
  MakeInternals = false
  MapMode = 5
  Placement = pos=(0,0,0) rot=(0.57735,0.57735,0.57735;2.0944rad)
  expr: Constraints[27] = Sketch005.Constraints.outer_r
  expr: Constraints[28] = Sketch005.Constraints[28]
  expr: Constraints[29] = Sketch005.Constraints[29]
  expr: Constraints[30] = Sketch005.Constraints[30]
  expr: Constraints[31] = Sketch005.Constraints[31]
  expr: Constraints[32] = Sketch005.Constraints[32]
  expr: Constraints[33] = Sketch005.Constraints[33]
  expr: Constraints[34] = Sketch005.Constraints[34]
  expr: Constraints[35] = Sketch005.Constraints[35]
  expr: Constraints[36] = Sketch005.Constraints[36]
  expr: Constraints[37] = Sketch005.Constraints[37]
  expr: Constraints[38] = Sketch005.Constraints[38]
  expr: Constraints[39] = Sketch005.Constraints[39]
  expr: Constraints[41] = Sketch005.Constraints[41]
  expr: Constraints[69] = Sketch005.Constraints.outer_r
  expr: Constraints[70] = Sketch005.Constraints[28]
  expr: Constraints[71] = Sketch005.Constraints[29]
  expr: Constraints[72] = Sketch005.Constraints[30]
  expr: Constraints[73] = Sketch005.Constraints[31]
  expr: Constraints[74] = Sketch005.Constraints[32]
  expr: Constraints[75] = Sketch005.Constraints[33]
  expr: Constraints[76] = Sketch005.Constraints[34]
  expr: Constraints[77] = Sketch005.Constraints[35]
  expr: Constraints[78] = Sketch005.Constraints[36]
  expr: Constraints[79] = Sketch005.Constraints[37]
  expr: Constraints[80] = Sketch005.Constraints[38]
  expr: Constraints[81] = Sketch005.Constraints[39]
  expr: Constraints[83] = Sketch005.Constraints[41]
  sketch-geometry (32):
    g0: LineSegment [constr] StartX=11.3 StartY=0 StartZ=0 EndX=11.3 EndY=1 EndZ=0
    g1: LineSegment [constr] StartX=11.3 StartY=1 StartZ=0 EndX=10.7 EndY=1 EndZ=0
    g2: LineSegment [constr] StartX=10.7 StartY=1 StartZ=0 EndX=10.7 EndY=9.9 EndZ=0
    g3: LineSegment [constr] StartX=10.7 StartY=9.9 StartZ=0 EndX=6.6 EndY=9.9 EndZ=0
    g4: LineSegment StartX=6.6 StartY=9.9 StartZ=0 EndX=6.6 EndY=3 EndZ=0
    g5: LineSegment StartX=6.6 StartY=3 StartZ=0 EndX=2.5 EndY=3 EndZ=0
    g6: LineSegment [constr] StartX=2.5 StartY=3 StartZ=0 EndX=2.5 EndY=20 EndZ=0
    g7: LineSegment [constr] StartX=2.5 StartY=20 StartZ=0 EndX=1.45 EndY=20 EndZ=0
    g8: LineSegment [constr] StartX=1.45 StartY=20 StartZ=0 EndX=1.45 EndY=2.5 EndZ=0
    g9: LineSegment [constr] StartX=1.45 StartY=2.5 StartZ=0 EndX=7 EndY=-0.6 EndZ=0
    g10: LineSegment [constr] StartX=7 StartY=-0.6 StartZ=0 EndX=7 EndY=8.85 EndZ=0
    g11: LineSegment [constr] StartX=7 StartY=8.85 StartZ=0 EndX=9.5 EndY=8.85 EndZ=0
    g12: LineSegment [constr] StartX=9.5 StartY=8.85 StartZ=0 EndX=9.5 EndY=0 EndZ=0
    g13: LineSegment [constr] StartX=9.5 StartY=0 StartZ=0 EndX=11.3 EndY=0 EndZ=0
    g14: LineSegment [constr] StartX=11.3 StartY=0 StartZ=0 EndX=11.3 EndY=1 EndZ=0
    g15: LineSegment [constr] StartX=11.3 StartY=1 StartZ=0 EndX=10.7 EndY=1 EndZ=0
    g16: LineSegment [constr] StartX=10.7 StartY=1 StartZ=0 EndX=10.7 EndY=9.9 EndZ=0
    g17: LineSegment [constr] StartX=10.7 StartY=9.9 StartZ=0 EndX=6.6 EndY=9.9 EndZ=0
    g18: LineSegment [constr] StartX=6.6 StartY=9.9 StartZ=0 EndX=6.6 EndY=3 EndZ=0
    g19: LineSegment [constr] StartX=6.6 StartY=3 StartZ=0 EndX=2.5 EndY=3 EndZ=0
    g20: LineSegment [constr] StartX=2.5 StartY=3 StartZ=0 EndX=2.5 EndY=20 EndZ=0
    g21: LineSegment [constr] StartX=2.5 StartY=20 StartZ=0 EndX=1.45 EndY=20 EndZ=0
    g22: LineSegment [constr] StartX=1.45 StartY=20 StartZ=0 EndX=1.45 EndY=2.5 EndZ=0
    g23: LineSegment [constr] StartX=1.45 StartY=2.5 StartZ=0 EndX=7 EndY=-0.6 EndZ=0
    g24: LineSegment [constr] StartX=7 StartY=-0.6 StartZ=0 EndX=7 EndY=8.85 EndZ=0
    g25: LineSegment [constr] StartX=7 StartY=8.85 StartZ=0 EndX=9.5 EndY=8.85 EndZ=0
    g26: LineSegment [constr] StartX=9.5 StartY=8.85 StartZ=0 EndX=9.5 EndY=0 EndZ=0
    g27: LineSegment [constr] StartX=9.5 StartY=0 StartZ=0 EndX=11.3 EndY=0 EndZ=0
    g28: LineSegment StartX=2.5 StartY=3 StartZ=0 EndX=2.04763 EndY=3 EndZ=0
    g29: LineSegment StartX=2.04763 StartY=3 StartZ=0 EndX=2.04763 EndY=12.6758 EndZ=0
    g30: LineSegment StartX=2.04763 StartY=12.6758 StartZ=0 EndX=6.6 EndY=9.9 EndZ=0
    g31: GeomPoint [constr] X=2.5 Y=12.4 Z=0
  constraints (94):
    c: PointOnObject(g0,g-1)
    c: Vertical(g0)
    c: Coincident(g0,g1)
    c: Horizontal(g1)
    c: Coincident(g1,g2)
    c: Vertical(g2)
    c: Coincident(g2,g3)
    c: Horizontal(g3)
    c: Coincident(g3,g4)
    c: Vertical(g4)
    c: Coincident(g4,g5)
    c: Coincident(g5,g6)
    c: Vertical(g6)
    c: Coincident(g6,g7)
    c: Horizontal(g7)
    c: Coincident(g7,g8)
    c: Vertical(g8)
    c: Coincident(g8,g9)
    c: Coincident(g9,g10)
    c: Vertical(g10)
    c: Coincident(g10,g11)
    c: Horizontal(g11)
    c: Coincident(g11,g12)
    c: Vertical(g12)
    c: Coincident(g12,g13)
    c: Coincident(g13,g0)
    c: Horizontal(g13)
    c: DistanceX(g0) = 11.3
    c: DistanceY(g0) = 1
    c: DistanceY(g2) = 9.9
    c: DistanceX(g1,g0) = 0.6
    c: DistanceX(g3,g2) = 4.1
    c: DistanceY(g4,g3) = 6.9
    c: DistanceX(g6) = 2.5
    c: DistanceX(g7) = 1.45
    c: DistanceY(g9,g3) = 10.5
    c: DistanceX(g12,g0) = 1.8
    c: DistanceY(g11) = 8.85
    c: DistanceX(g9) = 7
    c: DistanceY(g9,g6) = 20.6
    c: Horizontal(g5)
    c: DistanceY(g8,g5) = 0.5
    c: PointOnObject(g14,g-1)
    c: Vertical(g14)
    c: Coincident(g14,g15)
    c: Horizontal(g15)
    c: Coincident(g15,g16)
    c: Vertical(g16)
    c: Coincident(g16,g17)
    c: Horizontal(g17)
    c: Coincident(g17,g18)
    c: Vertical(g18)
    c: Coincident(g18,g19)
    c: Coincident(g19,g20)
    c: Vertical(g20)
    c: Coincident(g20,g21)
    c: Horizontal(g21)
    c: Coincident(g21,g22)
    c: Vertical(g22)
    c: Coincident(g22,g23)
    c: Coincident(g23,g24)
    c: Vertical(g24)
    c: Coincident(g24,g25)
    c: Horizontal(g25)
    c: Coincident(g25,g26)
    c: Vertical(g26)
    c: Coincident(g26,g27)
    c: Coincident(g27,g14)
    c: Horizontal(g27)
    c: DistanceX(g14) = 11.3
    c: DistanceY(g14) = 1
    c: DistanceY(g16) = 9.9
    c: DistanceX(g15,g14) = 0.6
    c: DistanceX(g17,g16) = 4.1
    c: DistanceY(g18,g17) = 6.9
    c: DistanceX(g20) = 2.5
    c: DistanceX(g21) = 1.45
    c: DistanceY(g23,g17) = 10.5
    c: DistanceX(g26,g14) = 1.8
    c: DistanceY(g25) = 8.85
    c: DistanceX(g23) = 7
    c: DistanceY(g23,g20) = 20.6
    c: Horizontal(g19)
    c: DistanceY(g22,g19) = 0.5
    c: Coincident(g28,g5)
    c: Horizontal(g28)
    c: Coincident(g29,g28)
    c: Vertical(g29)
    c: Coincident(g30,g29)
    c: Coincident(g30,g4)
    c: PointOnObject(g31,g30)
    c: PointOnObject(g31,g6)
    c: DistanceY(g4,g31) = 2.5
    c: DistanceX(g29,g31) = 0.452366
FEATURE [PartDesign::Body] Body001
  AllowCompound = false
  Group = -> [Sketch005,Revolution002,Sketch006]
  Origin = -> Origin001
  Placement = pos=(0,0,2.5) rot=(0,0,1;0rad)
  Tip = -> Revolution002
FEATURE [Sketcher::SketchObject] Sketch007  label="base"
  ArcFitTolerance = 0
  FullyConstrained = true
  MakeInternals = false
  expr: .Constraints.r = Sketch005.Constraints.outer_r + 0.5 mm
  sketch-geometry (1):
    g0: Circle CenterX=0 CenterY=0 CenterZ=0 NormalX=0 NormalY=0 NormalZ=1 AngleXU=0 Radius=11.8
  constraints (2):
    c: Coincident(g0,g-1)
    c: Radius(g0) = 11.8  'r'
FEATURE [Sketcher::SketchObject] Sketch002
  ArcFitTolerance = 0
  AttachmentSupport = -> [YZ_Plane]
  FullyConstrained = true
  MakeInternals = false
  MapMode = 5
  Placement = pos=(0,0,0) rot=(0.57735,0.57735,0.57735;2.0944rad)
  expr: Constraints[18] = Sketch001.Constraints[18]
  expr: Constraints[19] = Sketch001.Constraints[19]
  expr: Constraints[20] = Sketch001.Constraints[20]
  expr: Constraints[21] = Sketch001.Constraints[21]
  expr: Constraints[22] = Sketch001.Constraints[22]
  expr: Constraints[23] = Sketch001.Constraints[23]
  expr: Constraints[24] = Sketch001.Constraints[24]
  expr: Constraints[25] = Sketch001.Constraints[25]
  expr: Constraints[27] = Sketch001.Constraints[27]
  sketch-geometry (13):
    g0: LineSegment [constr] StartX=1.15 StartY=0 StartZ=0 EndX=1.15 EndY=-18.1612 EndZ=0
    g1: LineSegment StartX=1.15 StartY=-18.1612 StartZ=0 EndX=2.765 EndY=-8.77 EndZ=0
    g2: LineSegment [constr] StartX=2.765 StartY=-8.77 StartZ=0 EndX=2.2 EndY=-8.77 EndZ=0
    g3: LineSegment [constr] StartX=2.2 StartY=-8.77 StartZ=0 EndX=2.2 EndY=-5.32 EndZ=0
    g4: LineSegment [constr] StartX=2.2 StartY=-5.32 StartZ=0 EndX=3.35 EndY=-5.32 EndZ=0
    g5: LineSegment [constr] StartX=3.35 StartY=-5.32 StartZ=0 EndX=3.35 EndY=-3.66 EndZ=0
    g6: LineSegment [constr] StartX=3.35 StartY=-3.66 StartZ=0 EndX=2.65 EndY=-3.66 EndZ=0
    g7: LineSegment [constr] StartX=2.65 StartY=-3.66 StartZ=0 EndX=2.65 EndY=0 EndZ=0
    g8: LineSegment [constr] StartX=2.65 StartY=0 StartZ=0 EndX=1.15 EndY=0 EndZ=0
    g9: GeomPoint [constr] X=-2.765 Y=-8.77 Z=0
    g10: GeomPoint [constr] X=-2.765 Y=-8.77 Z=0
    g11: LineSegment StartX=1.15 StartY=-18.1612 StartZ=0 EndX=-3.0574 EndY=-18.1612 EndZ=0
    g12: LineSegment StartX=-3.0574 StartY=-18.1612 StartZ=0 EndX=2.765 EndY=-8.77 EndZ=0
  constraints (34):
    c: PointOnObject(g0,g-1)
    c: Vertical(g0)
    c: Coincident(g0,g1)
    c: Coincident(g1,g2)
    c: Horizontal(g2)
    c: Coincident(g2,g3)
    c: Vertical(g3)
    c: Coincident(g3,g4)
    c: Horizontal(g4)
    c: Coincident(g4,g5)
    c: Vertical(g5)
    c: Coincident(g5,g6)
    c: Horizontal(g6)
    c: Coincident(g6,g7)
    c: PointOnObject(g7,g-1)
    c: Vertical(g7)
    c: Coincident(g7,g8)
    c: Coincident(g8,g0)
    c: DistanceY(g2,g3) = 3.45
    c: DistanceY(g4,g5) = 1.66
    c: DistanceY(g6,g7) = 3.66
    c: DistanceX(g2) = 2.2
    c: DistanceX(g4) = 3.35
    c: DistanceX(g0) = 1.15
    c: DistanceX(g7) = 2.65
    c: DistanceX(g1) = 2.765
    c: Symmetric(g9,g1,g-2)
    c: Distance(g9,g1) = 5.45
    c: Symmetric(g10,g1,g-2)
    c: Coincident(g11,g1)
    c: Horizontal(g11)
    c: Coincident(g12,g11)
    c: Coincident(g12,g1)
    c: Distance(g9,g12) = 4.7
FEATURE [Sketcher::SketchObject] Sketch001
  ArcFitTolerance = 0
  AttachmentSupport = -> [XZ_Plane]
  FullyConstrained = true
  MakeInternals = false
  MapMode = 5
  Placement = pos=(0,0,0) rot=(1,0,0;1.5708rad)
  sketch-geometry (10):
    g0: LineSegment StartX=1.15 StartY=0 StartZ=0 EndX=1.15 EndY=-18.1612 EndZ=0
    g1: LineSegment StartX=1.15 StartY=-18.1612 StartZ=0 EndX=2.765 EndY=-8.77 EndZ=0
    g2: LineSegment StartX=2.765 StartY=-8.77 StartZ=0 EndX=2.2 EndY=-8.77 EndZ=0
    g3: LineSegment StartX=2.2 StartY=-8.77 StartZ=0 EndX=2.2 EndY=-5.32 EndZ=0
    g4: LineSegment StartX=2.2 StartY=-5.32 StartZ=0 EndX=3.35 EndY=-5.32 EndZ=0
    g5: LineSegment StartX=3.35 StartY=-5.32 StartZ=0 EndX=3.35 EndY=-3.66 EndZ=0
    g6: LineSegment StartX=3.35 StartY=-3.66 StartZ=0 EndX=2.65 EndY=-3.66 EndZ=0
    g7: LineSegment StartX=2.65 StartY=-3.66 StartZ=0 EndX=2.65 EndY=0 EndZ=0
    g8: LineSegment StartX=2.65 StartY=0 StartZ=0 EndX=1.15 EndY=0 EndZ=0
    g9: GeomPoint [constr] X=-2.765 Y=-8.77 Z=0
  constraints (28):
    c: PointOnObject(g0,g-1)
    c: Vertical(g0)
    c: Coincident(g0,g1)
    c: Coincident(g1,g2)
    c: Horizontal(g2)
    c: Coincident(g2,g3)
    c: Vertical(g3)
    c: Coincident(g3,g4)
    c: Horizontal(g4)
    c: Coincident(g4,g5)
    c: Vertical(g5)
    c: Coincident(g5,g6)
    c: Horizontal(g6)
    c: Coincident(g6,g7)
    c: PointOnObject(g7,g-1)
    c: Vertical(g7)
    c: Coincident(g7,g8)
    c: Coincident(g8,g0)
    c: DistanceY(g2,g3) = 3.45
    c: DistanceY(g4,g5) = 1.66
    c: DistanceY(g6,g7) = 3.66
    c: DistanceX(g2) = 2.2
    c: DistanceX(g4) = 3.35
    c: DistanceX(g0) = 1.15
    c: DistanceX(g7) = 2.65
    c: DistanceX(g1) = 2.765
    c: Symmetric(g9,g1,g-2)
    c: Distance(g9,g1) = 5.45
FEATURE [Sketcher::SketchObject] Sketch  label="fix_sketch"
  ArcFitTolerance = 0
  AttachmentSupport = -> [XY_Plane]
  FullyConstrained = true
  MakeInternals = false
  MapMode = 5
  sketch-geometry (5):
    g0: ArcOfCircle CenterX=0 CenterY=0 CenterZ=0 NormalX=0 NormalY=0 NormalZ=1 AngleXU=0 Radius=10.5 StartAngle=0.496317 EndAngle=1.5708
    g1: ArcOfCircle CenterX=16.5 CenterY=0 CenterZ=0 NormalX=0 NormalY=0 NormalZ=1 AngleXU=0 Radius=3.25 StartAngle=0 EndAngle=1.34547
    g2: LineSegment StartX=17.2261 StartY=3.16784 StartZ=0 EndX=9.23309 EndY=5 EndZ=0
    g3: GeomPoint [constr] X=-19.75 Y=0 Z=0
    g4: GeomPoint [constr] X=0 Y=-10.5 Z=0
  constraints (14):
    c: PointOnObject(g0,g-2)
    c: PointOnObject(g1,g-1)
    c: PointOnObject(g1,g-1)
    c: Coincident(g2,g0)
    c: Tangent(g2,g1) = -1.5708
    c: Diameter(g0) = 21
    c: DistanceX(g1) = 19.75
    c: DistanceY(g0) = 5
    c: Diameter(g1) = 6.5
    c: Coincident(g0,g-1)
    c: Symmetric(g3,g1,g-2)
    c: DistanceX(g3,g1) = 39.5  'length'
    c: Symmetric(g4,g0,g-1)
    c: DistanceY(g4,g0) = 21  'width'
FEATURE [Sketcher::SketchObject] Sketch004
  ArcFitTolerance = 0
  AttachmentSupport = -> [YZ_Plane]
  FullyConstrained = true
  MakeInternals = false
  MapMode = 5
  Placement = pos=(0,0,0) rot=(0.57735,0.57735,0.57735;2.0944rad)
  expr: Constraints[3] = Sketch003.Constraints[9]
  sketch-geometry (6):
    g0: LineSegment StartX=7.75 StartY=10.9 StartZ=0 EndX=0 EndY=10.9 EndZ=0
    g1: LineSegment StartX=0 StartY=10.9 StartZ=0 EndX=0 EndY=1.5 EndZ=0
    g2: LineSegment StartX=0 StartY=1.5 StartZ=0 EndX=7.25 EndY=1.5 EndZ=0
    g3: LineSegment StartX=7.25 StartY=1.5 StartZ=0 EndX=7.25 EndY=2.5 EndZ=0
    g4: LineSegment StartX=7.25 StartY=2.5 StartZ=0 EndX=7.75 EndY=4 EndZ=0
    g5: LineSegment StartX=7.75 StartY=4 StartZ=0 EndX=7.75 EndY=10.9 EndZ=0
  constraints (18):
    c: Coincident(g0,g1)
    c: Horizontal(g0)
    c: Vertical(g1)
    c: DistanceY(g0) = 10.9
    c: Horizontal(g2)
    c: Coincident(g2,g3)
    c: Vertical(g3)
    c: Coincident(g3,g4)
    c: Coincident(g4,g5)
    c: Vertical(g5)
    c: Coincident(g0,g5)
    c: Coincident(g1,g2)
    c: DistanceY(g1,g0) = 9.4
    c: DistanceX(g0) = 7.75
    c: DistanceY(g2,g3) = 1
    c: DistanceY(g3,g4) = 1.5
    c: DistanceX(g2,g4) = 0.5
    c: Vertical(g1,g-1)
FEATURE [Sketcher::SketchObject] Sketch003
  ArcFitTolerance = 0
  AttachmentSupport = -> [YZ_Plane]
  FullyConstrained = true
  MakeInternals = false
  MapMode = 5
  Placement = pos=(0,0,0) rot=(0.57735,0.57735,0.57735;2.0944rad)
  sketch-geometry (4):
    g0: LineSegment StartX=0 StartY=0 StartZ=0 EndX=8.825 EndY=0 EndZ=0
    g1: LineSegment StartX=8.825 StartY=0 StartZ=0 EndX=8.825 EndY=10.9 EndZ=0
    g2: LineSegment StartX=8.825 StartY=10.9 StartZ=0 EndX=0 EndY=10.9 EndZ=0
    g3: LineSegment StartX=0 StartY=10.9 StartZ=0 EndX=0 EndY=0 EndZ=0
  constraints (11):
    c: Coincident(g0,g1)
    c: Coincident(g1,g2)
    c: Coincident(g2,g3)
    c: Coincident(g3,g0)
    c: Horizontal(g0)
    c: Horizontal(g2)
    c: Vertical(g1)
    c: Vertical(g3)
    c: Coincident(g0,g-1)
    c: DistanceY(g2) = 10.9
    c: DistanceX(g0) = 8.825
FEATURE [PartDesign::CoordinateSystem] LCS_0
  AttacherType = Attacher::AttachEngine3D
  AttachmentOffset = pos=(0,0,2.45) rot=(0,0,1;0rad)
  AttachmentSupport = -> [X_Axis002]
  MapMode = 2
  Placement = pos=(0,0,2.45) rot=(0,0,1;0rad)
FEATURE [Spreadsheet::Sheet] Spreadsheet  label="Properties"
  cells = B2(top_d)==22.6 mm; C2(bot_d)==21 mm; D2(top_height)==20 mm; E2(bot_base_height)==2.4 mm; F2(total_height)==22.4 mm; G2(total_width)==38.9 mm
FEATURE [Part::FeaturePython] Mirror  label="Mirror of Sketch"  # WARN: FeaturePython — macro-defined, semantics opaque (R4)
  ExposePlacement = false
  FlipX = true
  FlipY = false
  FlipZ = false
  MarkerShape = 1
  MarkerSize = 0
  NumElements = 0
  Object = -> Sketch
  ObjectTraversal = 0
  Type = lattice2Mirror.LatticeMirror
  isLattice = 0
FEATURE [Part::FeaturePython] Mirror001  label="Mirror001 of Mirror of Sketch"  # WARN: FeaturePython — macro-defined, semantics opaque (R4)
  ExposePlacement = false
  FlipX = false
  FlipY = true
  FlipZ = false
  MarkerShape = 1
  MarkerSize = 0
  NumElements = 0
  Object = -> Mirror
  ObjectTraversal = 0
  Type = lattice2Mirror.LatticeMirror
  isLattice = 0
FEATURE [Part::FeaturePython] Mirror002  label="Mirror002 of Mirror001 of Mirror of Sketch"  # WARN: FeaturePython — macro-defined, semantics opaque (R4)
  ExposePlacement = false
  FlipX = true
  FlipY = false
  FlipZ = false
  MarkerShape = 1
  MarkerSize = 0
  NumElements = 0
  Object = -> Mirror001
  ObjectTraversal = 0
  Type = lattice2Mirror.LatticeMirror
  isLattice = 0
FEATURE [PartDesign::SubShapeBinder] Binder
  BindCopyOnChange = 0
  BindMode = 0
  ClaimChildren = true
  Context = -> Part [Body.Binder.]
  Fuse = false
  MakeFace = true
  OffsetFill = false
  OffsetIntersection = false
  OffsetJoinType = 0
  OffsetOpenResult = false
  PartialLoad = false
  Relative = true
  Support = -> [Connect]
  _Version = 2
FEATURE [PartDesign::Pad] Pad
  Direction = (0,0,1)
  Length = 2.45
  Length2 = 10
  Profile = -> Binder
  Suppressed = false
  Type = 0
FEATURE [PartDesign::Revolution] Revolution
  Angle = 360
  Angle2 = 60
  Axis = (0,2e-16,1)
  Base = (0,0,0)
  BaseFeature = -> Pad
  Profile = -> Sketch001
  ReferenceAxis = -> Sketch001 [V_Axis]
  Reversed = true
  Suppressed = false
  Type = 0
FEATURE [PartDesign::Pocket] Pocket
  BaseFeature = -> Revolution
  Direction = (-1,0,0)
  Length = 5
  Length2 = 5
  Midplane = true
  Profile = -> Sketch002
  ReferenceAxis = -> Sketch002 [N_Axis]
  Suppressed = false
  Type = 1
FEATURE [PartDesign::Revolution] Revolution001
  Angle = 360
  Angle2 = 60
  Axis = (0,0,1)
  Base = (0,0,0)
  BaseFeature = -> Pocket
  Profile = -> Sketch003
  ReferenceAxis = -> Sketch003 [V_Axis]
  Reversed = true
  Suppressed = false
  Type = 0
FEATURE [PartDesign::Groove] Groove
  Angle = 360
  Angle2 = 60
  Axis = (0,0,1)
  Base = (0,0,0)
  BaseFeature = -> Revolution001
  Profile = -> Sketch004
  ReferenceAxis = -> Sketch004 [V_Axis]
  Suppressed = false
  Type = 0
FEATURE [Sketcher::SketchObject] Sketch008  label="feed"
  ArcFitTolerance = 0
  AttachmentSupport = -> [XY_Plane]
  FullyConstrained = true
  MakeInternals = false
  MapMode = 5
  sketch-geometry (1):
    g0: Circle CenterX=0 CenterY=0 CenterZ=0 NormalX=0 NormalY=0 NormalZ=1 AngleXU=0 Radius=4
  constraints (2):
    c: Coincident(g0,g-1)
    c: Diameter(g0) = 8
FEATURE [PartDesign::Body] Body
  AllowCompound = false
  Group = -> [Sketch,Pad,Sketch001,Revolution,Sketch002,Pocket,Sketch003,Sketch004,Revolution001,Groove,Sketch008,Binder]
  Origin = -> Origin
  Tip = -> Groove
FEATURE [App::Part] Part  label="dropper"
  Group = -> [LCS_0,Body001,Body]
  Origin = -> Origin002
FEATURE [Part::FeaturePython] Connect  label="fix"  # WARN: FeaturePython — macro-defined, semantics opaque (R4)
  Objects = -> [Sketch,Mirror002,Mirror001,Mirror]
  Tolerance = 0
---- part ../hinge.FCStd = doc fcstd_00108e65cf5f ----
FCSTD DOCUMENT  (FreeCAD 0.22R36807 (Git))
Label: hinge
License: All rights reserved
LicenseURL: http://en.wikipedia.org/wiki/All_rights_reserved
objects: Sketcher::SketchObject×4, PartDesign::Pocket×3, PartDesign::SubShapeBinder×2, App::Link×2, App::Part×2, App::FeaturePython×2, PartDesign::FeaturePython×1, Assembly::JointGroup×1, Assembly::AssemblyObject×1, PartDesign::CoordinateSystem×1, PartDesign::Line×1, PartDesign::Body×1
note: 16 computed .brp shape members not serialized (recipe doc carries the construction recipe); baked Part::Feature solids carry a one-line shape summary decoded from their .brp

FEATURE [Sketcher::SketchObject] Sketch
  FullyConstrained = true
  sketch-geometry (2):
    g0: Circle CenterX=14 CenterY=12.5 CenterZ=0 NormalX=0 NormalY=0 NormalZ=1 AngleXU=0 Radius=2.5
    g1: Circle CenterX=-14 CenterY=12.5 CenterZ=0 NormalX=0 NormalY=0 NormalZ=1 AngleXU=0 Radius=2.5
  constraints (5):
    c: Symmetric(g1,g0,g-2)
    c: DistanceY(g0) = 12.5
    c: DistanceX(g1,g0) = 28
    c: Equal(g1,g0)
    c: Diameter(g0) = 5
FEATURE [Sketcher::SketchObject] Sketch001
  FullyConstrained = true
  Placement = pos=(0,0,0) rot=(0.57735,0.57735,0.57735;2.0944rad)
  sketch-geometry (6):
    g0: ArcOfCircle CenterX=0 CenterY=3 CenterZ=0 NormalX=0 NormalY=0 NormalZ=1 AngleXU=0 Radius=3.65 StartAngle=6.18715 EndAngle=11.6016
    g1: LineSegment StartX=2.07906 StartY=0 StartZ=0 EndX=18.95 EndY=0 EndZ=0
    g2: LineSegment StartX=-3.65 StartY=0 StartZ=0 EndX=-3.65 EndY=3 EndZ=0
    g3: GeomPoint X=0 Y=6.65 Z=0
    g4: LineSegment StartX=0 StartY=1.65 StartZ=0 EndX=18.95 EndY=1.65 EndZ=0
    g5: LineSegment StartX=18.95 StartY=0 StartZ=0 EndX=18.95 EndY=1.65 EndZ=0
  constraints (19):
    c: PointOnObject(g0,g-2)
    c: PointOnObject(g0,g-1)
    c: Coincident(g1,g0)
    c: PointOnObject(g1,g-1)
    c: Diameter(g0) = 7.3
    c: PointOnObject(g2,g-1)
    c: Tangent(g2,g0) = 1.5708
    c: Vertical(g2)
    c: DistanceX(g2,g1) = 22.6
    c: PointOnObject(g3,g0)
    c: PointOnObject(g3,g-2)
    c: PointOnObject(g4,g-2)
    c: Horizontal(g4)
    c: Coincident(g5,g1)
    c: Coincident(g5,g4)
    c: Vertical(g5)
    c: DistanceY(g4,g3) = 5
    c: DistanceY(g4) = 1.65
    c: Distance(g0,g4) = 1
FEATURE [PartDesign::SubShapeBinder] Binder
  BindCopyOnChange = 0
  BindMode = 0
  ClaimChildren = true
  Context = -> Body [Binder.]
  Fuse = false
  MakeFace = true
  OffsetFill = false
  OffsetIntersection = false
  OffsetJoinType = 0
  OffsetOpenResult = false
  PartialLoad = false
  Placement = pos=(0,0,0) rot=(0.57735,0.57735,0.57735;2.0944rad)
  Relative = false
  Support = -> [Sketch001]
  _Version = 2
  expr: Placement = Support[0][0].Placement
FEATURE [PartDesign::FeaturePython] BaseBend  # WARN: FeaturePython — macro-defined, semantics opaque (R4)
  BendSide = 1
  BendSketch = -> Binder
  MidPlane = true
  Reverse = false
  Suppressed = false
  length = 40
  radius = 1
  thickness = 1.6
FEATURE [Sketcher::SketchObject] Sketch002
  AttachmentSupport = -> [XY_Plane]
  ExternalGeometry = -> [Binder]
  FullyConstrained = true
  MapMode = 5
  sketch-geometry (9):
    g0: LineSegment StartX=-20 StartY=0 StartZ=0 EndX=20 EndY=0 EndZ=0
    g1: LineSegment StartX=10 StartY=-3.65 StartZ=0 EndX=20 EndY=-3.65 EndZ=0
    g2: LineSegment StartX=20 StartY=-3.65 StartZ=0 EndX=20 EndY=3.65 EndZ=0
    g3: LineSegment StartX=20 StartY=3.65 StartZ=0 EndX=10 EndY=3.65 EndZ=0
    g4: LineSegment StartX=10 StartY=3.65 StartZ=0 EndX=10 EndY=-3.65 EndZ=0
    g5: LineSegment StartX=-10 StartY=-3.65 StartZ=0 EndX=0 EndY=-3.65 EndZ=0
    g6: LineSegment StartX=0 StartY=-3.65 StartZ=0 EndX=0 EndY=3.65 EndZ=0
    g7: LineSegment StartX=0 StartY=3.65 StartZ=0 EndX=-10 EndY=3.65 EndZ=0
    g8: LineSegment StartX=-10 StartY=3.65 StartZ=0 EndX=-10 EndY=-3.65 EndZ=0
  constraints (25):
    c: PointOnObject(g0,g-1)
    c: Symmetric(g0,g0,g-2)
    c: DistanceX(g0,g0) = 40
    c: Coincident(g1,g2)
    c: Coincident(g2,g3)
    c: Coincident(g3,g4)
    c: Coincident(g4,g1)
    c: Horizontal(g1)
    c: Horizontal(g3)
    c: Vertical(g2)
    c: Vertical(g4)
    c: Coincident(g5,g6)
    c: Coincident(g6,g7)
    c: Coincident(g7,g8)
    c: Coincident(g8,g5)
    c: Horizontal(g5)
    c: Horizontal(g7)
    c: Vertical(g8)
    c: Coincident(g6,g-3)
    c: Coincident(g5,g-3)
    c: Horizontal(g5,g1)
    c: PointOnObject(g0,g2)
    c: Horizontal(g3,g6)
    c: Equal(g3,g7)
    c: DistanceX(g7,g7) = 10
FEATURE [PartDesign::SubShapeBinder] Binder001
  BindCopyOnChange = 0
  BindMode = 0
  ClaimChildren = true
  Context = -> Body [Binder001.]
  Fuse = false
  MakeFace = true
  OffsetFill = false
  OffsetIntersection = false
  OffsetJoinType = 0
  OffsetOpenResult = false
  PartialLoad = false
  Relative = false
  Support = -> [Sketch]
  _Version = 2
FEATURE [App::Link] Body001
  LinkedObject = -> Body
FEATURE [App::Part] Part_Body  label="Part_Body 🔒"
  Group = -> [Body001]
  Origin = -> Origin002
FEATURE [App::FeaturePython] GroundedJoint  # Assembly grounded joint (typed FeaturePython)
  ObjectToGround = -> Part_Body
FEATURE [App::Link] Body002
  LinkedObject = -> Body
FEATURE [App::Part] Part_Body001
  Group = -> [Body002]
  Origin = -> Origin003
  Placement = pos=(-1.8e-15,-3e-16,4e-16) rot=(0,0,-1;3.14159rad)
FEATURE [PartDesign::Pocket] Pocket
  BaseFeature = -> BaseBend
  Direction = (0,0,-1)
  Length = 5
  Length2 = 5
  Midplane = true
  Profile = -> Sketch002
  ReferenceAxis = -> Sketch002 [N_Axis]
  Suppressed = false
  Type = 1
FEATURE [PartDesign::Pocket] Pocket001
  BaseFeature = -> Pocket
  Direction = (0,0,-1)
  Length = 5
  Length2 = 5
  Midplane = true
  Profile = -> Binder001
  Suppressed = false
  Type = 1
FEATURE [App::FeaturePython] Cylindrical  # Assembly joint (typed FeaturePython)
  Activated = true
  Detach1 = false
  Detach2 = false
  Distance = 0
  Element1 = Edge26
  Element2 = Face22
  JointType = 2 (Cylindrical)
  Object1 = Body001
  Object2 = Body002
  Offset = (0,0,0)
  Part1 = -> Part_Body
  Part2 = -> Part_Body001
  Placement1 = pos=(-10,0,3) rot=(-0.57735,-0.57735,0.57735;2.0944rad)
  Placement2 = pos=(10,0,3) rot=(0.57735,-0.57735,0.57735;4.18879rad)
  Rotation = 180
  Vertex1 = Edge26
  Vertex2 = Edge3
FEATURE [Assembly::JointGroup] Joints
  Group = -> [GroundedJoint,Cylindrical]
FEATURE [Assembly::AssemblyObject] Assembly
  Group = -> [Joints,Part_Body,GroundedJoint,Part_Body001,Cylindrical]
  Origin = -> Origin001
  Type = Assembly
FEATURE [Sketcher::SketchObject] Sketch003
  AttachmentSupport = -> [XY_Plane]
  ExternalGeometry = -> [Binder]
  FullyConstrained = true
  MapMode = 5
  sketch-geometry (7):
    g0: LineSegment StartX=-20 StartY=0 StartZ=0 EndX=20 EndY=0 EndZ=0
    g1: ArcOfCircle CenterX=15 CenterY=13.95 CenterZ=0 NormalX=0 NormalY=0 NormalZ=1 AngleXU=0 Radius=5 StartAngle=0 EndAngle=1.5708
    g2: ArcOfCircle CenterX=-15 CenterY=13.95 CenterZ=0 NormalX=0 NormalY=0 NormalZ=1 AngleXU=0 Radius=5 StartAngle=1.5708 EndAngle=3.14159
    g3: LineSegment StartX=-20 StartY=13.95 StartZ=0 EndX=-20 EndY=18.95 EndZ=0
    g4: LineSegment StartX=-20 StartY=18.95 StartZ=0 EndX=-15 EndY=18.95 EndZ=0
    g5: LineSegment StartX=20 StartY=13.95 StartZ=0 EndX=20 EndY=18.95 EndZ=0
    g6: LineSegment StartX=15 StartY=18.95 StartZ=0 EndX=20 EndY=18.95 EndZ=0
  constraints (19):
    c: PointOnObject(g0,g-1)
    c: Symmetric(g0,g0,g-2)
    c: DistanceX(g0,g0) = 40
    c: Tangent(g3,g2) = 1.5708
    c: Coincident(g4,g3)
    c: Tangent(g4,g2) = 1.5708
    c: Tangent(g5,g1) = -1.5708
    c: Vertical(g5)
    c: Coincident(g6,g5)
    c: Tangent(g6,g1) = 1.5708
    c: Horizontal(g6)
    c: Vertical(g3)
    c: Horizontal(g4)
    c: Equal(g2,g1)
    c: Vertical(g5,g0)
    c: Horizontal(g-3,g5)
    c: Horizontal(g5,g3)
    c: Vertical(g3,g0)
    c: Radius(g1) = 5
FEATURE [PartDesign::Pocket] Pocket002
  BaseFeature = -> Pocket001
  Direction = (0,0,-1)
  Length = 5
  Length2 = 5
  Midplane = true
  Profile = -> Sketch003
  ReferenceAxis = -> Sketch003 [N_Axis]
  Suppressed = false
  Type = 1
FEATURE [PartDesign::CoordinateSystem] Local_CS
  AttacherType = Attacher::AttachEngine3D
  AttachmentSupport = -> [XY_Plane]
  MapMode = 5
FEATURE [PartDesign::Line] DatumLine
  AttacherType = Attacher::AttachEngineLine
  AttachmentSupport = -> [Pocket002]
  Length = 20
  MapMode = 19
  Placement = pos=(0,-2e-16,3) rot=(-0.694186,-0.190294,0.694186;2.7655rad)
  ResizeMode = 0
FEATURE [PartDesign::Body] Body
  Group = -> [Binder,BaseBend,Sketch002,Pocket,Binder001,Pocket001,Sketch003,Pocket002,Local_CS,DatumLine]
  Origin = -> Origin
  Tip = -> Pocket002
---- part ../module.FCStd = doc fcstd_3955753b3a20 ----
FCSTD DOCUMENT  (FreeCAD 1.1R38827 (Git))
Label: module
License: All rights reserved
LicenseURL: http://en.wikipedia.org/wiki/All_rights_reserved
objects: Sketcher::SketchObject×2, Part::Feature×1, PartDesign::FeatureBase×1, PartDesign::Body×1, Spreadsheet::Sheet×1
note: 8 computed .brp shape members not serialized (recipe doc carries the construction recipe); baked Part::Feature solids carry a one-line shape summary decoded from their .brp

FEATURE [Part::Feature] Part__Feature  label="module002"
  shape: bbox 170 x 148 x 41.12 mm, 715 faces (baked)
FEATURE [Sketcher::SketchObject] Sketch  label="module_holes"
  ArcFitTolerance = 0
  FullyConstrained = true
  MakeInternals = false
  sketch-geometry (10):
    g0: LineSegment StartX=59.5 StartY=-3.5 StartZ=0 EndX=59.5 EndY=3.5 EndZ=0
    g1: LineSegment StartX=59.5 StartY=3.5 StartZ=0 EndX=72.5 EndY=3.5 EndZ=0
    g2: LineSegment StartX=72.5 StartY=3.5 StartZ=0 EndX=72.5 EndY=-3.5 EndZ=0
    g3: LineSegment StartX=72.5 StartY=-3.5 StartZ=0 EndX=59.5 EndY=-3.5 EndZ=0
    g4: GeomPoint [constr] X=66 Y=0 Z=0
    g5: LineSegment StartX=-72.5 StartY=-3.5 StartZ=0 EndX=-72.5 EndY=3.5 EndZ=0
    g6: LineSegment StartX=-72.5 StartY=3.5 StartZ=0 EndX=-59.5 EndY=3.5 EndZ=0
    g7: LineSegment StartX=-59.5 StartY=3.5 StartZ=0 EndX=-59.5 EndY=-3.5 EndZ=0
    g8: LineSegment StartX=-59.5 StartY=-3.5 StartZ=0 EndX=-72.5 EndY=-3.5 EndZ=0
    g9: GeomPoint [constr] X=-66 Y=0 Z=0
  constraints (25):
    c: Coincident(g0,g1)
    c: Coincident(g1,g2)
    c: Coincident(g2,g3)
    c: Coincident(g3,g0)
    c: Horizontal(g1)
    c: Horizontal(g3)
    c: Vertical(g0)
    c: Vertical(g2)
    c: Symmetric(g1,g0,g4)
    c: PointOnObject(g4,g-1)
    c: Coincident(g5,g6)
    c: Coincident(g6,g7)
    c: Coincident(g7,g8)
    c: Coincident(g8,g5)
    c: Horizontal(g6)
    c: Horizontal(g8)
    c: Vertical(g5)
    c: Vertical(g7)
    c: Symmetric(g6,g5,g9)
    c: Symmetric(g9,g4,g-2)
    c: Equal(g1,g6)
    c: Equal(g7,g2)
    c: DistanceX(g1,g1) = 13
    c: DistanceY(g2,g2) = 7
    c: DistanceX(g9,g4) = 132
FEATURE [PartDesign::FeatureBase] BaseFeature
  BaseFeature = -> Part__Feature
  Placement = pos=(0,0,0) rot=(0,0,1;1.5708rad)
  Suppressed = false
FEATURE [PartDesign::Body] Body  label="module_Body"
  AllowCompound = false
  BaseFeature = -> Part__Feature
  Group = -> [BaseFeature]
  Origin = -> Origin
  Tip = -> BaseFeature
FEATURE [Spreadsheet::Sheet] Spreadsheet  label="Properties"
  cells = B2(module_width)==148 mm; C2(module_height)==160 mm; D2(module_fixture_distance_x)==132 mm; E2(module_fixture_distance_y)==80 mm; F2(module_hole_x)==13 mm; G2(module_hole_y)==7 mm
FEATURE [Sketcher::SketchObject] Sketch001  label="module_holes001"
  ArcFitTolerance = 0
  FullyConstrained = true
  MakeInternals = false
  sketch-geometry (10):
    g0: LineSegment StartX=59 StartY=-3.5 StartZ=0 EndX=59 EndY=3.5 EndZ=0
    g1: LineSegment StartX=59 StartY=3.5 StartZ=0 EndX=73 EndY=3.5 EndZ=0
    g2: LineSegment StartX=73 StartY=3.5 StartZ=0 EndX=73 EndY=-3.5 EndZ=0
    g3: LineSegment StartX=73 StartY=-3.5 StartZ=0 EndX=59 EndY=-3.5 EndZ=0
    g4: GeomPoint [constr] X=66 Y=0 Z=0
    g5: LineSegment StartX=-73 StartY=-3.5 StartZ=0 EndX=-73 EndY=3.5 EndZ=0
    g6: LineSegment StartX=-73 StartY=3.5 StartZ=0 EndX=-59 EndY=3.5 EndZ=0
    g7: LineSegment StartX=-59 StartY=3.5 StartZ=0 EndX=-59 EndY=-3.5 EndZ=0
    g8: LineSegment StartX=-59 StartY=-3.5 StartZ=0 EndX=-73 EndY=-3.5 EndZ=0
    g9: GeomPoint [constr] X=-66 Y=0 Z=0
  constraints (25):
    c: Coincident(g0,g1)
    c: Coincident(g1,g2)
    c: Coincident(g2,g3)
    c: Coincident(g3,g0)
    c: Horizontal(g1)
    c: Horizontal(g3)
    c: Vertical(g0)
    c: Vertical(g2)
    c: Symmetric(g1,g0,g4)
    c: PointOnObject(g4,g-1)
    c: Coincident(g5,g6)
    c: Coincident(g6,g7)
    c: Coincident(g7,g8)
    c: Coincident(g8,g5)
    c: Horizontal(g6)
    c: Horizontal(g8)
    c: Vertical(g5)
    c: Vertical(g7)
    c: Symmetric(g6,g5,g9)
    c: Symmetric(g9,g4,g-2)
    c: Equal(g1,g6)
    c: Equal(g7,g2)
    c: DistanceX(g1,g1) = 14
    c: DistanceY(g2,g2) = 7
    c: DistanceX(g9,g4) = 132
